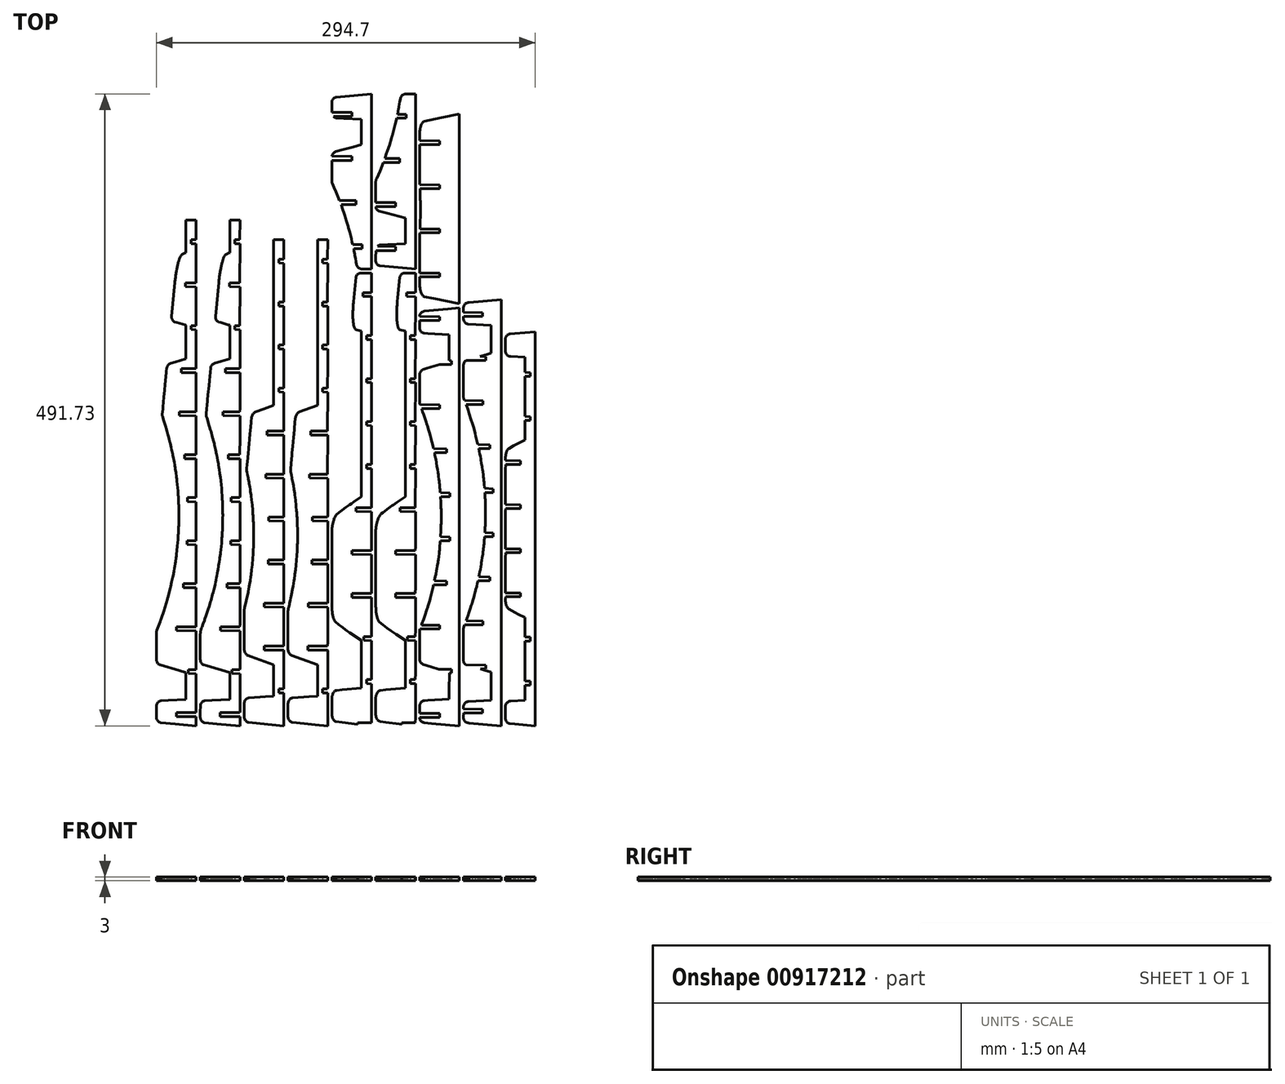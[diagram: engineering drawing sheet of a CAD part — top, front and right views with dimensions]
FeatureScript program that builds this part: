
annotation { "Feature Type Name" : "Feature", "Feature Type Description" : "" }
export const myFeature = defineFeature(function(context is Context, id is Id, definition is map)
    precondition{}
    {
        {
            var Q0;
            Q0=qCreatedBy(makeId("Top.planeOp"),FACE);
            var sketch = newSketch(context, id + "F0", { "sketchPlane" : qUnion([Q0])});
            skLineSegment(sketch, "E0", {"start": v(-124.7, 145.15) * mm, "end": v(-125.46, 145.15) * mm});
            skLineSegment(sketch, "E1", {"start": v(-125.46, 145.15) * mm, "end": v(-125.46, 144.59) * mm});
            skLineSegment(sketch, "E2", {"start": v(-125.46, 144.59) * mm, "end": v(-125.46, 143.96) * mm});
            skLineSegment(sketch, "E3", {"start": v(-125.46, 143.96) * mm, "end": v(-125.46, 143.45) * mm});
            skLineSegment(sketch, "E4", {"start": v(-125.46, 143.45) * mm, "end": v(-125.46, 142.94) * mm});
            skLineSegment(sketch, "E5", {"start": v(-125.46, 142.94) * mm, "end": v(-125.46, 134.23) * mm});
            skLineSegment(sketch, "E6", {"start": v(-125.46, 134.23) * mm, "end": v(-125.46, 132.49) * mm});
            skLineSegment(sketch, "E7", {"start": v(-125.46, 132.49) * mm, "end": v(-125.46, 131.98) * mm});
            skLineSegment(sketch, "E8", {"start": v(-125.46, 131.98) * mm, "end": v(-125.46, 131.33) * mm});
            skLineSegment(sketch, "E9", {"start": v(-125.46, 131.33) * mm, "end": v(-125.46, 130.23) * mm});
            skLineSegment(sketch, "E10", {"start": v(-125.46, 130.23) * mm, "end": v(-125.46, 129.43) * mm});
            skLineSegment(sketch, "E11", {"start": v(-125.46, 129.43) * mm, "end": v(-125.46, 128.37) * mm});
            skLineSegment(sketch, "E12", {"start": v(-125.46, 128.37) * mm, "end": v(-125.46, 126.95) * mm});
            skLineSegment(sketch, "E13", {"start": v(-125.46, 126.95) * mm, "end": v(-125.46, 124.97) * mm});
            skLineSegment(sketch, "E14", {"start": v(-125.46, 124.97) * mm, "end": v(-125.46, 122.08) * mm});
            skLineSegment(sketch, "E15", {"start": v(-125.46, 122.08) * mm, "end": v(-125.46, 119.96) * mm});
            skLineSegment(sketch, "E16", {"start": v(-125.46, 119.96) * mm, "end": v(-126.52, 119.45) * mm});
            skLineSegment(sketch, "E17", {"start": v(-126.52, 119.45) * mm, "end": v(-127.89, 118.8) * mm});
            skLineSegment(sketch, "E18", {"start": v(-127.89, 118.8) * mm, "end": v(-128.4, 118.56) * mm});
            skLineSegment(sketch, "E19", {"start": v(-128.4, 118.56) * mm, "end": v(-128.81, 118.25) * mm});
            skLineSegment(sketch, "E20", {"start": v(-128.81, 118.25) * mm, "end": v(-129.2, 117.8) * mm});
            skLineSegment(sketch, "E21", {"start": v(-129.2, 117.8) * mm, "end": v(-129.53, 117.3) * mm});
            skLineSegment(sketch, "E22", {"start": v(-129.53, 117.3) * mm, "end": v(-129.78, 116.82) * mm});
            skLineSegment(sketch, "E23", {"start": v(-129.78, 116.82) * mm, "end": v(-130.04, 116.28) * mm});
            skLineSegment(sketch, "E24", {"start": v(-130.04, 116.28) * mm, "end": v(-130.3, 115.64) * mm});
            skLineSegment(sketch, "E25", {"start": v(-130.3, 115.64) * mm, "end": v(-130.5, 115.14) * mm});
            skLineSegment(sketch, "E26", {"start": v(-130.5, 115.14) * mm, "end": v(-130.7, 114.6) * mm});
            skLineSegment(sketch, "E27", {"start": v(-130.7, 114.6) * mm, "end": v(-130.89, 114.02) * mm});
            skLineSegment(sketch, "E28", {"start": v(-130.89, 114.02) * mm, "end": v(-131.08, 113.4) * mm});
            skLineSegment(sketch, "E29", {"start": v(-131.08, 113.4) * mm, "end": v(-131.27, 112.77) * mm});
            skLineSegment(sketch, "E30", {"start": v(-131.27, 112.77) * mm, "end": v(-131.46, 112.1) * mm});
            skLineSegment(sketch, "E31", {"start": v(-131.46, 112.1) * mm, "end": v(-131.65, 111.39) * mm});
            skLineSegment(sketch, "E32", {"start": v(-131.65, 111.39) * mm, "end": v(-131.83, 110.65) * mm});
            skLineSegment(sketch, "E33", {"start": v(-131.83, 110.65) * mm, "end": v(-132, 109.9) * mm});
            skLineSegment(sketch, "E34", {"start": v(-132, 109.9) * mm, "end": v(-132.19, 109.1) * mm});
            skLineSegment(sketch, "E35", {"start": v(-132.19, 109.1) * mm, "end": v(-132.36, 108.3) * mm});
            skLineSegment(sketch, "E36", {"start": v(-132.36, 108.3) * mm, "end": v(-132.53, 107.46) * mm});
            skLineSegment(sketch, "E37", {"start": v(-132.53, 107.46) * mm, "end": v(-132.7, 106.6) * mm});
            skLineSegment(sketch, "E38", {"start": v(-132.7, 106.6) * mm, "end": v(-132.78, 106.09) * mm});
            skLineSegment(sketch, "E39", {"start": v(-132.78, 106.09) * mm, "end": v(-132.92, 105.3) * mm});
            skLineSegment(sketch, "E40", {"start": v(-132.92, 105.3) * mm, "end": v(-133.08, 104.38) * mm});
            skLineSegment(sketch, "E41", {"start": v(-133.08, 104.38) * mm, "end": v(-133.23, 103.45) * mm});
            skLineSegment(sketch, "E42", {"start": v(-133.23, 103.45) * mm, "end": v(-133.37, 102.5) * mm});
            skLineSegment(sketch, "E43", {"start": v(-133.37, 102.5) * mm, "end": v(-133.5, 101.54) * mm});
            skLineSegment(sketch, "E44", {"start": v(-133.5, 101.54) * mm, "end": v(-133.63, 100.57) * mm});
            skLineSegment(sketch, "E45", {"start": v(-133.63, 100.57) * mm, "end": v(-133.76, 99.59) * mm});
            skLineSegment(sketch, "E46", {"start": v(-133.76, 99.59) * mm, "end": v(-133.87, 98.6) * mm});
            skLineSegment(sketch, "E47", {"start": v(-133.87, 98.6) * mm, "end": v(-133.98, 97.6) * mm});
            skLineSegment(sketch, "E48", {"start": v(-133.98, 97.6) * mm, "end": v(-134.09, 96.6) * mm});
            skLineSegment(sketch, "E49", {"start": v(-134.09, 96.6) * mm, "end": v(-136.6, 70.19) * mm});
            skLineSegment(sketch, "E50", {"start": v(-136.6, 70.19) * mm, "end": v(-136.62, 69.65) * mm});
            skLineSegment(sketch, "E51", {"start": v(-136.62, 69.65) * mm, "end": v(-136.57, 69.12) * mm});
            skLineSegment(sketch, "E52", {"start": v(-136.57, 69.12) * mm, "end": v(-136.46, 68.6) * mm});
            skLineSegment(sketch, "E53", {"start": v(-136.46, 68.6) * mm, "end": v(-136.3, 68.1) * mm});
            skLineSegment(sketch, "E54", {"start": v(-136.3, 68.1) * mm, "end": v(-136.06, 67.62) * mm});
            skLineSegment(sketch, "E55", {"start": v(-136.06, 67.62) * mm, "end": v(-135.77, 67.18) * mm});
            skLineSegment(sketch, "E56", {"start": v(-135.77, 67.18) * mm, "end": v(-135.44, 66.78) * mm});
            skLineSegment(sketch, "E57", {"start": v(-135.44, 66.78) * mm, "end": v(-135.05, 66.43) * mm});
            skLineSegment(sketch, "E58", {"start": v(-135.05, 66.43) * mm, "end": v(-134.63, 66.14) * mm});
            skLineSegment(sketch, "E59", {"start": v(-134.63, 66.14) * mm, "end": v(-134.17, 65.9) * mm});
            skLineSegment(sketch, "E60", {"start": v(-134.17, 65.9) * mm, "end": v(-132.44, 65.42) * mm});
            skLineSegment(sketch, "E61", {"start": v(-132.44, 65.42) * mm, "end": v(-126, 63.58) * mm});
            skLineSegment(sketch, "E62", {"start": v(-126, 63.58) * mm, "end": v(-125.46, 63.43) * mm});
            skLineSegment(sketch, "E63", {"start": v(-125.46, 63.43) * mm, "end": v(-125.46, 51.97) * mm});
            skLineSegment(sketch, "E64", {"start": v(-125.46, 51.97) * mm, "end": v(-125.46, 40.78) * mm});
            skLineSegment(sketch, "E65", {"start": v(-125.46, 40.78) * mm, "end": v(-125.46, 40.22) * mm});
            skLineSegment(sketch, "E66", {"start": v(-125.46, 40.22) * mm, "end": v(-125.46, 39.7) * mm});
            skLineSegment(sketch, "E67", {"start": v(-125.46, 39.7) * mm, "end": v(-125.46, 37.14) * mm});
            skLineSegment(sketch, "E68", {"start": v(-125.46, 37.14) * mm, "end": v(-133.7, 34.73) * mm});
            skLineSegment(sketch, "E69", {"start": v(-133.7, 34.73) * mm, "end": v(-137.44, 33.64) * mm});
            skLineSegment(sketch, "E70", {"start": v(-137.44, 33.64) * mm, "end": v(-137.97, 33.43) * mm});
            skLineSegment(sketch, "E71", {"start": v(-137.97, 33.43) * mm, "end": v(-138.49, 33.15) * mm});
            skLineSegment(sketch, "E72", {"start": v(-138.49, 33.15) * mm, "end": v(-138.9, 32.84) * mm});
            skLineSegment(sketch, "E73", {"start": v(-138.9, 32.84) * mm, "end": v(-139.27, 32.48) * mm});
            skLineSegment(sketch, "E74", {"start": v(-139.27, 32.48) * mm, "end": v(-139.6, 32.08) * mm});
            skLineSegment(sketch, "E75", {"start": v(-139.6, 32.08) * mm, "end": v(-139.87, 31.64) * mm});
            skLineSegment(sketch, "E76", {"start": v(-139.87, 31.64) * mm, "end": v(-140.1, 31.16) * mm});
            skLineSegment(sketch, "E77", {"start": v(-140.1, 31.16) * mm, "end": v(-140.28, 30.66) * mm});
            skLineSegment(sketch, "E78", {"start": v(-140.28, 30.66) * mm, "end": v(-140.4, 30.14) * mm});
            skLineSegment(sketch, "E79", {"start": v(-140.4, 30.14) * mm, "end": v(-140.67, 27.42) * mm});
            skLineSegment(sketch, "E80", {"start": v(-140.67, 27.42) * mm, "end": v(-140.76, 26.56) * mm});
            skLineSegment(sketch, "E81", {"start": v(-140.76, 26.56) * mm, "end": v(-141.65, 17.18) * mm});
            skLineSegment(sketch, "E82", {"start": v(-141.65, 17.18) * mm, "end": v(-142.07, 12.73) * mm});
            skLineSegment(sketch, "E83", {"start": v(-142.07, 12.73) * mm, "end": v(-142.57, 7.47) * mm});
            skLineSegment(sketch, "E84", {"start": v(-142.57, 7.47) * mm, "end": v(-143.3, -0.2) * mm});
            skLineSegment(sketch, "E85", {"start": v(-143.3, -0.2) * mm, "end": v(-143.45, -1.78) * mm});
            skLineSegment(sketch, "E86", {"start": v(-143.45, -1.78) * mm, "end": v(-143.85, -5.9) * mm});
            skLineSegment(sketch, "E87", {"start": v(-143.85, -5.9) * mm, "end": v(-143.87, -6.48) * mm});
            skLineSegment(sketch, "E88", {"start": v(-143.87, -6.48) * mm, "end": v(-143.82, -7.05) * mm});
            skLineSegment(sketch, "E89", {"start": v(-143.82, -7.05) * mm, "end": v(-143.72, -7.61) * mm});
            skLineSegment(sketch, "E90", {"start": v(-143.72, -7.61) * mm, "end": v(-142.63, -10.9) * mm});
            skLineSegment(sketch, "E91", {"start": v(-142.63, -10.9) * mm, "end": v(-141.4, -14.92) * mm});
            skLineSegment(sketch, "E92", {"start": v(-141.4, -14.92) * mm, "end": v(-140.52, -17.8) * mm});
            skLineSegment(sketch, "E93", {"start": v(-140.52, -17.8) * mm, "end": v(-140.35, -18.38) * mm});
            skLineSegment(sketch, "E94", {"start": v(-140.35, -18.38) * mm, "end": v(-140.12, -19.13) * mm});
            skLineSegment(sketch, "E95", {"start": v(-140.12, -19.13) * mm, "end": v(-139.39, -21.85) * mm});
            skLineSegment(sketch, "E96", {"start": v(-139.39, -21.85) * mm, "end": v(-138.93, -23.53) * mm});
            skLineSegment(sketch, "E97", {"start": v(-138.93, -23.53) * mm, "end": v(-138.5, -25.17) * mm});
            skLineSegment(sketch, "E98", {"start": v(-138.5, -25.17) * mm, "end": v(-137.85, -27.69) * mm});
            skLineSegment(sketch, "E99", {"start": v(-137.85, -27.69) * mm, "end": v(-137.7, -28.36) * mm});
            skLineSegment(sketch, "E100", {"start": v(-137.7, -28.36) * mm, "end": v(-136.96, -31.55) * mm});
            skLineSegment(sketch, "E101", {"start": v(-136.96, -31.55) * mm, "end": v(-136.54, -33.4) * mm});
            skLineSegment(sketch, "E102", {"start": v(-136.54, -33.4) * mm, "end": v(-136.28, -34.58) * mm});
            skLineSegment(sketch, "E103", {"start": v(-136.28, -34.58) * mm, "end": v(-135.76, -36.97) * mm});
            skLineSegment(sketch, "E104", {"start": v(-135.76, -36.97) * mm, "end": v(-135.66, -37.5) * mm});
            skLineSegment(sketch, "E105", {"start": v(-135.66, -37.5) * mm, "end": v(-135.1, -40.43) * mm});
            skLineSegment(sketch, "E106", {"start": v(-135.1, -40.43) * mm, "end": v(-134.88, -41.68) * mm});
            skLineSegment(sketch, "E107", {"start": v(-134.88, -41.68) * mm, "end": v(-134.6, -43.22) * mm});
            skLineSegment(sketch, "E108", {"start": v(-134.6, -43.22) * mm, "end": v(-134.22, -45.37) * mm});
            skLineSegment(sketch, "E109", {"start": v(-134.22, -45.37) * mm, "end": v(-134.13, -45.9) * mm});
            skLineSegment(sketch, "E110", {"start": v(-134.13, -45.9) * mm, "end": v(-133.87, -47.46) * mm});
            skLineSegment(sketch, "E111", {"start": v(-133.87, -47.46) * mm, "end": v(-133.7, -48.54) * mm});
            skLineSegment(sketch, "E112", {"start": v(-133.7, -48.54) * mm, "end": v(-133.33, -51.15) * mm});
            skLineSegment(sketch, "E113", {"start": v(-133.33, -51.15) * mm, "end": v(-133.2, -52.07) * mm});
            skLineSegment(sketch, "E114", {"start": v(-133.2, -52.07) * mm, "end": v(-133, -53.68) * mm});
            skLineSegment(sketch, "E115", {"start": v(-133, -53.68) * mm, "end": v(-132.8, -55.14) * mm});
            skLineSegment(sketch, "E116", {"start": v(-132.8, -55.14) * mm, "end": v(-132.68, -56.12) * mm});
            skLineSegment(sketch, "E117", {"start": v(-132.68, -56.12) * mm, "end": v(-132.44, -58.07) * mm});
            skLineSegment(sketch, "E118", {"start": v(-132.44, -58.07) * mm, "end": v(-132.16, -60.6) * mm});
            skLineSegment(sketch, "E119", {"start": v(-132.16, -60.6) * mm, "end": v(-131.92, -63.17) * mm});
            skLineSegment(sketch, "E120", {"start": v(-131.92, -63.17) * mm, "end": v(-131.74, -65.47) * mm});
            skLineSegment(sketch, "E121", {"start": v(-131.74, -65.47) * mm, "end": v(-131.68, -66.12) * mm});
            skLineSegment(sketch, "E122", {"start": v(-131.68, -66.12) * mm, "end": v(-131.57, -67.73) * mm});
            skLineSegment(sketch, "E123", {"start": v(-131.57, -67.73) * mm, "end": v(-131.5, -68.63) * mm});
            skLineSegment(sketch, "E124", {"start": v(-131.5, -68.63) * mm, "end": v(-131.42, -69.96) * mm});
            skLineSegment(sketch, "E125", {"start": v(-131.42, -69.96) * mm, "end": v(-131.35, -71.06) * mm});
            skLineSegment(sketch, "E126", {"start": v(-131.35, -71.06) * mm, "end": v(-131.3, -72.16) * mm});
            skLineSegment(sketch, "E127", {"start": v(-131.3, -72.16) * mm, "end": v(-131.22, -73.44) * mm});
            skLineSegment(sketch, "E128", {"start": v(-131.22, -73.44) * mm, "end": v(-131.18, -74.35) * mm});
            skLineSegment(sketch, "E129", {"start": v(-131.18, -74.35) * mm, "end": v(-131.12, -75.78) * mm});
            skLineSegment(sketch, "E130", {"start": v(-131.12, -75.78) * mm, "end": v(-131.1, -76.53) * mm});
            skLineSegment(sketch, "E131", {"start": v(-131.1, -76.53) * mm, "end": v(-131.04, -78.07) * mm});
            skLineSegment(sketch, "E132", {"start": v(-131.04, -78.07) * mm, "end": v(-131.03, -78.7) * mm});
            skLineSegment(sketch, "E133", {"start": v(-131.03, -78.7) * mm, "end": v(-130.99, -80.35) * mm});
            skLineSegment(sketch, "E134", {"start": v(-130.99, -80.35) * mm, "end": v(-130.98, -80.9) * mm});
            skLineSegment(sketch, "E135", {"start": v(-130.98, -80.9) * mm, "end": v(-130.95, -82.6) * mm});
            skLineSegment(sketch, "E136", {"start": v(-130.95, -82.6) * mm, "end": v(-130.94, -84.85) * mm});
            skLineSegment(sketch, "E137", {"start": v(-130.94, -84.85) * mm, "end": v(-130.95, -87.1) * mm});
            skLineSegment(sketch, "E138", {"start": v(-130.95, -87.1) * mm, "end": v(-130.96, -87.62) * mm});
            skLineSegment(sketch, "E139", {"start": v(-130.96, -87.62) * mm, "end": v(-130.99, -89.35) * mm});
            skLineSegment(sketch, "E140", {"start": v(-130.99, -89.35) * mm, "end": v(-131, -89.94) * mm});
            skLineSegment(sketch, "E141", {"start": v(-131, -89.94) * mm, "end": v(-131.04, -91.62) * mm});
            skLineSegment(sketch, "E142", {"start": v(-131.04, -91.62) * mm, "end": v(-131.07, -92.32) * mm});
            skLineSegment(sketch, "E143", {"start": v(-131.07, -92.32) * mm, "end": v(-131.12, -93.92) * mm});
            skLineSegment(sketch, "E144", {"start": v(-131.12, -93.92) * mm, "end": v(-131.16, -94.77) * mm});
            skLineSegment(sketch, "E145", {"start": v(-131.16, -94.77) * mm, "end": v(-131.22, -96.25) * mm});
            skLineSegment(sketch, "E146", {"start": v(-131.22, -96.25) * mm, "end": v(-131.28, -97.32) * mm});
            skLineSegment(sketch, "E147", {"start": v(-131.28, -97.32) * mm, "end": v(-131.35, -98.63) * mm});
            skLineSegment(sketch, "E148", {"start": v(-131.35, -98.63) * mm, "end": v(-131.43, -99.97) * mm});
            skLineSegment(sketch, "E149", {"start": v(-131.43, -99.97) * mm, "end": v(-131.5, -101.07) * mm});
            skLineSegment(sketch, "E150", {"start": v(-131.5, -101.07) * mm, "end": v(-131.62, -102.75) * mm});
            skLineSegment(sketch, "E151", {"start": v(-131.62, -102.75) * mm, "end": v(-131.68, -103.57) * mm});
            skLineSegment(sketch, "E152", {"start": v(-131.68, -103.57) * mm, "end": v(-131.85, -105.68) * mm});
            skLineSegment(sketch, "E153", {"start": v(-131.85, -105.68) * mm, "end": v(-132.13, -108.79) * mm});
            skLineSegment(sketch, "E154", {"start": v(-132.13, -108.79) * mm, "end": v(-132.44, -111.63) * mm});
            skLineSegment(sketch, "E155", {"start": v(-132.44, -111.63) * mm, "end": v(-132.52, -112.3) * mm});
            skLineSegment(sketch, "E156", {"start": v(-132.52, -112.3) * mm, "end": v(-132.8, -114.55) * mm});
            skLineSegment(sketch, "E157", {"start": v(-132.8, -114.55) * mm, "end": v(-133.01, -116.15) * mm});
            skLineSegment(sketch, "E158", {"start": v(-133.01, -116.15) * mm, "end": v(-133.2, -117.62) * mm});
            skLineSegment(sketch, "E159", {"start": v(-133.2, -117.62) * mm, "end": v(-133.6, -120.39) * mm});
            skLineSegment(sketch, "E160", {"start": v(-133.6, -120.39) * mm, "end": v(-133.87, -122.24) * mm});
            skLineSegment(sketch, "E161", {"start": v(-133.87, -122.24) * mm, "end": v(-134.22, -124.33) * mm});
            skLineSegment(sketch, "E162", {"start": v(-134.22, -124.33) * mm, "end": v(-134.42, -125.45) * mm});
            skLineSegment(sketch, "E163", {"start": v(-134.42, -125.45) * mm, "end": v(-134.88, -128.02) * mm});
            skLineSegment(sketch, "E164", {"start": v(-134.88, -128.02) * mm, "end": v(-135.53, -131.53) * mm});
            skLineSegment(sketch, "E165", {"start": v(-135.53, -131.53) * mm, "end": v(-135.76, -132.73) * mm});
            skLineSegment(sketch, "E166", {"start": v(-135.76, -132.73) * mm, "end": v(-136.54, -136.3) * mm});
            skLineSegment(sketch, "E167", {"start": v(-136.54, -136.3) * mm, "end": v(-137.38, -139.96) * mm});
            skLineSegment(sketch, "E168", {"start": v(-137.38, -139.96) * mm, "end": v(-137.61, -141) * mm});
            skLineSegment(sketch, "E169", {"start": v(-137.61, -141) * mm, "end": v(-137.85, -142) * mm});
            skLineSegment(sketch, "E170", {"start": v(-137.85, -142) * mm, "end": v(-138.93, -146.16) * mm});
            skLineSegment(sketch, "E171", {"start": v(-138.93, -146.16) * mm, "end": v(-140.12, -150.57) * mm});
            skLineSegment(sketch, "E172", {"start": v(-140.12, -150.57) * mm, "end": v(-140.52, -151.9) * mm});
            skLineSegment(sketch, "E173", {"start": v(-140.52, -151.9) * mm, "end": v(-142.1, -157.07) * mm});
            skLineSegment(sketch, "E174", {"start": v(-142.1, -157.07) * mm, "end": v(-142.48, -158.32) * mm});
            skLineSegment(sketch, "E175", {"start": v(-142.48, -158.32) * mm, "end": v(-144.96, -165.6) * mm});
            skLineSegment(sketch, "E176", {"start": v(-144.96, -165.6) * mm, "end": v(-145.22, -166.35) * mm});
            skLineSegment(sketch, "E177", {"start": v(-145.22, -166.35) * mm, "end": v(-145.61, -167.36) * mm});
            skLineSegment(sketch, "E178", {"start": v(-145.61, -167.36) * mm, "end": v(-148.04, -173.74) * mm});
            skLineSegment(sketch, "E179", {"start": v(-148.04, -173.74) * mm, "end": v(-148.23, -174.3) * mm});
            skLineSegment(sketch, "E180", {"start": v(-148.23, -174.3) * mm, "end": v(-148.35, -174.88) * mm});
            skLineSegment(sketch, "E181", {"start": v(-148.35, -174.88) * mm, "end": v(-148.4, -175.48) * mm});
            skLineSegment(sketch, "E182", {"start": v(-148.4, -175.48) * mm, "end": v(-148.41, -178.9) * mm});
            skLineSegment(sketch, "E183", {"start": v(-148.41, -178.9) * mm, "end": v(-148.41, -182.48) * mm});
            skLineSegment(sketch, "E184", {"start": v(-148.41, -182.48) * mm, "end": v(-148.41, -189.59) * mm});
            skLineSegment(sketch, "E185", {"start": v(-148.41, -189.59) * mm, "end": v(-148.41, -196.75) * mm});
            skLineSegment(sketch, "E186", {"start": v(-148.41, -196.75) * mm, "end": v(-148.38, -197.3) * mm});
            skLineSegment(sketch, "E187", {"start": v(-148.38, -197.3) * mm, "end": v(-148.28, -197.86) * mm});
            skLineSegment(sketch, "E188", {"start": v(-148.28, -197.86) * mm, "end": v(-148.13, -198.39) * mm});
            skLineSegment(sketch, "E189", {"start": v(-148.13, -198.39) * mm, "end": v(-147.9, -198.89) * mm});
            skLineSegment(sketch, "E190", {"start": v(-147.9, -198.89) * mm, "end": v(-147.64, -199.36) * mm});
            skLineSegment(sketch, "E191", {"start": v(-147.64, -199.36) * mm, "end": v(-147.31, -199.79) * mm});
            skLineSegment(sketch, "E192", {"start": v(-147.31, -199.79) * mm, "end": v(-146.94, -200.17) * mm});
            skLineSegment(sketch, "E193", {"start": v(-146.94, -200.17) * mm, "end": v(-146.53, -200.5) * mm});
            skLineSegment(sketch, "E194", {"start": v(-146.53, -200.5) * mm, "end": v(-146.08, -200.76) * mm});
            skLineSegment(sketch, "E195", {"start": v(-146.08, -200.76) * mm, "end": v(-145.6, -200.96) * mm});
            skLineSegment(sketch, "E196", {"start": v(-145.6, -200.96) * mm, "end": v(-130.6, -205.33) * mm});
            skLineSegment(sketch, "E197", {"start": v(-130.6, -205.33) * mm, "end": v(-125.46, -206.84) * mm});
            skLineSegment(sketch, "E198", {"start": v(-125.46, -206.84) * mm, "end": v(-125.46, -208.47) * mm});
            skLineSegment(sketch, "E199", {"start": v(-125.46, -208.47) * mm, "end": v(-125.46, -210.91) * mm});
            skLineSegment(sketch, "E200", {"start": v(-125.46, -210.91) * mm, "end": v(-125.46, -220.58) * mm});
            skLineSegment(sketch, "E201", {"start": v(-125.46, -220.58) * mm, "end": v(-125.46, -227.75) * mm});
            skLineSegment(sketch, "E202", {"start": v(-125.46, -227.75) * mm, "end": v(-139.25, -228.54) * mm});
            skLineSegment(sketch, "E203", {"start": v(-139.25, -228.54) * mm, "end": v(-144.62, -228.84) * mm});
            skLineSegment(sketch, "E204", {"start": v(-144.62, -228.84) * mm, "end": v(-145.14, -228.9) * mm});
            skLineSegment(sketch, "E205", {"start": v(-145.14, -228.9) * mm, "end": v(-145.64, -229.03) * mm});
            skLineSegment(sketch, "E206", {"start": v(-145.64, -229.03) * mm, "end": v(-146.13, -229.24) * mm});
            skLineSegment(sketch, "E207", {"start": v(-146.13, -229.24) * mm, "end": v(-146.58, -229.5) * mm});
            skLineSegment(sketch, "E208", {"start": v(-146.58, -229.5) * mm, "end": v(-147, -229.83) * mm});
            skLineSegment(sketch, "E209", {"start": v(-147, -229.83) * mm, "end": v(-147.37, -230.21) * mm});
            skLineSegment(sketch, "E210", {"start": v(-147.37, -230.21) * mm, "end": v(-147.7, -230.64) * mm});
            skLineSegment(sketch, "E211", {"start": v(-147.7, -230.64) * mm, "end": v(-147.97, -231.12) * mm});
            skLineSegment(sketch, "E212", {"start": v(-147.97, -231.12) * mm, "end": v(-148.17, -231.62) * mm});
            skLineSegment(sketch, "E213", {"start": v(-148.17, -231.62) * mm, "end": v(-148.32, -232.15) * mm});
            skLineSegment(sketch, "E214", {"start": v(-148.32, -232.15) * mm, "end": v(-148.4, -232.7) * mm});
            skLineSegment(sketch, "E215", {"start": v(-148.4, -232.7) * mm, "end": v(-148.41, -237.11) * mm});
            skLineSegment(sketch, "E216", {"start": v(-148.41, -237.11) * mm, "end": v(-148.41, -241.73) * mm});
            skLineSegment(sketch, "E217", {"start": v(-148.41, -241.73) * mm, "end": v(-148.38, -242.28) * mm});
            skLineSegment(sketch, "E218", {"start": v(-148.38, -242.28) * mm, "end": v(-148.28, -242.82) * mm});
            skLineSegment(sketch, "E219", {"start": v(-148.28, -242.82) * mm, "end": v(-148.1, -243.34) * mm});
            skLineSegment(sketch, "E220", {"start": v(-148.1, -243.34) * mm, "end": v(-147.88, -243.84) * mm});
            skLineSegment(sketch, "E221", {"start": v(-147.88, -243.84) * mm, "end": v(-147.59, -244.3) * mm});
            skLineSegment(sketch, "E222", {"start": v(-147.59, -244.3) * mm, "end": v(-147.24, -244.7) * mm});
            skLineSegment(sketch, "E223", {"start": v(-147.24, -244.7) * mm, "end": v(-146.85, -245.07) * mm});
            skLineSegment(sketch, "E224", {"start": v(-146.85, -245.07) * mm, "end": v(-146.41, -245.38) * mm});
            skLineSegment(sketch, "E225", {"start": v(-146.41, -245.38) * mm, "end": v(-145.94, -245.62) * mm});
            skLineSegment(sketch, "E226", {"start": v(-145.94, -245.62) * mm, "end": v(-145.45, -245.8) * mm});
            skLineSegment(sketch, "E227", {"start": v(-145.45, -245.8) * mm, "end": v(-144.93, -245.9) * mm});
            skLineSegment(sketch, "E228", {"start": v(-144.93, -245.9) * mm, "end": v(-133.71, -246.92) * mm});
            skLineSegment(sketch, "E229", {"start": v(-133.71, -246.92) * mm, "end": v(-117.46, -248.41) * mm});
            skLineSegment(sketch, "E230", {"start": v(-117.46, -248.41) * mm, "end": v(-117.46, -241.24) * mm});
            skLineSegment(sketch, "E231", {"start": v(-117.46, -241.24) * mm, "end": v(-132.94, -241.09) * mm});
            skLineSegment(sketch, "E232", {"start": v(-132.94, -241.09) * mm, "end": v(-132.94, -238.09) * mm});
            skLineSegment(sketch, "E233", {"start": v(-132.94, -238.09) * mm, "end": v(-117.61, -238.09) * mm});
            skLineSegment(sketch, "E234", {"start": v(-117.61, -238.09) * mm, "end": v(-117.46, -219.57) * mm});
            skLineSegment(sketch, "E235", {"start": v(-117.46, -219.57) * mm, "end": v(-117.46, -218.58) * mm});
            skLineSegment(sketch, "E236", {"start": v(-117.46, -218.58) * mm, "end": v(-117.46, -207.78) * mm});
            skLineSegment(sketch, "E237", {"start": v(-117.46, -207.78) * mm, "end": v(-123.78, -207.63) * mm});
            skLineSegment(sketch, "E238", {"start": v(-123.78, -207.63) * mm, "end": v(-123.78, -204.63) * mm});
            skLineSegment(sketch, "E239", {"start": v(-123.78, -204.63) * mm, "end": v(-117.61, -204.63) * mm});
            skLineSegment(sketch, "E240", {"start": v(-117.61, -204.63) * mm, "end": v(-117.46, -203.27) * mm});
            skLineSegment(sketch, "E241", {"start": v(-117.46, -203.27) * mm, "end": v(-117.46, -192.24) * mm});
            skLineSegment(sketch, "E242", {"start": v(-117.46, -192.24) * mm, "end": v(-117.46, -190.68) * mm});
            skLineSegment(sketch, "E243", {"start": v(-117.46, -190.68) * mm, "end": v(-117.46, -181.81) * mm});
            skLineSegment(sketch, "E244", {"start": v(-117.46, -181.81) * mm, "end": v(-117.46, -180.12) * mm});
            skLineSegment(sketch, "E245", {"start": v(-117.46, -180.12) * mm, "end": v(-117.46, -174.32) * mm});
            skLineSegment(sketch, "E246", {"start": v(-117.46, -174.32) * mm, "end": v(-132.72, -174.17) * mm});
            skLineSegment(sketch, "E247", {"start": v(-132.72, -174.17) * mm, "end": v(-132.72, -171.17) * mm});
            skLineSegment(sketch, "E248", {"start": v(-132.72, -171.17) * mm, "end": v(-117.61, -171.17) * mm});
            skLineSegment(sketch, "E249", {"start": v(-117.61, -171.17) * mm, "end": v(-117.46, -165.08) * mm});
            skLineSegment(sketch, "E250", {"start": v(-117.46, -165.08) * mm, "end": v(-117.46, -163.27) * mm});
            skLineSegment(sketch, "E251", {"start": v(-117.46, -163.27) * mm, "end": v(-117.46, -158.23) * mm});
            skLineSegment(sketch, "E252", {"start": v(-117.46, -158.23) * mm, "end": v(-117.46, -156.4) * mm});
            skLineSegment(sketch, "E253", {"start": v(-117.46, -156.4) * mm, "end": v(-117.46, -152.13) * mm});
            skLineSegment(sketch, "E254", {"start": v(-117.46, -152.13) * mm, "end": v(-117.46, -150.3) * mm});
            skLineSegment(sketch, "E255", {"start": v(-117.46, -150.3) * mm, "end": v(-117.46, -146.65) * mm});
            skLineSegment(sketch, "E256", {"start": v(-117.46, -146.65) * mm, "end": v(-117.46, -144.82) * mm});
            skLineSegment(sketch, "E257", {"start": v(-117.46, -144.82) * mm, "end": v(-117.46, -141.67) * mm});
            skLineSegment(sketch, "E258", {"start": v(-117.46, -141.67) * mm, "end": v(-117.46, -140.87) * mm});
            skLineSegment(sketch, "E259", {"start": v(-117.46, -140.87) * mm, "end": v(-127.5, -140.72) * mm});
            skLineSegment(sketch, "E260", {"start": v(-127.5, -140.72) * mm, "end": v(-127.5, -137.72) * mm});
            skLineSegment(sketch, "E261", {"start": v(-127.5, -137.72) * mm, "end": v(-117.61, -137.72) * mm});
            skLineSegment(sketch, "E262", {"start": v(-117.61, -137.72) * mm, "end": v(-117.46, -137.13) * mm});
            skLineSegment(sketch, "E263", {"start": v(-117.46, -137.13) * mm, "end": v(-117.46, -135.32) * mm});
            skLineSegment(sketch, "E264", {"start": v(-117.46, -135.32) * mm, "end": v(-117.46, -132.94) * mm});
            skLineSegment(sketch, "E265", {"start": v(-117.46, -132.94) * mm, "end": v(-117.46, -131.16) * mm});
            skLineSegment(sketch, "E266", {"start": v(-117.46, -131.16) * mm, "end": v(-117.46, -129.06) * mm});
            skLineSegment(sketch, "E267", {"start": v(-117.46, -129.06) * mm, "end": v(-117.46, -127.3) * mm});
            skLineSegment(sketch, "E268", {"start": v(-117.46, -127.3) * mm, "end": v(-117.46, -125.44) * mm});
            skLineSegment(sketch, "E269", {"start": v(-117.46, -125.44) * mm, "end": v(-117.46, -123.7) * mm});
            skLineSegment(sketch, "E270", {"start": v(-117.46, -123.7) * mm, "end": v(-117.46, -122.05) * mm});
            skLineSegment(sketch, "E271", {"start": v(-117.46, -122.05) * mm, "end": v(-117.46, -120.33) * mm});
            skLineSegment(sketch, "E272", {"start": v(-117.46, -120.33) * mm, "end": v(-117.46, -118.85) * mm});
            skLineSegment(sketch, "E273", {"start": v(-117.46, -118.85) * mm, "end": v(-117.46, -117.14) * mm});
            skLineSegment(sketch, "E274", {"start": v(-117.46, -117.14) * mm, "end": v(-117.46, -115.81) * mm});
            skLineSegment(sketch, "E275", {"start": v(-117.46, -115.81) * mm, "end": v(-117.46, -114.13) * mm});
            skLineSegment(sketch, "E276", {"start": v(-117.46, -114.13) * mm, "end": v(-117.46, -112.92) * mm});
            skLineSegment(sketch, "E277", {"start": v(-117.46, -112.92) * mm, "end": v(-117.46, -111.25) * mm});
            skLineSegment(sketch, "E278", {"start": v(-117.46, -111.25) * mm, "end": v(-117.46, -110.16) * mm});
            skLineSegment(sketch, "E279", {"start": v(-117.46, -110.16) * mm, "end": v(-117.46, -108.5) * mm});
            skLineSegment(sketch, "E280", {"start": v(-117.46, -108.5) * mm, "end": v(-117.46, -107.5) * mm});
            skLineSegment(sketch, "E281", {"start": v(-117.46, -107.5) * mm, "end": v(-124.73, -107.26) * mm});
            skLineSegment(sketch, "E282", {"start": v(-124.73, -107.26) * mm, "end": v(-124.73, -104.26) * mm});
            skLineSegment(sketch, "E283", {"start": v(-124.73, -104.26) * mm, "end": v(-117.61, -104.26) * mm});
            skLineSegment(sketch, "E284", {"start": v(-117.61, -104.26) * mm, "end": v(-117.46, -103.3) * mm});
            skLineSegment(sketch, "E285", {"start": v(-117.46, -103.3) * mm, "end": v(-117.46, -102.44) * mm});
            skLineSegment(sketch, "E286", {"start": v(-117.46, -102.44) * mm, "end": v(-117.46, -100.82) * mm});
            skLineSegment(sketch, "E287", {"start": v(-117.46, -100.82) * mm, "end": v(-117.46, -100.01) * mm});
            skLineSegment(sketch, "E288", {"start": v(-117.46, -100.01) * mm, "end": v(-117.46, -98.4) * mm});
            skLineSegment(sketch, "E289", {"start": v(-117.46, -98.4) * mm, "end": v(-117.46, -97.64) * mm});
            skLineSegment(sketch, "E290", {"start": v(-117.46, -97.64) * mm, "end": v(-117.46, -96.04) * mm});
            skLineSegment(sketch, "E291", {"start": v(-117.46, -96.04) * mm, "end": v(-117.46, -95.32) * mm});
            skLineSegment(sketch, "E292", {"start": v(-117.46, -95.32) * mm, "end": v(-117.46, -93.72) * mm});
            skLineSegment(sketch, "E293", {"start": v(-117.46, -93.72) * mm, "end": v(-117.46, -93.03) * mm});
            skLineSegment(sketch, "E294", {"start": v(-117.46, -93.03) * mm, "end": v(-117.46, -91.43) * mm});
            skLineSegment(sketch, "E295", {"start": v(-117.46, -91.43) * mm, "end": v(-117.46, -90.76) * mm});
            skLineSegment(sketch, "E296", {"start": v(-117.46, -90.76) * mm, "end": v(-117.46, -89.17) * mm});
            skLineSegment(sketch, "E297", {"start": v(-117.46, -89.17) * mm, "end": v(-117.46, -88.51) * mm});
            skLineSegment(sketch, "E298", {"start": v(-117.46, -88.51) * mm, "end": v(-117.46, -86.92) * mm});
            skLineSegment(sketch, "E299", {"start": v(-117.46, -86.92) * mm, "end": v(-117.46, -86.27) * mm});
            skLineSegment(sketch, "E300", {"start": v(-117.46, -86.27) * mm, "end": v(-117.46, -84.68) * mm});
            skLineSegment(sketch, "E301", {"start": v(-117.46, -84.68) * mm, "end": v(-117.46, -84.03) * mm});
            skLineSegment(sketch, "E302", {"start": v(-117.46, -84.03) * mm, "end": v(-117.46, -82.44) * mm});
            skLineSegment(sketch, "E303", {"start": v(-117.46, -82.44) * mm, "end": v(-117.46, -81.78) * mm});
            skLineSegment(sketch, "E304", {"start": v(-117.46, -81.78) * mm, "end": v(-117.46, -80.18) * mm});
            skLineSegment(sketch, "E305", {"start": v(-117.46, -80.18) * mm, "end": v(-117.46, -79.52) * mm});
            skLineSegment(sketch, "E306", {"start": v(-117.46, -79.52) * mm, "end": v(-117.46, -77.91) * mm});
            skLineSegment(sketch, "E307", {"start": v(-117.46, -77.91) * mm, "end": v(-117.46, -77.23) * mm});
            skLineSegment(sketch, "E308", {"start": v(-117.46, -77.23) * mm, "end": v(-117.46, -75.61) * mm});
            skLineSegment(sketch, "E309", {"start": v(-117.46, -75.61) * mm, "end": v(-117.46, -74) * mm});
            skLineSegment(sketch, "E310", {"start": v(-117.46, -74) * mm, "end": v(-124.41, -73.8) * mm});
            skLineSegment(sketch, "E311", {"start": v(-124.41, -73.8) * mm, "end": v(-124.41, -70.8) * mm});
            skLineSegment(sketch, "E312", {"start": v(-124.41, -70.8) * mm, "end": v(-117.61, -70.8) * mm});
            skLineSegment(sketch, "E313", {"start": v(-117.61, -70.8) * mm, "end": v(-117.46, -69.28) * mm});
            skLineSegment(sketch, "E314", {"start": v(-117.46, -69.28) * mm, "end": v(-117.46, -67.76) * mm});
            skLineSegment(sketch, "E315", {"start": v(-117.46, -67.76) * mm, "end": v(-117.46, -66.27) * mm});
            skLineSegment(sketch, "E316", {"start": v(-117.46, -66.27) * mm, "end": v(-117.46, -64.82) * mm});
            skLineSegment(sketch, "E317", {"start": v(-117.46, -64.82) * mm, "end": v(-117.46, -63.4) * mm});
            skLineSegment(sketch, "E318", {"start": v(-117.46, -63.4) * mm, "end": v(-117.46, -62.04) * mm});
            skLineSegment(sketch, "E319", {"start": v(-117.46, -62.04) * mm, "end": v(-117.46, -40.5) * mm});
            skLineSegment(sketch, "E320", {"start": v(-117.46, -40.5) * mm, "end": v(-126.58, -40.35) * mm});
            skLineSegment(sketch, "E321", {"start": v(-126.58, -40.35) * mm, "end": v(-126.58, -37.35) * mm});
            skLineSegment(sketch, "E322", {"start": v(-126.58, -37.35) * mm, "end": v(-117.61, -37.35) * mm});
            skLineSegment(sketch, "E323", {"start": v(-117.61, -37.35) * mm, "end": v(-117.46, -26.41) * mm});
            skLineSegment(sketch, "E324", {"start": v(-117.46, -26.41) * mm, "end": v(-117.46, -23.6) * mm});
            skLineSegment(sketch, "E325", {"start": v(-117.46, -23.6) * mm, "end": v(-117.46, -20.76) * mm});
            skLineSegment(sketch, "E326", {"start": v(-117.46, -20.76) * mm, "end": v(-117.46, -17.93) * mm});
            skLineSegment(sketch, "E327", {"start": v(-117.46, -17.93) * mm, "end": v(-117.46, -15.1) * mm});
            skLineSegment(sketch, "E328", {"start": v(-117.46, -15.1) * mm, "end": v(-117.46, -12.3) * mm});
            skLineSegment(sketch, "E329", {"start": v(-117.46, -12.3) * mm, "end": v(-117.46, -9.53) * mm});
            skLineSegment(sketch, "E330", {"start": v(-117.46, -9.53) * mm, "end": v(-117.46, -7.05) * mm});
            skLineSegment(sketch, "E331", {"start": v(-117.46, -7.05) * mm, "end": v(-130.63, -6.9) * mm});
            skLineSegment(sketch, "E332", {"start": v(-130.63, -6.9) * mm, "end": v(-130.63, -3.9) * mm});
            skLineSegment(sketch, "E333", {"start": v(-130.63, -3.9) * mm, "end": v(-117.61, -3.9) * mm});
            skLineSegment(sketch, "E334", {"start": v(-117.61, -3.9) * mm, "end": v(-117.46, -1.45) * mm});
            skLineSegment(sketch, "E335", {"start": v(-117.46, -1.45) * mm, "end": v(-117.46, 1.14) * mm});
            skLineSegment(sketch, "E336", {"start": v(-117.46, 1.14) * mm, "end": v(-117.46, 3.73) * mm});
            skLineSegment(sketch, "E337", {"start": v(-117.46, 3.73) * mm, "end": v(-117.46, 4.26) * mm});
            skLineSegment(sketch, "E338", {"start": v(-117.46, 4.26) * mm, "end": v(-117.46, 4.8) * mm});
            skLineSegment(sketch, "E339", {"start": v(-117.46, 4.8) * mm, "end": v(-117.46, 5.4) * mm});
            skLineSegment(sketch, "E340", {"start": v(-117.46, 5.4) * mm, "end": v(-117.46, 6) * mm});
            skLineSegment(sketch, "E341", {"start": v(-117.46, 6) * mm, "end": v(-117.46, 6.58) * mm});
            skLineSegment(sketch, "E342", {"start": v(-117.46, 6.58) * mm, "end": v(-117.46, 9.1) * mm});
            skLineSegment(sketch, "E343", {"start": v(-117.46, 9.1) * mm, "end": v(-117.46, 11.54) * mm});
            skLineSegment(sketch, "E344", {"start": v(-117.46, 11.54) * mm, "end": v(-117.46, 13.91) * mm});
            skLineSegment(sketch, "E345", {"start": v(-117.46, 13.91) * mm, "end": v(-117.46, 16.2) * mm});
            skLineSegment(sketch, "E346", {"start": v(-117.46, 16.2) * mm, "end": v(-117.46, 18.4) * mm});
            skLineSegment(sketch, "E347", {"start": v(-117.46, 18.4) * mm, "end": v(-117.46, 20.53) * mm});
            skLineSegment(sketch, "E348", {"start": v(-117.46, 20.53) * mm, "end": v(-117.46, 22.56) * mm});
            skLineSegment(sketch, "E349", {"start": v(-117.46, 22.56) * mm, "end": v(-117.46, 24.5) * mm});
            skLineSegment(sketch, "E350", {"start": v(-117.46, 24.5) * mm, "end": v(-117.46, 26.36) * mm});
            skLineSegment(sketch, "E351", {"start": v(-117.46, 26.36) * mm, "end": v(-129.04, 26.56) * mm});
            skLineSegment(sketch, "E352", {"start": v(-129.04, 26.56) * mm, "end": v(-129.04, 29.56) * mm});
            skLineSegment(sketch, "E353", {"start": v(-129.04, 29.56) * mm, "end": v(-117.61, 29.56) * mm});
            skLineSegment(sketch, "E354", {"start": v(-117.61, 29.56) * mm, "end": v(-117.46, 59.86) * mm});
            skLineSegment(sketch, "E355", {"start": v(-117.46, 59.86) * mm, "end": v(-121.46, 60.01) * mm});
            skLineSegment(sketch, "E356", {"start": v(-121.46, 60.01) * mm, "end": v(-121.46, 63.01) * mm});
            skLineSegment(sketch, "E357", {"start": v(-121.46, 63.01) * mm, "end": v(-117.61, 63.01) * mm});
            skLineSegment(sketch, "E358", {"start": v(-117.61, 63.01) * mm, "end": v(-117.46, 93.32) * mm});
            skLineSegment(sketch, "E359", {"start": v(-117.46, 93.32) * mm, "end": v(-125.85, 93.47) * mm});
            skLineSegment(sketch, "E360", {"start": v(-125.85, 93.47) * mm, "end": v(-125.85, 96.47) * mm});
            skLineSegment(sketch, "E361", {"start": v(-125.85, 96.47) * mm, "end": v(-117.61, 96.47) * mm});
            skLineSegment(sketch, "E362", {"start": v(-117.61, 96.47) * mm, "end": v(-117.46, 126.77) * mm});
            skLineSegment(sketch, "E363", {"start": v(-117.46, 126.77) * mm, "end": v(-121.46, 126.92) * mm});
            skLineSegment(sketch, "E364", {"start": v(-121.46, 126.92) * mm, "end": v(-121.46, 129.92) * mm});
            skLineSegment(sketch, "E365", {"start": v(-121.46, 129.92) * mm, "end": v(-117.61, 129.92) * mm});
            skLineSegment(sketch, "E366", {"start": v(-117.61, 129.92) * mm, "end": v(-117.46, 145.15) * mm});
            skLineSegment(sketch, "E367", {"start": v(-117.46, 145.15) * mm, "end": v(-121.04, 145.15) * mm});
            skLineSegment(sketch, "E368", {"start": v(-121.04, 145.15) * mm, "end": v(-124.7, 145.15) * mm});
            skLineSegment(sketch, "E369", {"start": v(-83.34, 145.15) * mm, "end": v(-90.58, 145.15) * mm});
            skLineSegment(sketch, "E370", {"start": v(-90.58, 145.15) * mm, "end": v(-91.34, 145.15) * mm});
            skLineSegment(sketch, "E371", {"start": v(-91.34, 145.15) * mm, "end": v(-91.34, 144.59) * mm});
            skLineSegment(sketch, "E372", {"start": v(-91.34, 144.59) * mm, "end": v(-91.34, 143.96) * mm});
            skLineSegment(sketch, "E373", {"start": v(-91.34, 143.96) * mm, "end": v(-91.34, 143.45) * mm});
            skLineSegment(sketch, "E374", {"start": v(-91.34, 143.45) * mm, "end": v(-91.34, 142.87) * mm});
            skLineSegment(sketch, "E375", {"start": v(-91.34, 142.87) * mm, "end": v(-91.34, 142.24) * mm});
            skLineSegment(sketch, "E376", {"start": v(-91.34, 142.24) * mm, "end": v(-91.34, 119.96) * mm});
            skLineSegment(sketch, "E377", {"start": v(-91.34, 119.96) * mm, "end": v(-92.4, 119.45) * mm});
            skLineSegment(sketch, "E378", {"start": v(-92.4, 119.45) * mm, "end": v(-92.9, 119.21) * mm});
            skLineSegment(sketch, "E379", {"start": v(-92.9, 119.21) * mm, "end": v(-94.27, 118.56) * mm});
            skLineSegment(sketch, "E380", {"start": v(-94.27, 118.56) * mm, "end": v(-94.7, 118.24) * mm});
            skLineSegment(sketch, "E381", {"start": v(-94.7, 118.24) * mm, "end": v(-95.08, 117.8) * mm});
            skLineSegment(sketch, "E382", {"start": v(-95.08, 117.8) * mm, "end": v(-95.4, 117.31) * mm});
            skLineSegment(sketch, "E383", {"start": v(-95.4, 117.31) * mm, "end": v(-95.65, 116.83) * mm});
            skLineSegment(sketch, "E384", {"start": v(-95.65, 116.83) * mm, "end": v(-95.92, 116.26) * mm});
            skLineSegment(sketch, "E385", {"start": v(-95.92, 116.26) * mm, "end": v(-96.17, 115.67) * mm});
            skLineSegment(sketch, "E386", {"start": v(-96.17, 115.67) * mm, "end": v(-96.37, 115.16) * mm});
            skLineSegment(sketch, "E387", {"start": v(-96.37, 115.16) * mm, "end": v(-96.56, 114.62) * mm});
            skLineSegment(sketch, "E388", {"start": v(-96.56, 114.62) * mm, "end": v(-96.76, 114.05) * mm});
            skLineSegment(sketch, "E389", {"start": v(-96.76, 114.05) * mm, "end": v(-96.95, 113.44) * mm});
            skLineSegment(sketch, "E390", {"start": v(-96.95, 113.44) * mm, "end": v(-97.14, 112.8) * mm});
            skLineSegment(sketch, "E391", {"start": v(-97.14, 112.8) * mm, "end": v(-97.33, 112.12) * mm});
            skLineSegment(sketch, "E392", {"start": v(-97.33, 112.12) * mm, "end": v(-97.52, 111.42) * mm});
            skLineSegment(sketch, "E393", {"start": v(-97.52, 111.42) * mm, "end": v(-97.7, 110.68) * mm});
            skLineSegment(sketch, "E394", {"start": v(-97.7, 110.68) * mm, "end": v(-97.88, 109.92) * mm});
            skLineSegment(sketch, "E395", {"start": v(-97.88, 109.92) * mm, "end": v(-98.06, 109.13) * mm});
            skLineSegment(sketch, "E396", {"start": v(-98.06, 109.13) * mm, "end": v(-98.23, 108.32) * mm});
            skLineSegment(sketch, "E397", {"start": v(-98.23, 108.32) * mm, "end": v(-98.4, 107.48) * mm});
            skLineSegment(sketch, "E398", {"start": v(-98.4, 107.48) * mm, "end": v(-98.56, 106.63) * mm});
            skLineSegment(sketch, "E399", {"start": v(-98.56, 106.63) * mm, "end": v(-98.66, 106.12) * mm});
            skLineSegment(sketch, "E400", {"start": v(-98.66, 106.12) * mm, "end": v(-98.81, 105.22) * mm});
            skLineSegment(sketch, "E401", {"start": v(-98.81, 105.22) * mm, "end": v(-98.97, 104.32) * mm});
            skLineSegment(sketch, "E402", {"start": v(-98.97, 104.32) * mm, "end": v(-99.11, 103.4) * mm});
            skLineSegment(sketch, "E403", {"start": v(-99.11, 103.4) * mm, "end": v(-99.25, 102.45) * mm});
            skLineSegment(sketch, "E404", {"start": v(-99.25, 102.45) * mm, "end": v(-99.39, 101.5) * mm});
            skLineSegment(sketch, "E405", {"start": v(-99.39, 101.5) * mm, "end": v(-99.52, 100.53) * mm});
            skLineSegment(sketch, "E406", {"start": v(-99.52, 100.53) * mm, "end": v(-99.64, 99.56) * mm});
            skLineSegment(sketch, "E407", {"start": v(-99.64, 99.56) * mm, "end": v(-99.75, 98.58) * mm});
            skLineSegment(sketch, "E408", {"start": v(-99.75, 98.58) * mm, "end": v(-99.86, 97.59) * mm});
            skLineSegment(sketch, "E409", {"start": v(-99.86, 97.59) * mm, "end": v(-99.96, 96.6) * mm});
            skLineSegment(sketch, "E410", {"start": v(-99.96, 96.6) * mm, "end": v(-102.48, 70.2) * mm});
            skLineSegment(sketch, "E411", {"start": v(-102.48, 70.2) * mm, "end": v(-102.5, 69.67) * mm});
            skLineSegment(sketch, "E412", {"start": v(-102.5, 69.67) * mm, "end": v(-102.45, 69.13) * mm});
            skLineSegment(sketch, "E413", {"start": v(-102.45, 69.13) * mm, "end": v(-102.34, 68.61) * mm});
            skLineSegment(sketch, "E414", {"start": v(-102.34, 68.61) * mm, "end": v(-102.17, 68.1) * mm});
            skLineSegment(sketch, "E415", {"start": v(-102.17, 68.1) * mm, "end": v(-101.94, 67.63) * mm});
            skLineSegment(sketch, "E416", {"start": v(-101.94, 67.63) * mm, "end": v(-101.65, 67.2) * mm});
            skLineSegment(sketch, "E417", {"start": v(-101.65, 67.2) * mm, "end": v(-101.31, 66.8) * mm});
            skLineSegment(sketch, "E418", {"start": v(-101.31, 66.8) * mm, "end": v(-100.93, 66.45) * mm});
            skLineSegment(sketch, "E419", {"start": v(-100.93, 66.45) * mm, "end": v(-100.5, 66.15) * mm});
            skLineSegment(sketch, "E420", {"start": v(-100.5, 66.15) * mm, "end": v(-100.05, 65.92) * mm});
            skLineSegment(sketch, "E421", {"start": v(-100.05, 65.92) * mm, "end": v(-98.32, 65.42) * mm});
            skLineSegment(sketch, "E422", {"start": v(-98.32, 65.42) * mm, "end": v(-92.54, 63.78) * mm});
            skLineSegment(sketch, "E423", {"start": v(-92.54, 63.78) * mm, "end": v(-91.87, 63.58) * mm});
            skLineSegment(sketch, "E424", {"start": v(-91.87, 63.58) * mm, "end": v(-91.34, 63.43) * mm});
            skLineSegment(sketch, "E425", {"start": v(-91.34, 63.43) * mm, "end": v(-91.34, 51.97) * mm});
            skLineSegment(sketch, "E426", {"start": v(-91.34, 51.97) * mm, "end": v(-91.34, 40.84) * mm});
            skLineSegment(sketch, "E427", {"start": v(-91.34, 40.84) * mm, "end": v(-91.34, 40.3) * mm});
            skLineSegment(sketch, "E428", {"start": v(-91.34, 40.3) * mm, "end": v(-91.34, 39.77) * mm});
            skLineSegment(sketch, "E429", {"start": v(-91.34, 39.77) * mm, "end": v(-91.34, 37.14) * mm});
            skLineSegment(sketch, "E430", {"start": v(-91.34, 37.14) * mm, "end": v(-97.85, 35.25) * mm});
            skLineSegment(sketch, "E431", {"start": v(-97.85, 35.25) * mm, "end": v(-103.31, 33.66) * mm});
            skLineSegment(sketch, "E432", {"start": v(-103.31, 33.66) * mm, "end": v(-103.8, 33.48) * mm});
            skLineSegment(sketch, "E433", {"start": v(-103.8, 33.48) * mm, "end": v(-104.36, 33.17) * mm});
            skLineSegment(sketch, "E434", {"start": v(-104.36, 33.17) * mm, "end": v(-104.78, 32.86) * mm});
            skLineSegment(sketch, "E435", {"start": v(-104.78, 32.86) * mm, "end": v(-105.25, 32.38) * mm});
            skLineSegment(sketch, "E436", {"start": v(-105.25, 32.38) * mm, "end": v(-105.57, 31.97) * mm});
            skLineSegment(sketch, "E437", {"start": v(-105.57, 31.97) * mm, "end": v(-105.83, 31.51) * mm});
            skLineSegment(sketch, "E438", {"start": v(-105.83, 31.51) * mm, "end": v(-106.04, 31.03) * mm});
            skLineSegment(sketch, "E439", {"start": v(-106.04, 31.03) * mm, "end": v(-106.2, 30.52) * mm});
            skLineSegment(sketch, "E440", {"start": v(-106.2, 30.52) * mm, "end": v(-106.3, 30) * mm});
            skLineSegment(sketch, "E441", {"start": v(-106.3, 30) * mm, "end": v(-107.23, 20.31) * mm});
            skLineSegment(sketch, "E442", {"start": v(-107.23, 20.31) * mm, "end": v(-107.6, 16.3) * mm});
            skLineSegment(sketch, "E443", {"start": v(-107.6, 16.3) * mm, "end": v(-108.28, 9.24) * mm});
            skLineSegment(sketch, "E444", {"start": v(-108.28, 9.24) * mm, "end": v(-109.08, 0.84) * mm});
            skLineSegment(sketch, "E445", {"start": v(-109.08, 0.84) * mm, "end": v(-109.28, -1.25) * mm});
            skLineSegment(sketch, "E446", {"start": v(-109.28, -1.25) * mm, "end": v(-109.72, -5.9) * mm});
            skLineSegment(sketch, "E447", {"start": v(-109.72, -5.9) * mm, "end": v(-109.74, -6.48) * mm});
            skLineSegment(sketch, "E448", {"start": v(-109.74, -6.48) * mm, "end": v(-109.7, -7.05) * mm});
            skLineSegment(sketch, "E449", {"start": v(-109.7, -7.05) * mm, "end": v(-109.6, -7.61) * mm});
            skLineSegment(sketch, "E450", {"start": v(-109.6, -7.61) * mm, "end": v(-109.2, -8.8) * mm});
            skLineSegment(sketch, "E451", {"start": v(-109.2, -8.8) * mm, "end": v(-108.46, -11.05) * mm});
            skLineSegment(sketch, "E452", {"start": v(-108.46, -11.05) * mm, "end": v(-107.97, -12.62) * mm});
            skLineSegment(sketch, "E453", {"start": v(-107.97, -12.62) * mm, "end": v(-106.4, -17.8) * mm});
            skLineSegment(sketch, "E454", {"start": v(-106.4, -17.8) * mm, "end": v(-106, -19.13) * mm});
            skLineSegment(sketch, "E455", {"start": v(-106, -19.13) * mm, "end": v(-104.81, -23.53) * mm});
            skLineSegment(sketch, "E456", {"start": v(-104.81, -23.53) * mm, "end": v(-103.73, -27.69) * mm});
            skLineSegment(sketch, "E457", {"start": v(-103.73, -27.69) * mm, "end": v(-103.49, -28.7) * mm});
            skLineSegment(sketch, "E458", {"start": v(-103.49, -28.7) * mm, "end": v(-103.25, -29.73) * mm});
            skLineSegment(sketch, "E459", {"start": v(-103.25, -29.73) * mm, "end": v(-102.42, -33.4) * mm});
            skLineSegment(sketch, "E460", {"start": v(-102.42, -33.4) * mm, "end": v(-101.64, -36.97) * mm});
            skLineSegment(sketch, "E461", {"start": v(-101.64, -36.97) * mm, "end": v(-101.5, -37.7) * mm});
            skLineSegment(sketch, "E462", {"start": v(-101.5, -37.7) * mm, "end": v(-100.75, -41.68) * mm});
            skLineSegment(sketch, "E463", {"start": v(-100.75, -41.68) * mm, "end": v(-100.3, -44.25) * mm});
            skLineSegment(sketch, "E464", {"start": v(-100.3, -44.25) * mm, "end": v(-100.1, -45.37) * mm});
            skLineSegment(sketch, "E465", {"start": v(-100.1, -45.37) * mm, "end": v(-99.74, -47.46) * mm});
            skLineSegment(sketch, "E466", {"start": v(-99.74, -47.46) * mm, "end": v(-99.54, -48.82) * mm});
            skLineSegment(sketch, "E467", {"start": v(-99.54, -48.82) * mm, "end": v(-99.08, -52.07) * mm});
            skLineSegment(sketch, "E468", {"start": v(-99.08, -52.07) * mm, "end": v(-98.89, -53.55) * mm});
            skLineSegment(sketch, "E469", {"start": v(-98.89, -53.55) * mm, "end": v(-98.68, -55.14) * mm});
            skLineSegment(sketch, "E470", {"start": v(-98.68, -55.14) * mm, "end": v(-98.4, -57.4) * mm});
            skLineSegment(sketch, "E471", {"start": v(-98.4, -57.4) * mm, "end": v(-98.32, -58.07) * mm});
            skLineSegment(sketch, "E472", {"start": v(-98.32, -58.07) * mm, "end": v(-98.04, -60.6) * mm});
            skLineSegment(sketch, "E473", {"start": v(-98.04, -60.6) * mm, "end": v(-97.77, -63.54) * mm});
            skLineSegment(sketch, "E474", {"start": v(-97.77, -63.54) * mm, "end": v(-97.56, -66.12) * mm});
            skLineSegment(sketch, "E475", {"start": v(-97.56, -66.12) * mm, "end": v(-97.5, -66.95) * mm});
            skLineSegment(sketch, "E476", {"start": v(-97.5, -66.95) * mm, "end": v(-97.38, -68.63) * mm});
            skLineSegment(sketch, "E477", {"start": v(-97.38, -68.63) * mm, "end": v(-97.31, -69.72) * mm});
            skLineSegment(sketch, "E478", {"start": v(-97.31, -69.72) * mm, "end": v(-97.23, -71.06) * mm});
            skLineSegment(sketch, "E479", {"start": v(-97.23, -71.06) * mm, "end": v(-97.16, -72.38) * mm});
            skLineSegment(sketch, "E480", {"start": v(-97.16, -72.38) * mm, "end": v(-97.1, -73.44) * mm});
            skLineSegment(sketch, "E481", {"start": v(-97.1, -73.44) * mm, "end": v(-97.04, -74.92) * mm});
            skLineSegment(sketch, "E482", {"start": v(-97.04, -74.92) * mm, "end": v(-97, -75.78) * mm});
            skLineSegment(sketch, "E483", {"start": v(-97, -75.78) * mm, "end": v(-96.94, -77.38) * mm});
            skLineSegment(sketch, "E484", {"start": v(-96.94, -77.38) * mm, "end": v(-96.92, -78.07) * mm});
            skLineSegment(sketch, "E485", {"start": v(-96.92, -78.07) * mm, "end": v(-96.88, -79.76) * mm});
            skLineSegment(sketch, "E486", {"start": v(-96.88, -79.76) * mm, "end": v(-96.86, -80.35) * mm});
            skLineSegment(sketch, "E487", {"start": v(-96.86, -80.35) * mm, "end": v(-96.84, -82.08) * mm});
            skLineSegment(sketch, "E488", {"start": v(-96.84, -82.08) * mm, "end": v(-96.83, -82.6) * mm});
            skLineSegment(sketch, "E489", {"start": v(-96.83, -82.6) * mm, "end": v(-96.82, -84.35) * mm});
            skLineSegment(sketch, "E490", {"start": v(-96.82, -84.35) * mm, "end": v(-96.83, -86.59) * mm});
            skLineSegment(sketch, "E491", {"start": v(-96.83, -86.59) * mm, "end": v(-96.86, -88.8) * mm});
            skLineSegment(sketch, "E492", {"start": v(-96.86, -88.8) * mm, "end": v(-96.86, -89.35) * mm});
            skLineSegment(sketch, "E493", {"start": v(-96.86, -89.35) * mm, "end": v(-96.9, -90.99) * mm});
            skLineSegment(sketch, "E494", {"start": v(-96.9, -90.99) * mm, "end": v(-96.92, -91.62) * mm});
            skLineSegment(sketch, "E495", {"start": v(-96.92, -91.62) * mm, "end": v(-96.97, -93.17) * mm});
            skLineSegment(sketch, "E496", {"start": v(-96.97, -93.17) * mm, "end": v(-97, -93.92) * mm});
            skLineSegment(sketch, "E497", {"start": v(-97, -93.92) * mm, "end": v(-97.06, -95.35) * mm});
            skLineSegment(sketch, "E498", {"start": v(-97.06, -95.35) * mm, "end": v(-97.1, -96.25) * mm});
            skLineSegment(sketch, "E499", {"start": v(-97.1, -96.25) * mm, "end": v(-97.17, -97.54) * mm});
            skLineSegment(sketch, "E500", {"start": v(-97.17, -97.54) * mm, "end": v(-97.23, -98.63) * mm});
            skLineSegment(sketch, "E501", {"start": v(-97.23, -98.63) * mm, "end": v(-97.3, -99.74) * mm});
            skLineSegment(sketch, "E502", {"start": v(-97.3, -99.74) * mm, "end": v(-97.38, -101.07) * mm});
            skLineSegment(sketch, "E503", {"start": v(-97.38, -101.07) * mm, "end": v(-97.44, -101.97) * mm});
            skLineSegment(sketch, "E504", {"start": v(-97.44, -101.97) * mm, "end": v(-97.56, -103.57) * mm});
            skLineSegment(sketch, "E505", {"start": v(-97.56, -103.57) * mm, "end": v(-97.61, -104.22) * mm});
            skLineSegment(sketch, "E506", {"start": v(-97.61, -104.22) * mm, "end": v(-97.77, -106.16) * mm});
            skLineSegment(sketch, "E507", {"start": v(-97.77, -106.16) * mm, "end": v(-98.01, -108.84) * mm});
            skLineSegment(sketch, "E508", {"start": v(-98.01, -108.84) * mm, "end": v(-98.27, -111.2) * mm});
            skLineSegment(sketch, "E509", {"start": v(-98.27, -111.2) * mm, "end": v(-98.56, -113.57) * mm});
            skLineSegment(sketch, "E510", {"start": v(-98.56, -113.57) * mm, "end": v(-98.68, -114.55) * mm});
            skLineSegment(sketch, "E511", {"start": v(-98.68, -114.55) * mm, "end": v(-98.87, -116.02) * mm});
            skLineSegment(sketch, "E512", {"start": v(-98.87, -116.02) * mm, "end": v(-99.08, -117.62) * mm});
            skLineSegment(sketch, "E513", {"start": v(-99.08, -117.62) * mm, "end": v(-99.21, -118.54) * mm});
            skLineSegment(sketch, "E514", {"start": v(-99.21, -118.54) * mm, "end": v(-99.54, -120.87) * mm});
            skLineSegment(sketch, "E515", {"start": v(-99.54, -120.87) * mm, "end": v(-99.74, -122.24) * mm});
            skLineSegment(sketch, "E516", {"start": v(-99.74, -122.24) * mm, "end": v(-100, -123.8) * mm});
            skLineSegment(sketch, "E517", {"start": v(-100, -123.8) * mm, "end": v(-100.1, -124.33) * mm});
            skLineSegment(sketch, "E518", {"start": v(-100.1, -124.33) * mm, "end": v(-100.48, -126.47) * mm});
            skLineSegment(sketch, "E519", {"start": v(-100.48, -126.47) * mm, "end": v(-100.75, -128.02) * mm});
            skLineSegment(sketch, "E520", {"start": v(-100.75, -128.02) * mm, "end": v(-100.99, -129.27) * mm});
            skLineSegment(sketch, "E521", {"start": v(-100.99, -129.27) * mm, "end": v(-101.5, -132) * mm});
            skLineSegment(sketch, "E522", {"start": v(-101.5, -132) * mm, "end": v(-101.64, -132.73) * mm});
            skLineSegment(sketch, "E523", {"start": v(-101.64, -132.73) * mm, "end": v(-102.16, -135.11) * mm});
            skLineSegment(sketch, "E524", {"start": v(-102.16, -135.11) * mm, "end": v(-102.42, -136.3) * mm});
            skLineSegment(sketch, "E525", {"start": v(-102.42, -136.3) * mm, "end": v(-102.84, -138.14) * mm});
            skLineSegment(sketch, "E526", {"start": v(-102.84, -138.14) * mm, "end": v(-103.49, -141) * mm});
            skLineSegment(sketch, "E527", {"start": v(-103.49, -141) * mm, "end": v(-103.73, -142) * mm});
            skLineSegment(sketch, "E528", {"start": v(-103.73, -142) * mm, "end": v(-104.38, -144.53) * mm});
            skLineSegment(sketch, "E529", {"start": v(-104.38, -144.53) * mm, "end": v(-104.81, -146.16) * mm});
            skLineSegment(sketch, "E530", {"start": v(-104.81, -146.16) * mm, "end": v(-105.27, -147.85) * mm});
            skLineSegment(sketch, "E531", {"start": v(-105.27, -147.85) * mm, "end": v(-106, -150.57) * mm});
            skLineSegment(sketch, "E532", {"start": v(-106, -150.57) * mm, "end": v(-106.22, -151.32) * mm});
            skLineSegment(sketch, "E533", {"start": v(-106.22, -151.32) * mm, "end": v(-106.4, -151.9) * mm});
            skLineSegment(sketch, "E534", {"start": v(-106.4, -151.9) * mm, "end": v(-107.27, -154.78) * mm});
            skLineSegment(sketch, "E535", {"start": v(-107.27, -154.78) * mm, "end": v(-108.36, -158.32) * mm});
            skLineSegment(sketch, "E536", {"start": v(-108.36, -158.32) * mm, "end": v(-109.64, -162.1) * mm});
            skLineSegment(sketch, "E537", {"start": v(-109.64, -162.1) * mm, "end": v(-110.84, -165.6) * mm});
            skLineSegment(sketch, "E538", {"start": v(-110.84, -165.6) * mm, "end": v(-111.1, -166.35) * mm});
            skLineSegment(sketch, "E539", {"start": v(-111.1, -166.35) * mm, "end": v(-112.15, -169.07) * mm});
            skLineSegment(sketch, "E540", {"start": v(-112.15, -169.07) * mm, "end": v(-112.93, -171.2) * mm});
            skLineSegment(sketch, "E541", {"start": v(-112.93, -171.2) * mm, "end": v(-113.35, -172.25) * mm});
            skLineSegment(sketch, "E542", {"start": v(-113.35, -172.25) * mm, "end": v(-113.92, -173.74) * mm});
            skLineSegment(sketch, "E543", {"start": v(-113.92, -173.74) * mm, "end": v(-114.1, -174.3) * mm});
            skLineSegment(sketch, "E544", {"start": v(-114.1, -174.3) * mm, "end": v(-114.22, -174.8) * mm});
            skLineSegment(sketch, "E545", {"start": v(-114.22, -174.8) * mm, "end": v(-114.28, -175.4) * mm});
            skLineSegment(sketch, "E546", {"start": v(-114.28, -175.4) * mm, "end": v(-114.29, -177.8) * mm});
            skLineSegment(sketch, "E547", {"start": v(-114.29, -177.8) * mm, "end": v(-114.29, -178.9) * mm});
            skLineSegment(sketch, "E548", {"start": v(-114.29, -178.9) * mm, "end": v(-114.29, -184.5) * mm});
            skLineSegment(sketch, "E549", {"start": v(-114.29, -184.5) * mm, "end": v(-114.29, -189.59) * mm});
            skLineSegment(sketch, "E550", {"start": v(-114.29, -189.59) * mm, "end": v(-114.29, -191.99) * mm});
            skLineSegment(sketch, "E551", {"start": v(-114.29, -191.99) * mm, "end": v(-114.29, -196.75) * mm});
            skLineSegment(sketch, "E552", {"start": v(-114.29, -196.75) * mm, "end": v(-114.26, -197.3) * mm});
            skLineSegment(sketch, "E553", {"start": v(-114.26, -197.3) * mm, "end": v(-114.16, -197.86) * mm});
            skLineSegment(sketch, "E554", {"start": v(-114.16, -197.86) * mm, "end": v(-114, -198.39) * mm});
            skLineSegment(sketch, "E555", {"start": v(-114, -198.39) * mm, "end": v(-113.79, -198.89) * mm});
            skLineSegment(sketch, "E556", {"start": v(-113.79, -198.89) * mm, "end": v(-113.51, -199.36) * mm});
            skLineSegment(sketch, "E557", {"start": v(-113.51, -199.36) * mm, "end": v(-113.19, -199.79) * mm});
            skLineSegment(sketch, "E558", {"start": v(-113.19, -199.79) * mm, "end": v(-112.82, -200.17) * mm});
            skLineSegment(sketch, "E559", {"start": v(-112.82, -200.17) * mm, "end": v(-112.4, -200.5) * mm});
            skLineSegment(sketch, "E560", {"start": v(-112.4, -200.5) * mm, "end": v(-111.96, -200.76) * mm});
            skLineSegment(sketch, "E561", {"start": v(-111.96, -200.76) * mm, "end": v(-111.49, -200.96) * mm});
            skLineSegment(sketch, "E562", {"start": v(-111.49, -200.96) * mm, "end": v(-109.43, -201.57) * mm});
            skLineSegment(sketch, "E563", {"start": v(-109.43, -201.57) * mm, "end": v(-91.34, -206.84) * mm});
            skLineSegment(sketch, "E564", {"start": v(-91.34, -206.84) * mm, "end": v(-91.34, -207.86) * mm});
            skLineSegment(sketch, "E565", {"start": v(-91.34, -207.86) * mm, "end": v(-91.34, -208.47) * mm});
            skLineSegment(sketch, "E566", {"start": v(-91.34, -208.47) * mm, "end": v(-91.34, -215.15) * mm});
            skLineSegment(sketch, "E567", {"start": v(-91.34, -215.15) * mm, "end": v(-91.34, -220.58) * mm});
            skLineSegment(sketch, "E568", {"start": v(-91.34, -220.58) * mm, "end": v(-91.34, -223.19) * mm});
            skLineSegment(sketch, "E569", {"start": v(-91.34, -223.19) * mm, "end": v(-91.34, -227.75) * mm});
            skLineSegment(sketch, "E570", {"start": v(-91.34, -227.75) * mm, "end": v(-105.13, -228.54) * mm});
            skLineSegment(sketch, "E571", {"start": v(-105.13, -228.54) * mm, "end": v(-110.5, -228.84) * mm});
            skLineSegment(sketch, "E572", {"start": v(-110.5, -228.84) * mm, "end": v(-111.02, -228.9) * mm});
            skLineSegment(sketch, "E573", {"start": v(-111.02, -228.9) * mm, "end": v(-111.52, -229.03) * mm});
            skLineSegment(sketch, "E574", {"start": v(-111.52, -229.03) * mm, "end": v(-112, -229.24) * mm});
            skLineSegment(sketch, "E575", {"start": v(-112, -229.24) * mm, "end": v(-112.46, -229.5) * mm});
            skLineSegment(sketch, "E576", {"start": v(-112.46, -229.5) * mm, "end": v(-112.88, -229.83) * mm});
            skLineSegment(sketch, "E577", {"start": v(-112.88, -229.83) * mm, "end": v(-113.25, -230.21) * mm});
            skLineSegment(sketch, "E578", {"start": v(-113.25, -230.21) * mm, "end": v(-113.57, -230.64) * mm});
            skLineSegment(sketch, "E579", {"start": v(-113.57, -230.64) * mm, "end": v(-113.84, -231.12) * mm});
            skLineSegment(sketch, "E580", {"start": v(-113.84, -231.12) * mm, "end": v(-114.05, -231.62) * mm});
            skLineSegment(sketch, "E581", {"start": v(-114.05, -231.62) * mm, "end": v(-114.2, -232.15) * mm});
            skLineSegment(sketch, "E582", {"start": v(-114.2, -232.15) * mm, "end": v(-114.27, -232.7) * mm});
            skLineSegment(sketch, "E583", {"start": v(-114.27, -232.7) * mm, "end": v(-114.29, -237.6) * mm});
            skLineSegment(sketch, "E584", {"start": v(-114.29, -237.6) * mm, "end": v(-114.29, -241.73) * mm});
            skLineSegment(sketch, "E585", {"start": v(-114.29, -241.73) * mm, "end": v(-114.26, -242.28) * mm});
            skLineSegment(sketch, "E586", {"start": v(-114.26, -242.28) * mm, "end": v(-114.15, -242.82) * mm});
            skLineSegment(sketch, "E587", {"start": v(-114.15, -242.82) * mm, "end": v(-113.99, -243.34) * mm});
            skLineSegment(sketch, "E588", {"start": v(-113.99, -243.34) * mm, "end": v(-113.75, -243.84) * mm});
            skLineSegment(sketch, "E589", {"start": v(-113.75, -243.84) * mm, "end": v(-113.46, -244.3) * mm});
            skLineSegment(sketch, "E590", {"start": v(-113.46, -244.3) * mm, "end": v(-113.12, -244.7) * mm});
            skLineSegment(sketch, "E591", {"start": v(-113.12, -244.7) * mm, "end": v(-112.72, -245.07) * mm});
            skLineSegment(sketch, "E592", {"start": v(-112.72, -245.07) * mm, "end": v(-112.29, -245.38) * mm});
            skLineSegment(sketch, "E593", {"start": v(-112.29, -245.38) * mm, "end": v(-111.82, -245.62) * mm});
            skLineSegment(sketch, "E594", {"start": v(-111.82, -245.62) * mm, "end": v(-111.32, -245.8) * mm});
            skLineSegment(sketch, "E595", {"start": v(-111.32, -245.8) * mm, "end": v(-110.81, -245.9) * mm});
            skLineSegment(sketch, "E596", {"start": v(-110.81, -245.9) * mm, "end": v(-101.52, -246.77) * mm});
            skLineSegment(sketch, "E597", {"start": v(-101.52, -246.77) * mm, "end": v(-83.34, -248.41) * mm});
            skLineSegment(sketch, "E598", {"start": v(-83.34, -248.41) * mm, "end": v(-83.34, -241.24) * mm});
            skLineSegment(sketch, "E599", {"start": v(-83.34, -241.24) * mm, "end": v(-98.82, -241.09) * mm});
            skLineSegment(sketch, "E600", {"start": v(-98.82, -241.09) * mm, "end": v(-98.82, -238.09) * mm});
            skLineSegment(sketch, "E601", {"start": v(-98.82, -238.09) * mm, "end": v(-83.5, -238.09) * mm});
            skLineSegment(sketch, "E602", {"start": v(-83.5, -238.09) * mm, "end": v(-83.34, -237.26) * mm});
            skLineSegment(sketch, "E603", {"start": v(-83.34, -237.26) * mm, "end": v(-83.34, -218.58) * mm});
            skLineSegment(sketch, "E604", {"start": v(-83.34, -218.58) * mm, "end": v(-83.34, -217.52) * mm});
            skLineSegment(sketch, "E605", {"start": v(-83.34, -217.52) * mm, "end": v(-83.34, -207.78) * mm});
            skLineSegment(sketch, "E606", {"start": v(-83.34, -207.78) * mm, "end": v(-89.66, -207.63) * mm});
            skLineSegment(sketch, "E607", {"start": v(-89.66, -207.63) * mm, "end": v(-89.66, -204.63) * mm});
            skLineSegment(sketch, "E608", {"start": v(-89.66, -204.63) * mm, "end": v(-83.5, -204.63) * mm});
            skLineSegment(sketch, "E609", {"start": v(-83.5, -204.63) * mm, "end": v(-83.34, -203.27) * mm});
            skLineSegment(sketch, "E610", {"start": v(-83.34, -203.27) * mm, "end": v(-83.34, -201.84) * mm});
            skLineSegment(sketch, "E611", {"start": v(-83.34, -201.84) * mm, "end": v(-83.34, -190.68) * mm});
            skLineSegment(sketch, "E612", {"start": v(-83.34, -190.68) * mm, "end": v(-83.34, -189.03) * mm});
            skLineSegment(sketch, "E613", {"start": v(-83.34, -189.03) * mm, "end": v(-83.34, -180.12) * mm});
            skLineSegment(sketch, "E614", {"start": v(-83.34, -180.12) * mm, "end": v(-83.34, -178.34) * mm});
            skLineSegment(sketch, "E615", {"start": v(-83.34, -178.34) * mm, "end": v(-83.34, -174.32) * mm});
            skLineSegment(sketch, "E616", {"start": v(-83.34, -174.32) * mm, "end": v(-98.6, -174.17) * mm});
            skLineSegment(sketch, "E617", {"start": v(-98.6, -174.17) * mm, "end": v(-98.6, -171.17) * mm});
            skLineSegment(sketch, "E618", {"start": v(-98.6, -171.17) * mm, "end": v(-83.5, -171.17) * mm});
            skLineSegment(sketch, "E619", {"start": v(-83.5, -171.17) * mm, "end": v(-83.34, -169.24) * mm});
            skLineSegment(sketch, "E620", {"start": v(-83.34, -169.24) * mm, "end": v(-83.34, -163.27) * mm});
            skLineSegment(sketch, "E621", {"start": v(-83.34, -163.27) * mm, "end": v(-83.34, -161.38) * mm});
            skLineSegment(sketch, "E622", {"start": v(-83.34, -161.38) * mm, "end": v(-83.34, -156.4) * mm});
            skLineSegment(sketch, "E623", {"start": v(-83.34, -156.4) * mm, "end": v(-83.34, -154.5) * mm});
            skLineSegment(sketch, "E624", {"start": v(-83.34, -154.5) * mm, "end": v(-83.34, -150.3) * mm});
            skLineSegment(sketch, "E625", {"start": v(-83.34, -150.3) * mm, "end": v(-83.34, -148.4) * mm});
            skLineSegment(sketch, "E626", {"start": v(-83.34, -148.4) * mm, "end": v(-83.34, -144.82) * mm});
            skLineSegment(sketch, "E627", {"start": v(-83.34, -144.82) * mm, "end": v(-83.34, -142.93) * mm});
            skLineSegment(sketch, "E628", {"start": v(-83.34, -142.93) * mm, "end": v(-83.34, -140.87) * mm});
            skLineSegment(sketch, "E629", {"start": v(-83.34, -140.87) * mm, "end": v(-93.38, -140.72) * mm});
            skLineSegment(sketch, "E630", {"start": v(-93.38, -140.72) * mm, "end": v(-93.38, -137.72) * mm});
            skLineSegment(sketch, "E631", {"start": v(-93.38, -137.72) * mm, "end": v(-83.5, -137.72) * mm});
            skLineSegment(sketch, "E632", {"start": v(-83.5, -137.72) * mm, "end": v(-83.34, -135.32) * mm});
            skLineSegment(sketch, "E633", {"start": v(-83.34, -135.32) * mm, "end": v(-83.34, -133.47) * mm});
            skLineSegment(sketch, "E634", {"start": v(-83.34, -133.47) * mm, "end": v(-83.34, -131.16) * mm});
            skLineSegment(sketch, "E635", {"start": v(-83.34, -131.16) * mm, "end": v(-83.34, -129.33) * mm});
            skLineSegment(sketch, "E636", {"start": v(-83.34, -129.33) * mm, "end": v(-83.34, -127.3) * mm});
            skLineSegment(sketch, "E637", {"start": v(-83.34, -127.3) * mm, "end": v(-83.34, -125.5) * mm});
            skLineSegment(sketch, "E638", {"start": v(-83.34, -125.5) * mm, "end": v(-83.34, -123.7) * mm});
            skLineSegment(sketch, "E639", {"start": v(-83.34, -123.7) * mm, "end": v(-83.34, -121.92) * mm});
            skLineSegment(sketch, "E640", {"start": v(-83.34, -121.92) * mm, "end": v(-83.34, -120.33) * mm});
            skLineSegment(sketch, "E641", {"start": v(-83.34, -120.33) * mm, "end": v(-83.34, -118.57) * mm});
            skLineSegment(sketch, "E642", {"start": v(-83.34, -118.57) * mm, "end": v(-83.34, -117.14) * mm});
            skLineSegment(sketch, "E643", {"start": v(-83.34, -117.14) * mm, "end": v(-83.34, -115.4) * mm});
            skLineSegment(sketch, "E644", {"start": v(-83.34, -115.4) * mm, "end": v(-83.34, -114.13) * mm});
            skLineSegment(sketch, "E645", {"start": v(-83.34, -114.13) * mm, "end": v(-83.34, -112.41) * mm});
            skLineSegment(sketch, "E646", {"start": v(-83.34, -112.41) * mm, "end": v(-83.34, -111.25) * mm});
            skLineSegment(sketch, "E647", {"start": v(-83.34, -111.25) * mm, "end": v(-83.34, -109.56) * mm});
            skLineSegment(sketch, "E648", {"start": v(-83.34, -109.56) * mm, "end": v(-83.34, -108.5) * mm});
            skLineSegment(sketch, "E649", {"start": v(-83.34, -108.5) * mm, "end": v(-83.34, -107.41) * mm});
            skLineSegment(sketch, "E650", {"start": v(-83.34, -107.41) * mm, "end": v(-90.6, -107.26) * mm});
            skLineSegment(sketch, "E651", {"start": v(-90.6, -107.26) * mm, "end": v(-90.6, -104.26) * mm});
            skLineSegment(sketch, "E652", {"start": v(-90.6, -104.26) * mm, "end": v(-83.5, -104.26) * mm});
            skLineSegment(sketch, "E653", {"start": v(-83.5, -104.26) * mm, "end": v(-83.34, -103.3) * mm});
            skLineSegment(sketch, "E654", {"start": v(-83.34, -103.3) * mm, "end": v(-83.34, -101.65) * mm});
            skLineSegment(sketch, "E655", {"start": v(-83.34, -101.65) * mm, "end": v(-83.34, -100.82) * mm});
            skLineSegment(sketch, "E656", {"start": v(-83.34, -100.82) * mm, "end": v(-83.34, -99.18) * mm});
            skLineSegment(sketch, "E657", {"start": v(-83.34, -99.18) * mm, "end": v(-83.34, -98.4) * mm});
            skLineSegment(sketch, "E658", {"start": v(-83.34, -98.4) * mm, "end": v(-83.34, -96.78) * mm});
            skLineSegment(sketch, "E659", {"start": v(-83.34, -96.78) * mm, "end": v(-83.34, -96.04) * mm});
            skLineSegment(sketch, "E660", {"start": v(-83.34, -96.04) * mm, "end": v(-83.34, -94.43) * mm});
            skLineSegment(sketch, "E661", {"start": v(-83.34, -94.43) * mm, "end": v(-83.34, -93.72) * mm});
            skLineSegment(sketch, "E662", {"start": v(-83.34, -93.72) * mm, "end": v(-83.34, -92.11) * mm});
            skLineSegment(sketch, "E663", {"start": v(-83.34, -92.11) * mm, "end": v(-83.34, -91.43) * mm});
            skLineSegment(sketch, "E664", {"start": v(-83.34, -91.43) * mm, "end": v(-83.34, -89.83) * mm});
            skLineSegment(sketch, "E665", {"start": v(-83.34, -89.83) * mm, "end": v(-83.34, -89.17) * mm});
            skLineSegment(sketch, "E666", {"start": v(-83.34, -89.17) * mm, "end": v(-83.34, -87.57) * mm});
            skLineSegment(sketch, "E667", {"start": v(-83.34, -87.57) * mm, "end": v(-83.34, -86.92) * mm});
            skLineSegment(sketch, "E668", {"start": v(-83.34, -86.92) * mm, "end": v(-83.34, -85.33) * mm});
            skLineSegment(sketch, "E669", {"start": v(-83.34, -85.33) * mm, "end": v(-83.34, -84.68) * mm});
            skLineSegment(sketch, "E670", {"start": v(-83.34, -84.68) * mm, "end": v(-83.34, -83.09) * mm});
            skLineSegment(sketch, "E671", {"start": v(-83.34, -83.09) * mm, "end": v(-83.34, -82.44) * mm});
            skLineSegment(sketch, "E672", {"start": v(-83.34, -82.44) * mm, "end": v(-83.34, -80.84) * mm});
            skLineSegment(sketch, "E673", {"start": v(-83.34, -80.84) * mm, "end": v(-83.34, -80.18) * mm});
            skLineSegment(sketch, "E674", {"start": v(-83.34, -80.18) * mm, "end": v(-83.34, -78.59) * mm});
            skLineSegment(sketch, "E675", {"start": v(-83.34, -78.59) * mm, "end": v(-83.34, -77.91) * mm});
            skLineSegment(sketch, "E676", {"start": v(-83.34, -77.91) * mm, "end": v(-83.34, -76.31) * mm});
            skLineSegment(sketch, "E677", {"start": v(-83.34, -76.31) * mm, "end": v(-83.34, -75.61) * mm});
            skLineSegment(sketch, "E678", {"start": v(-83.34, -75.61) * mm, "end": v(-83.34, -74) * mm});
            skLineSegment(sketch, "E679", {"start": v(-83.34, -74) * mm, "end": v(-90.3, -73.8) * mm});
            skLineSegment(sketch, "E680", {"start": v(-90.3, -73.8) * mm, "end": v(-90.3, -70.8) * mm});
            skLineSegment(sketch, "E681", {"start": v(-90.3, -70.8) * mm, "end": v(-83.5, -70.8) * mm});
            skLineSegment(sketch, "E682", {"start": v(-83.5, -70.8) * mm, "end": v(-83.34, -69.28) * mm});
            skLineSegment(sketch, "E683", {"start": v(-83.34, -69.28) * mm, "end": v(-83.34, -67.76) * mm});
            skLineSegment(sketch, "E684", {"start": v(-83.34, -67.76) * mm, "end": v(-83.34, -66.27) * mm});
            skLineSegment(sketch, "E685", {"start": v(-83.34, -66.27) * mm, "end": v(-83.34, -64.82) * mm});
            skLineSegment(sketch, "E686", {"start": v(-83.34, -64.82) * mm, "end": v(-83.34, -63.4) * mm});
            skLineSegment(sketch, "E687", {"start": v(-83.34, -63.4) * mm, "end": v(-83.34, -62.04) * mm});
            skLineSegment(sketch, "E688", {"start": v(-83.34, -62.04) * mm, "end": v(-83.34, -60.73) * mm});
            skLineSegment(sketch, "E689", {"start": v(-83.34, -60.73) * mm, "end": v(-83.34, -40.5) * mm});
            skLineSegment(sketch, "E690", {"start": v(-83.34, -40.5) * mm, "end": v(-92.45, -40.35) * mm});
            skLineSegment(sketch, "E691", {"start": v(-92.45, -40.35) * mm, "end": v(-92.45, -37.35) * mm});
            skLineSegment(sketch, "E692", {"start": v(-92.45, -37.35) * mm, "end": v(-83.5, -37.35) * mm});
            skLineSegment(sketch, "E693", {"start": v(-83.5, -37.35) * mm, "end": v(-83.34, -23.6) * mm});
            skLineSegment(sketch, "E694", {"start": v(-83.34, -23.6) * mm, "end": v(-83.34, -20.76) * mm});
            skLineSegment(sketch, "E695", {"start": v(-83.34, -20.76) * mm, "end": v(-83.34, -17.93) * mm});
            skLineSegment(sketch, "E696", {"start": v(-83.34, -17.93) * mm, "end": v(-83.34, -15.1) * mm});
            skLineSegment(sketch, "E697", {"start": v(-83.34, -15.1) * mm, "end": v(-83.34, -12.3) * mm});
            skLineSegment(sketch, "E698", {"start": v(-83.34, -12.3) * mm, "end": v(-83.34, -9.53) * mm});
            skLineSegment(sketch, "E699", {"start": v(-83.34, -9.53) * mm, "end": v(-83.34, -7.05) * mm});
            skLineSegment(sketch, "E700", {"start": v(-83.34, -7.05) * mm, "end": v(-96.5, -6.9) * mm});
            skLineSegment(sketch, "E701", {"start": v(-96.5, -6.9) * mm, "end": v(-96.5, -3.9) * mm});
            skLineSegment(sketch, "E702", {"start": v(-96.5, -3.9) * mm, "end": v(-83.5, -3.9) * mm});
            skLineSegment(sketch, "E703", {"start": v(-83.5, -3.9) * mm, "end": v(-83.34, -1.45) * mm});
            skLineSegment(sketch, "E704", {"start": v(-83.34, -1.45) * mm, "end": v(-83.34, 1.14) * mm});
            skLineSegment(sketch, "E705", {"start": v(-83.34, 1.14) * mm, "end": v(-83.34, 3.66) * mm});
            skLineSegment(sketch, "E706", {"start": v(-83.34, 3.66) * mm, "end": v(-83.34, 4.18) * mm});
            skLineSegment(sketch, "E707", {"start": v(-83.34, 4.18) * mm, "end": v(-83.34, 4.71) * mm});
            skLineSegment(sketch, "E708", {"start": v(-83.34, 4.71) * mm, "end": v(-83.34, 5.3) * mm});
            skLineSegment(sketch, "E709", {"start": v(-83.34, 5.3) * mm, "end": v(-83.34, 5.9) * mm});
            skLineSegment(sketch, "E710", {"start": v(-83.34, 5.9) * mm, "end": v(-83.34, 6.49) * mm});
            skLineSegment(sketch, "E711", {"start": v(-83.34, 6.49) * mm, "end": v(-83.34, 9) * mm});
            skLineSegment(sketch, "E712", {"start": v(-83.34, 9) * mm, "end": v(-83.34, 11.54) * mm});
            skLineSegment(sketch, "E713", {"start": v(-83.34, 11.54) * mm, "end": v(-83.34, 13.91) * mm});
            skLineSegment(sketch, "E714", {"start": v(-83.34, 13.91) * mm, "end": v(-83.34, 16.2) * mm});
            skLineSegment(sketch, "E715", {"start": v(-83.34, 16.2) * mm, "end": v(-83.34, 18.4) * mm});
            skLineSegment(sketch, "E716", {"start": v(-83.34, 18.4) * mm, "end": v(-83.34, 20.53) * mm});
            skLineSegment(sketch, "E717", {"start": v(-83.34, 20.53) * mm, "end": v(-83.34, 22.56) * mm});
            skLineSegment(sketch, "E718", {"start": v(-83.34, 22.56) * mm, "end": v(-83.34, 24.5) * mm});
            skLineSegment(sketch, "E719", {"start": v(-83.34, 24.5) * mm, "end": v(-83.34, 26.36) * mm});
            skLineSegment(sketch, "E720", {"start": v(-83.34, 26.36) * mm, "end": v(-94.92, 26.56) * mm});
            skLineSegment(sketch, "E721", {"start": v(-94.92, 26.56) * mm, "end": v(-94.92, 29.56) * mm});
            skLineSegment(sketch, "E722", {"start": v(-94.92, 29.56) * mm, "end": v(-83.5, 29.56) * mm});
            skLineSegment(sketch, "E723", {"start": v(-83.5, 29.56) * mm, "end": v(-83.34, 31.4) * mm});
            skLineSegment(sketch, "E724", {"start": v(-83.34, 31.4) * mm, "end": v(-83.34, 32.91) * mm});
            skLineSegment(sketch, "E725", {"start": v(-83.34, 32.91) * mm, "end": v(-83.34, 59.86) * mm});
            skLineSegment(sketch, "E726", {"start": v(-83.34, 59.86) * mm, "end": v(-87.34, 60.01) * mm});
            skLineSegment(sketch, "E727", {"start": v(-87.34, 60.01) * mm, "end": v(-87.34, 63.01) * mm});
            skLineSegment(sketch, "E728", {"start": v(-87.34, 63.01) * mm, "end": v(-83.5, 63.01) * mm});
            skLineSegment(sketch, "E729", {"start": v(-83.5, 63.01) * mm, "end": v(-83.34, 93.32) * mm});
            skLineSegment(sketch, "E730", {"start": v(-83.34, 93.32) * mm, "end": v(-91.73, 93.47) * mm});
            skLineSegment(sketch, "E731", {"start": v(-91.73, 93.47) * mm, "end": v(-91.73, 96.47) * mm});
            skLineSegment(sketch, "E732", {"start": v(-91.73, 96.47) * mm, "end": v(-83.5, 96.47) * mm});
            skLineSegment(sketch, "E733", {"start": v(-83.5, 96.47) * mm, "end": v(-83.34, 126.77) * mm});
            skLineSegment(sketch, "E734", {"start": v(-83.34, 126.77) * mm, "end": v(-87.34, 126.92) * mm});
            skLineSegment(sketch, "E735", {"start": v(-87.34, 126.92) * mm, "end": v(-87.34, 129.92) * mm});
            skLineSegment(sketch, "E736", {"start": v(-87.34, 129.92) * mm, "end": v(-83.5, 129.92) * mm});
            skLineSegment(sketch, "E737", {"start": v(-83.5, 129.92) * mm, "end": v(-83.34, 145.15) * mm});
            skLineSegment(sketch, "E738", {"start": v(-53.22, 130.07) * mm, "end": v(-57.22, 130.07) * mm});
            skLineSegment(sketch, "E739", {"start": v(-57.22, 130.07) * mm, "end": v(-57.22, 129.51) * mm});
            skLineSegment(sketch, "E740", {"start": v(-57.22, 129.51) * mm, "end": v(-57.22, 128.99) * mm});
            skLineSegment(sketch, "E741", {"start": v(-57.22, 128.99) * mm, "end": v(-57.22, 128.46) * mm});
            skLineSegment(sketch, "E742", {"start": v(-57.22, 128.46) * mm, "end": v(-57.22, 127.91) * mm});
            skLineSegment(sketch, "E743", {"start": v(-57.22, 127.91) * mm, "end": v(-57.22, 127.35) * mm});
            skLineSegment(sketch, "E744", {"start": v(-57.22, 127.35) * mm, "end": v(-57.22, 126.74) * mm});
            skLineSegment(sketch, "E745", {"start": v(-57.22, 126.74) * mm, "end": v(-57.22, 52.16) * mm});
            skLineSegment(sketch, "E746", {"start": v(-57.22, 52.16) * mm, "end": v(-57.22, 36.67) * mm});
            skLineSegment(sketch, "E747", {"start": v(-57.22, 36.67) * mm, "end": v(-57.22, 35.35) * mm});
            skLineSegment(sketch, "E748", {"start": v(-57.22, 35.35) * mm, "end": v(-57.22, 34.02) * mm});
            skLineSegment(sketch, "E749", {"start": v(-57.22, 34.02) * mm, "end": v(-57.22, 32.15) * mm});
            skLineSegment(sketch, "E750", {"start": v(-57.22, 32.15) * mm, "end": v(-57.22, 29.63) * mm});
            skLineSegment(sketch, "E751", {"start": v(-57.22, 29.63) * mm, "end": v(-57.22, 26.31) * mm});
            skLineSegment(sketch, "E752", {"start": v(-57.22, 26.31) * mm, "end": v(-57.22, 22) * mm});
            skLineSegment(sketch, "E753", {"start": v(-57.22, 22) * mm, "end": v(-57.22, 16.4) * mm});
            skLineSegment(sketch, "E754", {"start": v(-57.22, 16.4) * mm, "end": v(-57.22, 9.07) * mm});
            skLineSegment(sketch, "E755", {"start": v(-57.22, 9.07) * mm, "end": v(-57.22, 0.95) * mm});
            skLineSegment(sketch, "E756", {"start": v(-57.22, 0.95) * mm, "end": v(-64.83, -1.77) * mm});
            skLineSegment(sketch, "E757", {"start": v(-64.83, -1.77) * mm, "end": v(-71.28, -4.03) * mm});
            skLineSegment(sketch, "E758", {"start": v(-71.28, -4.03) * mm, "end": v(-71.76, -4.24) * mm});
            skLineSegment(sketch, "E759", {"start": v(-71.76, -4.24) * mm, "end": v(-72.22, -4.54) * mm});
            skLineSegment(sketch, "E760", {"start": v(-72.22, -4.54) * mm, "end": v(-72.65, -4.92) * mm});
            skLineSegment(sketch, "E761", {"start": v(-72.65, -4.92) * mm, "end": v(-73.05, -5.36) * mm});
            skLineSegment(sketch, "E762", {"start": v(-73.05, -5.36) * mm, "end": v(-73.41, -5.86) * mm});
            skLineSegment(sketch, "E763", {"start": v(-73.41, -5.86) * mm, "end": v(-73.73, -6.42) * mm});
            skLineSegment(sketch, "E764", {"start": v(-73.73, -6.42) * mm, "end": v(-73.94, -6.9) * mm});
            skLineSegment(sketch, "E765", {"start": v(-73.94, -6.9) * mm, "end": v(-74.14, -7.45) * mm});
            skLineSegment(sketch, "E766", {"start": v(-74.14, -7.45) * mm, "end": v(-74.3, -8) * mm});
            skLineSegment(sketch, "E767", {"start": v(-74.3, -8) * mm, "end": v(-74.4, -8.57) * mm});
            skLineSegment(sketch, "E768", {"start": v(-74.4, -8.57) * mm, "end": v(-74.71, -11.69) * mm});
            skLineSegment(sketch, "E769", {"start": v(-74.71, -11.69) * mm, "end": v(-74.77, -12.22) * mm});
            skLineSegment(sketch, "E770", {"start": v(-74.77, -12.22) * mm, "end": v(-75.4, -18.8) * mm});
            skLineSegment(sketch, "E771", {"start": v(-75.4, -18.8) * mm, "end": v(-75.58, -20.73) * mm});
            skLineSegment(sketch, "E772", {"start": v(-75.58, -20.73) * mm, "end": v(-76.05, -25.68) * mm});
            skLineSegment(sketch, "E773", {"start": v(-76.05, -25.68) * mm, "end": v(-76.35, -28.9) * mm});
            skLineSegment(sketch, "E774", {"start": v(-76.35, -28.9) * mm, "end": v(-76.68, -32.34) * mm});
            skLineSegment(sketch, "E775", {"start": v(-76.68, -32.34) * mm, "end": v(-77.1, -36.78) * mm});
            skLineSegment(sketch, "E776", {"start": v(-77.1, -36.78) * mm, "end": v(-77.3, -38.77) * mm});
            skLineSegment(sketch, "E777", {"start": v(-77.3, -38.77) * mm, "end": v(-77.43, -40.23) * mm});
            skLineSegment(sketch, "E778", {"start": v(-77.43, -40.23) * mm, "end": v(-77.89, -45.02) * mm});
            skLineSegment(sketch, "E779", {"start": v(-77.89, -45.02) * mm, "end": v(-78.18, -48.08) * mm});
            skLineSegment(sketch, "E780", {"start": v(-78.18, -48.08) * mm, "end": v(-78.21, -48.6) * mm});
            skLineSegment(sketch, "E781", {"start": v(-78.21, -48.6) * mm, "end": v(-78.22, -49.13) * mm});
            skLineSegment(sketch, "E782", {"start": v(-78.22, -49.13) * mm, "end": v(-78.2, -49.65) * mm});
            skLineSegment(sketch, "E783", {"start": v(-78.2, -49.65) * mm, "end": v(-78.15, -50.16) * mm});
            skLineSegment(sketch, "E784", {"start": v(-78.15, -50.16) * mm, "end": v(-78.02, -50.89) * mm});
            skLineSegment(sketch, "E785", {"start": v(-78.02, -50.89) * mm, "end": v(-77.6, -52.85) * mm});
            skLineSegment(sketch, "E786", {"start": v(-77.6, -52.85) * mm, "end": v(-77.08, -55.38) * mm});
            skLineSegment(sketch, "E787", {"start": v(-77.08, -55.38) * mm, "end": v(-76.98, -55.92) * mm});
            skLineSegment(sketch, "E788", {"start": v(-76.98, -55.92) * mm, "end": v(-76.41, -59.02) * mm});
            skLineSegment(sketch, "E789", {"start": v(-76.41, -59.02) * mm, "end": v(-76.25, -59.94) * mm});
            skLineSegment(sketch, "E790", {"start": v(-76.25, -59.94) * mm, "end": v(-75.81, -62.54) * mm});
            skLineSegment(sketch, "E791", {"start": v(-75.81, -62.54) * mm, "end": v(-75.5, -64.4) * mm});
            skLineSegment(sketch, "E792", {"start": v(-75.5, -64.4) * mm, "end": v(-75.27, -66.01) * mm});
            skLineSegment(sketch, "E793", {"start": v(-75.27, -66.01) * mm, "end": v(-74.86, -68.72) * mm});
            skLineSegment(sketch, "E794", {"start": v(-74.86, -68.72) * mm, "end": v(-74.77, -69.45) * mm});
            skLineSegment(sketch, "E795", {"start": v(-74.77, -69.45) * mm, "end": v(-74.34, -72.7) * mm});
            skLineSegment(sketch, "E796", {"start": v(-74.34, -72.7) * mm, "end": v(-73.95, -76.35) * mm});
            skLineSegment(sketch, "E797", {"start": v(-73.95, -76.35) * mm, "end": v(-73.88, -76.95) * mm});
            skLineSegment(sketch, "E798", {"start": v(-73.88, -76.95) * mm, "end": v(-73.62, -79.84) * mm});
            skLineSegment(sketch, "E799", {"start": v(-73.62, -79.84) * mm, "end": v(-73.53, -80.92) * mm});
            skLineSegment(sketch, "E800", {"start": v(-73.53, -80.92) * mm, "end": v(-73.35, -83.32) * mm});
            skLineSegment(sketch, "E801", {"start": v(-73.35, -83.32) * mm, "end": v(-73.24, -84.8) * mm});
            skLineSegment(sketch, "E802", {"start": v(-73.24, -84.8) * mm, "end": v(-73.12, -86.82) * mm});
            skLineSegment(sketch, "E803", {"start": v(-73.12, -86.82) * mm, "end": v(-73.02, -88.64) * mm});
            skLineSegment(sketch, "E804", {"start": v(-73.02, -88.64) * mm, "end": v(-72.95, -90.36) * mm});
            skLineSegment(sketch, "E805", {"start": v(-72.95, -90.36) * mm, "end": v(-72.86, -92.42) * mm});
            skLineSegment(sketch, "E806", {"start": v(-72.86, -92.42) * mm, "end": v(-72.82, -93.94) * mm});
            skLineSegment(sketch, "E807", {"start": v(-72.82, -93.94) * mm, "end": v(-72.77, -96.18) * mm});
            skLineSegment(sketch, "E808", {"start": v(-72.77, -96.18) * mm, "end": v(-72.76, -97.59) * mm});
            skLineSegment(sketch, "E809", {"start": v(-72.76, -97.59) * mm, "end": v(-72.74, -99.93) * mm});
            skLineSegment(sketch, "E810", {"start": v(-72.74, -99.93) * mm, "end": v(-72.75, -101.32) * mm});
            skLineSegment(sketch, "E811", {"start": v(-72.75, -101.32) * mm, "end": v(-72.77, -103.67) * mm});
            skLineSegment(sketch, "E812", {"start": v(-72.77, -103.67) * mm, "end": v(-72.8, -105.15) * mm});
            skLineSegment(sketch, "E813", {"start": v(-72.8, -105.15) * mm, "end": v(-72.86, -107.43) * mm});
            skLineSegment(sketch, "E814", {"start": v(-72.86, -107.43) * mm, "end": v(-72.93, -109.12) * mm});
            skLineSegment(sketch, "E815", {"start": v(-72.93, -109.12) * mm, "end": v(-73.02, -111.22) * mm});
            skLineSegment(sketch, "E816", {"start": v(-73.02, -111.22) * mm, "end": v(-73.13, -113.24) * mm});
            skLineSegment(sketch, "E817", {"start": v(-73.13, -113.24) * mm, "end": v(-73.24, -115.05) * mm});
            skLineSegment(sketch, "E818", {"start": v(-73.24, -115.05) * mm, "end": v(-73.42, -117.55) * mm});
            skLineSegment(sketch, "E819", {"start": v(-73.42, -117.55) * mm, "end": v(-73.53, -118.94) * mm});
            skLineSegment(sketch, "E820", {"start": v(-73.53, -118.94) * mm, "end": v(-73.81, -122.1) * mm});
            skLineSegment(sketch, "E821", {"start": v(-73.81, -122.1) * mm, "end": v(-73.88, -122.9) * mm});
            skLineSegment(sketch, "E822", {"start": v(-73.88, -122.9) * mm, "end": v(-74.3, -126.92) * mm});
            skLineSegment(sketch, "E823", {"start": v(-74.3, -126.92) * mm, "end": v(-74.86, -131.14) * mm});
            skLineSegment(sketch, "E824", {"start": v(-74.86, -131.14) * mm, "end": v(-75.04, -132.33) * mm});
            skLineSegment(sketch, "E825", {"start": v(-75.04, -132.33) * mm, "end": v(-75.5, -135.44) * mm});
            skLineSegment(sketch, "E826", {"start": v(-75.5, -135.44) * mm, "end": v(-75.97, -138.27) * mm});
            skLineSegment(sketch, "E827", {"start": v(-75.97, -138.27) * mm, "end": v(-76.25, -139.91) * mm});
            skLineSegment(sketch, "E828", {"start": v(-76.25, -139.91) * mm, "end": v(-76.98, -143.93) * mm});
            skLineSegment(sketch, "E829", {"start": v(-76.98, -143.93) * mm, "end": v(-77.13, -144.72) * mm});
            skLineSegment(sketch, "E830", {"start": v(-77.13, -144.72) * mm, "end": v(-77.3, -145.44) * mm});
            skLineSegment(sketch, "E831", {"start": v(-77.3, -145.44) * mm, "end": v(-78.49, -150.95) * mm});
            skLineSegment(sketch, "E832", {"start": v(-78.49, -150.95) * mm, "end": v(-79.8, -156.48) * mm});
            skLineSegment(sketch, "E833", {"start": v(-79.8, -156.48) * mm, "end": v(-79.93, -157.08) * mm});
            skLineSegment(sketch, "E834", {"start": v(-79.93, -157.08) * mm, "end": v(-80.03, -157.66) * mm});
            skLineSegment(sketch, "E835", {"start": v(-80.03, -157.66) * mm, "end": v(-80.1, -158.22) * mm});
            skLineSegment(sketch, "E836", {"start": v(-80.1, -158.22) * mm, "end": v(-80.15, -158.79) * mm});
            skLineSegment(sketch, "E837", {"start": v(-80.15, -158.79) * mm, "end": v(-80.17, -159.36) * mm});
            skLineSegment(sketch, "E838", {"start": v(-80.17, -159.36) * mm, "end": v(-80.17, -163.08) * mm});
            skLineSegment(sketch, "E839", {"start": v(-80.17, -163.08) * mm, "end": v(-80.17, -164.04) * mm});
            skLineSegment(sketch, "E840", {"start": v(-80.17, -164.04) * mm, "end": v(-80.17, -169.1) * mm});
            skLineSegment(sketch, "E841", {"start": v(-80.17, -169.1) * mm, "end": v(-80.17, -171.88) * mm});
            skLineSegment(sketch, "E842", {"start": v(-80.17, -171.88) * mm, "end": v(-80.17, -175.54) * mm});
            skLineSegment(sketch, "E843", {"start": v(-80.17, -175.54) * mm, "end": v(-80.17, -180.67) * mm});
            skLineSegment(sketch, "E844", {"start": v(-80.17, -180.67) * mm, "end": v(-80.17, -182.5) * mm});
            skLineSegment(sketch, "E845", {"start": v(-80.17, -182.5) * mm, "end": v(-80.17, -188.35) * mm});
            skLineSegment(sketch, "E846", {"start": v(-80.17, -188.35) * mm, "end": v(-80.15, -188.86) * mm});
            skLineSegment(sketch, "E847", {"start": v(-80.15, -188.86) * mm, "end": v(-80.08, -189.53) * mm});
            skLineSegment(sketch, "E848", {"start": v(-80.08, -189.53) * mm, "end": v(-79.98, -190.06) * mm});
            skLineSegment(sketch, "E849", {"start": v(-79.98, -190.06) * mm, "end": v(-79.82, -190.62) * mm});
            skLineSegment(sketch, "E850", {"start": v(-79.82, -190.62) * mm, "end": v(-79.6, -191.21) * mm});
            skLineSegment(sketch, "E851", {"start": v(-79.6, -191.21) * mm, "end": v(-79.3, -191.76) * mm});
            skLineSegment(sketch, "E852", {"start": v(-79.3, -191.76) * mm, "end": v(-78.98, -192.26) * mm});
            skLineSegment(sketch, "E853", {"start": v(-78.98, -192.26) * mm, "end": v(-78.6, -192.7) * mm});
            skLineSegment(sketch, "E854", {"start": v(-78.6, -192.7) * mm, "end": v(-78.2, -193.08) * mm});
            skLineSegment(sketch, "E855", {"start": v(-78.2, -193.08) * mm, "end": v(-77.75, -193.39) * mm});
            skLineSegment(sketch, "E856", {"start": v(-77.75, -193.39) * mm, "end": v(-77.2, -193.68) * mm});
            skLineSegment(sketch, "E857", {"start": v(-77.2, -193.68) * mm, "end": v(-74.74, -194.56) * mm});
            skLineSegment(sketch, "E858", {"start": v(-74.74, -194.56) * mm, "end": v(-57.22, -200.8) * mm});
            skLineSegment(sketch, "E859", {"start": v(-57.22, -200.8) * mm, "end": v(-57.22, -201.94) * mm});
            skLineSegment(sketch, "E860", {"start": v(-57.22, -201.94) * mm, "end": v(-57.22, -202.54) * mm});
            skLineSegment(sketch, "E861", {"start": v(-57.22, -202.54) * mm, "end": v(-57.22, -210.08) * mm});
            skLineSegment(sketch, "E862", {"start": v(-57.22, -210.08) * mm, "end": v(-57.22, -215.51) * mm});
            skLineSegment(sketch, "E863", {"start": v(-57.22, -215.51) * mm, "end": v(-57.22, -218.97) * mm});
            skLineSegment(sketch, "E864", {"start": v(-57.22, -218.97) * mm, "end": v(-57.22, -225.3) * mm});
            skLineSegment(sketch, "E865", {"start": v(-57.22, -225.3) * mm, "end": v(-63.69, -225.7) * mm});
            skLineSegment(sketch, "E866", {"start": v(-63.69, -225.7) * mm, "end": v(-76.38, -226.52) * mm});
            skLineSegment(sketch, "E867", {"start": v(-76.38, -226.52) * mm, "end": v(-76.9, -226.6) * mm});
            skLineSegment(sketch, "E868", {"start": v(-76.9, -226.6) * mm, "end": v(-77.4, -226.75) * mm});
            skLineSegment(sketch, "E869", {"start": v(-77.4, -226.75) * mm, "end": v(-77.88, -226.98) * mm});
            skLineSegment(sketch, "E870", {"start": v(-77.88, -226.98) * mm, "end": v(-78.33, -227.29) * mm});
            skLineSegment(sketch, "E871", {"start": v(-78.33, -227.29) * mm, "end": v(-78.75, -227.66) * mm});
            skLineSegment(sketch, "E872", {"start": v(-78.75, -227.66) * mm, "end": v(-79.13, -228.1) * mm});
            skLineSegment(sketch, "E873", {"start": v(-79.13, -228.1) * mm, "end": v(-79.45, -228.6) * mm});
            skLineSegment(sketch, "E874", {"start": v(-79.45, -228.6) * mm, "end": v(-79.72, -229.14) * mm});
            skLineSegment(sketch, "E875", {"start": v(-79.72, -229.14) * mm, "end": v(-79.93, -229.7) * mm});
            skLineSegment(sketch, "E876", {"start": v(-79.93, -229.7) * mm, "end": v(-80.07, -230.28) * mm});
            skLineSegment(sketch, "E877", {"start": v(-80.07, -230.28) * mm, "end": v(-80.15, -230.88) * mm});
            skLineSegment(sketch, "E878", {"start": v(-80.15, -230.88) * mm, "end": v(-80.17, -237.96) * mm});
            skLineSegment(sketch, "E879", {"start": v(-80.17, -237.96) * mm, "end": v(-80.17, -241.02) * mm});
            skLineSegment(sketch, "E880", {"start": v(-80.17, -241.02) * mm, "end": v(-80.14, -241.54) * mm});
            skLineSegment(sketch, "E881", {"start": v(-80.14, -241.54) * mm, "end": v(-80.05, -242.13) * mm});
            skLineSegment(sketch, "E882", {"start": v(-80.05, -242.13) * mm, "end": v(-79.9, -242.7) * mm});
            skLineSegment(sketch, "E883", {"start": v(-79.9, -242.7) * mm, "end": v(-79.68, -243.25) * mm});
            skLineSegment(sketch, "E884", {"start": v(-79.68, -243.25) * mm, "end": v(-79.4, -243.76) * mm});
            skLineSegment(sketch, "E885", {"start": v(-79.4, -243.76) * mm, "end": v(-79.07, -244.22) * mm});
            skLineSegment(sketch, "E886", {"start": v(-79.07, -244.22) * mm, "end": v(-78.7, -244.64) * mm});
            skLineSegment(sketch, "E887", {"start": v(-78.7, -244.64) * mm, "end": v(-78.27, -244.99) * mm});
            skLineSegment(sketch, "E888", {"start": v(-78.27, -244.99) * mm, "end": v(-77.81, -245.27) * mm});
            skLineSegment(sketch, "E889", {"start": v(-77.81, -245.27) * mm, "end": v(-77.33, -245.49) * mm});
            skLineSegment(sketch, "E890", {"start": v(-77.33, -245.49) * mm, "end": v(-76.82, -245.62) * mm});
            skLineSegment(sketch, "E891", {"start": v(-76.82, -245.62) * mm, "end": v(-67.65, -246.59) * mm});
            skLineSegment(sketch, "E892", {"start": v(-67.65, -246.59) * mm, "end": v(-49.22, -248.41) * mm});
            skLineSegment(sketch, "E893", {"start": v(-49.22, -248.41) * mm, "end": v(-49.22, -242.58) * mm});
            skLineSegment(sketch, "E894", {"start": v(-49.22, -242.58) * mm, "end": v(-49.22, -229.89) * mm});
            skLineSegment(sketch, "E895", {"start": v(-49.22, -229.89) * mm, "end": v(-49.22, -222.86) * mm});
            skLineSegment(sketch, "E896", {"start": v(-49.22, -222.86) * mm, "end": v(-53.22, -222.7) * mm});
            skLineSegment(sketch, "E897", {"start": v(-53.22, -222.7) * mm, "end": v(-53.22, -219.7) * mm});
            skLineSegment(sketch, "E898", {"start": v(-53.22, -219.7) * mm, "end": v(-49.37, -219.7) * mm});
            skLineSegment(sketch, "E899", {"start": v(-49.37, -219.7) * mm, "end": v(-49.22, -218.7) * mm});
            skLineSegment(sketch, "E900", {"start": v(-49.22, -218.7) * mm, "end": v(-49.22, -218.14) * mm});
            skLineSegment(sketch, "E901", {"start": v(-49.22, -218.14) * mm, "end": v(-49.22, -208.74) * mm});
            skLineSegment(sketch, "E902", {"start": v(-49.22, -208.74) * mm, "end": v(-49.22, -208.04) * mm});
            skLineSegment(sketch, "E903", {"start": v(-49.22, -208.04) * mm, "end": v(-49.22, -199.78) * mm});
            skLineSegment(sketch, "E904", {"start": v(-49.22, -199.78) * mm, "end": v(-49.22, -198.98) * mm});
            skLineSegment(sketch, "E905", {"start": v(-49.22, -198.98) * mm, "end": v(-49.22, -191.64) * mm});
            skLineSegment(sketch, "E906", {"start": v(-49.22, -191.64) * mm, "end": v(-49.22, -190.76) * mm});
            skLineSegment(sketch, "E907", {"start": v(-49.22, -190.76) * mm, "end": v(-49.22, -189.4) * mm});
            skLineSegment(sketch, "E908", {"start": v(-49.22, -189.4) * mm, "end": v(-64.7, -189.25) * mm});
            skLineSegment(sketch, "E909", {"start": v(-64.7, -189.25) * mm, "end": v(-64.7, -186.25) * mm});
            skLineSegment(sketch, "E910", {"start": v(-64.7, -186.25) * mm, "end": v(-49.37, -186.25) * mm});
            skLineSegment(sketch, "E911", {"start": v(-49.37, -186.25) * mm, "end": v(-49.22, -184.2) * mm});
            skLineSegment(sketch, "E912", {"start": v(-49.22, -184.2) * mm, "end": v(-49.22, -183.26) * mm});
            skLineSegment(sketch, "E913", {"start": v(-49.22, -183.26) * mm, "end": v(-49.22, -177.35) * mm});
            skLineSegment(sketch, "E914", {"start": v(-49.22, -177.35) * mm, "end": v(-49.22, -176.36) * mm});
            skLineSegment(sketch, "E915", {"start": v(-49.22, -176.36) * mm, "end": v(-49.22, -171) * mm});
            skLineSegment(sketch, "E916", {"start": v(-49.22, -171) * mm, "end": v(-49.22, -169.97) * mm});
            skLineSegment(sketch, "E917", {"start": v(-49.22, -169.97) * mm, "end": v(-49.22, -165.06) * mm});
            skLineSegment(sketch, "E918", {"start": v(-49.22, -165.06) * mm, "end": v(-49.22, -164) * mm});
            skLineSegment(sketch, "E919", {"start": v(-49.22, -164) * mm, "end": v(-49.22, -159.49) * mm});
            skLineSegment(sketch, "E920", {"start": v(-49.22, -159.49) * mm, "end": v(-49.22, -158.42) * mm});
            skLineSegment(sketch, "E921", {"start": v(-49.22, -158.42) * mm, "end": v(-49.22, -155.95) * mm});
            skLineSegment(sketch, "E922", {"start": v(-49.22, -155.95) * mm, "end": v(-64.43, -155.8) * mm});
            skLineSegment(sketch, "E923", {"start": v(-64.43, -155.8) * mm, "end": v(-64.43, -152.8) * mm});
            skLineSegment(sketch, "E924", {"start": v(-64.43, -152.8) * mm, "end": v(-49.37, -152.8) * mm});
            skLineSegment(sketch, "E925", {"start": v(-49.37, -152.8) * mm, "end": v(-49.22, -149.24) * mm});
            skLineSegment(sketch, "E926", {"start": v(-49.22, -149.24) * mm, "end": v(-49.22, -148.14) * mm});
            skLineSegment(sketch, "E927", {"start": v(-49.22, -148.14) * mm, "end": v(-49.22, -144.48) * mm});
            skLineSegment(sketch, "E928", {"start": v(-49.22, -144.48) * mm, "end": v(-49.22, -143.38) * mm});
            skLineSegment(sketch, "E929", {"start": v(-49.22, -143.38) * mm, "end": v(-49.22, -139.93) * mm});
            skLineSegment(sketch, "E930", {"start": v(-49.22, -139.93) * mm, "end": v(-49.22, -138.81) * mm});
            skLineSegment(sketch, "E931", {"start": v(-49.22, -138.81) * mm, "end": v(-49.22, -135.54) * mm});
            skLineSegment(sketch, "E932", {"start": v(-49.22, -135.54) * mm, "end": v(-49.22, -134.42) * mm});
            skLineSegment(sketch, "E933", {"start": v(-49.22, -134.42) * mm, "end": v(-49.22, -131.3) * mm});
            skLineSegment(sketch, "E934", {"start": v(-49.22, -131.3) * mm, "end": v(-49.22, -130.18) * mm});
            skLineSegment(sketch, "E935", {"start": v(-49.22, -130.18) * mm, "end": v(-49.22, -127.2) * mm});
            skLineSegment(sketch, "E936", {"start": v(-49.22, -127.2) * mm, "end": v(-49.22, -126.06) * mm});
            skLineSegment(sketch, "E937", {"start": v(-49.22, -126.06) * mm, "end": v(-49.22, -123.18) * mm});
            skLineSegment(sketch, "E938", {"start": v(-49.22, -123.18) * mm, "end": v(-49.22, -122.5) * mm});
            skLineSegment(sketch, "E939", {"start": v(-49.22, -122.5) * mm, "end": v(-61.53, -122.34) * mm});
            skLineSegment(sketch, "E940", {"start": v(-61.53, -122.34) * mm, "end": v(-61.53, -119.34) * mm});
            skLineSegment(sketch, "E941", {"start": v(-61.53, -119.34) * mm, "end": v(-49.37, -119.34) * mm});
            skLineSegment(sketch, "E942", {"start": v(-49.37, -119.34) * mm, "end": v(-49.22, -118.13) * mm});
            skLineSegment(sketch, "E943", {"start": v(-49.22, -118.13) * mm, "end": v(-49.22, -115.41) * mm});
            skLineSegment(sketch, "E944", {"start": v(-49.22, -115.41) * mm, "end": v(-49.22, -114.28) * mm});
            skLineSegment(sketch, "E945", {"start": v(-49.22, -114.28) * mm, "end": v(-49.22, -111.61) * mm});
            skLineSegment(sketch, "E946", {"start": v(-49.22, -111.61) * mm, "end": v(-49.22, -110.48) * mm});
            skLineSegment(sketch, "E947", {"start": v(-49.22, -110.48) * mm, "end": v(-49.22, -107.85) * mm});
            skLineSegment(sketch, "E948", {"start": v(-49.22, -107.85) * mm, "end": v(-49.22, -106.72) * mm});
            skLineSegment(sketch, "E949", {"start": v(-49.22, -106.72) * mm, "end": v(-49.22, -104.12) * mm});
            skLineSegment(sketch, "E950", {"start": v(-49.22, -104.12) * mm, "end": v(-49.22, -102.98) * mm});
            skLineSegment(sketch, "E951", {"start": v(-49.22, -102.98) * mm, "end": v(-49.22, -100.4) * mm});
            skLineSegment(sketch, "E952", {"start": v(-49.22, -100.4) * mm, "end": v(-49.22, -99.26) * mm});
            skLineSegment(sketch, "E953", {"start": v(-49.22, -99.26) * mm, "end": v(-49.22, -96.67) * mm});
            skLineSegment(sketch, "E954", {"start": v(-49.22, -96.67) * mm, "end": v(-49.22, -95.53) * mm});
            skLineSegment(sketch, "E955", {"start": v(-49.22, -95.53) * mm, "end": v(-49.22, -92.92) * mm});
            skLineSegment(sketch, "E956", {"start": v(-49.22, -92.92) * mm, "end": v(-49.22, -91.78) * mm});
            skLineSegment(sketch, "E957", {"start": v(-49.22, -91.78) * mm, "end": v(-49.22, -89.15) * mm});
            skLineSegment(sketch, "E958", {"start": v(-49.22, -89.15) * mm, "end": v(-61.2, -88.89) * mm});
            skLineSegment(sketch, "E959", {"start": v(-61.2, -88.89) * mm, "end": v(-61.2, -85.89) * mm});
            skLineSegment(sketch, "E960", {"start": v(-61.2, -85.89) * mm, "end": v(-49.37, -85.89) * mm});
            skLineSegment(sketch, "E961", {"start": v(-49.37, -85.89) * mm, "end": v(-49.22, -85.32) * mm});
            skLineSegment(sketch, "E962", {"start": v(-49.22, -85.32) * mm, "end": v(-49.22, -84.18) * mm});
            skLineSegment(sketch, "E963", {"start": v(-49.22, -84.18) * mm, "end": v(-49.22, -83.04) * mm});
            skLineSegment(sketch, "E964", {"start": v(-49.22, -83.04) * mm, "end": v(-49.22, -81.92) * mm});
            skLineSegment(sketch, "E965", {"start": v(-49.22, -81.92) * mm, "end": v(-49.22, -80.8) * mm});
            skLineSegment(sketch, "E966", {"start": v(-49.22, -80.8) * mm, "end": v(-49.22, -79.7) * mm});
            skLineSegment(sketch, "E967", {"start": v(-49.22, -79.7) * mm, "end": v(-49.22, -78.63) * mm});
            skLineSegment(sketch, "E968", {"start": v(-49.22, -78.63) * mm, "end": v(-49.22, -77.57) * mm});
            skLineSegment(sketch, "E969", {"start": v(-49.22, -77.57) * mm, "end": v(-49.22, -76.55) * mm});
            skLineSegment(sketch, "E970", {"start": v(-49.22, -76.55) * mm, "end": v(-49.22, -75.55) * mm});
            skLineSegment(sketch, "E971", {"start": v(-49.22, -75.55) * mm, "end": v(-49.22, -74.58) * mm});
            skLineSegment(sketch, "E972", {"start": v(-49.22, -74.58) * mm, "end": v(-49.22, -55.58) * mm});
            skLineSegment(sketch, "E973", {"start": v(-49.22, -55.58) * mm, "end": v(-63.45, -55.43) * mm});
            skLineSegment(sketch, "E974", {"start": v(-63.45, -55.43) * mm, "end": v(-63.45, -52.43) * mm});
            skLineSegment(sketch, "E975", {"start": v(-63.45, -52.43) * mm, "end": v(-49.37, -52.43) * mm});
            skLineSegment(sketch, "E976", {"start": v(-49.37, -52.43) * mm, "end": v(-49.22, -22.13) * mm});
            skLineSegment(sketch, "E977", {"start": v(-49.22, -22.13) * mm, "end": v(-62.38, -21.98) * mm});
            skLineSegment(sketch, "E978", {"start": v(-62.38, -21.98) * mm, "end": v(-62.38, -18.98) * mm});
            skLineSegment(sketch, "E979", {"start": v(-62.38, -18.98) * mm, "end": v(-49.37, -18.98) * mm});
            skLineSegment(sketch, "E980", {"start": v(-49.37, -18.98) * mm, "end": v(-49.22, 11.33) * mm});
            skLineSegment(sketch, "E981", {"start": v(-49.22, 11.33) * mm, "end": v(-53.22, 11.48) * mm});
            skLineSegment(sketch, "E982", {"start": v(-53.22, 11.48) * mm, "end": v(-53.22, 14.48) * mm});
            skLineSegment(sketch, "E983", {"start": v(-53.22, 14.48) * mm, "end": v(-49.37, 14.48) * mm});
            skLineSegment(sketch, "E984", {"start": v(-49.37, 14.48) * mm, "end": v(-49.22, 30.04) * mm});
            skLineSegment(sketch, "E985", {"start": v(-49.22, 30.04) * mm, "end": v(-49.22, 31.66) * mm});
            skLineSegment(sketch, "E986", {"start": v(-49.22, 31.66) * mm, "end": v(-49.22, 33.3) * mm});
            skLineSegment(sketch, "E987", {"start": v(-49.22, 33.3) * mm, "end": v(-49.22, 34.92) * mm});
            skLineSegment(sketch, "E988", {"start": v(-49.22, 34.92) * mm, "end": v(-49.22, 36.54) * mm});
            skLineSegment(sketch, "E989", {"start": v(-49.22, 36.54) * mm, "end": v(-49.22, 38.16) * mm});
            skLineSegment(sketch, "E990", {"start": v(-49.22, 38.16) * mm, "end": v(-49.22, 39.75) * mm});
            skLineSegment(sketch, "E991", {"start": v(-49.22, 39.75) * mm, "end": v(-49.22, 41.33) * mm});
            skLineSegment(sketch, "E992", {"start": v(-49.22, 41.33) * mm, "end": v(-49.22, 42.88) * mm});
            skLineSegment(sketch, "E993", {"start": v(-49.22, 42.88) * mm, "end": v(-49.22, 44.4) * mm});
            skLineSegment(sketch, "E994", {"start": v(-49.22, 44.4) * mm, "end": v(-49.37, 44.93) * mm});
            skLineSegment(sketch, "E995", {"start": v(-49.37, 44.93) * mm, "end": v(-53.22, 44.93) * mm});
            skLineSegment(sketch, "E996", {"start": v(-53.22, 44.93) * mm, "end": v(-53.22, 47.93) * mm});
            skLineSegment(sketch, "E997", {"start": v(-53.22, 47.93) * mm, "end": v(-49.37, 47.93) * mm});
            skLineSegment(sketch, "E998", {"start": v(-49.37, 47.93) * mm, "end": v(-49.22, 48.58) * mm});
            skLineSegment(sketch, "E999", {"start": v(-49.22, 48.58) * mm, "end": v(-49.22, 49.14) * mm});
            skLineSegment(sketch, "E1000", {"start": v(-49.22, 49.14) * mm, "end": v(-49.22, 49.73) * mm});
            skLineSegment(sketch, "E1001", {"start": v(-49.22, 49.73) * mm, "end": v(-49.22, 50.34) * mm});
            skLineSegment(sketch, "E1002", {"start": v(-49.22, 50.34) * mm, "end": v(-49.22, 50.97) * mm});
            skLineSegment(sketch, "E1003", {"start": v(-49.22, 50.97) * mm, "end": v(-49.22, 51.6) * mm});
            skLineSegment(sketch, "E1004", {"start": v(-49.22, 51.6) * mm, "end": v(-49.22, 52.23) * mm});
            skLineSegment(sketch, "E1005", {"start": v(-49.22, 52.23) * mm, "end": v(-49.22, 52.84) * mm});
            skLineSegment(sketch, "E1006", {"start": v(-49.22, 52.84) * mm, "end": v(-49.22, 53.43) * mm});
            skLineSegment(sketch, "E1007", {"start": v(-49.22, 53.43) * mm, "end": v(-49.22, 54.82) * mm});
            skLineSegment(sketch, "E1008", {"start": v(-49.22, 54.82) * mm, "end": v(-49.22, 56.18) * mm});
            skLineSegment(sketch, "E1009", {"start": v(-49.22, 56.18) * mm, "end": v(-49.22, 57.49) * mm});
            skLineSegment(sketch, "E1010", {"start": v(-49.22, 57.49) * mm, "end": v(-49.22, 58.75) * mm});
            skLineSegment(sketch, "E1011", {"start": v(-49.22, 58.75) * mm, "end": v(-49.22, 59.97) * mm});
            skLineSegment(sketch, "E1012", {"start": v(-49.22, 59.97) * mm, "end": v(-49.22, 61.14) * mm});
            skLineSegment(sketch, "E1013", {"start": v(-49.22, 61.14) * mm, "end": v(-49.22, 62.27) * mm});
            skLineSegment(sketch, "E1014", {"start": v(-49.22, 62.27) * mm, "end": v(-49.22, 63.35) * mm});
            skLineSegment(sketch, "E1015", {"start": v(-49.22, 63.35) * mm, "end": v(-49.22, 64.37) * mm});
            skLineSegment(sketch, "E1016", {"start": v(-49.22, 64.37) * mm, "end": v(-49.22, 65.35) * mm});
            skLineSegment(sketch, "E1017", {"start": v(-49.22, 65.35) * mm, "end": v(-49.22, 66.28) * mm});
            skLineSegment(sketch, "E1018", {"start": v(-49.22, 66.28) * mm, "end": v(-49.22, 78.24) * mm});
            skLineSegment(sketch, "E1019", {"start": v(-49.22, 78.24) * mm, "end": v(-53.22, 78.4) * mm});
            skLineSegment(sketch, "E1020", {"start": v(-53.22, 78.4) * mm, "end": v(-53.22, 81.4) * mm});
            skLineSegment(sketch, "E1021", {"start": v(-53.22, 81.4) * mm, "end": v(-49.37, 81.4) * mm});
            skLineSegment(sketch, "E1022", {"start": v(-49.37, 81.4) * mm, "end": v(-49.22, 111.7) * mm});
            skLineSegment(sketch, "E1023", {"start": v(-49.22, 111.7) * mm, "end": v(-53.22, 111.85) * mm});
            skLineSegment(sketch, "E1024", {"start": v(-53.22, 111.85) * mm, "end": v(-53.22, 114.85) * mm});
            skLineSegment(sketch, "E1025", {"start": v(-53.22, 114.85) * mm, "end": v(-49.37, 114.85) * mm});
            skLineSegment(sketch, "E1026", {"start": v(-49.37, 114.85) * mm, "end": v(-49.22, 130.07) * mm});
            skLineSegment(sketch, "E1027", {"start": v(-49.22, 130.07) * mm, "end": v(-51.2, 130.07) * mm});
            skLineSegment(sketch, "E1028", {"start": v(-51.2, 130.07) * mm, "end": v(-53.22, 130.07) * mm});
            skLineSegment(sketch, "E1029", {"start": v(-15.1, 130.07) * mm, "end": v(-19.1, 130.07) * mm});
            skLineSegment(sketch, "E1030", {"start": v(-19.1, 130.07) * mm, "end": v(-23.1, 130.07) * mm});
            skLineSegment(sketch, "E1031", {"start": v(-23.1, 130.07) * mm, "end": v(-23.1, 129.51) * mm});
            skLineSegment(sketch, "E1032", {"start": v(-23.1, 129.51) * mm, "end": v(-23.1, 129) * mm});
            skLineSegment(sketch, "E1033", {"start": v(-23.1, 129) * mm, "end": v(-23.1, 128.45) * mm});
            skLineSegment(sketch, "E1034", {"start": v(-23.1, 128.45) * mm, "end": v(-23.1, 127.9) * mm});
            skLineSegment(sketch, "E1035", {"start": v(-23.1, 127.9) * mm, "end": v(-23.1, 87.44) * mm});
            skLineSegment(sketch, "E1036", {"start": v(-23.1, 87.44) * mm, "end": v(-23.1, 86.9) * mm});
            skLineSegment(sketch, "E1037", {"start": v(-23.1, 86.9) * mm, "end": v(-23.1, 86.4) * mm});
            skLineSegment(sketch, "E1038", {"start": v(-23.1, 86.4) * mm, "end": v(-23.1, 76.52) * mm});
            skLineSegment(sketch, "E1039", {"start": v(-23.1, 76.52) * mm, "end": v(-23.1, 70.04) * mm});
            skLineSegment(sketch, "E1040", {"start": v(-23.1, 70.04) * mm, "end": v(-23.1, 62.15) * mm});
            skLineSegment(sketch, "E1041", {"start": v(-23.1, 62.15) * mm, "end": v(-23.1, 52.44) * mm});
            skLineSegment(sketch, "E1042", {"start": v(-23.1, 52.44) * mm, "end": v(-23.1, 40.28) * mm});
            skLineSegment(sketch, "E1043", {"start": v(-23.1, 40.28) * mm, "end": v(-23.1, 24.75) * mm});
            skLineSegment(sketch, "E1044", {"start": v(-23.1, 24.75) * mm, "end": v(-23.1, 4.42) * mm});
            skLineSegment(sketch, "E1045", {"start": v(-23.1, 4.42) * mm, "end": v(-23.1, 0.95) * mm});
            skLineSegment(sketch, "E1046", {"start": v(-23.1, 0.95) * mm, "end": v(-32.96, -2.54) * mm});
            skLineSegment(sketch, "E1047", {"start": v(-32.96, -2.54) * mm, "end": v(-37.16, -4.05) * mm});
            skLineSegment(sketch, "E1048", {"start": v(-37.16, -4.05) * mm, "end": v(-37.64, -4.28) * mm});
            skLineSegment(sketch, "E1049", {"start": v(-37.64, -4.28) * mm, "end": v(-38.1, -4.58) * mm});
            skLineSegment(sketch, "E1050", {"start": v(-38.1, -4.58) * mm, "end": v(-38.53, -4.94) * mm});
            skLineSegment(sketch, "E1051", {"start": v(-38.53, -4.94) * mm, "end": v(-38.93, -5.38) * mm});
            skLineSegment(sketch, "E1052", {"start": v(-38.93, -5.38) * mm, "end": v(-39.3, -5.88) * mm});
            skLineSegment(sketch, "E1053", {"start": v(-39.3, -5.88) * mm, "end": v(-39.6, -6.42) * mm});
            skLineSegment(sketch, "E1054", {"start": v(-39.6, -6.42) * mm, "end": v(-39.87, -7.02) * mm});
            skLineSegment(sketch, "E1055", {"start": v(-39.87, -7.02) * mm, "end": v(-40.08, -7.65) * mm});
            skLineSegment(sketch, "E1056", {"start": v(-40.08, -7.65) * mm, "end": v(-40.24, -8.3) * mm});
            skLineSegment(sketch, "E1057", {"start": v(-40.24, -8.3) * mm, "end": v(-40.33, -8.98) * mm});
            skLineSegment(sketch, "E1058", {"start": v(-40.33, -8.98) * mm, "end": v(-41.04, -16.4) * mm});
            skLineSegment(sketch, "E1059", {"start": v(-41.04, -16.4) * mm, "end": v(-41.2, -18.02) * mm});
            skLineSegment(sketch, "E1060", {"start": v(-41.2, -18.02) * mm, "end": v(-41.75, -23.87) * mm});
            skLineSegment(sketch, "E1061", {"start": v(-41.75, -23.87) * mm, "end": v(-42.05, -27.05) * mm});
            skLineSegment(sketch, "E1062", {"start": v(-42.05, -27.05) * mm, "end": v(-42.44, -31.07) * mm});
            skLineSegment(sketch, "E1063", {"start": v(-42.44, -31.07) * mm, "end": v(-42.88, -35.72) * mm});
            skLineSegment(sketch, "E1064", {"start": v(-42.88, -35.72) * mm, "end": v(-43.1, -38.04) * mm});
            skLineSegment(sketch, "E1065", {"start": v(-43.1, -38.04) * mm, "end": v(-43.67, -44.04) * mm});
            skLineSegment(sketch, "E1066", {"start": v(-43.67, -44.04) * mm, "end": v(-43.74, -44.78) * mm});
            skLineSegment(sketch, "E1067", {"start": v(-43.74, -44.78) * mm, "end": v(-44.06, -48.08) * mm});
            skLineSegment(sketch, "E1068", {"start": v(-44.06, -48.08) * mm, "end": v(-44.1, -48.6) * mm});
            skLineSegment(sketch, "E1069", {"start": v(-44.1, -48.6) * mm, "end": v(-44.1, -49.13) * mm});
            skLineSegment(sketch, "E1070", {"start": v(-44.1, -49.13) * mm, "end": v(-44.07, -49.65) * mm});
            skLineSegment(sketch, "E1071", {"start": v(-44.07, -49.65) * mm, "end": v(-44.02, -50.16) * mm});
            skLineSegment(sketch, "E1072", {"start": v(-44.02, -50.16) * mm, "end": v(-43.94, -50.68) * mm});
            skLineSegment(sketch, "E1073", {"start": v(-43.94, -50.68) * mm, "end": v(-43.45, -53.05) * mm});
            skLineSegment(sketch, "E1074", {"start": v(-43.45, -53.05) * mm, "end": v(-42.96, -55.38) * mm});
            skLineSegment(sketch, "E1075", {"start": v(-42.96, -55.38) * mm, "end": v(-42.85, -55.92) * mm});
            skLineSegment(sketch, "E1076", {"start": v(-42.85, -55.92) * mm, "end": v(-42.12, -59.94) * mm});
            skLineSegment(sketch, "E1077", {"start": v(-42.12, -59.94) * mm, "end": v(-41.85, -61.59) * mm});
            skLineSegment(sketch, "E1078", {"start": v(-41.85, -61.59) * mm, "end": v(-41.38, -64.4) * mm});
            skLineSegment(sketch, "E1079", {"start": v(-41.38, -64.4) * mm, "end": v(-40.92, -67.52) * mm});
            skLineSegment(sketch, "E1080", {"start": v(-40.92, -67.52) * mm, "end": v(-40.74, -68.72) * mm});
            skLineSegment(sketch, "E1081", {"start": v(-40.74, -68.72) * mm, "end": v(-40.21, -72.7) * mm});
            skLineSegment(sketch, "E1082", {"start": v(-40.21, -72.7) * mm, "end": v(-39.76, -76.95) * mm});
            skLineSegment(sketch, "E1083", {"start": v(-39.76, -76.95) * mm, "end": v(-39.69, -77.76) * mm});
            skLineSegment(sketch, "E1084", {"start": v(-39.69, -77.76) * mm, "end": v(-39.4, -80.92) * mm});
            skLineSegment(sketch, "E1085", {"start": v(-39.4, -80.92) * mm, "end": v(-39.3, -82.3) * mm});
            skLineSegment(sketch, "E1086", {"start": v(-39.3, -82.3) * mm, "end": v(-39.12, -84.8) * mm});
            skLineSegment(sketch, "E1087", {"start": v(-39.12, -84.8) * mm, "end": v(-39.01, -86.61) * mm});
            skLineSegment(sketch, "E1088", {"start": v(-39.01, -86.61) * mm, "end": v(-38.9, -88.64) * mm});
            skLineSegment(sketch, "E1089", {"start": v(-38.9, -88.64) * mm, "end": v(-38.8, -90.74) * mm});
            skLineSegment(sketch, "E1090", {"start": v(-38.8, -90.74) * mm, "end": v(-38.74, -92.42) * mm});
            skLineSegment(sketch, "E1091", {"start": v(-38.74, -92.42) * mm, "end": v(-38.68, -94.7) * mm});
            skLineSegment(sketch, "E1092", {"start": v(-38.68, -94.7) * mm, "end": v(-38.65, -96.18) * mm});
            skLineSegment(sketch, "E1093", {"start": v(-38.65, -96.18) * mm, "end": v(-38.63, -98.53) * mm});
            skLineSegment(sketch, "E1094", {"start": v(-38.63, -98.53) * mm, "end": v(-38.61, -99.93) * mm});
            skLineSegment(sketch, "E1095", {"start": v(-38.61, -99.93) * mm, "end": v(-38.63, -102.26) * mm});
            skLineSegment(sketch, "E1096", {"start": v(-38.63, -102.26) * mm, "end": v(-38.65, -103.67) * mm});
            skLineSegment(sketch, "E1097", {"start": v(-38.65, -103.67) * mm, "end": v(-38.7, -105.91) * mm});
            skLineSegment(sketch, "E1098", {"start": v(-38.7, -105.91) * mm, "end": v(-38.74, -107.43) * mm});
            skLineSegment(sketch, "E1099", {"start": v(-38.74, -107.43) * mm, "end": v(-38.82, -109.5) * mm});
            skLineSegment(sketch, "E1100", {"start": v(-38.82, -109.5) * mm, "end": v(-38.9, -111.22) * mm});
            skLineSegment(sketch, "E1101", {"start": v(-38.9, -111.22) * mm, "end": v(-39, -113.03) * mm});
            skLineSegment(sketch, "E1102", {"start": v(-39, -113.03) * mm, "end": v(-39.12, -115.05) * mm});
            skLineSegment(sketch, "E1103", {"start": v(-39.12, -115.05) * mm, "end": v(-39.22, -116.53) * mm});
            skLineSegment(sketch, "E1104", {"start": v(-39.22, -116.53) * mm, "end": v(-39.4, -118.94) * mm});
            skLineSegment(sketch, "E1105", {"start": v(-39.4, -118.94) * mm, "end": v(-39.5, -120.02) * mm});
            skLineSegment(sketch, "E1106", {"start": v(-39.5, -120.02) * mm, "end": v(-39.76, -122.9) * mm});
            skLineSegment(sketch, "E1107", {"start": v(-39.76, -122.9) * mm, "end": v(-39.82, -123.5) * mm});
            skLineSegment(sketch, "E1108", {"start": v(-39.82, -123.5) * mm, "end": v(-40.19, -126.96) * mm});
            skLineSegment(sketch, "E1109", {"start": v(-40.19, -126.96) * mm, "end": v(-40.64, -130.4) * mm});
            skLineSegment(sketch, "E1110", {"start": v(-40.64, -130.4) * mm, "end": v(-40.74, -131.14) * mm});
            skLineSegment(sketch, "E1111", {"start": v(-40.74, -131.14) * mm, "end": v(-41.14, -133.84) * mm});
            skLineSegment(sketch, "E1112", {"start": v(-41.14, -133.84) * mm, "end": v(-41.38, -135.44) * mm});
            skLineSegment(sketch, "E1113", {"start": v(-41.38, -135.44) * mm, "end": v(-41.7, -137.31) * mm});
            skLineSegment(sketch, "E1114", {"start": v(-41.7, -137.31) * mm, "end": v(-42.12, -139.91) * mm});
            skLineSegment(sketch, "E1115", {"start": v(-42.12, -139.91) * mm, "end": v(-42.29, -140.83) * mm});
            skLineSegment(sketch, "E1116", {"start": v(-42.29, -140.83) * mm, "end": v(-42.85, -143.93) * mm});
            skLineSegment(sketch, "E1117", {"start": v(-42.85, -143.93) * mm, "end": v(-42.96, -144.48) * mm});
            skLineSegment(sketch, "E1118", {"start": v(-42.96, -144.48) * mm, "end": v(-43.6, -147.44) * mm});
            skLineSegment(sketch, "E1119", {"start": v(-43.6, -147.44) * mm, "end": v(-43.84, -148.62) * mm});
            skLineSegment(sketch, "E1120", {"start": v(-43.84, -148.62) * mm, "end": v(-44.3, -150.6) * mm});
            skLineSegment(sketch, "E1121", {"start": v(-44.3, -150.6) * mm, "end": v(-44.8, -152.89) * mm});
            skLineSegment(sketch, "E1122", {"start": v(-44.8, -152.89) * mm, "end": v(-45.04, -153.81) * mm});
            skLineSegment(sketch, "E1123", {"start": v(-45.04, -153.81) * mm, "end": v(-45.67, -156.48) * mm});
            skLineSegment(sketch, "E1124", {"start": v(-45.67, -156.48) * mm, "end": v(-45.8, -157.05) * mm});
            skLineSegment(sketch, "E1125", {"start": v(-45.8, -157.05) * mm, "end": v(-45.9, -157.67) * mm});
            skLineSegment(sketch, "E1126", {"start": v(-45.9, -157.67) * mm, "end": v(-45.98, -158.26) * mm});
            skLineSegment(sketch, "E1127", {"start": v(-45.98, -158.26) * mm, "end": v(-46.03, -158.86) * mm});
            skLineSegment(sketch, "E1128", {"start": v(-46.03, -158.86) * mm, "end": v(-46.04, -159.46) * mm});
            skLineSegment(sketch, "E1129", {"start": v(-46.04, -159.46) * mm, "end": v(-46.04, -162.47) * mm});
            skLineSegment(sketch, "E1130", {"start": v(-46.04, -162.47) * mm, "end": v(-46.04, -163.08) * mm});
            skLineSegment(sketch, "E1131", {"start": v(-46.04, -163.08) * mm, "end": v(-46.04, -167.36) * mm});
            skLineSegment(sketch, "E1132", {"start": v(-46.04, -167.36) * mm, "end": v(-46.04, -169.1) * mm});
            skLineSegment(sketch, "E1133", {"start": v(-46.04, -169.1) * mm, "end": v(-46.04, -172.5) * mm});
            skLineSegment(sketch, "E1134", {"start": v(-46.04, -172.5) * mm, "end": v(-46.04, -175.54) * mm});
            skLineSegment(sketch, "E1135", {"start": v(-46.04, -175.54) * mm, "end": v(-46.04, -177.9) * mm});
            skLineSegment(sketch, "E1136", {"start": v(-46.04, -177.9) * mm, "end": v(-46.04, -182.5) * mm});
            skLineSegment(sketch, "E1137", {"start": v(-46.04, -182.5) * mm, "end": v(-46.04, -183.63) * mm});
            skLineSegment(sketch, "E1138", {"start": v(-46.04, -183.63) * mm, "end": v(-46.04, -188.35) * mm});
            skLineSegment(sketch, "E1139", {"start": v(-46.04, -188.35) * mm, "end": v(-46.01, -189.03) * mm});
            skLineSegment(sketch, "E1140", {"start": v(-46.01, -189.03) * mm, "end": v(-45.92, -189.75) * mm});
            skLineSegment(sketch, "E1141", {"start": v(-45.92, -189.75) * mm, "end": v(-45.76, -190.42) * mm});
            skLineSegment(sketch, "E1142", {"start": v(-45.76, -190.42) * mm, "end": v(-45.54, -191.04) * mm});
            skLineSegment(sketch, "E1143", {"start": v(-45.54, -191.04) * mm, "end": v(-45.27, -191.62) * mm});
            skLineSegment(sketch, "E1144", {"start": v(-45.27, -191.62) * mm, "end": v(-44.94, -192.14) * mm});
            skLineSegment(sketch, "E1145", {"start": v(-44.94, -192.14) * mm, "end": v(-44.57, -192.61) * mm});
            skLineSegment(sketch, "E1146", {"start": v(-44.57, -192.61) * mm, "end": v(-44.16, -193) * mm});
            skLineSegment(sketch, "E1147", {"start": v(-44.16, -193) * mm, "end": v(-43.71, -193.33) * mm});
            skLineSegment(sketch, "E1148", {"start": v(-43.71, -193.33) * mm, "end": v(-43.24, -193.58) * mm});
            skLineSegment(sketch, "E1149", {"start": v(-43.24, -193.58) * mm, "end": v(-35.52, -196.4) * mm});
            skLineSegment(sketch, "E1150", {"start": v(-35.52, -196.4) * mm, "end": v(-23.1, -200.8) * mm});
            skLineSegment(sketch, "E1151", {"start": v(-23.1, -200.8) * mm, "end": v(-23.1, -201.65) * mm});
            skLineSegment(sketch, "E1152", {"start": v(-23.1, -201.65) * mm, "end": v(-23.1, -207.58) * mm});
            skLineSegment(sketch, "E1153", {"start": v(-23.1, -207.58) * mm, "end": v(-23.1, -210.08) * mm});
            skLineSegment(sketch, "E1154", {"start": v(-23.1, -210.08) * mm, "end": v(-23.1, -213.9) * mm});
            skLineSegment(sketch, "E1155", {"start": v(-23.1, -213.9) * mm, "end": v(-23.1, -218.97) * mm});
            skLineSegment(sketch, "E1156", {"start": v(-23.1, -218.97) * mm, "end": v(-23.1, -220.62) * mm});
            skLineSegment(sketch, "E1157", {"start": v(-23.1, -220.62) * mm, "end": v(-23.1, -225.3) * mm});
            skLineSegment(sketch, "E1158", {"start": v(-23.1, -225.3) * mm, "end": v(-29.56, -225.7) * mm});
            skLineSegment(sketch, "E1159", {"start": v(-29.56, -225.7) * mm, "end": v(-42.25, -226.52) * mm});
            skLineSegment(sketch, "E1160", {"start": v(-42.25, -226.52) * mm, "end": v(-42.77, -226.6) * mm});
            skLineSegment(sketch, "E1161", {"start": v(-42.77, -226.6) * mm, "end": v(-43.27, -226.75) * mm});
            skLineSegment(sketch, "E1162", {"start": v(-43.27, -226.75) * mm, "end": v(-43.76, -226.98) * mm});
            skLineSegment(sketch, "E1163", {"start": v(-43.76, -226.98) * mm, "end": v(-44.18, -227.27) * mm});
            skLineSegment(sketch, "E1164", {"start": v(-44.18, -227.27) * mm, "end": v(-44.6, -227.64) * mm});
            skLineSegment(sketch, "E1165", {"start": v(-44.6, -227.64) * mm, "end": v(-44.99, -228.09) * mm});
            skLineSegment(sketch, "E1166", {"start": v(-44.99, -228.09) * mm, "end": v(-45.32, -228.59) * mm});
            skLineSegment(sketch, "E1167", {"start": v(-45.32, -228.59) * mm, "end": v(-45.6, -229.14) * mm});
            skLineSegment(sketch, "E1168", {"start": v(-45.6, -229.14) * mm, "end": v(-45.8, -229.7) * mm});
            skLineSegment(sketch, "E1169", {"start": v(-45.8, -229.7) * mm, "end": v(-45.95, -230.3) * mm});
            skLineSegment(sketch, "E1170", {"start": v(-45.95, -230.3) * mm, "end": v(-46.03, -230.91) * mm});
            skLineSegment(sketch, "E1171", {"start": v(-46.03, -230.91) * mm, "end": v(-46.04, -234.92) * mm});
            skLineSegment(sketch, "E1172", {"start": v(-46.04, -234.92) * mm, "end": v(-46.04, -237.96) * mm});
            skLineSegment(sketch, "E1173", {"start": v(-46.04, -237.96) * mm, "end": v(-46.04, -239.35) * mm});
            skLineSegment(sketch, "E1174", {"start": v(-46.04, -239.35) * mm, "end": v(-46.04, -241.02) * mm});
            skLineSegment(sketch, "E1175", {"start": v(-46.04, -241.02) * mm, "end": v(-46, -241.63) * mm});
            skLineSegment(sketch, "E1176", {"start": v(-46, -241.63) * mm, "end": v(-45.9, -242.23) * mm});
            skLineSegment(sketch, "E1177", {"start": v(-45.9, -242.23) * mm, "end": v(-45.74, -242.8) * mm});
            skLineSegment(sketch, "E1178", {"start": v(-45.74, -242.8) * mm, "end": v(-45.54, -243.28) * mm});
            skLineSegment(sketch, "E1179", {"start": v(-45.54, -243.28) * mm, "end": v(-45.26, -243.8) * mm});
            skLineSegment(sketch, "E1180", {"start": v(-45.26, -243.8) * mm, "end": v(-44.91, -244.27) * mm});
            skLineSegment(sketch, "E1181", {"start": v(-44.91, -244.27) * mm, "end": v(-44.52, -244.68) * mm});
            skLineSegment(sketch, "E1182", {"start": v(-44.52, -244.68) * mm, "end": v(-44.09, -245.03) * mm});
            skLineSegment(sketch, "E1183", {"start": v(-44.09, -245.03) * mm, "end": v(-43.62, -245.3) * mm});
            skLineSegment(sketch, "E1184", {"start": v(-43.62, -245.3) * mm, "end": v(-43.12, -245.51) * mm});
            skLineSegment(sketch, "E1185", {"start": v(-43.12, -245.51) * mm, "end": v(-42.6, -245.64) * mm});
            skLineSegment(sketch, "E1186", {"start": v(-42.6, -245.64) * mm, "end": v(-33.52, -246.59) * mm});
            skLineSegment(sketch, "E1187", {"start": v(-33.52, -246.59) * mm, "end": v(-24.77, -247.44) * mm});
            skLineSegment(sketch, "E1188", {"start": v(-24.77, -247.44) * mm, "end": v(-15.1, -248.41) * mm});
            skLineSegment(sketch, "E1189", {"start": v(-15.1, -248.41) * mm, "end": v(-15.1, -242.46) * mm});
            skLineSegment(sketch, "E1190", {"start": v(-15.1, -242.46) * mm, "end": v(-15.1, -229.51) * mm});
            skLineSegment(sketch, "E1191", {"start": v(-15.1, -229.51) * mm, "end": v(-15.1, -222.86) * mm});
            skLineSegment(sketch, "E1192", {"start": v(-15.1, -222.86) * mm, "end": v(-19.1, -222.7) * mm});
            skLineSegment(sketch, "E1193", {"start": v(-19.1, -222.7) * mm, "end": v(-19.1, -219.7) * mm});
            skLineSegment(sketch, "E1194", {"start": v(-19.1, -219.7) * mm, "end": v(-15.25, -219.7) * mm});
            skLineSegment(sketch, "E1195", {"start": v(-15.25, -219.7) * mm, "end": v(-15.1, -218.14) * mm});
            skLineSegment(sketch, "E1196", {"start": v(-15.1, -218.14) * mm, "end": v(-15.1, -217.56) * mm});
            skLineSegment(sketch, "E1197", {"start": v(-15.1, -217.56) * mm, "end": v(-15.1, -208.04) * mm});
            skLineSegment(sketch, "E1198", {"start": v(-15.1, -208.04) * mm, "end": v(-15.1, -207.32) * mm});
            skLineSegment(sketch, "E1199", {"start": v(-15.1, -207.32) * mm, "end": v(-15.1, -198.98) * mm});
            skLineSegment(sketch, "E1200", {"start": v(-15.1, -198.98) * mm, "end": v(-15.1, -198.15) * mm});
            skLineSegment(sketch, "E1201", {"start": v(-15.1, -198.15) * mm, "end": v(-15.1, -190.76) * mm});
            skLineSegment(sketch, "E1202", {"start": v(-15.1, -190.76) * mm, "end": v(-15.1, -189.86) * mm});
            skLineSegment(sketch, "E1203", {"start": v(-15.1, -189.86) * mm, "end": v(-15.25, -189.25) * mm});
            skLineSegment(sketch, "E1204", {"start": v(-15.25, -189.25) * mm, "end": v(-30.57, -189.25) * mm});
            skLineSegment(sketch, "E1205", {"start": v(-30.57, -189.25) * mm, "end": v(-30.57, -186.25) * mm});
            skLineSegment(sketch, "E1206", {"start": v(-30.57, -186.25) * mm, "end": v(-15.25, -186.25) * mm});
            skLineSegment(sketch, "E1207", {"start": v(-15.25, -186.25) * mm, "end": v(-15.1, -183.26) * mm});
            skLineSegment(sketch, "E1208", {"start": v(-15.1, -183.26) * mm, "end": v(-15.1, -182.3) * mm});
            skLineSegment(sketch, "E1209", {"start": v(-15.1, -182.3) * mm, "end": v(-15.1, -176.36) * mm});
            skLineSegment(sketch, "E1210", {"start": v(-15.1, -176.36) * mm, "end": v(-15.1, -175.35) * mm});
            skLineSegment(sketch, "E1211", {"start": v(-15.1, -175.35) * mm, "end": v(-15.1, -169.97) * mm});
            skLineSegment(sketch, "E1212", {"start": v(-15.1, -169.97) * mm, "end": v(-15.1, -168.92) * mm});
            skLineSegment(sketch, "E1213", {"start": v(-15.1, -168.92) * mm, "end": v(-15.1, -164) * mm});
            skLineSegment(sketch, "E1214", {"start": v(-15.1, -164) * mm, "end": v(-15.1, -162.94) * mm});
            skLineSegment(sketch, "E1215", {"start": v(-15.1, -162.94) * mm, "end": v(-15.1, -158.42) * mm});
            skLineSegment(sketch, "E1216", {"start": v(-15.1, -158.42) * mm, "end": v(-15.1, -157.33) * mm});
            skLineSegment(sketch, "E1217", {"start": v(-15.1, -157.33) * mm, "end": v(-15.1, -155.95) * mm});
            skLineSegment(sketch, "E1218", {"start": v(-15.1, -155.95) * mm, "end": v(-30.3, -155.8) * mm});
            skLineSegment(sketch, "E1219", {"start": v(-30.3, -155.8) * mm, "end": v(-30.3, -152.8) * mm});
            skLineSegment(sketch, "E1220", {"start": v(-30.3, -152.8) * mm, "end": v(-15.25, -152.8) * mm});
            skLineSegment(sketch, "E1221", {"start": v(-15.25, -152.8) * mm, "end": v(-15.1, -152.04) * mm});
            skLineSegment(sketch, "E1222", {"start": v(-15.1, -152.04) * mm, "end": v(-15.1, -148.14) * mm});
            skLineSegment(sketch, "E1223", {"start": v(-15.1, -148.14) * mm, "end": v(-15.1, -147.03) * mm});
            skLineSegment(sketch, "E1224", {"start": v(-15.1, -147.03) * mm, "end": v(-15.1, -143.38) * mm});
            skLineSegment(sketch, "E1225", {"start": v(-15.1, -143.38) * mm, "end": v(-15.1, -142.25) * mm});
            skLineSegment(sketch, "E1226", {"start": v(-15.1, -142.25) * mm, "end": v(-15.1, -138.81) * mm});
            skLineSegment(sketch, "E1227", {"start": v(-15.1, -138.81) * mm, "end": v(-15.1, -137.68) * mm});
            skLineSegment(sketch, "E1228", {"start": v(-15.1, -137.68) * mm, "end": v(-15.1, -134.42) * mm});
            skLineSegment(sketch, "E1229", {"start": v(-15.1, -134.42) * mm, "end": v(-15.1, -133.29) * mm});
            skLineSegment(sketch, "E1230", {"start": v(-15.1, -133.29) * mm, "end": v(-15.1, -130.18) * mm});
            skLineSegment(sketch, "E1231", {"start": v(-15.1, -130.18) * mm, "end": v(-15.1, -129.04) * mm});
            skLineSegment(sketch, "E1232", {"start": v(-15.1, -129.04) * mm, "end": v(-15.1, -126.06) * mm});
            skLineSegment(sketch, "E1233", {"start": v(-15.1, -126.06) * mm, "end": v(-15.1, -124.93) * mm});
            skLineSegment(sketch, "E1234", {"start": v(-15.1, -124.93) * mm, "end": v(-15.1, -122.5) * mm});
            skLineSegment(sketch, "E1235", {"start": v(-15.1, -122.5) * mm, "end": v(-27.4, -122.34) * mm});
            skLineSegment(sketch, "E1236", {"start": v(-27.4, -122.34) * mm, "end": v(-27.4, -119.34) * mm});
            skLineSegment(sketch, "E1237", {"start": v(-27.4, -119.34) * mm, "end": v(-15.25, -119.34) * mm});
            skLineSegment(sketch, "E1238", {"start": v(-15.25, -119.34) * mm, "end": v(-15.1, -118.13) * mm});
            skLineSegment(sketch, "E1239", {"start": v(-15.1, -118.13) * mm, "end": v(-15.1, -117) * mm});
            skLineSegment(sketch, "E1240", {"start": v(-15.1, -117) * mm, "end": v(-15.1, -114.28) * mm});
            skLineSegment(sketch, "E1241", {"start": v(-15.1, -114.28) * mm, "end": v(-15.1, -113.14) * mm});
            skLineSegment(sketch, "E1242", {"start": v(-15.1, -113.14) * mm, "end": v(-15.1, -110.48) * mm});
            skLineSegment(sketch, "E1243", {"start": v(-15.1, -110.48) * mm, "end": v(-15.1, -109.34) * mm});
            skLineSegment(sketch, "E1244", {"start": v(-15.1, -109.34) * mm, "end": v(-15.1, -106.72) * mm});
            skLineSegment(sketch, "E1245", {"start": v(-15.1, -106.72) * mm, "end": v(-15.1, -105.58) * mm});
            skLineSegment(sketch, "E1246", {"start": v(-15.1, -105.58) * mm, "end": v(-15.1, -102.98) * mm});
            skLineSegment(sketch, "E1247", {"start": v(-15.1, -102.98) * mm, "end": v(-15.1, -101.85) * mm});
            skLineSegment(sketch, "E1248", {"start": v(-15.1, -101.85) * mm, "end": v(-15.1, -99.26) * mm});
            skLineSegment(sketch, "E1249", {"start": v(-15.1, -99.26) * mm, "end": v(-15.1, -98.12) * mm});
            skLineSegment(sketch, "E1250", {"start": v(-15.1, -98.12) * mm, "end": v(-15.1, -95.53) * mm});
            skLineSegment(sketch, "E1251", {"start": v(-15.1, -95.53) * mm, "end": v(-15.1, -94.4) * mm});
            skLineSegment(sketch, "E1252", {"start": v(-15.1, -94.4) * mm, "end": v(-15.1, -91.78) * mm});
            skLineSegment(sketch, "E1253", {"start": v(-15.1, -91.78) * mm, "end": v(-15.1, -90.65) * mm});
            skLineSegment(sketch, "E1254", {"start": v(-15.1, -90.65) * mm, "end": v(-15.1, -89.04) * mm});
            skLineSegment(sketch, "E1255", {"start": v(-15.1, -89.04) * mm, "end": v(-27.07, -88.89) * mm});
            skLineSegment(sketch, "E1256", {"start": v(-27.07, -88.89) * mm, "end": v(-27.07, -85.89) * mm});
            skLineSegment(sketch, "E1257", {"start": v(-27.07, -85.89) * mm, "end": v(-15.25, -85.89) * mm});
            skLineSegment(sketch, "E1258", {"start": v(-15.25, -85.89) * mm, "end": v(-15.1, -84.18) * mm});
            skLineSegment(sketch, "E1259", {"start": v(-15.1, -84.18) * mm, "end": v(-15.1, -83.04) * mm});
            skLineSegment(sketch, "E1260", {"start": v(-15.1, -83.04) * mm, "end": v(-15.1, -81.92) * mm});
            skLineSegment(sketch, "E1261", {"start": v(-15.1, -81.92) * mm, "end": v(-15.1, -80.8) * mm});
            skLineSegment(sketch, "E1262", {"start": v(-15.1, -80.8) * mm, "end": v(-15.1, -79.7) * mm});
            skLineSegment(sketch, "E1263", {"start": v(-15.1, -79.7) * mm, "end": v(-15.1, -78.63) * mm});
            skLineSegment(sketch, "E1264", {"start": v(-15.1, -78.63) * mm, "end": v(-15.1, -77.57) * mm});
            skLineSegment(sketch, "E1265", {"start": v(-15.1, -77.57) * mm, "end": v(-15.1, -76.55) * mm});
            skLineSegment(sketch, "E1266", {"start": v(-15.1, -76.55) * mm, "end": v(-15.1, -75.55) * mm});
            skLineSegment(sketch, "E1267", {"start": v(-15.1, -75.55) * mm, "end": v(-15.1, -74.58) * mm});
            skLineSegment(sketch, "E1268", {"start": v(-15.1, -74.58) * mm, "end": v(-15.1, -73.66) * mm});
            skLineSegment(sketch, "E1269", {"start": v(-15.1, -73.66) * mm, "end": v(-15.1, -55.58) * mm});
            skLineSegment(sketch, "E1270", {"start": v(-15.1, -55.58) * mm, "end": v(-29.34, -55.43) * mm});
            skLineSegment(sketch, "E1271", {"start": v(-29.34, -55.43) * mm, "end": v(-29.34, -52.43) * mm});
            skLineSegment(sketch, "E1272", {"start": v(-29.34, -52.43) * mm, "end": v(-15.25, -52.43) * mm});
            skLineSegment(sketch, "E1273", {"start": v(-15.25, -52.43) * mm, "end": v(-15.1, -22.13) * mm});
            skLineSegment(sketch, "E1274", {"start": v(-15.1, -22.13) * mm, "end": v(-28.26, -21.98) * mm});
            skLineSegment(sketch, "E1275", {"start": v(-28.26, -21.98) * mm, "end": v(-28.26, -18.98) * mm});
            skLineSegment(sketch, "E1276", {"start": v(-28.26, -18.98) * mm, "end": v(-15.25, -18.98) * mm});
            skLineSegment(sketch, "E1277", {"start": v(-15.25, -18.98) * mm, "end": v(-15.1, 11.33) * mm});
            skLineSegment(sketch, "E1278", {"start": v(-15.1, 11.33) * mm, "end": v(-19.1, 11.48) * mm});
            skLineSegment(sketch, "E1279", {"start": v(-19.1, 11.48) * mm, "end": v(-19.1, 14.48) * mm});
            skLineSegment(sketch, "E1280", {"start": v(-19.1, 14.48) * mm, "end": v(-15.25, 14.48) * mm});
            skLineSegment(sketch, "E1281", {"start": v(-15.25, 14.48) * mm, "end": v(-15.1, 31.66) * mm});
            skLineSegment(sketch, "E1282", {"start": v(-15.1, 31.66) * mm, "end": v(-15.1, 33.3) * mm});
            skLineSegment(sketch, "E1283", {"start": v(-15.1, 33.3) * mm, "end": v(-15.1, 34.92) * mm});
            skLineSegment(sketch, "E1284", {"start": v(-15.1, 34.92) * mm, "end": v(-15.1, 36.54) * mm});
            skLineSegment(sketch, "E1285", {"start": v(-15.1, 36.54) * mm, "end": v(-15.1, 38.16) * mm});
            skLineSegment(sketch, "E1286", {"start": v(-15.1, 38.16) * mm, "end": v(-15.1, 39.75) * mm});
            skLineSegment(sketch, "E1287", {"start": v(-15.1, 39.75) * mm, "end": v(-15.1, 41.33) * mm});
            skLineSegment(sketch, "E1288", {"start": v(-15.1, 41.33) * mm, "end": v(-15.1, 42.88) * mm});
            skLineSegment(sketch, "E1289", {"start": v(-15.1, 42.88) * mm, "end": v(-15.1, 44.4) * mm});
            skLineSegment(sketch, "E1290", {"start": v(-15.1, 44.4) * mm, "end": v(-15.25, 44.93) * mm});
            skLineSegment(sketch, "E1291", {"start": v(-15.25, 44.93) * mm, "end": v(-19.1, 44.93) * mm});
            skLineSegment(sketch, "E1292", {"start": v(-19.1, 44.93) * mm, "end": v(-19.1, 47.93) * mm});
            skLineSegment(sketch, "E1293", {"start": v(-19.1, 47.93) * mm, "end": v(-15.25, 47.93) * mm});
            skLineSegment(sketch, "E1294", {"start": v(-15.25, 47.93) * mm, "end": v(-15.1, 48.58) * mm});
            skLineSegment(sketch, "E1295", {"start": v(-15.1, 48.58) * mm, "end": v(-15.1, 49.14) * mm});
            skLineSegment(sketch, "E1296", {"start": v(-15.1, 49.14) * mm, "end": v(-15.1, 49.73) * mm});
            skLineSegment(sketch, "E1297", {"start": v(-15.1, 49.73) * mm, "end": v(-15.1, 50.34) * mm});
            skLineSegment(sketch, "E1298", {"start": v(-15.1, 50.34) * mm, "end": v(-15.1, 50.97) * mm});
            skLineSegment(sketch, "E1299", {"start": v(-15.1, 50.97) * mm, "end": v(-15.1, 51.6) * mm});
            skLineSegment(sketch, "E1300", {"start": v(-15.1, 51.6) * mm, "end": v(-15.1, 52.23) * mm});
            skLineSegment(sketch, "E1301", {"start": v(-15.1, 52.23) * mm, "end": v(-15.1, 52.84) * mm});
            skLineSegment(sketch, "E1302", {"start": v(-15.1, 52.84) * mm, "end": v(-15.1, 54.63) * mm});
            skLineSegment(sketch, "E1303", {"start": v(-15.1, 54.63) * mm, "end": v(-15.1, 56.18) * mm});
            skLineSegment(sketch, "E1304", {"start": v(-15.1, 56.18) * mm, "end": v(-15.1, 57.49) * mm});
            skLineSegment(sketch, "E1305", {"start": v(-15.1, 57.49) * mm, "end": v(-15.1, 58.75) * mm});
            skLineSegment(sketch, "E1306", {"start": v(-15.1, 58.75) * mm, "end": v(-15.1, 59.97) * mm});
            skLineSegment(sketch, "E1307", {"start": v(-15.1, 59.97) * mm, "end": v(-15.1, 61.14) * mm});
            skLineSegment(sketch, "E1308", {"start": v(-15.1, 61.14) * mm, "end": v(-15.1, 62.27) * mm});
            skLineSegment(sketch, "E1309", {"start": v(-15.1, 62.27) * mm, "end": v(-15.1, 63.35) * mm});
            skLineSegment(sketch, "E1310", {"start": v(-15.1, 63.35) * mm, "end": v(-15.1, 64.37) * mm});
            skLineSegment(sketch, "E1311", {"start": v(-15.1, 64.37) * mm, "end": v(-15.1, 65.35) * mm});
            skLineSegment(sketch, "E1312", {"start": v(-15.1, 65.35) * mm, "end": v(-15.1, 66.28) * mm});
            skLineSegment(sketch, "E1313", {"start": v(-15.1, 66.28) * mm, "end": v(-15.1, 67.16) * mm});
            skLineSegment(sketch, "E1314", {"start": v(-15.1, 67.16) * mm, "end": v(-15.1, 68) * mm});
            skLineSegment(sketch, "E1315", {"start": v(-15.1, 68) * mm, "end": v(-15.1, 78.24) * mm});
            skLineSegment(sketch, "E1316", {"start": v(-15.1, 78.24) * mm, "end": v(-19.1, 78.4) * mm});
            skLineSegment(sketch, "E1317", {"start": v(-19.1, 78.4) * mm, "end": v(-19.1, 81.4) * mm});
            skLineSegment(sketch, "E1318", {"start": v(-19.1, 81.4) * mm, "end": v(-15.25, 81.4) * mm});
            skLineSegment(sketch, "E1319", {"start": v(-15.25, 81.4) * mm, "end": v(-15.1, 111.7) * mm});
            skLineSegment(sketch, "E1320", {"start": v(-15.1, 111.7) * mm, "end": v(-19.1, 111.85) * mm});
            skLineSegment(sketch, "E1321", {"start": v(-19.1, 111.85) * mm, "end": v(-19.1, 114.85) * mm});
            skLineSegment(sketch, "E1322", {"start": v(-19.1, 114.85) * mm, "end": v(-15.25, 114.85) * mm});
            skLineSegment(sketch, "E1323", {"start": v(-15.25, 114.85) * mm, "end": v(-15.1, 130.07) * mm});
            skLineSegment(sketch, "E1324", {"start": v(13.49, 104.02) * mm, "end": v(10.9, 104.02) * mm});
            skLineSegment(sketch, "E1325", {"start": v(10.9, 104.02) * mm, "end": v(10.4, 104.01) * mm});
            skLineSegment(sketch, "E1326", {"start": v(10.4, 104.01) * mm, "end": v(9.82, 103.93) * mm});
            skLineSegment(sketch, "E1327", {"start": v(9.82, 103.93) * mm, "end": v(9.3, 103.78) * mm});
            skLineSegment(sketch, "E1328", {"start": v(9.3, 103.78) * mm, "end": v(8.83, 103.57) * mm});
            skLineSegment(sketch, "E1329", {"start": v(8.83, 103.57) * mm, "end": v(8.38, 103.3) * mm});
            skLineSegment(sketch, "E1330", {"start": v(8.38, 103.3) * mm, "end": v(7.97, 102.98) * mm});
            skLineSegment(sketch, "E1331", {"start": v(7.97, 102.98) * mm, "end": v(7.61, 102.6) * mm});
            skLineSegment(sketch, "E1332", {"start": v(7.61, 102.6) * mm, "end": v(7.3, 102.19) * mm});
            skLineSegment(sketch, "E1333", {"start": v(7.3, 102.19) * mm, "end": v(7.05, 101.73) * mm});
            skLineSegment(sketch, "E1334", {"start": v(7.05, 101.73) * mm, "end": v(6.86, 101.25) * mm});
            skLineSegment(sketch, "E1335", {"start": v(6.86, 101.25) * mm, "end": v(6.73, 100.74) * mm});
            skLineSegment(sketch, "E1336", {"start": v(6.73, 100.74) * mm, "end": v(4.9, 81.62) * mm});
            skLineSegment(sketch, "E1337", {"start": v(4.9, 81.62) * mm, "end": v(4.81, 80.71) * mm});
            skLineSegment(sketch, "E1338", {"start": v(4.81, 80.71) * mm, "end": v(4.74, 79.85) * mm});
            skLineSegment(sketch, "E1339", {"start": v(4.74, 79.85) * mm, "end": v(4.67, 78.95) * mm});
            skLineSegment(sketch, "E1340", {"start": v(4.67, 78.95) * mm, "end": v(4.61, 78.06) * mm});
            skLineSegment(sketch, "E1341", {"start": v(4.61, 78.06) * mm, "end": v(4.56, 77.12) * mm});
            skLineSegment(sketch, "E1342", {"start": v(4.56, 77.12) * mm, "end": v(4.51, 76.23) * mm});
            skLineSegment(sketch, "E1343", {"start": v(4.51, 76.23) * mm, "end": v(4.48, 75.36) * mm});
            skLineSegment(sketch, "E1344", {"start": v(4.48, 75.36) * mm, "end": v(4.45, 74.5) * mm});
            skLineSegment(sketch, "E1345", {"start": v(4.45, 74.5) * mm, "end": v(4.43, 73.64) * mm});
            skLineSegment(sketch, "E1346", {"start": v(4.43, 73.64) * mm, "end": v(4.42, 72.8) * mm});
            skLineSegment(sketch, "E1347", {"start": v(4.42, 72.8) * mm, "end": v(4.41, 71.97) * mm});
            skLineSegment(sketch, "E1348", {"start": v(4.41, 71.97) * mm, "end": v(4.42, 71.17) * mm});
            skLineSegment(sketch, "E1349", {"start": v(4.42, 71.17) * mm, "end": v(4.43, 70.38) * mm});
            skLineSegment(sketch, "E1350", {"start": v(4.43, 70.38) * mm, "end": v(4.45, 69.61) * mm});
            skLineSegment(sketch, "E1351", {"start": v(4.45, 69.61) * mm, "end": v(4.48, 68.86) * mm});
            skLineSegment(sketch, "E1352", {"start": v(4.48, 68.86) * mm, "end": v(4.51, 68.14) * mm});
            skLineSegment(sketch, "E1353", {"start": v(4.51, 68.14) * mm, "end": v(4.56, 67.44) * mm});
            skLineSegment(sketch, "E1354", {"start": v(4.56, 67.44) * mm, "end": v(4.6, 66.76) * mm});
            skLineSegment(sketch, "E1355", {"start": v(4.6, 66.76) * mm, "end": v(4.67, 66.11) * mm});
            skLineSegment(sketch, "E1356", {"start": v(4.67, 66.11) * mm, "end": v(4.74, 65.49) * mm});
            skLineSegment(sketch, "E1357", {"start": v(4.74, 65.49) * mm, "end": v(4.81, 64.9) * mm});
            skLineSegment(sketch, "E1358", {"start": v(4.81, 64.9) * mm, "end": v(4.9, 64.33) * mm});
            skLineSegment(sketch, "E1359", {"start": v(4.9, 64.33) * mm, "end": v(4.98, 63.8) * mm});
            skLineSegment(sketch, "E1360", {"start": v(4.98, 63.8) * mm, "end": v(5.08, 63.3) * mm});
            skLineSegment(sketch, "E1361", {"start": v(5.08, 63.3) * mm, "end": v(5.2, 62.76) * mm});
            skLineSegment(sketch, "E1362", {"start": v(5.2, 62.76) * mm, "end": v(5.33, 62.27) * mm});
            skLineSegment(sketch, "E1363", {"start": v(5.33, 62.27) * mm, "end": v(5.53, 61.63) * mm});
            skLineSegment(sketch, "E1364", {"start": v(5.53, 61.63) * mm, "end": v(5.8, 61) * mm});
            skLineSegment(sketch, "E1365", {"start": v(5.8, 61) * mm, "end": v(6.09, 60.53) * mm});
            skLineSegment(sketch, "E1366", {"start": v(6.09, 60.53) * mm, "end": v(6.45, 60.16) * mm});
            skLineSegment(sketch, "E1367", {"start": v(6.45, 60.16) * mm, "end": v(7.16, 59.9) * mm});
            skLineSegment(sketch, "E1368", {"start": v(7.16, 59.9) * mm, "end": v(11.03, 58.8) * mm});
            skLineSegment(sketch, "E1369", {"start": v(11.03, 58.8) * mm, "end": v(11.03, -40.89) * mm});
            skLineSegment(sketch, "E1370", {"start": v(11.03, -40.89) * mm, "end": v(11.03, -70.06) * mm});
            skLineSegment(sketch, "E1371", {"start": v(11.03, -70.06) * mm, "end": v(4.9, -74.2) * mm});
            skLineSegment(sketch, "E1372", {"start": v(4.9, -74.2) * mm, "end": v(3.2, -75.3) * mm});
            skLineSegment(sketch, "E1373", {"start": v(3.2, -75.3) * mm, "end": v(1.8, -76.25) * mm});
            skLineSegment(sketch, "E1374", {"start": v(1.8, -76.25) * mm, "end": v(-1.09, -78.4) * mm});
            skLineSegment(sketch, "E1375", {"start": v(-1.09, -78.4) * mm, "end": v(-4.01, -80.49) * mm});
            skLineSegment(sketch, "E1376", {"start": v(-4.01, -80.49) * mm, "end": v(-6.36, -82.29) * mm});
            skLineSegment(sketch, "E1377", {"start": v(-6.36, -82.29) * mm, "end": v(-6.78, -82.64) * mm});
            skLineSegment(sketch, "E1378", {"start": v(-6.78, -82.64) * mm, "end": v(-7.97, -83.6) * mm});
            skLineSegment(sketch, "E1379", {"start": v(-7.97, -83.6) * mm, "end": v(-8.33, -83.98) * mm});
            skLineSegment(sketch, "E1380", {"start": v(-8.33, -83.98) * mm, "end": v(-8.68, -84.4) * mm});
            skLineSegment(sketch, "E1381", {"start": v(-8.68, -84.4) * mm, "end": v(-9, -84.85) * mm});
            skLineSegment(sketch, "E1382", {"start": v(-9, -84.85) * mm, "end": v(-9.36, -85.45) * mm});
            skLineSegment(sketch, "E1383", {"start": v(-9.36, -85.45) * mm, "end": v(-9.7, -86.17) * mm});
            skLineSegment(sketch, "E1384", {"start": v(-9.7, -86.17) * mm, "end": v(-9.9, -86.64) * mm});
            skLineSegment(sketch, "E1385", {"start": v(-9.9, -86.64) * mm, "end": v(-10.19, -87.45) * mm});
            skLineSegment(sketch, "E1386", {"start": v(-10.19, -87.45) * mm, "end": v(-10.4, -88.12) * mm});
            skLineSegment(sketch, "E1387", {"start": v(-10.4, -88.12) * mm, "end": v(-10.57, -88.66) * mm});
            skLineSegment(sketch, "E1388", {"start": v(-10.57, -88.66) * mm, "end": v(-10.73, -89.22) * mm});
            skLineSegment(sketch, "E1389", {"start": v(-10.73, -89.22) * mm, "end": v(-10.88, -89.8) * mm});
            skLineSegment(sketch, "E1390", {"start": v(-10.88, -89.8) * mm, "end": v(-11.03, -90.4) * mm});
            skLineSegment(sketch, "E1391", {"start": v(-11.03, -90.4) * mm, "end": v(-11.17, -91.01) * mm});
            skLineSegment(sketch, "E1392", {"start": v(-11.17, -91.01) * mm, "end": v(-11.3, -91.62) * mm});
            skLineSegment(sketch, "E1393", {"start": v(-11.3, -91.62) * mm, "end": v(-11.4, -92.19) * mm});
            skLineSegment(sketch, "E1394", {"start": v(-11.4, -92.19) * mm, "end": v(-11.53, -92.88) * mm});
            skLineSegment(sketch, "E1395", {"start": v(-11.53, -92.88) * mm, "end": v(-11.63, -93.49) * mm});
            skLineSegment(sketch, "E1396", {"start": v(-11.63, -93.49) * mm, "end": v(-11.72, -94.08) * mm});
            skLineSegment(sketch, "E1397", {"start": v(-11.72, -94.08) * mm, "end": v(-11.8, -94.62) * mm});
            skLineSegment(sketch, "E1398", {"start": v(-11.8, -94.62) * mm, "end": v(-11.86, -95.32) * mm});
            skLineSegment(sketch, "E1399", {"start": v(-11.86, -95.32) * mm, "end": v(-11.88, -95.95) * mm});
            skLineSegment(sketch, "E1400", {"start": v(-11.88, -95.95) * mm, "end": v(-11.9, -96.8) * mm});
            skLineSegment(sketch, "E1401", {"start": v(-11.9, -96.8) * mm, "end": v(-11.92, -97.54) * mm});
            skLineSegment(sketch, "E1402", {"start": v(-11.92, -97.54) * mm, "end": v(-11.92, -98.4) * mm});
            skLineSegment(sketch, "E1403", {"start": v(-11.92, -98.4) * mm, "end": v(-11.92, -102.75) * mm});
            skLineSegment(sketch, "E1404", {"start": v(-11.92, -102.75) * mm, "end": v(-11.92, -107.9) * mm});
            skLineSegment(sketch, "E1405", {"start": v(-11.92, -107.9) * mm, "end": v(-11.92, -113.02) * mm});
            skLineSegment(sketch, "E1406", {"start": v(-11.92, -113.02) * mm, "end": v(-11.92, -113.61) * mm});
            skLineSegment(sketch, "E1407", {"start": v(-11.92, -113.61) * mm, "end": v(-11.92, -118.16) * mm});
            skLineSegment(sketch, "E1408", {"start": v(-11.92, -118.16) * mm, "end": v(-11.92, -118.86) * mm});
            skLineSegment(sketch, "E1409", {"start": v(-11.92, -118.86) * mm, "end": v(-11.92, -123.33) * mm});
            skLineSegment(sketch, "E1410", {"start": v(-11.92, -123.33) * mm, "end": v(-11.92, -124.08) * mm});
            skLineSegment(sketch, "E1411", {"start": v(-11.92, -124.08) * mm, "end": v(-11.92, -128.55) * mm});
            skLineSegment(sketch, "E1412", {"start": v(-11.92, -128.55) * mm, "end": v(-11.92, -129.3) * mm});
            skLineSegment(sketch, "E1413", {"start": v(-11.92, -129.3) * mm, "end": v(-11.92, -133.84) * mm});
            skLineSegment(sketch, "E1414", {"start": v(-11.92, -133.84) * mm, "end": v(-11.92, -134.54) * mm});
            skLineSegment(sketch, "E1415", {"start": v(-11.92, -134.54) * mm, "end": v(-11.92, -139.22) * mm});
            skLineSegment(sketch, "E1416", {"start": v(-11.92, -139.22) * mm, "end": v(-11.92, -139.8) * mm});
            skLineSegment(sketch, "E1417", {"start": v(-11.92, -139.8) * mm, "end": v(-11.92, -144.73) * mm});
            skLineSegment(sketch, "E1418", {"start": v(-11.92, -144.73) * mm, "end": v(-11.92, -150.38) * mm});
            skLineSegment(sketch, "E1419", {"start": v(-11.92, -150.38) * mm, "end": v(-11.92, -153.5) * mm});
            skLineSegment(sketch, "E1420", {"start": v(-11.92, -153.5) * mm, "end": v(-11.92, -154.27) * mm});
            skLineSegment(sketch, "E1421", {"start": v(-11.92, -154.27) * mm, "end": v(-11.9, -155.03) * mm});
            skLineSegment(sketch, "E1422", {"start": v(-11.9, -155.03) * mm, "end": v(-11.89, -155.78) * mm});
            skLineSegment(sketch, "E1423", {"start": v(-11.89, -155.78) * mm, "end": v(-11.86, -156.42) * mm});
            skLineSegment(sketch, "E1424", {"start": v(-11.86, -156.42) * mm, "end": v(-11.84, -156.98) * mm});
            skLineSegment(sketch, "E1425", {"start": v(-11.84, -156.98) * mm, "end": v(-11.8, -157.54) * mm});
            skLineSegment(sketch, "E1426", {"start": v(-11.8, -157.54) * mm, "end": v(-11.76, -158.1) * mm});
            skLineSegment(sketch, "E1427", {"start": v(-11.76, -158.1) * mm, "end": v(-11.72, -158.65) * mm});
            skLineSegment(sketch, "E1428", {"start": v(-11.72, -158.65) * mm, "end": v(-11.67, -159.2) * mm});
            skLineSegment(sketch, "E1429", {"start": v(-11.67, -159.2) * mm, "end": v(-11.61, -159.73) * mm});
            skLineSegment(sketch, "E1430", {"start": v(-11.61, -159.73) * mm, "end": v(-11.55, -160.26) * mm});
            skLineSegment(sketch, "E1431", {"start": v(-11.55, -160.26) * mm, "end": v(-11.48, -160.79) * mm});
            skLineSegment(sketch, "E1432", {"start": v(-11.48, -160.79) * mm, "end": v(-11.41, -161.3) * mm});
            skLineSegment(sketch, "E1433", {"start": v(-11.41, -161.3) * mm, "end": v(-11.25, -162.21) * mm});
            skLineSegment(sketch, "E1434", {"start": v(-11.25, -162.21) * mm, "end": v(-11.14, -162.71) * mm});
            skLineSegment(sketch, "E1435", {"start": v(-11.14, -162.71) * mm, "end": v(-10.97, -163.44) * mm});
            skLineSegment(sketch, "E1436", {"start": v(-10.97, -163.44) * mm, "end": v(-10.82, -163.98) * mm});
            skLineSegment(sketch, "E1437", {"start": v(-10.82, -163.98) * mm, "end": v(-10.64, -164.56) * mm});
            skLineSegment(sketch, "E1438", {"start": v(-10.64, -164.56) * mm, "end": v(-10.45, -165.1) * mm});
            skLineSegment(sketch, "E1439", {"start": v(-10.45, -165.1) * mm, "end": v(-10.18, -165.77) * mm});
            skLineSegment(sketch, "E1440", {"start": v(-10.18, -165.77) * mm, "end": v(-9.9, -166.35) * mm});
            skLineSegment(sketch, "E1441", {"start": v(-9.9, -166.35) * mm, "end": v(-9.6, -166.86) * mm});
            skLineSegment(sketch, "E1442", {"start": v(-9.6, -166.86) * mm, "end": v(-9.28, -167.28) * mm});
            skLineSegment(sketch, "E1443", {"start": v(-9.28, -167.28) * mm, "end": v(-6.36, -169.67) * mm});
            skLineSegment(sketch, "E1444", {"start": v(-6.36, -169.67) * mm, "end": v(-4.5, -171.04) * mm});
            skLineSegment(sketch, "E1445", {"start": v(-4.5, -171.04) * mm, "end": v(0, -174.42) * mm});
            skLineSegment(sketch, "E1446", {"start": v(0, -174.42) * mm, "end": v(1.8, -175.7) * mm});
            skLineSegment(sketch, "E1447", {"start": v(1.8, -175.7) * mm, "end": v(11.03, -181.84) * mm});
            skLineSegment(sketch, "E1448", {"start": v(11.03, -181.84) * mm, "end": v(11.03, -188.12) * mm});
            skLineSegment(sketch, "E1449", {"start": v(11.03, -188.12) * mm, "end": v(11.03, -189.32) * mm});
            skLineSegment(sketch, "E1450", {"start": v(11.03, -189.32) * mm, "end": v(11.03, -194.52) * mm});
            skLineSegment(sketch, "E1451", {"start": v(11.03, -194.52) * mm, "end": v(11.03, -197.13) * mm});
            skLineSegment(sketch, "E1452", {"start": v(11.03, -197.13) * mm, "end": v(11.03, -201.18) * mm});
            skLineSegment(sketch, "E1453", {"start": v(11.03, -201.18) * mm, "end": v(11.03, -205.5) * mm});
            skLineSegment(sketch, "E1454", {"start": v(11.03, -205.5) * mm, "end": v(11.03, -208.14) * mm});
            skLineSegment(sketch, "E1455", {"start": v(11.03, -208.14) * mm, "end": v(11.03, -214.5) * mm});
            skLineSegment(sketch, "E1456", {"start": v(11.03, -214.5) * mm, "end": v(11.03, -215.45) * mm});
            skLineSegment(sketch, "E1457", {"start": v(11.03, -215.45) * mm, "end": v(11.03, -219.02) * mm});
            skLineSegment(sketch, "E1458", {"start": v(11.03, -219.02) * mm, "end": v(-3.97, -220.33) * mm});
            skLineSegment(sketch, "E1459", {"start": v(-3.97, -220.33) * mm, "end": v(-8.13, -220.69) * mm});
            skLineSegment(sketch, "E1460", {"start": v(-8.13, -220.69) * mm, "end": v(-8.65, -220.79) * mm});
            skLineSegment(sketch, "E1461", {"start": v(-8.65, -220.79) * mm, "end": v(-9.15, -221) * mm});
            skLineSegment(sketch, "E1462", {"start": v(-9.15, -221) * mm, "end": v(-9.63, -221.31) * mm});
            skLineSegment(sketch, "E1463", {"start": v(-9.63, -221.31) * mm, "end": v(-10.09, -221.73) * mm});
            skLineSegment(sketch, "E1464", {"start": v(-10.09, -221.73) * mm, "end": v(-10.5, -222.2) * mm});
            skLineSegment(sketch, "E1465", {"start": v(-10.5, -222.2) * mm, "end": v(-10.87, -222.76) * mm});
            skLineSegment(sketch, "E1466", {"start": v(-10.87, -222.76) * mm, "end": v(-11.18, -223.37) * mm});
            skLineSegment(sketch, "E1467", {"start": v(-11.18, -223.37) * mm, "end": v(-11.4, -223.88) * mm});
            skLineSegment(sketch, "E1468", {"start": v(-11.4, -223.88) * mm, "end": v(-11.6, -224.52) * mm});
            skLineSegment(sketch, "E1469", {"start": v(-11.6, -224.52) * mm, "end": v(-11.74, -225.12) * mm});
            skLineSegment(sketch, "E1470", {"start": v(-11.74, -225.12) * mm, "end": v(-11.83, -225.64) * mm});
            skLineSegment(sketch, "E1471", {"start": v(-11.83, -225.64) * mm, "end": v(-11.89, -226.18) * mm});
            skLineSegment(sketch, "E1472", {"start": v(-11.89, -226.18) * mm, "end": v(-11.92, -226.72) * mm});
            skLineSegment(sketch, "E1473", {"start": v(-11.92, -226.72) * mm, "end": v(-11.92, -229.67) * mm});
            skLineSegment(sketch, "E1474", {"start": v(-11.92, -229.67) * mm, "end": v(-11.92, -234.5) * mm});
            skLineSegment(sketch, "E1475", {"start": v(-11.92, -234.5) * mm, "end": v(-11.92, -237.7) * mm});
            skLineSegment(sketch, "E1476", {"start": v(-11.92, -237.7) * mm, "end": v(-11.92, -239.34) * mm});
            skLineSegment(sketch, "E1477", {"start": v(-11.92, -239.34) * mm, "end": v(-11.9, -240.02) * mm});
            skLineSegment(sketch, "E1478", {"start": v(-11.9, -240.02) * mm, "end": v(-11.83, -240.6) * mm});
            skLineSegment(sketch, "E1479", {"start": v(-11.83, -240.6) * mm, "end": v(-11.7, -241.21) * mm});
            skLineSegment(sketch, "E1480", {"start": v(-11.7, -241.21) * mm, "end": v(-11.55, -241.78) * mm});
            skLineSegment(sketch, "E1481", {"start": v(-11.55, -241.78) * mm, "end": v(-11.34, -242.32) * mm});
            skLineSegment(sketch, "E1482", {"start": v(-11.34, -242.32) * mm, "end": v(-11.1, -242.85) * mm});
            skLineSegment(sketch, "E1483", {"start": v(-11.1, -242.85) * mm, "end": v(-10.83, -243.3) * mm});
            skLineSegment(sketch, "E1484", {"start": v(-10.83, -243.3) * mm, "end": v(-10.5, -243.75) * mm});
            skLineSegment(sketch, "E1485", {"start": v(-10.5, -243.75) * mm, "end": v(-10.07, -244.2) * mm});
            skLineSegment(sketch, "E1486", {"start": v(-10.07, -244.2) * mm, "end": v(-9.61, -244.56) * mm});
            skLineSegment(sketch, "E1487", {"start": v(-9.61, -244.56) * mm, "end": v(-9.12, -244.84) * mm});
            skLineSegment(sketch, "E1488", {"start": v(-9.12, -244.84) * mm, "end": v(-8.61, -245.01) * mm});
            skLineSegment(sketch, "E1489", {"start": v(-8.61, -245.01) * mm, "end": v(-4, -245.62) * mm});
            skLineSegment(sketch, "E1490", {"start": v(-4, -245.62) * mm, "end": v(8.19, -247.1) * mm});
            skLineSegment(sketch, "E1491", {"start": v(8.19, -247.1) * mm, "end": v(8.19, -245.76) * mm});
            skLineSegment(sketch, "E1492", {"start": v(8.19, -245.76) * mm, "end": v(18.88, -245.76) * mm});
            skLineSegment(sketch, "E1493", {"start": v(18.88, -245.76) * mm, "end": v(19.03, -242.26) * mm});
            skLineSegment(sketch, "E1494", {"start": v(19.03, -242.26) * mm, "end": v(19.03, -232.73) * mm});
            skLineSegment(sketch, "E1495", {"start": v(19.03, -232.73) * mm, "end": v(19.03, -223.9) * mm});
            skLineSegment(sketch, "E1496", {"start": v(19.03, -223.9) * mm, "end": v(19.03, -215.65) * mm});
            skLineSegment(sketch, "E1497", {"start": v(19.03, -215.65) * mm, "end": v(15.03, -215.3) * mm});
            skLineSegment(sketch, "E1498", {"start": v(15.03, -215.3) * mm, "end": v(15.03, -212.3) * mm});
            skLineSegment(sketch, "E1499", {"start": v(15.03, -212.3) * mm, "end": v(18.88, -212.3) * mm});
            skLineSegment(sketch, "E1500", {"start": v(18.88, -212.3) * mm, "end": v(19.03, -207.9) * mm});
            skLineSegment(sketch, "E1501", {"start": v(19.03, -207.9) * mm, "end": v(19.03, -200.58) * mm});
            skLineSegment(sketch, "E1502", {"start": v(19.03, -200.58) * mm, "end": v(19.03, -193.64) * mm});
            skLineSegment(sketch, "E1503", {"start": v(19.03, -193.64) * mm, "end": v(19.03, -193.13) * mm});
            skLineSegment(sketch, "E1504", {"start": v(19.03, -193.13) * mm, "end": v(19.03, -187.02) * mm});
            skLineSegment(sketch, "E1505", {"start": v(19.03, -187.02) * mm, "end": v(19.03, -186.47) * mm});
            skLineSegment(sketch, "E1506", {"start": v(19.03, -186.47) * mm, "end": v(19.03, -182) * mm});
            skLineSegment(sketch, "E1507", {"start": v(19.03, -182) * mm, "end": v(12.78, -181.85) * mm});
            skLineSegment(sketch, "E1508", {"start": v(12.78, -181.85) * mm, "end": v(12.78, -178.85) * mm});
            skLineSegment(sketch, "E1509", {"start": v(12.78, -178.85) * mm, "end": v(18.88, -178.85) * mm});
            skLineSegment(sketch, "E1510", {"start": v(18.88, -178.85) * mm, "end": v(19.03, -174.56) * mm});
            skLineSegment(sketch, "E1511", {"start": v(19.03, -174.56) * mm, "end": v(19.03, -173.96) * mm});
            skLineSegment(sketch, "E1512", {"start": v(19.03, -173.96) * mm, "end": v(19.03, -168.66) * mm});
            skLineSegment(sketch, "E1513", {"start": v(19.03, -168.66) * mm, "end": v(19.03, -168.04) * mm});
            skLineSegment(sketch, "E1514", {"start": v(19.03, -168.04) * mm, "end": v(19.03, -162.92) * mm});
            skLineSegment(sketch, "E1515", {"start": v(19.03, -162.92) * mm, "end": v(19.03, -162.29) * mm});
            skLineSegment(sketch, "E1516", {"start": v(19.03, -162.29) * mm, "end": v(19.03, -157.33) * mm});
            skLineSegment(sketch, "E1517", {"start": v(19.03, -157.33) * mm, "end": v(19.03, -156.68) * mm});
            skLineSegment(sketch, "E1518", {"start": v(19.03, -156.68) * mm, "end": v(19.03, -151.86) * mm});
            skLineSegment(sketch, "E1519", {"start": v(19.03, -151.86) * mm, "end": v(19.03, -151.2) * mm});
            skLineSegment(sketch, "E1520", {"start": v(19.03, -151.2) * mm, "end": v(19.03, -148.55) * mm});
            skLineSegment(sketch, "E1521", {"start": v(19.03, -148.55) * mm, "end": v(3.55, -148.4) * mm});
            skLineSegment(sketch, "E1522", {"start": v(3.55, -148.4) * mm, "end": v(3.55, -145.4) * mm});
            skLineSegment(sketch, "E1523", {"start": v(3.55, -145.4) * mm, "end": v(18.88, -145.4) * mm});
            skLineSegment(sketch, "E1524", {"start": v(18.88, -145.4) * mm, "end": v(19.03, -141.17) * mm});
            skLineSegment(sketch, "E1525", {"start": v(19.03, -141.17) * mm, "end": v(19.03, -140.5) * mm});
            skLineSegment(sketch, "E1526", {"start": v(19.03, -140.5) * mm, "end": v(19.03, -135.92) * mm});
            skLineSegment(sketch, "E1527", {"start": v(19.03, -135.92) * mm, "end": v(19.03, -135.24) * mm});
            skLineSegment(sketch, "E1528", {"start": v(19.03, -135.24) * mm, "end": v(19.03, -130.7) * mm});
            skLineSegment(sketch, "E1529", {"start": v(19.03, -130.7) * mm, "end": v(19.03, -130.02) * mm});
            skLineSegment(sketch, "E1530", {"start": v(19.03, -130.02) * mm, "end": v(19.03, -125.5) * mm});
            skLineSegment(sketch, "E1531", {"start": v(19.03, -125.5) * mm, "end": v(19.03, -124.81) * mm});
            skLineSegment(sketch, "E1532", {"start": v(19.03, -124.81) * mm, "end": v(19.03, -120.28) * mm});
            skLineSegment(sketch, "E1533", {"start": v(19.03, -120.28) * mm, "end": v(19.03, -119.6) * mm});
            skLineSegment(sketch, "E1534", {"start": v(19.03, -119.6) * mm, "end": v(19.03, -115.1) * mm});
            skLineSegment(sketch, "E1535", {"start": v(19.03, -115.1) * mm, "end": v(3.55, -114.94) * mm});
            skLineSegment(sketch, "E1536", {"start": v(3.55, -114.94) * mm, "end": v(3.55, -111.94) * mm});
            skLineSegment(sketch, "E1537", {"start": v(3.55, -111.94) * mm, "end": v(18.88, -111.94) * mm});
            skLineSegment(sketch, "E1538", {"start": v(18.88, -111.94) * mm, "end": v(19.03, -109.75) * mm});
            skLineSegment(sketch, "E1539", {"start": v(19.03, -109.75) * mm, "end": v(19.03, -109.07) * mm});
            skLineSegment(sketch, "E1540", {"start": v(19.03, -109.07) * mm, "end": v(19.03, -104.4) * mm});
            skLineSegment(sketch, "E1541", {"start": v(19.03, -104.4) * mm, "end": v(19.03, -103.72) * mm});
            skLineSegment(sketch, "E1542", {"start": v(19.03, -103.72) * mm, "end": v(19.03, -103.06) * mm});
            skLineSegment(sketch, "E1543", {"start": v(19.03, -103.06) * mm, "end": v(19.03, -102.4) * mm});
            skLineSegment(sketch, "E1544", {"start": v(19.03, -102.4) * mm, "end": v(19.03, -101.74) * mm});
            skLineSegment(sketch, "E1545", {"start": v(19.03, -101.74) * mm, "end": v(19.03, -101.1) * mm});
            skLineSegment(sketch, "E1546", {"start": v(19.03, -101.1) * mm, "end": v(19.03, -100.47) * mm});
            skLineSegment(sketch, "E1547", {"start": v(19.03, -100.47) * mm, "end": v(19.03, -99.85) * mm});
            skLineSegment(sketch, "E1548", {"start": v(19.03, -99.85) * mm, "end": v(19.03, -99.25) * mm});
            skLineSegment(sketch, "E1549", {"start": v(19.03, -99.25) * mm, "end": v(19.03, -98.66) * mm});
            skLineSegment(sketch, "E1550", {"start": v(19.03, -98.66) * mm, "end": v(19.03, -98.1) * mm});
            skLineSegment(sketch, "E1551", {"start": v(19.03, -98.1) * mm, "end": v(19.03, -81.63) * mm});
            skLineSegment(sketch, "E1552", {"start": v(19.03, -81.63) * mm, "end": v(6.86, -81.48) * mm});
            skLineSegment(sketch, "E1553", {"start": v(6.86, -81.48) * mm, "end": v(6.86, -78.48) * mm});
            skLineSegment(sketch, "E1554", {"start": v(6.86, -78.48) * mm, "end": v(18.88, -78.48) * mm});
            skLineSegment(sketch, "E1555", {"start": v(18.88, -78.48) * mm, "end": v(19.03, -48.18) * mm});
            skLineSegment(sketch, "E1556", {"start": v(19.03, -48.18) * mm, "end": v(15.03, -48.03) * mm});
            skLineSegment(sketch, "E1557", {"start": v(15.03, -48.03) * mm, "end": v(15.03, -45.03) * mm});
            skLineSegment(sketch, "E1558", {"start": v(15.03, -45.03) * mm, "end": v(18.88, -45.03) * mm});
            skLineSegment(sketch, "E1559", {"start": v(18.88, -45.03) * mm, "end": v(19.03, -14.72) * mm});
            skLineSegment(sketch, "E1560", {"start": v(19.03, -14.72) * mm, "end": v(15.03, -14.57) * mm});
            skLineSegment(sketch, "E1561", {"start": v(15.03, -14.57) * mm, "end": v(15.03, -11.57) * mm});
            skLineSegment(sketch, "E1562", {"start": v(15.03, -11.57) * mm, "end": v(18.88, -11.57) * mm});
            skLineSegment(sketch, "E1563", {"start": v(18.88, -11.57) * mm, "end": v(19.03, 18.73) * mm});
            skLineSegment(sketch, "E1564", {"start": v(19.03, 18.73) * mm, "end": v(15.03, 18.88) * mm});
            skLineSegment(sketch, "E1565", {"start": v(15.03, 18.88) * mm, "end": v(15.03, 21.88) * mm});
            skLineSegment(sketch, "E1566", {"start": v(15.03, 21.88) * mm, "end": v(18.88, 21.88) * mm});
            skLineSegment(sketch, "E1567", {"start": v(18.88, 21.88) * mm, "end": v(19.03, 52.19) * mm});
            skLineSegment(sketch, "E1568", {"start": v(19.03, 52.19) * mm, "end": v(15.03, 52.34) * mm});
            skLineSegment(sketch, "E1569", {"start": v(15.03, 52.34) * mm, "end": v(15.03, 55.34) * mm});
            skLineSegment(sketch, "E1570", {"start": v(15.03, 55.34) * mm, "end": v(18.88, 55.34) * mm});
            skLineSegment(sketch, "E1571", {"start": v(18.88, 55.34) * mm, "end": v(19.03, 75.53) * mm});
            skLineSegment(sketch, "E1572", {"start": v(19.03, 75.53) * mm, "end": v(19.03, 76.37) * mm});
            skLineSegment(sketch, "E1573", {"start": v(19.03, 76.37) * mm, "end": v(19.03, 77.22) * mm});
            skLineSegment(sketch, "E1574", {"start": v(19.03, 77.22) * mm, "end": v(19.03, 78.06) * mm});
            skLineSegment(sketch, "E1575", {"start": v(19.03, 78.06) * mm, "end": v(19.03, 78.87) * mm});
            skLineSegment(sketch, "E1576", {"start": v(19.03, 78.87) * mm, "end": v(19.03, 79.65) * mm});
            skLineSegment(sketch, "E1577", {"start": v(19.03, 79.65) * mm, "end": v(19.03, 80.24) * mm});
            skLineSegment(sketch, "E1578", {"start": v(19.03, 80.24) * mm, "end": v(19.03, 80.91) * mm});
            skLineSegment(sketch, "E1579", {"start": v(19.03, 80.91) * mm, "end": v(19.03, 81.67) * mm});
            skLineSegment(sketch, "E1580", {"start": v(19.03, 81.67) * mm, "end": v(19.03, 82.2) * mm});
            skLineSegment(sketch, "E1581", {"start": v(19.03, 82.2) * mm, "end": v(19.03, 82.78) * mm});
            skLineSegment(sketch, "E1582", {"start": v(19.03, 82.78) * mm, "end": v(19.03, 83.37) * mm});
            skLineSegment(sketch, "E1583", {"start": v(19.03, 83.37) * mm, "end": v(19.03, 83.98) * mm});
            skLineSegment(sketch, "E1584", {"start": v(19.03, 83.98) * mm, "end": v(19.03, 84.6) * mm});
            skLineSegment(sketch, "E1585", {"start": v(19.03, 84.6) * mm, "end": v(19.03, 85.24) * mm});
            skLineSegment(sketch, "E1586", {"start": v(19.03, 85.24) * mm, "end": v(18.88, 85.8) * mm});
            skLineSegment(sketch, "E1587", {"start": v(18.88, 85.8) * mm, "end": v(12.23, 85.8) * mm});
            skLineSegment(sketch, "E1588", {"start": v(12.23, 85.8) * mm, "end": v(12.23, 88.8) * mm});
            skLineSegment(sketch, "E1589", {"start": v(12.23, 88.8) * mm, "end": v(18.88, 88.8) * mm});
            skLineSegment(sketch, "E1590", {"start": v(18.88, 88.8) * mm, "end": v(19.03, 89.3) * mm});
            skLineSegment(sketch, "E1591", {"start": v(19.03, 89.3) * mm, "end": v(19.03, 89.84) * mm});
            skLineSegment(sketch, "E1592", {"start": v(19.03, 89.84) * mm, "end": v(19.03, 90.56) * mm});
            skLineSegment(sketch, "E1593", {"start": v(19.03, 90.56) * mm, "end": v(19.03, 91.21) * mm});
            skLineSegment(sketch, "E1594", {"start": v(19.03, 91.21) * mm, "end": v(19.03, 91.78) * mm});
            skLineSegment(sketch, "E1595", {"start": v(19.03, 91.78) * mm, "end": v(19.03, 104.02) * mm});
            skLineSegment(sketch, "E1596", {"start": v(19.03, 104.02) * mm, "end": v(18.26, 104.02) * mm});
            skLineSegment(sketch, "E1597", {"start": v(18.26, 104.02) * mm, "end": v(13.49, 104.02) * mm});
            skLineSegment(sketch, "E1598", {"start": v(11.03, 223.55) * mm, "end": v(11.03, 213.74) * mm});
            skLineSegment(sketch, "E1599", {"start": v(11.03, 213.74) * mm, "end": v(11.03, 203.83) * mm});
            skLineSegment(sketch, "E1600", {"start": v(11.03, 203.83) * mm, "end": v(4.55, 202.07) * mm});
            skLineSegment(sketch, "E1601", {"start": v(4.55, 202.07) * mm, "end": v(-3.08, 200.02) * mm});
            skLineSegment(sketch, "E1602", {"start": v(-3.08, 200.02) * mm, "end": v(-8.96, 198.43) * mm});
            skLineSegment(sketch, "E1603", {"start": v(-8.96, 198.43) * mm, "end": v(-9.44, 198.25) * mm});
            skLineSegment(sketch, "E1604", {"start": v(-9.44, 198.25) * mm, "end": v(-9.92, 198.01) * mm});
            skLineSegment(sketch, "E1605", {"start": v(-9.92, 198.01) * mm, "end": v(-10.34, 197.73) * mm});
            skLineSegment(sketch, "E1606", {"start": v(-10.34, 197.73) * mm, "end": v(-10.72, 197.39) * mm});
            skLineSegment(sketch, "E1607", {"start": v(-10.72, 197.39) * mm, "end": v(-11.06, 197) * mm});
            skLineSegment(sketch, "E1608", {"start": v(-11.06, 197) * mm, "end": v(-11.35, 196.58) * mm});
            skLineSegment(sketch, "E1609", {"start": v(-11.35, 196.58) * mm, "end": v(-11.58, 196.12) * mm});
            skLineSegment(sketch, "E1610", {"start": v(-11.58, 196.12) * mm, "end": v(-11.76, 195.63) * mm});
            skLineSegment(sketch, "E1611", {"start": v(-11.76, 195.63) * mm, "end": v(-11.87, 195.13) * mm});
            skLineSegment(sketch, "E1612", {"start": v(-11.87, 195.13) * mm, "end": v(3.55, 194.66) * mm});
            skLineSegment(sketch, "E1613", {"start": v(3.55, 194.66) * mm, "end": v(3.55, 191.66) * mm});
            skLineSegment(sketch, "E1614", {"start": v(3.55, 191.66) * mm, "end": v(-11.77, 191.66) * mm});
            skLineSegment(sketch, "E1615", {"start": v(-11.77, 191.66) * mm, "end": v(-11.92, 186) * mm});
            skLineSegment(sketch, "E1616", {"start": v(-11.92, 186) * mm, "end": v(-11.92, 176.64) * mm});
            skLineSegment(sketch, "E1617", {"start": v(-11.92, 176.64) * mm, "end": v(-11.92, 175.94) * mm});
            skLineSegment(sketch, "E1618", {"start": v(-11.92, 175.94) * mm, "end": v(-11.92, 175.4) * mm});
            skLineSegment(sketch, "E1619", {"start": v(-11.92, 175.4) * mm, "end": v(-11.89, 174.87) * mm});
            skLineSegment(sketch, "E1620", {"start": v(-11.89, 174.87) * mm, "end": v(-11.79, 174.35) * mm});
            skLineSegment(sketch, "E1621", {"start": v(-11.79, 174.35) * mm, "end": v(-11.62, 173.84) * mm});
            skLineSegment(sketch, "E1622", {"start": v(-11.62, 173.84) * mm, "end": v(-10.21, 170.56) * mm});
            skLineSegment(sketch, "E1623", {"start": v(-10.21, 170.56) * mm, "end": v(-8.77, 167.3) * mm});
            skLineSegment(sketch, "E1624", {"start": v(-8.77, 167.3) * mm, "end": v(-6.79, 162.34) * mm});
            skLineSegment(sketch, "E1625", {"start": v(-6.79, 162.34) * mm, "end": v(-6.09, 160.6) * mm});
            skLineSegment(sketch, "E1626", {"start": v(-6.09, 160.6) * mm, "end": v(6.72, 160.36) * mm});
            skLineSegment(sketch, "E1627", {"start": v(6.72, 160.36) * mm, "end": v(6.72, 157.36) * mm});
            skLineSegment(sketch, "E1628", {"start": v(6.72, 157.36) * mm, "end": v(-4.7, 157.36) * mm});
            skLineSegment(sketch, "E1629", {"start": v(-4.7, 157.36) * mm, "end": v(-3.63, 153.9) * mm});
            skLineSegment(sketch, "E1630", {"start": v(-3.63, 153.9) * mm, "end": v(-3.32, 152.97) * mm});
            skLineSegment(sketch, "E1631", {"start": v(-3.32, 152.97) * mm, "end": v(-2.7, 151.17) * mm});
            skLineSegment(sketch, "E1632", {"start": v(-2.7, 151.17) * mm, "end": v(-1.8, 148.44) * mm});
            skLineSegment(sketch, "E1633", {"start": v(-1.8, 148.44) * mm, "end": v(-1.36, 147.1) * mm});
            skLineSegment(sketch, "E1634", {"start": v(-1.36, 147.1) * mm, "end": v(-0.42, 144.02) * mm});
            skLineSegment(sketch, "E1635", {"start": v(-0.42, 144.02) * mm, "end": v(0.73, 140.21) * mm});
            skLineSegment(sketch, "E1636", {"start": v(0.73, 140.21) * mm, "end": v(0.94, 139.45) * mm});
            skLineSegment(sketch, "E1637", {"start": v(0.94, 139.45) * mm, "end": v(1.94, 135.74) * mm});
            skLineSegment(sketch, "E1638", {"start": v(1.94, 135.74) * mm, "end": v(2.63, 133.17) * mm});
            skLineSegment(sketch, "E1639", {"start": v(2.63, 133.17) * mm, "end": v(2.93, 131.89) * mm});
            skLineSegment(sketch, "E1640", {"start": v(2.93, 131.89) * mm, "end": v(3.25, 130.58) * mm});
            skLineSegment(sketch, "E1641", {"start": v(3.25, 130.58) * mm, "end": v(3.82, 128.15) * mm});
            skLineSegment(sketch, "E1642", {"start": v(3.82, 128.15) * mm, "end": v(4.28, 126.2) * mm});
            skLineSegment(sketch, "E1643", {"start": v(4.28, 126.2) * mm, "end": v(11.76, 126.06) * mm});
            skLineSegment(sketch, "E1644", {"start": v(11.76, 126.06) * mm, "end": v(11.76, 123.06) * mm});
            skLineSegment(sketch, "E1645", {"start": v(11.76, 123.06) * mm, "end": v(5.12, 123.06) * mm});
            skLineSegment(sketch, "E1646", {"start": v(5.12, 123.06) * mm, "end": v(5.3, 121.29) * mm});
            skLineSegment(sketch, "E1647", {"start": v(5.3, 121.29) * mm, "end": v(5.85, 118.64) * mm});
            skLineSegment(sketch, "E1648", {"start": v(5.85, 118.64) * mm, "end": v(5.97, 117.96) * mm});
            skLineSegment(sketch, "E1649", {"start": v(5.97, 117.96) * mm, "end": v(6.46, 115.17) * mm});
            skLineSegment(sketch, "E1650", {"start": v(6.46, 115.17) * mm, "end": v(6.78, 113.29) * mm});
            skLineSegment(sketch, "E1651", {"start": v(6.78, 113.29) * mm, "end": v(6.93, 112.42) * mm});
            skLineSegment(sketch, "E1652", {"start": v(6.93, 112.42) * mm, "end": v(7.17, 111) * mm});
            skLineSegment(sketch, "E1653", {"start": v(7.17, 111) * mm, "end": v(7.28, 110.48) * mm});
            skLineSegment(sketch, "E1654", {"start": v(7.28, 110.48) * mm, "end": v(7.48, 109.9) * mm});
            skLineSegment(sketch, "E1655", {"start": v(7.48, 109.9) * mm, "end": v(7.74, 109.35) * mm});
            skLineSegment(sketch, "E1656", {"start": v(7.74, 109.35) * mm, "end": v(8.05, 108.86) * mm});
            skLineSegment(sketch, "E1657", {"start": v(8.05, 108.86) * mm, "end": v(8.41, 108.42) * mm});
            skLineSegment(sketch, "E1658", {"start": v(8.41, 108.42) * mm, "end": v(8.82, 108.04) * mm});
            skLineSegment(sketch, "E1659", {"start": v(8.82, 108.04) * mm, "end": v(9.27, 107.72) * mm});
            skLineSegment(sketch, "E1660", {"start": v(9.27, 107.72) * mm, "end": v(9.74, 107.48) * mm});
            skLineSegment(sketch, "E1661", {"start": v(9.74, 107.48) * mm, "end": v(10.25, 107.3) * mm});
            skLineSegment(sketch, "E1662", {"start": v(10.25, 107.3) * mm, "end": v(10.76, 107.21) * mm});
            skLineSegment(sketch, "E1663", {"start": v(10.76, 107.21) * mm, "end": v(14.17, 107.2) * mm});
            skLineSegment(sketch, "E1664", {"start": v(14.17, 107.2) * mm, "end": v(19.03, 107.2) * mm});
            skLineSegment(sketch, "E1665", {"start": v(19.03, 107.2) * mm, "end": v(19.03, 109.41) * mm});
            skLineSegment(sketch, "E1666", {"start": v(19.03, 109.41) * mm, "end": v(19.03, 113.51) * mm});
            skLineSegment(sketch, "E1667", {"start": v(19.03, 113.51) * mm, "end": v(19.03, 114.3) * mm});
            skLineSegment(sketch, "E1668", {"start": v(19.03, 114.3) * mm, "end": v(19.03, 118.4) * mm});
            skLineSegment(sketch, "E1669", {"start": v(19.03, 118.4) * mm, "end": v(19.03, 119.97) * mm});
            skLineSegment(sketch, "E1670", {"start": v(19.03, 119.97) * mm, "end": v(19.03, 124.33) * mm});
            skLineSegment(sketch, "E1671", {"start": v(19.03, 124.33) * mm, "end": v(19.03, 127.1) * mm});
            skLineSegment(sketch, "E1672", {"start": v(19.03, 127.1) * mm, "end": v(19.03, 131.72) * mm});
            skLineSegment(sketch, "E1673", {"start": v(19.03, 131.72) * mm, "end": v(19.03, 136.35) * mm});
            skLineSegment(sketch, "E1674", {"start": v(19.03, 136.35) * mm, "end": v(19.03, 141.24) * mm});
            skLineSegment(sketch, "E1675", {"start": v(19.03, 141.24) * mm, "end": v(19.03, 148.93) * mm});
            skLineSegment(sketch, "E1676", {"start": v(19.03, 148.93) * mm, "end": v(19.03, 154) * mm});
            skLineSegment(sketch, "E1677", {"start": v(19.03, 154) * mm, "end": v(19.03, 167.14) * mm});
            skLineSegment(sketch, "E1678", {"start": v(19.03, 167.14) * mm, "end": v(19.03, 172.12) * mm});
            skLineSegment(sketch, "E1679", {"start": v(19.03, 172.12) * mm, "end": v(19.03, 196.01) * mm});
            skLineSegment(sketch, "E1680", {"start": v(19.03, 196.01) * mm, "end": v(19.03, 199.95) * mm});
            skLineSegment(sketch, "E1681", {"start": v(19.03, 199.95) * mm, "end": v(19.03, 243.32) * mm});
            skLineSegment(sketch, "E1682", {"start": v(19.03, 243.32) * mm, "end": v(-5.18, 241.19) * mm});
            skLineSegment(sketch, "E1683", {"start": v(-5.18, 241.19) * mm, "end": v(-8.27, 240.92) * mm});
            skLineSegment(sketch, "E1684", {"start": v(-8.27, 240.92) * mm, "end": v(-8.79, 240.83) * mm});
            skLineSegment(sketch, "E1685", {"start": v(-8.79, 240.83) * mm, "end": v(-9.29, 240.68) * mm});
            skLineSegment(sketch, "E1686", {"start": v(-9.29, 240.68) * mm, "end": v(-9.77, 240.47) * mm});
            skLineSegment(sketch, "E1687", {"start": v(-9.77, 240.47) * mm, "end": v(-10.21, 240.2) * mm});
            skLineSegment(sketch, "E1688", {"start": v(-10.21, 240.2) * mm, "end": v(-10.62, 239.86) * mm});
            skLineSegment(sketch, "E1689", {"start": v(-10.62, 239.86) * mm, "end": v(-10.98, 239.48) * mm});
            skLineSegment(sketch, "E1690", {"start": v(-10.98, 239.48) * mm, "end": v(-11.3, 239.05) * mm});
            skLineSegment(sketch, "E1691", {"start": v(-11.3, 239.05) * mm, "end": v(-11.55, 238.6) * mm});
            skLineSegment(sketch, "E1692", {"start": v(-11.55, 238.6) * mm, "end": v(-11.74, 238.1) * mm});
            skLineSegment(sketch, "E1693", {"start": v(-11.74, 238.1) * mm, "end": v(-11.86, 237.59) * mm});
            skLineSegment(sketch, "E1694", {"start": v(-11.86, 237.59) * mm, "end": v(-11.92, 237.06) * mm});
            skLineSegment(sketch, "E1695", {"start": v(-11.92, 237.06) * mm, "end": v(-11.92, 230.22) * mm});
            skLineSegment(sketch, "E1696", {"start": v(-11.92, 230.22) * mm, "end": v(-11.92, 229.1) * mm});
            skLineSegment(sketch, "E1697", {"start": v(-11.92, 229.1) * mm, "end": v(3.6, 228.96) * mm});
            skLineSegment(sketch, "E1698", {"start": v(3.6, 228.96) * mm, "end": v(3.6, 225.96) * mm});
            skLineSegment(sketch, "E1699", {"start": v(3.6, 225.96) * mm, "end": v(-10.65, 225.96) * mm});
            skLineSegment(sketch, "E1700", {"start": v(-10.65, 225.96) * mm, "end": v(-10.37, 225.42) * mm});
            skLineSegment(sketch, "E1701", {"start": v(-10.37, 225.42) * mm, "end": v(-9.94, 225.12) * mm});
            skLineSegment(sketch, "E1702", {"start": v(-9.94, 225.12) * mm, "end": v(-9.48, 224.89) * mm});
            skLineSegment(sketch, "E1703", {"start": v(-9.48, 224.89) * mm, "end": v(-8.98, 224.71) * mm});
            skLineSegment(sketch, "E1704", {"start": v(-8.98, 224.71) * mm, "end": v(-8.48, 224.6) * mm});
            skLineSegment(sketch, "E1705", {"start": v(-8.48, 224.6) * mm, "end": v(-2.59, 224.28) * mm});
            skLineSegment(sketch, "E1706", {"start": v(-2.59, 224.28) * mm, "end": v(11.03, 223.55) * mm});
            skLineSegment(sketch, "E1707", {"start": v(53.15, 104.02) * mm, "end": v(52.38, 104.02) * mm});
            skLineSegment(sketch, "E1708", {"start": v(52.38, 104.02) * mm, "end": v(47.61, 104.02) * mm});
            skLineSegment(sketch, "E1709", {"start": v(47.61, 104.02) * mm, "end": v(44.79, 104.02) * mm});
            skLineSegment(sketch, "E1710", {"start": v(44.79, 104.02) * mm, "end": v(44.27, 103.99) * mm});
            skLineSegment(sketch, "E1711", {"start": v(44.27, 103.99) * mm, "end": v(43.76, 103.89) * mm});
            skLineSegment(sketch, "E1712", {"start": v(43.76, 103.89) * mm, "end": v(43.27, 103.72) * mm});
            skLineSegment(sketch, "E1713", {"start": v(43.27, 103.72) * mm, "end": v(42.8, 103.5) * mm});
            skLineSegment(sketch, "E1714", {"start": v(42.8, 103.5) * mm, "end": v(42.36, 103.2) * mm});
            skLineSegment(sketch, "E1715", {"start": v(42.36, 103.2) * mm, "end": v(41.97, 102.86) * mm});
            skLineSegment(sketch, "E1716", {"start": v(41.97, 102.86) * mm, "end": v(41.63, 102.47) * mm});
            skLineSegment(sketch, "E1717", {"start": v(41.63, 102.47) * mm, "end": v(41.33, 102.04) * mm});
            skLineSegment(sketch, "E1718", {"start": v(41.33, 102.04) * mm, "end": v(41.1, 101.57) * mm});
            skLineSegment(sketch, "E1719", {"start": v(41.1, 101.57) * mm, "end": v(40.93, 101.08) * mm});
            skLineSegment(sketch, "E1720", {"start": v(40.93, 101.08) * mm, "end": v(40.83, 100.57) * mm});
            skLineSegment(sketch, "E1721", {"start": v(40.83, 100.57) * mm, "end": v(39.34, 85.02) * mm});
            skLineSegment(sketch, "E1722", {"start": v(39.34, 85.02) * mm, "end": v(39.02, 81.62) * mm});
            skLineSegment(sketch, "E1723", {"start": v(39.02, 81.62) * mm, "end": v(38.94, 80.8) * mm});
            skLineSegment(sketch, "E1724", {"start": v(38.94, 80.8) * mm, "end": v(38.86, 79.85) * mm});
            skLineSegment(sketch, "E1725", {"start": v(38.86, 79.85) * mm, "end": v(38.8, 78.95) * mm});
            skLineSegment(sketch, "E1726", {"start": v(38.8, 78.95) * mm, "end": v(38.74, 78.06) * mm});
            skLineSegment(sketch, "E1727", {"start": v(38.74, 78.06) * mm, "end": v(38.68, 77.17) * mm});
            skLineSegment(sketch, "E1728", {"start": v(38.68, 77.17) * mm, "end": v(38.64, 76.29) * mm});
            skLineSegment(sketch, "E1729", {"start": v(38.64, 76.29) * mm, "end": v(38.6, 75.4) * mm});
            skLineSegment(sketch, "E1730", {"start": v(38.6, 75.4) * mm, "end": v(38.57, 74.54) * mm});
            skLineSegment(sketch, "E1731", {"start": v(38.57, 74.54) * mm, "end": v(38.55, 73.69) * mm});
            skLineSegment(sketch, "E1732", {"start": v(38.55, 73.69) * mm, "end": v(38.54, 72.85) * mm});
            skLineSegment(sketch, "E1733", {"start": v(38.54, 72.85) * mm, "end": v(38.53, 72.02) * mm});
            skLineSegment(sketch, "E1734", {"start": v(38.53, 72.02) * mm, "end": v(38.54, 71.22) * mm});
            skLineSegment(sketch, "E1735", {"start": v(38.54, 71.22) * mm, "end": v(38.55, 70.43) * mm});
            skLineSegment(sketch, "E1736", {"start": v(38.55, 70.43) * mm, "end": v(38.57, 69.65) * mm});
            skLineSegment(sketch, "E1737", {"start": v(38.57, 69.65) * mm, "end": v(38.6, 68.9) * mm});
            skLineSegment(sketch, "E1738", {"start": v(38.6, 68.9) * mm, "end": v(38.63, 68.18) * mm});
            skLineSegment(sketch, "E1739", {"start": v(38.63, 68.18) * mm, "end": v(38.68, 67.47) * mm});
            skLineSegment(sketch, "E1740", {"start": v(38.68, 67.47) * mm, "end": v(38.73, 66.8) * mm});
            skLineSegment(sketch, "E1741", {"start": v(38.73, 66.8) * mm, "end": v(38.79, 66.14) * mm});
            skLineSegment(sketch, "E1742", {"start": v(38.79, 66.14) * mm, "end": v(38.86, 65.52) * mm});
            skLineSegment(sketch, "E1743", {"start": v(38.86, 65.52) * mm, "end": v(38.93, 64.92) * mm});
            skLineSegment(sketch, "E1744", {"start": v(38.93, 64.92) * mm, "end": v(39.01, 64.36) * mm});
            skLineSegment(sketch, "E1745", {"start": v(39.01, 64.36) * mm, "end": v(39.1, 63.82) * mm});
            skLineSegment(sketch, "E1746", {"start": v(39.1, 63.82) * mm, "end": v(39.2, 63.32) * mm});
            skLineSegment(sketch, "E1747", {"start": v(39.2, 63.32) * mm, "end": v(39.32, 62.78) * mm});
            skLineSegment(sketch, "E1748", {"start": v(39.32, 62.78) * mm, "end": v(39.45, 62.28) * mm});
            skLineSegment(sketch, "E1749", {"start": v(39.45, 62.28) * mm, "end": v(39.65, 61.64) * mm});
            skLineSegment(sketch, "E1750", {"start": v(39.65, 61.64) * mm, "end": v(39.92, 61.01) * mm});
            skLineSegment(sketch, "E1751", {"start": v(39.92, 61.01) * mm, "end": v(40.2, 60.53) * mm});
            skLineSegment(sketch, "E1752", {"start": v(40.2, 60.53) * mm, "end": v(40.57, 60.16) * mm});
            skLineSegment(sketch, "E1753", {"start": v(40.57, 60.16) * mm, "end": v(41.29, 59.9) * mm});
            skLineSegment(sketch, "E1754", {"start": v(41.29, 59.9) * mm, "end": v(45.15, 58.8) * mm});
            skLineSegment(sketch, "E1755", {"start": v(45.15, 58.8) * mm, "end": v(45.15, -34.8) * mm});
            skLineSegment(sketch, "E1756", {"start": v(45.15, -34.8) * mm, "end": v(45.15, -70.12) * mm});
            skLineSegment(sketch, "E1757", {"start": v(45.15, -70.12) * mm, "end": v(38.5, -74.52) * mm});
            skLineSegment(sketch, "E1758", {"start": v(38.5, -74.52) * mm, "end": v(35.93, -76.25) * mm});
            skLineSegment(sketch, "E1759", {"start": v(35.93, -76.25) * mm, "end": v(34.93, -76.96) * mm});
            skLineSegment(sketch, "E1760", {"start": v(34.93, -76.96) * mm, "end": v(32.14, -79.01) * mm});
            skLineSegment(sketch, "E1761", {"start": v(32.14, -79.01) * mm, "end": v(27.76, -82.29) * mm});
            skLineSegment(sketch, "E1762", {"start": v(27.76, -82.29) * mm, "end": v(26.22, -83.51) * mm});
            skLineSegment(sketch, "E1763", {"start": v(26.22, -83.51) * mm, "end": v(25.8, -83.91) * mm});
            skLineSegment(sketch, "E1764", {"start": v(25.8, -83.91) * mm, "end": v(25.47, -84.34) * mm});
            skLineSegment(sketch, "E1765", {"start": v(25.47, -84.34) * mm, "end": v(25.13, -84.84) * mm});
            skLineSegment(sketch, "E1766", {"start": v(25.13, -84.84) * mm, "end": v(24.8, -85.43) * mm});
            skLineSegment(sketch, "E1767", {"start": v(24.8, -85.43) * mm, "end": v(24.58, -85.88) * mm});
            skLineSegment(sketch, "E1768", {"start": v(24.58, -85.88) * mm, "end": v(24.34, -86.43) * mm});
            skLineSegment(sketch, "E1769", {"start": v(24.34, -86.43) * mm, "end": v(24.1, -87.03) * mm});
            skLineSegment(sketch, "E1770", {"start": v(24.1, -87.03) * mm, "end": v(23.9, -87.57) * mm});
            skLineSegment(sketch, "E1771", {"start": v(23.9, -87.57) * mm, "end": v(23.63, -88.34) * mm});
            skLineSegment(sketch, "E1772", {"start": v(23.63, -88.34) * mm, "end": v(23.49, -88.83) * mm});
            skLineSegment(sketch, "E1773", {"start": v(23.49, -88.83) * mm, "end": v(23.35, -89.33) * mm});
            skLineSegment(sketch, "E1774", {"start": v(23.35, -89.33) * mm, "end": v(23.23, -89.84) * mm});
            skLineSegment(sketch, "E1775", {"start": v(23.23, -89.84) * mm, "end": v(23.1, -90.37) * mm});
            skLineSegment(sketch, "E1776", {"start": v(23.1, -90.37) * mm, "end": v(22.98, -90.92) * mm});
            skLineSegment(sketch, "E1777", {"start": v(22.98, -90.92) * mm, "end": v(22.86, -91.48) * mm});
            skLineSegment(sketch, "E1778", {"start": v(22.86, -91.48) * mm, "end": v(22.75, -92.05) * mm});
            skLineSegment(sketch, "E1779", {"start": v(22.75, -92.05) * mm, "end": v(22.64, -92.63) * mm});
            skLineSegment(sketch, "E1780", {"start": v(22.64, -92.63) * mm, "end": v(22.54, -93.21) * mm});
            skLineSegment(sketch, "E1781", {"start": v(22.54, -93.21) * mm, "end": v(22.44, -93.8) * mm});
            skLineSegment(sketch, "E1782", {"start": v(22.44, -93.8) * mm, "end": v(22.35, -94.37) * mm});
            skLineSegment(sketch, "E1783", {"start": v(22.35, -94.37) * mm, "end": v(22.28, -95.05) * mm});
            skLineSegment(sketch, "E1784", {"start": v(22.28, -95.05) * mm, "end": v(22.25, -95.69) * mm});
            skLineSegment(sketch, "E1785", {"start": v(22.25, -95.69) * mm, "end": v(22.23, -96.35) * mm});
            skLineSegment(sketch, "E1786", {"start": v(22.23, -96.35) * mm, "end": v(22.22, -96.88) * mm});
            skLineSegment(sketch, "E1787", {"start": v(22.22, -96.88) * mm, "end": v(22.2, -97.54) * mm});
            skLineSegment(sketch, "E1788", {"start": v(22.2, -97.54) * mm, "end": v(22.2, -98.28) * mm});
            skLineSegment(sketch, "E1789", {"start": v(22.2, -98.28) * mm, "end": v(22.2, -102.98) * mm});
            skLineSegment(sketch, "E1790", {"start": v(22.2, -102.98) * mm, "end": v(22.2, -108.33) * mm});
            skLineSegment(sketch, "E1791", {"start": v(22.2, -108.33) * mm, "end": v(22.2, -113.61) * mm});
            skLineSegment(sketch, "E1792", {"start": v(22.2, -113.61) * mm, "end": v(22.2, -114.24) * mm});
            skLineSegment(sketch, "E1793", {"start": v(22.2, -114.24) * mm, "end": v(22.2, -118.86) * mm});
            skLineSegment(sketch, "E1794", {"start": v(22.2, -118.86) * mm, "end": v(22.2, -119.58) * mm});
            skLineSegment(sketch, "E1795", {"start": v(22.2, -119.58) * mm, "end": v(22.2, -124.08) * mm});
            skLineSegment(sketch, "E1796", {"start": v(22.2, -124.08) * mm, "end": v(22.2, -124.84) * mm});
            skLineSegment(sketch, "E1797", {"start": v(22.2, -124.84) * mm, "end": v(22.2, -129.3) * mm});
            skLineSegment(sketch, "E1798", {"start": v(22.2, -129.3) * mm, "end": v(22.2, -130.04) * mm});
            skLineSegment(sketch, "E1799", {"start": v(22.2, -130.04) * mm, "end": v(22.2, -134.54) * mm});
            skLineSegment(sketch, "E1800", {"start": v(22.2, -134.54) * mm, "end": v(22.2, -135.21) * mm});
            skLineSegment(sketch, "E1801", {"start": v(22.2, -135.21) * mm, "end": v(22.2, -139.8) * mm});
            skLineSegment(sketch, "E1802", {"start": v(22.2, -139.8) * mm, "end": v(22.2, -140.37) * mm});
            skLineSegment(sketch, "E1803", {"start": v(22.2, -140.37) * mm, "end": v(22.2, -145.14) * mm});
            skLineSegment(sketch, "E1804", {"start": v(22.2, -145.14) * mm, "end": v(22.2, -150.55) * mm});
            skLineSegment(sketch, "E1805", {"start": v(22.2, -150.55) * mm, "end": v(22.2, -153.5) * mm});
            skLineSegment(sketch, "E1806", {"start": v(22.2, -153.5) * mm, "end": v(22.2, -154.27) * mm});
            skLineSegment(sketch, "E1807", {"start": v(22.2, -154.27) * mm, "end": v(22.21, -154.87) * mm});
            skLineSegment(sketch, "E1808", {"start": v(22.21, -154.87) * mm, "end": v(22.23, -155.74) * mm});
            skLineSegment(sketch, "E1809", {"start": v(22.23, -155.74) * mm, "end": v(22.26, -156.46) * mm});
            skLineSegment(sketch, "E1810", {"start": v(22.26, -156.46) * mm, "end": v(22.3, -157.09) * mm});
            skLineSegment(sketch, "E1811", {"start": v(22.3, -157.09) * mm, "end": v(22.33, -157.7) * mm});
            skLineSegment(sketch, "E1812", {"start": v(22.33, -157.7) * mm, "end": v(22.38, -158.33) * mm});
            skLineSegment(sketch, "E1813", {"start": v(22.38, -158.33) * mm, "end": v(22.43, -158.93) * mm});
            skLineSegment(sketch, "E1814", {"start": v(22.43, -158.93) * mm, "end": v(22.49, -159.53) * mm});
            skLineSegment(sketch, "E1815", {"start": v(22.49, -159.53) * mm, "end": v(22.55, -160.12) * mm});
            skLineSegment(sketch, "E1816", {"start": v(22.55, -160.12) * mm, "end": v(22.63, -160.7) * mm});
            skLineSegment(sketch, "E1817", {"start": v(22.63, -160.7) * mm, "end": v(22.7, -161.22) * mm});
            skLineSegment(sketch, "E1818", {"start": v(22.7, -161.22) * mm, "end": v(22.8, -161.8) * mm});
            skLineSegment(sketch, "E1819", {"start": v(22.8, -161.8) * mm, "end": v(22.9, -162.31) * mm});
            skLineSegment(sketch, "E1820", {"start": v(22.9, -162.31) * mm, "end": v(23.08, -163.15) * mm});
            skLineSegment(sketch, "E1821", {"start": v(23.08, -163.15) * mm, "end": v(23.23, -163.72) * mm});
            skLineSegment(sketch, "E1822", {"start": v(23.23, -163.72) * mm, "end": v(23.42, -164.37) * mm});
            skLineSegment(sketch, "E1823", {"start": v(23.42, -164.37) * mm, "end": v(23.62, -164.96) * mm});
            skLineSegment(sketch, "E1824", {"start": v(23.62, -164.96) * mm, "end": v(23.8, -165.45) * mm});
            skLineSegment(sketch, "E1825", {"start": v(23.8, -165.45) * mm, "end": v(24.05, -166) * mm});
            skLineSegment(sketch, "E1826", {"start": v(24.05, -166) * mm, "end": v(24.36, -166.58) * mm});
            skLineSegment(sketch, "E1827", {"start": v(24.36, -166.58) * mm, "end": v(24.68, -167.06) * mm});
            skLineSegment(sketch, "E1828", {"start": v(24.68, -167.06) * mm, "end": v(25, -167.45) * mm});
            skLineSegment(sketch, "E1829", {"start": v(25, -167.45) * mm, "end": v(27.76, -169.67) * mm});
            skLineSegment(sketch, "E1830", {"start": v(27.76, -169.67) * mm, "end": v(31.12, -172.2) * mm});
            skLineSegment(sketch, "E1831", {"start": v(31.12, -172.2) * mm, "end": v(34.13, -174.42) * mm});
            skLineSegment(sketch, "E1832", {"start": v(34.13, -174.42) * mm, "end": v(35.93, -175.7) * mm});
            skLineSegment(sketch, "E1833", {"start": v(35.93, -175.7) * mm, "end": v(37.88, -177.03) * mm});
            skLineSegment(sketch, "E1834", {"start": v(37.88, -177.03) * mm, "end": v(45.15, -181.84) * mm});
            skLineSegment(sketch, "E1835", {"start": v(45.15, -181.84) * mm, "end": v(45.15, -187.26) * mm});
            skLineSegment(sketch, "E1836", {"start": v(45.15, -187.26) * mm, "end": v(45.15, -188.12) * mm});
            skLineSegment(sketch, "E1837", {"start": v(45.15, -188.12) * mm, "end": v(45.15, -192.7) * mm});
            skLineSegment(sketch, "E1838", {"start": v(45.15, -192.7) * mm, "end": v(45.15, -194.52) * mm});
            skLineSegment(sketch, "E1839", {"start": v(45.15, -194.52) * mm, "end": v(45.15, -198.27) * mm});
            skLineSegment(sketch, "E1840", {"start": v(45.15, -198.27) * mm, "end": v(45.15, -201.18) * mm});
            skLineSegment(sketch, "E1841", {"start": v(45.15, -201.18) * mm, "end": v(45.15, -204) * mm});
            skLineSegment(sketch, "E1842", {"start": v(45.15, -204) * mm, "end": v(45.15, -208.14) * mm});
            skLineSegment(sketch, "E1843", {"start": v(45.15, -208.14) * mm, "end": v(45.15, -209.93) * mm});
            skLineSegment(sketch, "E1844", {"start": v(45.15, -209.93) * mm, "end": v(45.15, -215.45) * mm});
            skLineSegment(sketch, "E1845", {"start": v(45.15, -215.45) * mm, "end": v(45.15, -216.07) * mm});
            skLineSegment(sketch, "E1846", {"start": v(45.15, -216.07) * mm, "end": v(45.15, -219.02) * mm});
            skLineSegment(sketch, "E1847", {"start": v(45.15, -219.02) * mm, "end": v(30.15, -220.33) * mm});
            skLineSegment(sketch, "E1848", {"start": v(30.15, -220.33) * mm, "end": v(26, -220.69) * mm});
            skLineSegment(sketch, "E1849", {"start": v(26, -220.69) * mm, "end": v(25.48, -220.79) * mm});
            skLineSegment(sketch, "E1850", {"start": v(25.48, -220.79) * mm, "end": v(24.99, -220.99) * mm});
            skLineSegment(sketch, "E1851", {"start": v(24.99, -220.99) * mm, "end": v(24.5, -221.3) * mm});
            skLineSegment(sketch, "E1852", {"start": v(24.5, -221.3) * mm, "end": v(24.04, -221.73) * mm});
            skLineSegment(sketch, "E1853", {"start": v(24.04, -221.73) * mm, "end": v(23.62, -222.21) * mm});
            skLineSegment(sketch, "E1854", {"start": v(23.62, -222.21) * mm, "end": v(23.24, -222.78) * mm});
            skLineSegment(sketch, "E1855", {"start": v(23.24, -222.78) * mm, "end": v(23, -223.24) * mm});
            skLineSegment(sketch, "E1856", {"start": v(23, -223.24) * mm, "end": v(22.73, -223.88) * mm});
            skLineSegment(sketch, "E1857", {"start": v(22.73, -223.88) * mm, "end": v(22.55, -224.44) * mm});
            skLineSegment(sketch, "E1858", {"start": v(22.55, -224.44) * mm, "end": v(22.42, -224.97) * mm});
            skLineSegment(sketch, "E1859", {"start": v(22.42, -224.97) * mm, "end": v(22.32, -225.5) * mm});
            skLineSegment(sketch, "E1860", {"start": v(22.32, -225.5) * mm, "end": v(22.25, -226.06) * mm});
            skLineSegment(sketch, "E1861", {"start": v(22.25, -226.06) * mm, "end": v(22.21, -226.61) * mm});
            skLineSegment(sketch, "E1862", {"start": v(22.21, -226.61) * mm, "end": v(22.2, -228.64) * mm});
            skLineSegment(sketch, "E1863", {"start": v(22.2, -228.64) * mm, "end": v(22.2, -229.67) * mm});
            skLineSegment(sketch, "E1864", {"start": v(22.2, -229.67) * mm, "end": v(22.2, -233.5) * mm});
            skLineSegment(sketch, "E1865", {"start": v(22.2, -233.5) * mm, "end": v(22.2, -237.7) * mm});
            skLineSegment(sketch, "E1866", {"start": v(22.2, -237.7) * mm, "end": v(22.2, -238.36) * mm});
            skLineSegment(sketch, "E1867", {"start": v(22.2, -238.36) * mm, "end": v(22.2, -239.34) * mm});
            skLineSegment(sketch, "E1868", {"start": v(22.2, -239.34) * mm, "end": v(22.22, -239.91) * mm});
            skLineSegment(sketch, "E1869", {"start": v(22.22, -239.91) * mm, "end": v(22.27, -240.43) * mm});
            skLineSegment(sketch, "E1870", {"start": v(22.27, -240.43) * mm, "end": v(22.36, -240.93) * mm});
            skLineSegment(sketch, "E1871", {"start": v(22.36, -240.93) * mm, "end": v(22.5, -241.55) * mm});
            skLineSegment(sketch, "E1872", {"start": v(22.5, -241.55) * mm, "end": v(22.7, -242.12) * mm});
            skLineSegment(sketch, "E1873", {"start": v(22.7, -242.12) * mm, "end": v(22.93, -242.65) * mm});
            skLineSegment(sketch, "E1874", {"start": v(22.93, -242.65) * mm, "end": v(23.21, -243.17) * mm});
            skLineSegment(sketch, "E1875", {"start": v(23.21, -243.17) * mm, "end": v(23.5, -243.59) * mm});
            skLineSegment(sketch, "E1876", {"start": v(23.5, -243.59) * mm, "end": v(23.87, -244.02) * mm});
            skLineSegment(sketch, "E1877", {"start": v(23.87, -244.02) * mm, "end": v(24.32, -244.43) * mm});
            skLineSegment(sketch, "E1878", {"start": v(24.32, -244.43) * mm, "end": v(24.8, -244.74) * mm});
            skLineSegment(sketch, "E1879", {"start": v(24.8, -244.74) * mm, "end": v(25.31, -244.96) * mm});
            skLineSegment(sketch, "E1880", {"start": v(25.31, -244.96) * mm, "end": v(25.85, -245.1) * mm});
            skLineSegment(sketch, "E1881", {"start": v(25.85, -245.1) * mm, "end": v(30.12, -245.62) * mm});
            skLineSegment(sketch, "E1882", {"start": v(30.12, -245.62) * mm, "end": v(40.53, -246.86) * mm});
            skLineSegment(sketch, "E1883", {"start": v(40.53, -246.86) * mm, "end": v(42.4, -247.09) * mm});
            skLineSegment(sketch, "E1884", {"start": v(42.4, -247.09) * mm, "end": v(42.4, -245.76) * mm});
            skLineSegment(sketch, "E1885", {"start": v(42.4, -245.76) * mm, "end": v(53, -245.76) * mm});
            skLineSegment(sketch, "E1886", {"start": v(53, -245.76) * mm, "end": v(53.15, -242.18) * mm});
            skLineSegment(sketch, "E1887", {"start": v(53.15, -242.18) * mm, "end": v(53.15, -232.54) * mm});
            skLineSegment(sketch, "E1888", {"start": v(53.15, -232.54) * mm, "end": v(53.15, -223.61) * mm});
            skLineSegment(sketch, "E1889", {"start": v(53.15, -223.61) * mm, "end": v(53.15, -215.46) * mm});
            skLineSegment(sketch, "E1890", {"start": v(53.15, -215.46) * mm, "end": v(49.15, -215.3) * mm});
            skLineSegment(sketch, "E1891", {"start": v(49.15, -215.3) * mm, "end": v(49.15, -212.3) * mm});
            skLineSegment(sketch, "E1892", {"start": v(49.15, -212.3) * mm, "end": v(53, -212.3) * mm});
            skLineSegment(sketch, "E1893", {"start": v(53, -212.3) * mm, "end": v(53.15, -207.48) * mm});
            skLineSegment(sketch, "E1894", {"start": v(53.15, -207.48) * mm, "end": v(53.15, -200.12) * mm});
            skLineSegment(sketch, "E1895", {"start": v(53.15, -200.12) * mm, "end": v(53.15, -193.13) * mm});
            skLineSegment(sketch, "E1896", {"start": v(53.15, -193.13) * mm, "end": v(53.15, -192.61) * mm});
            skLineSegment(sketch, "E1897", {"start": v(53.15, -192.61) * mm, "end": v(53.15, -186.47) * mm});
            skLineSegment(sketch, "E1898", {"start": v(53.15, -186.47) * mm, "end": v(53.15, -185.92) * mm});
            skLineSegment(sketch, "E1899", {"start": v(53.15, -185.92) * mm, "end": v(53.15, -182) * mm});
            skLineSegment(sketch, "E1900", {"start": v(53.15, -182) * mm, "end": v(46.9, -181.85) * mm});
            skLineSegment(sketch, "E1901", {"start": v(46.9, -181.85) * mm, "end": v(46.9, -178.85) * mm});
            skLineSegment(sketch, "E1902", {"start": v(46.9, -178.85) * mm, "end": v(53, -178.85) * mm});
            skLineSegment(sketch, "E1903", {"start": v(53, -178.85) * mm, "end": v(53.15, -173.96) * mm});
            skLineSegment(sketch, "E1904", {"start": v(53.15, -173.96) * mm, "end": v(53.15, -173.36) * mm});
            skLineSegment(sketch, "E1905", {"start": v(53.15, -173.36) * mm, "end": v(53.15, -168.04) * mm});
            skLineSegment(sketch, "E1906", {"start": v(53.15, -168.04) * mm, "end": v(53.15, -167.41) * mm});
            skLineSegment(sketch, "E1907", {"start": v(53.15, -167.41) * mm, "end": v(53.15, -162.29) * mm});
            skLineSegment(sketch, "E1908", {"start": v(53.15, -162.29) * mm, "end": v(53.15, -161.64) * mm});
            skLineSegment(sketch, "E1909", {"start": v(53.15, -161.64) * mm, "end": v(53.15, -156.68) * mm});
            skLineSegment(sketch, "E1910", {"start": v(53.15, -156.68) * mm, "end": v(53.15, -156.03) * mm});
            skLineSegment(sketch, "E1911", {"start": v(53.15, -156.03) * mm, "end": v(53.15, -151.2) * mm});
            skLineSegment(sketch, "E1912", {"start": v(53.15, -151.2) * mm, "end": v(53.15, -150.53) * mm});
            skLineSegment(sketch, "E1913", {"start": v(53.15, -150.53) * mm, "end": v(53.15, -148.55) * mm});
            skLineSegment(sketch, "E1914", {"start": v(53.15, -148.55) * mm, "end": v(37.68, -148.4) * mm});
            skLineSegment(sketch, "E1915", {"start": v(37.68, -148.4) * mm, "end": v(37.68, -145.4) * mm});
            skLineSegment(sketch, "E1916", {"start": v(37.68, -145.4) * mm, "end": v(53, -145.4) * mm});
            skLineSegment(sketch, "E1917", {"start": v(53, -145.4) * mm, "end": v(53.15, -140.5) * mm});
            skLineSegment(sketch, "E1918", {"start": v(53.15, -140.5) * mm, "end": v(53.15, -139.82) * mm});
            skLineSegment(sketch, "E1919", {"start": v(53.15, -139.82) * mm, "end": v(53.15, -135.24) * mm});
            skLineSegment(sketch, "E1920", {"start": v(53.15, -135.24) * mm, "end": v(53.15, -134.56) * mm});
            skLineSegment(sketch, "E1921", {"start": v(53.15, -134.56) * mm, "end": v(53.15, -130.02) * mm});
            skLineSegment(sketch, "E1922", {"start": v(53.15, -130.02) * mm, "end": v(53.15, -129.34) * mm});
            skLineSegment(sketch, "E1923", {"start": v(53.15, -129.34) * mm, "end": v(53.15, -124.81) * mm});
            skLineSegment(sketch, "E1924", {"start": v(53.15, -124.81) * mm, "end": v(53.15, -124.13) * mm});
            skLineSegment(sketch, "E1925", {"start": v(53.15, -124.13) * mm, "end": v(53.15, -119.6) * mm});
            skLineSegment(sketch, "E1926", {"start": v(53.15, -119.6) * mm, "end": v(53.15, -118.92) * mm});
            skLineSegment(sketch, "E1927", {"start": v(53.15, -118.92) * mm, "end": v(53.15, -115.1) * mm});
            skLineSegment(sketch, "E1928", {"start": v(53.15, -115.1) * mm, "end": v(37.68, -114.94) * mm});
            skLineSegment(sketch, "E1929", {"start": v(37.68, -114.94) * mm, "end": v(37.68, -111.94) * mm});
            skLineSegment(sketch, "E1930", {"start": v(37.68, -111.94) * mm, "end": v(53, -111.94) * mm});
            skLineSegment(sketch, "E1931", {"start": v(53, -111.94) * mm, "end": v(53.15, -109.07) * mm});
            skLineSegment(sketch, "E1932", {"start": v(53.15, -109.07) * mm, "end": v(53.15, -108.4) * mm});
            skLineSegment(sketch, "E1933", {"start": v(53.15, -108.4) * mm, "end": v(53.15, -103.72) * mm});
            skLineSegment(sketch, "E1934", {"start": v(53.15, -103.72) * mm, "end": v(53.15, -103.06) * mm});
            skLineSegment(sketch, "E1935", {"start": v(53.15, -103.06) * mm, "end": v(53.15, -102.4) * mm});
            skLineSegment(sketch, "E1936", {"start": v(53.15, -102.4) * mm, "end": v(53.15, -101.74) * mm});
            skLineSegment(sketch, "E1937", {"start": v(53.15, -101.74) * mm, "end": v(53.15, -101.1) * mm});
            skLineSegment(sketch, "E1938", {"start": v(53.15, -101.1) * mm, "end": v(53.15, -100.47) * mm});
            skLineSegment(sketch, "E1939", {"start": v(53.15, -100.47) * mm, "end": v(53.15, -99.85) * mm});
            skLineSegment(sketch, "E1940", {"start": v(53.15, -99.85) * mm, "end": v(53.15, -99.25) * mm});
            skLineSegment(sketch, "E1941", {"start": v(53.15, -99.25) * mm, "end": v(53.15, -98.66) * mm});
            skLineSegment(sketch, "E1942", {"start": v(53.15, -98.66) * mm, "end": v(53.15, -98.1) * mm});
            skLineSegment(sketch, "E1943", {"start": v(53.15, -98.1) * mm, "end": v(53.15, -97.55) * mm});
            skLineSegment(sketch, "E1944", {"start": v(53.15, -97.55) * mm, "end": v(53.15, -81.63) * mm});
            skLineSegment(sketch, "E1945", {"start": v(53.15, -81.63) * mm, "end": v(41, -81.48) * mm});
            skLineSegment(sketch, "E1946", {"start": v(41, -81.48) * mm, "end": v(41, -78.48) * mm});
            skLineSegment(sketch, "E1947", {"start": v(41, -78.48) * mm, "end": v(53, -78.48) * mm});
            skLineSegment(sketch, "E1948", {"start": v(53, -78.48) * mm, "end": v(53.15, -48.18) * mm});
            skLineSegment(sketch, "E1949", {"start": v(53.15, -48.18) * mm, "end": v(49.15, -48.03) * mm});
            skLineSegment(sketch, "E1950", {"start": v(49.15, -48.03) * mm, "end": v(49.15, -45.03) * mm});
            skLineSegment(sketch, "E1951", {"start": v(49.15, -45.03) * mm, "end": v(53, -45.03) * mm});
            skLineSegment(sketch, "E1952", {"start": v(53, -45.03) * mm, "end": v(53.15, -14.72) * mm});
            skLineSegment(sketch, "E1953", {"start": v(53.15, -14.72) * mm, "end": v(49.15, -14.57) * mm});
            skLineSegment(sketch, "E1954", {"start": v(49.15, -14.57) * mm, "end": v(49.15, -11.57) * mm});
            skLineSegment(sketch, "E1955", {"start": v(49.15, -11.57) * mm, "end": v(53, -11.57) * mm});
            skLineSegment(sketch, "E1956", {"start": v(53, -11.57) * mm, "end": v(53.15, 18.73) * mm});
            skLineSegment(sketch, "E1957", {"start": v(53.15, 18.73) * mm, "end": v(49.15, 18.88) * mm});
            skLineSegment(sketch, "E1958", {"start": v(49.15, 18.88) * mm, "end": v(49.15, 21.88) * mm});
            skLineSegment(sketch, "E1959", {"start": v(49.15, 21.88) * mm, "end": v(53, 21.88) * mm});
            skLineSegment(sketch, "E1960", {"start": v(53, 21.88) * mm, "end": v(53.15, 52.19) * mm});
            skLineSegment(sketch, "E1961", {"start": v(53.15, 52.19) * mm, "end": v(49.15, 52.34) * mm});
            skLineSegment(sketch, "E1962", {"start": v(49.15, 52.34) * mm, "end": v(49.15, 55.34) * mm});
            skLineSegment(sketch, "E1963", {"start": v(49.15, 55.34) * mm, "end": v(53, 55.34) * mm});
            skLineSegment(sketch, "E1964", {"start": v(53, 55.34) * mm, "end": v(53.15, 75.95) * mm});
            skLineSegment(sketch, "E1965", {"start": v(53.15, 75.95) * mm, "end": v(53.15, 76.8) * mm});
            skLineSegment(sketch, "E1966", {"start": v(53.15, 76.8) * mm, "end": v(53.15, 77.64) * mm});
            skLineSegment(sketch, "E1967", {"start": v(53.15, 77.64) * mm, "end": v(53.15, 78.47) * mm});
            skLineSegment(sketch, "E1968", {"start": v(53.15, 78.47) * mm, "end": v(53.15, 79.27) * mm});
            skLineSegment(sketch, "E1969", {"start": v(53.15, 79.27) * mm, "end": v(53.15, 80.03) * mm});
            skLineSegment(sketch, "E1970", {"start": v(53.15, 80.03) * mm, "end": v(53.15, 80.68) * mm});
            skLineSegment(sketch, "E1971", {"start": v(53.15, 80.68) * mm, "end": v(53.15, 81.4) * mm});
            skLineSegment(sketch, "E1972", {"start": v(53.15, 81.4) * mm, "end": v(53.15, 81.94) * mm});
            skLineSegment(sketch, "E1973", {"start": v(53.15, 81.94) * mm, "end": v(53.15, 82.5) * mm});
            skLineSegment(sketch, "E1974", {"start": v(53.15, 82.5) * mm, "end": v(53.15, 83.07) * mm});
            skLineSegment(sketch, "E1975", {"start": v(53.15, 83.07) * mm, "end": v(53.15, 83.67) * mm});
            skLineSegment(sketch, "E1976", {"start": v(53.15, 83.67) * mm, "end": v(53.15, 84.29) * mm});
            skLineSegment(sketch, "E1977", {"start": v(53.15, 84.29) * mm, "end": v(53.15, 84.92) * mm});
            skLineSegment(sketch, "E1978", {"start": v(53.15, 84.92) * mm, "end": v(53.15, 85.56) * mm});
            skLineSegment(sketch, "E1979", {"start": v(53.15, 85.56) * mm, "end": v(46.35, 85.8) * mm});
            skLineSegment(sketch, "E1980", {"start": v(46.35, 85.8) * mm, "end": v(46.35, 88.8) * mm});
            skLineSegment(sketch, "E1981", {"start": v(46.35, 88.8) * mm, "end": v(53, 88.8) * mm});
            skLineSegment(sketch, "E1982", {"start": v(53, 88.8) * mm, "end": v(53.15, 89.29) * mm});
            skLineSegment(sketch, "E1983", {"start": v(53.15, 89.29) * mm, "end": v(53.15, 89.84) * mm});
            skLineSegment(sketch, "E1984", {"start": v(53.15, 89.84) * mm, "end": v(53.15, 90.56) * mm});
            skLineSegment(sketch, "E1985", {"start": v(53.15, 90.56) * mm, "end": v(53.15, 91.21) * mm});
            skLineSegment(sketch, "E1986", {"start": v(53.15, 91.21) * mm, "end": v(53.15, 91.78) * mm});
            skLineSegment(sketch, "E1987", {"start": v(53.15, 91.78) * mm, "end": v(53.15, 104.02) * mm});
            skLineSegment(sketch, "E1988", {"start": v(41.87, 241.18) * mm, "end": v(41.62, 240.67) * mm});
            skLineSegment(sketch, "E1989", {"start": v(41.62, 240.67) * mm, "end": v(41.44, 240.15) * mm});
            skLineSegment(sketch, "E1990", {"start": v(41.44, 240.15) * mm, "end": v(41.31, 239.6) * mm});
            skLineSegment(sketch, "E1991", {"start": v(41.31, 239.6) * mm, "end": v(40.9, 237.23) * mm});
            skLineSegment(sketch, "E1992", {"start": v(40.9, 237.23) * mm, "end": v(40.26, 233.54) * mm});
            skLineSegment(sketch, "E1993", {"start": v(40.26, 233.54) * mm, "end": v(40.1, 232.55) * mm});
            skLineSegment(sketch, "E1994", {"start": v(40.1, 232.55) * mm, "end": v(39.97, 231.88) * mm});
            skLineSegment(sketch, "E1995", {"start": v(39.97, 231.88) * mm, "end": v(39.1, 227.61) * mm});
            skLineSegment(sketch, "E1996", {"start": v(39.1, 227.61) * mm, "end": v(45.89, 227.46) * mm});
            skLineSegment(sketch, "E1997", {"start": v(45.89, 227.46) * mm, "end": v(45.89, 224.46) * mm});
            skLineSegment(sketch, "E1998", {"start": v(45.89, 224.46) * mm, "end": v(38.56, 224.46) * mm});
            skLineSegment(sketch, "E1999", {"start": v(38.56, 224.46) * mm, "end": v(37.37, 219.94) * mm});
            skLineSegment(sketch, "E2000", {"start": v(37.37, 219.94) * mm, "end": v(36.75, 217.35) * mm});
            skLineSegment(sketch, "E2001", {"start": v(36.75, 217.35) * mm, "end": v(35.06, 211.07) * mm});
            skLineSegment(sketch, "E2002", {"start": v(35.06, 211.07) * mm, "end": v(34.85, 210.3) * mm});
            skLineSegment(sketch, "E2003", {"start": v(34.85, 210.3) * mm, "end": v(34.48, 209.06) * mm});
            skLineSegment(sketch, "E2004", {"start": v(34.48, 209.06) * mm, "end": v(32.76, 203.4) * mm});
            skLineSegment(sketch, "E2005", {"start": v(32.76, 203.4) * mm, "end": v(31.41, 199.35) * mm});
            skLineSegment(sketch, "E2006", {"start": v(31.41, 199.35) * mm, "end": v(30.5, 196.6) * mm});
            skLineSegment(sketch, "E2007", {"start": v(30.5, 196.6) * mm, "end": v(29.7, 194.45) * mm});
            skLineSegment(sketch, "E2008", {"start": v(29.7, 194.45) * mm, "end": v(29.28, 193.31) * mm});
            skLineSegment(sketch, "E2009", {"start": v(29.28, 193.31) * mm, "end": v(40.84, 193.16) * mm});
            skLineSegment(sketch, "E2010", {"start": v(40.84, 193.16) * mm, "end": v(40.84, 190.16) * mm});
            skLineSegment(sketch, "E2011", {"start": v(40.84, 190.16) * mm, "end": v(28.22, 190.16) * mm});
            skLineSegment(sketch, "E2012", {"start": v(28.22, 190.16) * mm, "end": v(25.45, 183.46) * mm});
            skLineSegment(sketch, "E2013", {"start": v(25.45, 183.46) * mm, "end": v(22.93, 177.68) * mm});
            skLineSegment(sketch, "E2014", {"start": v(22.93, 177.68) * mm, "end": v(22.57, 176.84) * mm});
            skLineSegment(sketch, "E2015", {"start": v(22.57, 176.84) * mm, "end": v(22.39, 176.34) * mm});
            skLineSegment(sketch, "E2016", {"start": v(22.39, 176.34) * mm, "end": v(22.26, 175.83) * mm});
            skLineSegment(sketch, "E2017", {"start": v(22.26, 175.83) * mm, "end": v(22.2, 175.3) * mm});
            skLineSegment(sketch, "E2018", {"start": v(22.2, 175.3) * mm, "end": v(22.2, 173.88) * mm});
            skLineSegment(sketch, "E2019", {"start": v(22.2, 173.88) * mm, "end": v(22.2, 159.01) * mm});
            skLineSegment(sketch, "E2020", {"start": v(22.2, 159.01) * mm, "end": v(37.68, 158.86) * mm});
            skLineSegment(sketch, "E2021", {"start": v(37.68, 158.86) * mm, "end": v(37.68, 155.86) * mm});
            skLineSegment(sketch, "E2022", {"start": v(37.68, 155.86) * mm, "end": v(22.37, 155.86) * mm});
            skLineSegment(sketch, "E2023", {"start": v(22.37, 155.86) * mm, "end": v(22.26, 155.35) * mm});
            skLineSegment(sketch, "E2024", {"start": v(22.26, 155.35) * mm, "end": v(22.38, 154.85) * mm});
            skLineSegment(sketch, "E2025", {"start": v(22.38, 154.85) * mm, "end": v(22.55, 154.36) * mm});
            skLineSegment(sketch, "E2026", {"start": v(22.55, 154.36) * mm, "end": v(22.8, 153.9) * mm});
            skLineSegment(sketch, "E2027", {"start": v(22.8, 153.9) * mm, "end": v(23.08, 153.49) * mm});
            skLineSegment(sketch, "E2028", {"start": v(23.08, 153.49) * mm, "end": v(23.42, 153.1) * mm});
            skLineSegment(sketch, "E2029", {"start": v(23.42, 153.1) * mm, "end": v(23.8, 152.77) * mm});
            skLineSegment(sketch, "E2030", {"start": v(23.8, 152.77) * mm, "end": v(24.23, 152.5) * mm});
            skLineSegment(sketch, "E2031", {"start": v(24.23, 152.5) * mm, "end": v(24.71, 152.26) * mm});
            skLineSegment(sketch, "E2032", {"start": v(24.71, 152.26) * mm, "end": v(31.04, 150.5) * mm});
            skLineSegment(sketch, "E2033", {"start": v(31.04, 150.5) * mm, "end": v(45.15, 146.7) * mm});
            skLineSegment(sketch, "E2034", {"start": v(45.15, 146.7) * mm, "end": v(45.15, 138.49) * mm});
            skLineSegment(sketch, "E2035", {"start": v(45.15, 138.49) * mm, "end": v(45.15, 126.97) * mm});
            skLineSegment(sketch, "E2036", {"start": v(45.15, 126.97) * mm, "end": v(31.53, 126.24) * mm});
            skLineSegment(sketch, "E2037", {"start": v(31.53, 126.24) * mm, "end": v(26, 125.94) * mm});
            skLineSegment(sketch, "E2038", {"start": v(26, 125.94) * mm, "end": v(25.48, 125.89) * mm});
            skLineSegment(sketch, "E2039", {"start": v(25.48, 125.89) * mm, "end": v(24.97, 125.76) * mm});
            skLineSegment(sketch, "E2040", {"start": v(24.97, 125.76) * mm, "end": v(24.49, 125.56) * mm});
            skLineSegment(sketch, "E2041", {"start": v(24.49, 125.56) * mm, "end": v(24.03, 125.3) * mm});
            skLineSegment(sketch, "E2042", {"start": v(24.03, 125.3) * mm, "end": v(23.62, 125) * mm});
            skLineSegment(sketch, "E2043", {"start": v(23.62, 125) * mm, "end": v(37.73, 124.56) * mm});
            skLineSegment(sketch, "E2044", {"start": v(37.73, 124.56) * mm, "end": v(37.73, 121.56) * mm});
            skLineSegment(sketch, "E2045", {"start": v(37.73, 121.56) * mm, "end": v(22.35, 121.56) * mm});
            skLineSegment(sketch, "E2046", {"start": v(22.35, 121.56) * mm, "end": v(22.2, 116.07) * mm});
            skLineSegment(sketch, "E2047", {"start": v(22.2, 116.07) * mm, "end": v(22.2, 113.63) * mm});
            skLineSegment(sketch, "E2048", {"start": v(22.2, 113.63) * mm, "end": v(22.24, 113.1) * mm});
            skLineSegment(sketch, "E2049", {"start": v(22.24, 113.1) * mm, "end": v(22.34, 112.59) * mm});
            skLineSegment(sketch, "E2050", {"start": v(22.34, 112.59) * mm, "end": v(22.5, 112.09) * mm});
            skLineSegment(sketch, "E2051", {"start": v(22.5, 112.09) * mm, "end": v(22.74, 111.62) * mm});
            skLineSegment(sketch, "E2052", {"start": v(22.74, 111.62) * mm, "end": v(23.03, 111.18) * mm});
            skLineSegment(sketch, "E2053", {"start": v(23.03, 111.18) * mm, "end": v(23.37, 110.78) * mm});
            skLineSegment(sketch, "E2054", {"start": v(23.37, 110.78) * mm, "end": v(23.77, 110.43) * mm});
            skLineSegment(sketch, "E2055", {"start": v(23.77, 110.43) * mm, "end": v(24.2, 110.14) * mm});
            skLineSegment(sketch, "E2056", {"start": v(24.2, 110.14) * mm, "end": v(24.67, 109.9) * mm});
            skLineSegment(sketch, "E2057", {"start": v(24.67, 109.9) * mm, "end": v(25.17, 109.74) * mm});
            skLineSegment(sketch, "E2058", {"start": v(25.17, 109.74) * mm, "end": v(25.68, 109.63) * mm});
            skLineSegment(sketch, "E2059", {"start": v(25.68, 109.63) * mm, "end": v(50.1, 107.46) * mm});
            skLineSegment(sketch, "E2060", {"start": v(50.1, 107.46) * mm, "end": v(53.15, 107.2) * mm});
            skLineSegment(sketch, "E2061", {"start": v(53.15, 107.2) * mm, "end": v(53.15, 147.24) * mm});
            skLineSegment(sketch, "E2062", {"start": v(53.15, 147.24) * mm, "end": v(53.15, 150.57) * mm});
            skLineSegment(sketch, "E2063", {"start": v(53.15, 150.57) * mm, "end": v(53.15, 174.03) * mm});
            skLineSegment(sketch, "E2064", {"start": v(53.15, 174.03) * mm, "end": v(53.15, 178.4) * mm});
            skLineSegment(sketch, "E2065", {"start": v(53.15, 178.4) * mm, "end": v(53.15, 191.94) * mm});
            skLineSegment(sketch, "E2066", {"start": v(53.15, 191.94) * mm, "end": v(53.15, 196.51) * mm});
            skLineSegment(sketch, "E2067", {"start": v(53.15, 196.51) * mm, "end": v(53.15, 204.8) * mm});
            skLineSegment(sketch, "E2068", {"start": v(53.15, 204.8) * mm, "end": v(53.15, 209.28) * mm});
            skLineSegment(sketch, "E2069", {"start": v(53.15, 209.28) * mm, "end": v(53.15, 214.5) * mm});
            skLineSegment(sketch, "E2070", {"start": v(53.15, 214.5) * mm, "end": v(53.15, 218.8) * mm});
            skLineSegment(sketch, "E2071", {"start": v(53.15, 218.8) * mm, "end": v(53.15, 222.12) * mm});
            skLineSegment(sketch, "E2072", {"start": v(53.15, 222.12) * mm, "end": v(53.15, 226.2) * mm});
            skLineSegment(sketch, "E2073", {"start": v(53.15, 226.2) * mm, "end": v(53.15, 228.26) * mm});
            skLineSegment(sketch, "E2074", {"start": v(53.15, 228.26) * mm, "end": v(53.15, 232.12) * mm});
            skLineSegment(sketch, "E2075", {"start": v(53.15, 232.12) * mm, "end": v(53.15, 233.35) * mm});
            skLineSegment(sketch, "E2076", {"start": v(53.15, 233.35) * mm, "end": v(53.15, 237) * mm});
            skLineSegment(sketch, "E2077", {"start": v(53.15, 237) * mm, "end": v(53.15, 237.63) * mm});
            skLineSegment(sketch, "E2078", {"start": v(53.15, 237.63) * mm, "end": v(53.15, 241.1) * mm});
            skLineSegment(sketch, "E2079", {"start": v(53.15, 241.1) * mm, "end": v(53.15, 243.32) * mm});
            skLineSegment(sketch, "E2080", {"start": v(53.15, 243.32) * mm, "end": v(50.1, 243.32) * mm});
            skLineSegment(sketch, "E2081", {"start": v(50.1, 243.32) * mm, "end": v(45.23, 243.32) * mm});
            skLineSegment(sketch, "E2082", {"start": v(45.23, 243.32) * mm, "end": v(44.71, 243.28) * mm});
            skLineSegment(sketch, "E2083", {"start": v(44.71, 243.28) * mm, "end": v(44.2, 243.17) * mm});
            skLineSegment(sketch, "E2084", {"start": v(44.2, 243.17) * mm, "end": v(43.7, 242.97) * mm});
            skLineSegment(sketch, "E2085", {"start": v(43.7, 242.97) * mm, "end": v(43.24, 242.7) * mm});
            skLineSegment(sketch, "E2086", {"start": v(43.24, 242.7) * mm, "end": v(42.8, 242.36) * mm});
            skLineSegment(sketch, "E2087", {"start": v(42.8, 242.36) * mm, "end": v(42.4, 241.96) * mm});
            skLineSegment(sketch, "E2088", {"start": v(42.4, 241.96) * mm, "end": v(42.06, 241.5) * mm});
            skLineSegment(sketch, "E2089", {"start": v(42.06, 241.5) * mm, "end": v(41.87, 241.18) * mm});
            skLineSegment(sketch, "E2090", {"start": v(87.27, 69.77) * mm, "end": v(87.27, 76.83) * mm});
            skLineSegment(sketch, "E2091", {"start": v(87.27, 76.83) * mm, "end": v(78.22, 76.01) * mm});
            skLineSegment(sketch, "E2092", {"start": v(78.22, 76.01) * mm, "end": v(59.98, 74.33) * mm});
            skLineSegment(sketch, "E2093", {"start": v(59.98, 74.33) * mm, "end": v(59.46, 74.24) * mm});
            skLineSegment(sketch, "E2094", {"start": v(59.46, 74.24) * mm, "end": v(58.96, 74.09) * mm});
            skLineSegment(sketch, "E2095", {"start": v(58.96, 74.09) * mm, "end": v(58.48, 73.86) * mm});
            skLineSegment(sketch, "E2096", {"start": v(58.48, 73.86) * mm, "end": v(58.03, 73.58) * mm});
            skLineSegment(sketch, "E2097", {"start": v(58.03, 73.58) * mm, "end": v(57.62, 73.23) * mm});
            skLineSegment(sketch, "E2098", {"start": v(57.62, 73.23) * mm, "end": v(57.26, 72.84) * mm});
            skLineSegment(sketch, "E2099", {"start": v(57.26, 72.84) * mm, "end": v(56.95, 72.4) * mm});
            skLineSegment(sketch, "E2100", {"start": v(56.95, 72.4) * mm, "end": v(56.71, 71.94) * mm});
            skLineSegment(sketch, "E2101", {"start": v(56.71, 71.94) * mm, "end": v(56.52, 71.42) * mm});
            skLineSegment(sketch, "E2102", {"start": v(56.52, 71.42) * mm, "end": v(56.4, 70.88) * mm});
            skLineSegment(sketch, "E2103", {"start": v(56.4, 70.88) * mm, "end": v(56.33, 70.33) * mm});
            skLineSegment(sketch, "E2104", {"start": v(56.33, 70.33) * mm, "end": v(71.8, 70.06) * mm});
            skLineSegment(sketch, "E2105", {"start": v(71.8, 70.06) * mm, "end": v(71.8, 67.06) * mm});
            skLineSegment(sketch, "E2106", {"start": v(71.8, 67.06) * mm, "end": v(56.48, 67.06) * mm});
            skLineSegment(sketch, "E2107", {"start": v(56.48, 67.06) * mm, "end": v(56.33, 65.08) * mm});
            skLineSegment(sketch, "E2108", {"start": v(56.33, 65.08) * mm, "end": v(56.33, 61.39) * mm});
            skLineSegment(sketch, "E2109", {"start": v(56.33, 61.39) * mm, "end": v(56.36, 60.87) * mm});
            skLineSegment(sketch, "E2110", {"start": v(56.36, 60.87) * mm, "end": v(56.46, 60.32) * mm});
            skLineSegment(sketch, "E2111", {"start": v(56.46, 60.32) * mm, "end": v(56.62, 59.79) * mm});
            skLineSegment(sketch, "E2112", {"start": v(56.62, 59.79) * mm, "end": v(56.85, 59.29) * mm});
            skLineSegment(sketch, "E2113", {"start": v(56.85, 59.29) * mm, "end": v(57.14, 58.82) * mm});
            skLineSegment(sketch, "E2114", {"start": v(57.14, 58.82) * mm, "end": v(57.48, 58.4) * mm});
            skLineSegment(sketch, "E2115", {"start": v(57.48, 58.4) * mm, "end": v(57.87, 58.03) * mm});
            skLineSegment(sketch, "E2116", {"start": v(57.87, 58.03) * mm, "end": v(58.3, 57.72) * mm});
            skLineSegment(sketch, "E2117", {"start": v(58.3, 57.72) * mm, "end": v(58.77, 57.47) * mm});
            skLineSegment(sketch, "E2118", {"start": v(58.77, 57.47) * mm, "end": v(59.26, 57.28) * mm});
            skLineSegment(sketch, "E2119", {"start": v(59.26, 57.28) * mm, "end": v(59.77, 57.17) * mm});
            skLineSegment(sketch, "E2120", {"start": v(59.77, 57.17) * mm, "end": v(62.66, 57) * mm});
            skLineSegment(sketch, "E2121", {"start": v(62.66, 57) * mm, "end": v(79.27, 56.03) * mm});
            skLineSegment(sketch, "E2122", {"start": v(79.27, 56.03) * mm, "end": v(79.27, 52.56) * mm});
            skLineSegment(sketch, "E2123", {"start": v(79.27, 52.56) * mm, "end": v(79.27, 49.15) * mm});
            skLineSegment(sketch, "E2124", {"start": v(79.27, 49.15) * mm, "end": v(79.27, 41.73) * mm});
            skLineSegment(sketch, "E2125", {"start": v(79.27, 41.73) * mm, "end": v(79.27, 35.9) * mm});
            skLineSegment(sketch, "E2126", {"start": v(79.27, 35.9) * mm, "end": v(81.03, 35.76) * mm});
            skLineSegment(sketch, "E2127", {"start": v(81.03, 35.76) * mm, "end": v(81.03, 32.76) * mm});
            skLineSegment(sketch, "E2128", {"start": v(81.03, 32.76) * mm, "end": v(71.87, 32.76) * mm});
            skLineSegment(sketch, "E2129", {"start": v(71.87, 32.76) * mm, "end": v(65.26, 30.81) * mm});
            skLineSegment(sketch, "E2130", {"start": v(65.26, 30.81) * mm, "end": v(61.1, 29.57) * mm});
            skLineSegment(sketch, "E2131", {"start": v(61.1, 29.57) * mm, "end": v(59.3, 29.04) * mm});
            skLineSegment(sketch, "E2132", {"start": v(59.3, 29.04) * mm, "end": v(58.81, 28.83) * mm});
            skLineSegment(sketch, "E2133", {"start": v(58.81, 28.83) * mm, "end": v(58.36, 28.59) * mm});
            skLineSegment(sketch, "E2134", {"start": v(58.36, 28.59) * mm, "end": v(57.93, 28.28) * mm});
            skLineSegment(sketch, "E2135", {"start": v(57.93, 28.28) * mm, "end": v(57.55, 27.92) * mm});
            skLineSegment(sketch, "E2136", {"start": v(57.55, 27.92) * mm, "end": v(57.2, 27.5) * mm});
            skLineSegment(sketch, "E2137", {"start": v(57.2, 27.5) * mm, "end": v(56.91, 27.05) * mm});
            skLineSegment(sketch, "E2138", {"start": v(56.91, 27.05) * mm, "end": v(56.68, 26.55) * mm});
            skLineSegment(sketch, "E2139", {"start": v(56.68, 26.55) * mm, "end": v(56.51, 26.07) * mm});
            skLineSegment(sketch, "E2140", {"start": v(56.51, 26.07) * mm, "end": v(56.39, 25.52) * mm});
            skLineSegment(sketch, "E2141", {"start": v(56.39, 25.52) * mm, "end": v(56.33, 24.95) * mm});
            skLineSegment(sketch, "E2142", {"start": v(56.33, 24.95) * mm, "end": v(56.33, 23.74) * mm});
            skLineSegment(sketch, "E2143", {"start": v(56.33, 23.74) * mm, "end": v(56.33, 16.25) * mm});
            skLineSegment(sketch, "E2144", {"start": v(56.33, 16.25) * mm, "end": v(56.33, 12.57) * mm});
            skLineSegment(sketch, "E2145", {"start": v(56.33, 12.57) * mm, "end": v(56.33, 9.5) * mm});
            skLineSegment(sketch, "E2146", {"start": v(56.33, 9.5) * mm, "end": v(56.33, 3.4) * mm});
            skLineSegment(sketch, "E2147", {"start": v(56.33, 3.4) * mm, "end": v(56.36, 2.73) * mm});
            skLineSegment(sketch, "E2148", {"start": v(56.36, 2.73) * mm, "end": v(56.46, 2.13) * mm});
            skLineSegment(sketch, "E2149", {"start": v(56.46, 2.13) * mm, "end": v(56.6, 1.6) * mm});
            skLineSegment(sketch, "E2150", {"start": v(56.6, 1.6) * mm, "end": v(72.07, 1.46) * mm});
            skLineSegment(sketch, "E2151", {"start": v(72.07, 1.46) * mm, "end": v(72.07, -1.54) * mm});
            skLineSegment(sketch, "E2152", {"start": v(72.07, -1.54) * mm, "end": v(57.98, -1.54) * mm});
            skLineSegment(sketch, "E2153", {"start": v(57.98, -1.54) * mm, "end": v(58.18, -2.6) * mm});
            skLineSegment(sketch, "E2154", {"start": v(58.18, -2.6) * mm, "end": v(58.72, -4.09) * mm});
            skLineSegment(sketch, "E2155", {"start": v(58.72, -4.09) * mm, "end": v(59.52, -6.22) * mm});
            skLineSegment(sketch, "E2156", {"start": v(59.52, -6.22) * mm, "end": v(59.86, -7.24) * mm});
            skLineSegment(sketch, "E2157", {"start": v(59.86, -7.24) * mm, "end": v(60.17, -8.14) * mm});
            skLineSegment(sketch, "E2158", {"start": v(60.17, -8.14) * mm, "end": v(61.12, -11) * mm});
            skLineSegment(sketch, "E2159", {"start": v(61.12, -11) * mm, "end": v(62.16, -14.12) * mm});
            skLineSegment(sketch, "E2160", {"start": v(62.16, -14.12) * mm, "end": v(62.4, -14.93) * mm});
            skLineSegment(sketch, "E2161", {"start": v(62.4, -14.93) * mm, "end": v(63.37, -18.2) * mm});
            skLineSegment(sketch, "E2162", {"start": v(63.37, -18.2) * mm, "end": v(64.2, -21) * mm});
            skLineSegment(sketch, "E2163", {"start": v(64.2, -21) * mm, "end": v(64.37, -21.6) * mm});
            skLineSegment(sketch, "E2164", {"start": v(64.37, -21.6) * mm, "end": v(64.62, -22.47) * mm});
            skLineSegment(sketch, "E2165", {"start": v(64.62, -22.47) * mm, "end": v(65.28, -25) * mm});
            skLineSegment(sketch, "E2166", {"start": v(65.28, -25) * mm, "end": v(65.65, -26.45) * mm});
            skLineSegment(sketch, "E2167", {"start": v(65.65, -26.45) * mm, "end": v(66.11, -28.3) * mm});
            skLineSegment(sketch, "E2168", {"start": v(66.11, -28.3) * mm, "end": v(66.89, -31.39) * mm});
            skLineSegment(sketch, "E2169", {"start": v(66.89, -31.39) * mm, "end": v(67.17, -32.7) * mm});
            skLineSegment(sketch, "E2170", {"start": v(67.17, -32.7) * mm, "end": v(77.24, -32.84) * mm});
            skLineSegment(sketch, "E2171", {"start": v(77.24, -32.84) * mm, "end": v(77.24, -35.84) * mm});
            skLineSegment(sketch, "E2172", {"start": v(77.24, -35.84) * mm, "end": v(68.04, -35.84) * mm});
            skLineSegment(sketch, "E2173", {"start": v(68.04, -35.84) * mm, "end": v(68.23, -37.6) * mm});
            skLineSegment(sketch, "E2174", {"start": v(68.23, -37.6) * mm, "end": v(68.76, -40.17) * mm});
            skLineSegment(sketch, "E2175", {"start": v(68.76, -40.17) * mm, "end": v(68.97, -41.26) * mm});
            skLineSegment(sketch, "E2176", {"start": v(68.97, -41.26) * mm, "end": v(69.35, -43.37) * mm});
            skLineSegment(sketch, "E2177", {"start": v(69.35, -43.37) * mm, "end": v(69.47, -44.07) * mm});
            skLineSegment(sketch, "E2178", {"start": v(69.47, -44.07) * mm, "end": v(69.83, -46.19) * mm});
            skLineSegment(sketch, "E2179", {"start": v(69.83, -46.19) * mm, "end": v(70.09, -47.72) * mm});
            skLineSegment(sketch, "E2180", {"start": v(70.09, -47.72) * mm, "end": v(70.27, -48.9) * mm});
            skLineSegment(sketch, "E2181", {"start": v(70.27, -48.9) * mm, "end": v(70.63, -51.15) * mm});
            skLineSegment(sketch, "E2182", {"start": v(70.63, -51.15) * mm, "end": v(70.87, -52.8) * mm});
            skLineSegment(sketch, "E2183", {"start": v(70.87, -52.8) * mm, "end": v(71.04, -54.1) * mm});
            skLineSegment(sketch, "E2184", {"start": v(71.04, -54.1) * mm, "end": v(71.36, -56.68) * mm});
            skLineSegment(sketch, "E2185", {"start": v(71.36, -56.68) * mm, "end": v(71.46, -57.48) * mm});
            skLineSegment(sketch, "E2186", {"start": v(71.46, -57.48) * mm, "end": v(71.65, -59.19) * mm});
            skLineSegment(sketch, "E2187", {"start": v(71.65, -59.19) * mm, "end": v(71.8, -60.44) * mm});
            skLineSegment(sketch, "E2188", {"start": v(71.8, -60.44) * mm, "end": v(71.91, -61.63) * mm});
            skLineSegment(sketch, "E2189", {"start": v(71.91, -61.63) * mm, "end": v(72.08, -63.27) * mm});
            skLineSegment(sketch, "E2190", {"start": v(72.08, -63.27) * mm, "end": v(72.15, -64.02) * mm});
            skLineSegment(sketch, "E2191", {"start": v(72.15, -64.02) * mm, "end": v(72.33, -66) * mm});
            skLineSegment(sketch, "E2192", {"start": v(72.33, -66) * mm, "end": v(72.41, -66.99) * mm});
            skLineSegment(sketch, "E2193", {"start": v(72.41, -66.99) * mm, "end": v(79.85, -67.14) * mm});
            skLineSegment(sketch, "E2194", {"start": v(79.85, -67.14) * mm, "end": v(79.85, -70.14) * mm});
            skLineSegment(sketch, "E2195", {"start": v(79.85, -70.14) * mm, "end": v(72.8, -70.14) * mm});
            skLineSegment(sketch, "E2196", {"start": v(72.8, -70.14) * mm, "end": v(72.7, -71.04) * mm});
            skLineSegment(sketch, "E2197", {"start": v(72.7, -71.04) * mm, "end": v(72.83, -73.37) * mm});
            skLineSegment(sketch, "E2198", {"start": v(72.83, -73.37) * mm, "end": v(72.93, -75.69) * mm});
            skLineSegment(sketch, "E2199", {"start": v(72.93, -75.69) * mm, "end": v(72.95, -76.2) * mm});
            skLineSegment(sketch, "E2200", {"start": v(72.95, -76.2) * mm, "end": v(73.01, -78) * mm});
            skLineSegment(sketch, "E2201", {"start": v(73.01, -78) * mm, "end": v(73.04, -78.63) * mm});
            skLineSegment(sketch, "E2202", {"start": v(73.04, -78.63) * mm, "end": v(73.08, -80.31) * mm});
            skLineSegment(sketch, "E2203", {"start": v(73.08, -80.31) * mm, "end": v(73.1, -81.03) * mm});
            skLineSegment(sketch, "E2204", {"start": v(73.1, -81.03) * mm, "end": v(73.12, -82.64) * mm});
            skLineSegment(sketch, "E2205", {"start": v(73.12, -82.64) * mm, "end": v(73.13, -83.42) * mm});
            skLineSegment(sketch, "E2206", {"start": v(73.13, -83.42) * mm, "end": v(73.14, -84.98) * mm});
            skLineSegment(sketch, "E2207", {"start": v(73.14, -84.98) * mm, "end": v(73.14, -85.79) * mm});
            skLineSegment(sketch, "E2208", {"start": v(73.14, -85.79) * mm, "end": v(73.13, -87.36) * mm});
            skLineSegment(sketch, "E2209", {"start": v(73.13, -87.36) * mm, "end": v(73.13, -88.16) * mm});
            skLineSegment(sketch, "E2210", {"start": v(73.13, -88.16) * mm, "end": v(73.1, -89.78) * mm});
            skLineSegment(sketch, "E2211", {"start": v(73.1, -89.78) * mm, "end": v(73.1, -90.55) * mm});
            skLineSegment(sketch, "E2212", {"start": v(73.1, -90.55) * mm, "end": v(73.05, -92.26) * mm});
            skLineSegment(sketch, "E2213", {"start": v(73.05, -92.26) * mm, "end": v(73.04, -92.95) * mm});
            skLineSegment(sketch, "E2214", {"start": v(73.04, -92.95) * mm, "end": v(72.97, -94.8) * mm});
            skLineSegment(sketch, "E2215", {"start": v(72.97, -94.8) * mm, "end": v(72.95, -95.38) * mm});
            skLineSegment(sketch, "E2216", {"start": v(72.95, -95.38) * mm, "end": v(72.86, -97.42) * mm});
            skLineSegment(sketch, "E2217", {"start": v(72.86, -97.42) * mm, "end": v(72.72, -100.14) * mm});
            skLineSegment(sketch, "E2218", {"start": v(72.72, -100.14) * mm, "end": v(72.65, -101.29) * mm});
            skLineSegment(sketch, "E2219", {"start": v(72.65, -101.29) * mm, "end": v(79.85, -101.44) * mm});
            skLineSegment(sketch, "E2220", {"start": v(79.85, -101.44) * mm, "end": v(79.85, -104.44) * mm});
            skLineSegment(sketch, "E2221", {"start": v(79.85, -104.44) * mm, "end": v(72.56, -104.44) * mm});
            skLineSegment(sketch, "E2222", {"start": v(72.56, -104.44) * mm, "end": v(72.33, -105.58) * mm});
            skLineSegment(sketch, "E2223", {"start": v(72.33, -105.58) * mm, "end": v(72.28, -106.09) * mm});
            skLineSegment(sketch, "E2224", {"start": v(72.28, -106.09) * mm, "end": v(72.08, -108.31) * mm});
            skLineSegment(sketch, "E2225", {"start": v(72.08, -108.31) * mm, "end": v(71.97, -109.38) * mm});
            skLineSegment(sketch, "E2226", {"start": v(71.97, -109.38) * mm, "end": v(71.8, -111.14) * mm});
            skLineSegment(sketch, "E2227", {"start": v(71.8, -111.14) * mm, "end": v(71.6, -112.91) * mm});
            skLineSegment(sketch, "E2228", {"start": v(71.6, -112.91) * mm, "end": v(71.46, -114.1) * mm});
            skLineSegment(sketch, "E2229", {"start": v(71.46, -114.1) * mm, "end": v(71.14, -116.74) * mm});
            skLineSegment(sketch, "E2230", {"start": v(71.14, -116.74) * mm, "end": v(70.87, -118.78) * mm});
            skLineSegment(sketch, "E2231", {"start": v(70.87, -118.78) * mm, "end": v(70.63, -120.43) * mm});
            skLineSegment(sketch, "E2232", {"start": v(70.63, -120.43) * mm, "end": v(70.52, -121.1) * mm});
            skLineSegment(sketch, "E2233", {"start": v(70.52, -121.1) * mm, "end": v(70.09, -123.86) * mm});
            skLineSegment(sketch, "E2234", {"start": v(70.09, -123.86) * mm, "end": v(69.7, -126.18) * mm});
            skLineSegment(sketch, "E2235", {"start": v(69.7, -126.18) * mm, "end": v(69.47, -127.5) * mm});
            skLineSegment(sketch, "E2236", {"start": v(69.47, -127.5) * mm, "end": v(68.97, -130.32) * mm});
            skLineSegment(sketch, "E2237", {"start": v(68.97, -130.32) * mm, "end": v(68.76, -131.41) * mm});
            skLineSegment(sketch, "E2238", {"start": v(68.76, -131.41) * mm, "end": v(68.6, -132.21) * mm});
            skLineSegment(sketch, "E2239", {"start": v(68.6, -132.21) * mm, "end": v(67.9, -135.59) * mm});
            skLineSegment(sketch, "E2240", {"start": v(67.9, -135.59) * mm, "end": v(77.24, -135.74) * mm});
            skLineSegment(sketch, "E2241", {"start": v(77.24, -135.74) * mm, "end": v(77.24, -138.74) * mm});
            skLineSegment(sketch, "E2242", {"start": v(77.24, -138.74) * mm, "end": v(67.32, -138.74) * mm});
            skLineSegment(sketch, "E2243", {"start": v(67.32, -138.74) * mm, "end": v(66.9, -140.13) * mm});
            skLineSegment(sketch, "E2244", {"start": v(66.9, -140.13) * mm, "end": v(65.65, -145.13) * mm});
            skLineSegment(sketch, "E2245", {"start": v(65.65, -145.13) * mm, "end": v(64.62, -149.1) * mm});
            skLineSegment(sketch, "E2246", {"start": v(64.62, -149.1) * mm, "end": v(64.2, -150.59) * mm});
            skLineSegment(sketch, "E2247", {"start": v(64.2, -150.59) * mm, "end": v(63.04, -154.5) * mm});
            skLineSegment(sketch, "E2248", {"start": v(63.04, -154.5) * mm, "end": v(62.4, -156.65) * mm});
            skLineSegment(sketch, "E2249", {"start": v(62.4, -156.65) * mm, "end": v(62.16, -157.46) * mm});
            skLineSegment(sketch, "E2250", {"start": v(62.16, -157.46) * mm, "end": v(60.17, -163.44) * mm});
            skLineSegment(sketch, "E2251", {"start": v(60.17, -163.44) * mm, "end": v(59.52, -165.36) * mm});
            skLineSegment(sketch, "E2252", {"start": v(59.52, -165.36) * mm, "end": v(58.09, -169.18) * mm});
            skLineSegment(sketch, "E2253", {"start": v(58.09, -169.18) * mm, "end": v(57.83, -169.89) * mm});
            skLineSegment(sketch, "E2254", {"start": v(57.83, -169.89) * mm, "end": v(72.07, -170.04) * mm});
            skLineSegment(sketch, "E2255", {"start": v(72.07, -170.04) * mm, "end": v(72.07, -173.04) * mm});
            skLineSegment(sketch, "E2256", {"start": v(72.07, -173.04) * mm, "end": v(56.75, -173.04) * mm});
            skLineSegment(sketch, "E2257", {"start": v(56.75, -173.04) * mm, "end": v(56.5, -173.5) * mm});
            skLineSegment(sketch, "E2258", {"start": v(56.5, -173.5) * mm, "end": v(56.39, -174.1) * mm});
            skLineSegment(sketch, "E2259", {"start": v(56.39, -174.1) * mm, "end": v(56.33, -174.72) * mm});
            skLineSegment(sketch, "E2260", {"start": v(56.33, -174.72) * mm, "end": v(56.33, -184.15) * mm});
            skLineSegment(sketch, "E2261", {"start": v(56.33, -184.15) * mm, "end": v(56.33, -193.5) * mm});
            skLineSegment(sketch, "E2262", {"start": v(56.33, -193.5) * mm, "end": v(56.33, -194.84) * mm});
            skLineSegment(sketch, "E2263", {"start": v(56.33, -194.84) * mm, "end": v(56.33, -196.32) * mm});
            skLineSegment(sketch, "E2264", {"start": v(56.33, -196.32) * mm, "end": v(56.36, -196.84) * mm});
            skLineSegment(sketch, "E2265", {"start": v(56.36, -196.84) * mm, "end": v(56.45, -197.39) * mm});
            skLineSegment(sketch, "E2266", {"start": v(56.45, -197.39) * mm, "end": v(56.6, -197.91) * mm});
            skLineSegment(sketch, "E2267", {"start": v(56.6, -197.91) * mm, "end": v(56.8, -198.41) * mm});
            skLineSegment(sketch, "E2268", {"start": v(56.8, -198.41) * mm, "end": v(57.07, -198.88) * mm});
            skLineSegment(sketch, "E2269", {"start": v(57.07, -198.88) * mm, "end": v(57.38, -199.31) * mm});
            skLineSegment(sketch, "E2270", {"start": v(57.38, -199.31) * mm, "end": v(57.75, -199.7) * mm});
            skLineSegment(sketch, "E2271", {"start": v(57.75, -199.7) * mm, "end": v(58.15, -200.03) * mm});
            skLineSegment(sketch, "E2272", {"start": v(58.15, -200.03) * mm, "end": v(58.59, -200.3) * mm});
            skLineSegment(sketch, "E2273", {"start": v(58.59, -200.3) * mm, "end": v(59.05, -200.5) * mm});
            skLineSegment(sketch, "E2274", {"start": v(59.05, -200.5) * mm, "end": v(65.26, -202.39) * mm});
            skLineSegment(sketch, "E2275", {"start": v(65.26, -202.39) * mm, "end": v(71.36, -204.19) * mm});
            skLineSegment(sketch, "E2276", {"start": v(71.36, -204.19) * mm, "end": v(71.87, -204.34) * mm});
            skLineSegment(sketch, "E2277", {"start": v(71.87, -204.34) * mm, "end": v(81.01, -204.34) * mm});
            skLineSegment(sketch, "E2278", {"start": v(81.01, -204.34) * mm, "end": v(81.01, -207.34) * mm});
            skLineSegment(sketch, "E2279", {"start": v(81.01, -207.34) * mm, "end": v(79.42, -207.34) * mm});
            skLineSegment(sketch, "E2280", {"start": v(79.42, -207.34) * mm, "end": v(79.27, -220.73) * mm});
            skLineSegment(sketch, "E2281", {"start": v(79.27, -220.73) * mm, "end": v(79.27, -227.61) * mm});
            skLineSegment(sketch, "E2282", {"start": v(79.27, -227.61) * mm, "end": v(62.66, -228.57) * mm});
            skLineSegment(sketch, "E2283", {"start": v(62.66, -228.57) * mm, "end": v(60.12, -228.72) * mm});
            skLineSegment(sketch, "E2284", {"start": v(60.12, -228.72) * mm, "end": v(59.6, -228.78) * mm});
            skLineSegment(sketch, "E2285", {"start": v(59.6, -228.78) * mm, "end": v(59.1, -228.91) * mm});
            skLineSegment(sketch, "E2286", {"start": v(59.1, -228.91) * mm, "end": v(58.61, -229.12) * mm});
            skLineSegment(sketch, "E2287", {"start": v(58.61, -229.12) * mm, "end": v(58.16, -229.4) * mm});
            skLineSegment(sketch, "E2288", {"start": v(58.16, -229.4) * mm, "end": v(57.74, -229.72) * mm});
            skLineSegment(sketch, "E2289", {"start": v(57.74, -229.72) * mm, "end": v(57.37, -230.1) * mm});
            skLineSegment(sketch, "E2290", {"start": v(57.37, -230.1) * mm, "end": v(57.05, -230.53) * mm});
            skLineSegment(sketch, "E2291", {"start": v(57.05, -230.53) * mm, "end": v(56.78, -231) * mm});
            skLineSegment(sketch, "E2292", {"start": v(56.78, -231) * mm, "end": v(56.57, -231.5) * mm});
            skLineSegment(sketch, "E2293", {"start": v(56.57, -231.5) * mm, "end": v(56.43, -232.02) * mm});
            skLineSegment(sketch, "E2294", {"start": v(56.43, -232.02) * mm, "end": v(56.34, -232.56) * mm});
            skLineSegment(sketch, "E2295", {"start": v(56.34, -232.56) * mm, "end": v(56.33, -238.48) * mm});
            skLineSegment(sketch, "E2296", {"start": v(56.33, -238.48) * mm, "end": v(71.8, -238.63) * mm});
            skLineSegment(sketch, "E2297", {"start": v(71.8, -238.63) * mm, "end": v(71.8, -241.63) * mm});
            skLineSegment(sketch, "E2298", {"start": v(71.8, -241.63) * mm, "end": v(56.48, -241.63) * mm});
            skLineSegment(sketch, "E2299", {"start": v(56.48, -241.63) * mm, "end": v(56.36, -242.24) * mm});
            skLineSegment(sketch, "E2300", {"start": v(56.36, -242.24) * mm, "end": v(56.46, -242.77) * mm});
            skLineSegment(sketch, "E2301", {"start": v(56.46, -242.77) * mm, "end": v(56.62, -243.3) * mm});
            skLineSegment(sketch, "E2302", {"start": v(56.62, -243.3) * mm, "end": v(56.85, -243.78) * mm});
            skLineSegment(sketch, "E2303", {"start": v(56.85, -243.78) * mm, "end": v(57.13, -244.24) * mm});
            skLineSegment(sketch, "E2304", {"start": v(57.13, -244.24) * mm, "end": v(57.47, -244.65) * mm});
            skLineSegment(sketch, "E2305", {"start": v(57.47, -244.65) * mm, "end": v(57.86, -245.02) * mm});
            skLineSegment(sketch, "E2306", {"start": v(57.86, -245.02) * mm, "end": v(58.29, -245.33) * mm});
            skLineSegment(sketch, "E2307", {"start": v(58.29, -245.33) * mm, "end": v(58.75, -245.58) * mm});
            skLineSegment(sketch, "E2308", {"start": v(58.75, -245.58) * mm, "end": v(59.24, -245.76) * mm});
            skLineSegment(sketch, "E2309", {"start": v(59.24, -245.76) * mm, "end": v(59.75, -245.87) * mm});
            skLineSegment(sketch, "E2310", {"start": v(59.75, -245.87) * mm, "end": v(65.7, -246.43) * mm});
            skLineSegment(sketch, "E2311", {"start": v(65.7, -246.43) * mm, "end": v(87.27, -248.41) * mm});
            skLineSegment(sketch, "E2312", {"start": v(87.27, -248.41) * mm, "end": v(87.27, -241.87) * mm});
            skLineSegment(sketch, "E2313", {"start": v(87.27, -241.87) * mm, "end": v(87.27, -222.94) * mm});
            skLineSegment(sketch, "E2314", {"start": v(87.27, -222.94) * mm, "end": v(87.27, -222.08) * mm});
            skLineSegment(sketch, "E2315", {"start": v(87.27, -222.08) * mm, "end": v(87.27, -207.65) * mm});
            skLineSegment(sketch, "E2316", {"start": v(87.27, -207.65) * mm, "end": v(87.27, -206.4) * mm});
            skLineSegment(sketch, "E2317", {"start": v(87.27, -206.4) * mm, "end": v(87.27, -195) * mm});
            skLineSegment(sketch, "E2318", {"start": v(87.27, -195) * mm, "end": v(87.27, -193.51) * mm});
            skLineSegment(sketch, "E2319", {"start": v(87.27, -193.51) * mm, "end": v(87.27, -184.3) * mm});
            skLineSegment(sketch, "E2320", {"start": v(87.27, -184.3) * mm, "end": v(87.27, -182.69) * mm});
            skLineSegment(sketch, "E2321", {"start": v(87.27, -182.69) * mm, "end": v(87.27, -175.13) * mm});
            skLineSegment(sketch, "E2322", {"start": v(87.27, -175.13) * mm, "end": v(87.27, -173.43) * mm});
            skLineSegment(sketch, "E2323", {"start": v(87.27, -173.43) * mm, "end": v(87.27, -167.15) * mm});
            skLineSegment(sketch, "E2324", {"start": v(87.27, -167.15) * mm, "end": v(87.27, -165.4) * mm});
            skLineSegment(sketch, "E2325", {"start": v(87.27, -165.4) * mm, "end": v(87.27, -160.11) * mm});
            skLineSegment(sketch, "E2326", {"start": v(87.27, -160.11) * mm, "end": v(87.27, -158.34) * mm});
            skLineSegment(sketch, "E2327", {"start": v(87.27, -158.34) * mm, "end": v(87.27, -153.84) * mm});
            skLineSegment(sketch, "E2328", {"start": v(87.27, -153.84) * mm, "end": v(87.27, -152.06) * mm});
            skLineSegment(sketch, "E2329", {"start": v(87.27, -152.06) * mm, "end": v(87.27, -148.2) * mm});
            skLineSegment(sketch, "E2330", {"start": v(87.27, -148.2) * mm, "end": v(87.27, -146.42) * mm});
            skLineSegment(sketch, "E2331", {"start": v(87.27, -146.42) * mm, "end": v(87.27, -143.08) * mm});
            skLineSegment(sketch, "E2332", {"start": v(87.27, -143.08) * mm, "end": v(87.27, -141.3) * mm});
            skLineSegment(sketch, "E2333", {"start": v(87.27, -141.3) * mm, "end": v(87.27, -138.4) * mm});
            skLineSegment(sketch, "E2334", {"start": v(87.27, -138.4) * mm, "end": v(87.27, -136.63) * mm});
            skLineSegment(sketch, "E2335", {"start": v(87.27, -136.63) * mm, "end": v(87.27, -134.07) * mm});
            skLineSegment(sketch, "E2336", {"start": v(87.27, -134.07) * mm, "end": v(87.27, -132.33) * mm});
            skLineSegment(sketch, "E2337", {"start": v(87.27, -132.33) * mm, "end": v(87.27, -130.06) * mm});
            skLineSegment(sketch, "E2338", {"start": v(87.27, -130.06) * mm, "end": v(87.27, -128.34) * mm});
            skLineSegment(sketch, "E2339", {"start": v(87.27, -128.34) * mm, "end": v(87.27, -126.32) * mm});
            skLineSegment(sketch, "E2340", {"start": v(87.27, -126.32) * mm, "end": v(87.27, -124.61) * mm});
            skLineSegment(sketch, "E2341", {"start": v(87.27, -124.61) * mm, "end": v(87.27, -122.8) * mm});
            skLineSegment(sketch, "E2342", {"start": v(87.27, -122.8) * mm, "end": v(87.27, -121.11) * mm});
            skLineSegment(sketch, "E2343", {"start": v(87.27, -121.11) * mm, "end": v(87.27, -119.48) * mm});
            skLineSegment(sketch, "E2344", {"start": v(87.27, -119.48) * mm, "end": v(87.27, -117.81) * mm});
            skLineSegment(sketch, "E2345", {"start": v(87.27, -117.81) * mm, "end": v(87.27, -116.33) * mm});
            skLineSegment(sketch, "E2346", {"start": v(87.27, -116.33) * mm, "end": v(87.27, -114.68) * mm});
            skLineSegment(sketch, "E2347", {"start": v(87.27, -114.68) * mm, "end": v(87.27, -113.33) * mm});
            skLineSegment(sketch, "E2348", {"start": v(87.27, -113.33) * mm, "end": v(87.27, -111.69) * mm});
            skLineSegment(sketch, "E2349", {"start": v(87.27, -111.69) * mm, "end": v(87.27, -110.45) * mm});
            skLineSegment(sketch, "E2350", {"start": v(87.27, -110.45) * mm, "end": v(87.27, -108.82) * mm});
            skLineSegment(sketch, "E2351", {"start": v(87.27, -108.82) * mm, "end": v(87.27, -107.67) * mm});
            skLineSegment(sketch, "E2352", {"start": v(87.27, -107.67) * mm, "end": v(87.27, -106.06) * mm});
            skLineSegment(sketch, "E2353", {"start": v(87.27, -106.06) * mm, "end": v(87.27, -105) * mm});
            skLineSegment(sketch, "E2354", {"start": v(87.27, -105) * mm, "end": v(87.27, -103.4) * mm});
            skLineSegment(sketch, "E2355", {"start": v(87.27, -103.4) * mm, "end": v(87.27, -102.39) * mm});
            skLineSegment(sketch, "E2356", {"start": v(87.27, -102.39) * mm, "end": v(87.27, -100.8) * mm});
            skLineSegment(sketch, "E2357", {"start": v(87.27, -100.8) * mm, "end": v(87.27, -99.85) * mm});
            skLineSegment(sketch, "E2358", {"start": v(87.27, -99.85) * mm, "end": v(87.27, -98.27) * mm});
            skLineSegment(sketch, "E2359", {"start": v(87.27, -98.27) * mm, "end": v(87.27, -97.36) * mm});
            skLineSegment(sketch, "E2360", {"start": v(87.27, -97.36) * mm, "end": v(87.27, -95.8) * mm});
            skLineSegment(sketch, "E2361", {"start": v(87.27, -95.8) * mm, "end": v(87.27, -94.92) * mm});
            skLineSegment(sketch, "E2362", {"start": v(87.27, -94.92) * mm, "end": v(87.27, -93.35) * mm});
            skLineSegment(sketch, "E2363", {"start": v(87.27, -93.35) * mm, "end": v(87.27, -92.5) * mm});
            skLineSegment(sketch, "E2364", {"start": v(87.27, -92.5) * mm, "end": v(87.27, -90.95) * mm});
            skLineSegment(sketch, "E2365", {"start": v(87.27, -90.95) * mm, "end": v(87.27, -90.12) * mm});
            skLineSegment(sketch, "E2366", {"start": v(87.27, -90.12) * mm, "end": v(87.27, -88.57) * mm});
            skLineSegment(sketch, "E2367", {"start": v(87.27, -88.57) * mm, "end": v(87.27, -87.75) * mm});
            skLineSegment(sketch, "E2368", {"start": v(87.27, -87.75) * mm, "end": v(87.27, -86.2) * mm});
            skLineSegment(sketch, "E2369", {"start": v(87.27, -86.2) * mm, "end": v(87.27, -85.38) * mm});
            skLineSegment(sketch, "E2370", {"start": v(87.27, -85.38) * mm, "end": v(87.27, -84.57) * mm});
            skLineSegment(sketch, "E2371", {"start": v(87.27, -84.57) * mm, "end": v(87.27, -83.01) * mm});
            skLineSegment(sketch, "E2372", {"start": v(87.27, -83.01) * mm, "end": v(87.27, -82.19) * mm});
            skLineSegment(sketch, "E2373", {"start": v(87.27, -82.19) * mm, "end": v(87.27, -80.63) * mm});
            skLineSegment(sketch, "E2374", {"start": v(87.27, -80.63) * mm, "end": v(87.27, -79.8) * mm});
            skLineSegment(sketch, "E2375", {"start": v(87.27, -79.8) * mm, "end": v(87.27, -78.22) * mm});
            skLineSegment(sketch, "E2376", {"start": v(87.27, -78.22) * mm, "end": v(87.27, -77.36) * mm});
            skLineSegment(sketch, "E2377", {"start": v(87.27, -77.36) * mm, "end": v(87.27, -75.79) * mm});
            skLineSegment(sketch, "E2378", {"start": v(87.27, -75.79) * mm, "end": v(87.27, -74.9) * mm});
            skLineSegment(sketch, "E2379", {"start": v(87.27, -74.9) * mm, "end": v(87.27, -73.3) * mm});
            skLineSegment(sketch, "E2380", {"start": v(87.27, -73.3) * mm, "end": v(87.27, -72.38) * mm});
            skLineSegment(sketch, "E2381", {"start": v(87.27, -72.38) * mm, "end": v(87.27, -70.78) * mm});
            skLineSegment(sketch, "E2382", {"start": v(87.27, -70.78) * mm, "end": v(87.27, -69.8) * mm});
            skLineSegment(sketch, "E2383", {"start": v(87.27, -69.8) * mm, "end": v(87.27, -68.19) * mm});
            skLineSegment(sketch, "E2384", {"start": v(87.27, -68.19) * mm, "end": v(87.27, -67.14) * mm});
            skLineSegment(sketch, "E2385", {"start": v(87.27, -67.14) * mm, "end": v(87.27, -65.52) * mm});
            skLineSegment(sketch, "E2386", {"start": v(87.27, -65.52) * mm, "end": v(87.27, -64.4) * mm});
            skLineSegment(sketch, "E2387", {"start": v(87.27, -64.4) * mm, "end": v(87.27, -62.76) * mm});
            skLineSegment(sketch, "E2388", {"start": v(87.27, -62.76) * mm, "end": v(87.27, -61.55) * mm});
            skLineSegment(sketch, "E2389", {"start": v(87.27, -61.55) * mm, "end": v(87.27, -59.89) * mm});
            skLineSegment(sketch, "E2390", {"start": v(87.27, -59.89) * mm, "end": v(87.27, -58.57) * mm});
            skLineSegment(sketch, "E2391", {"start": v(87.27, -58.57) * mm, "end": v(87.27, -56.9) * mm});
            skLineSegment(sketch, "E2392", {"start": v(87.27, -56.9) * mm, "end": v(87.27, -55.46) * mm});
            skLineSegment(sketch, "E2393", {"start": v(87.27, -55.46) * mm, "end": v(87.27, -53.77) * mm});
            skLineSegment(sketch, "E2394", {"start": v(87.27, -53.77) * mm, "end": v(87.27, -52.18) * mm});
            skLineSegment(sketch, "E2395", {"start": v(87.27, -52.18) * mm, "end": v(87.27, -50.46) * mm});
            skLineSegment(sketch, "E2396", {"start": v(87.27, -50.46) * mm, "end": v(87.27, -48.7) * mm});
            skLineSegment(sketch, "E2397", {"start": v(87.27, -48.7) * mm, "end": v(87.27, -46.97) * mm});
            skLineSegment(sketch, "E2398", {"start": v(87.27, -46.97) * mm, "end": v(87.27, -45) * mm});
            skLineSegment(sketch, "E2399", {"start": v(87.27, -45) * mm, "end": v(87.27, -43.24) * mm});
            skLineSegment(sketch, "E2400", {"start": v(87.27, -43.24) * mm, "end": v(87.27, -41.03) * mm});
            skLineSegment(sketch, "E2401", {"start": v(87.27, -41.03) * mm, "end": v(87.27, -39.25) * mm});
            skLineSegment(sketch, "E2402", {"start": v(87.27, -39.25) * mm, "end": v(87.27, -36.75) * mm});
            skLineSegment(sketch, "E2403", {"start": v(87.27, -36.75) * mm, "end": v(87.27, -34.95) * mm});
            skLineSegment(sketch, "E2404", {"start": v(87.27, -34.95) * mm, "end": v(87.27, -32.1) * mm});
            skLineSegment(sketch, "E2405", {"start": v(87.27, -32.1) * mm, "end": v(87.27, -30.27) * mm});
            skLineSegment(sketch, "E2406", {"start": v(87.27, -30.27) * mm, "end": v(87.27, -27) * mm});
            skLineSegment(sketch, "E2407", {"start": v(87.27, -27) * mm, "end": v(87.27, -25.16) * mm});
            skLineSegment(sketch, "E2408", {"start": v(87.27, -25.16) * mm, "end": v(87.27, -21.37) * mm});
            skLineSegment(sketch, "E2409", {"start": v(87.27, -21.37) * mm, "end": v(87.27, -19.52) * mm});
            skLineSegment(sketch, "E2410", {"start": v(87.27, -19.52) * mm, "end": v(87.27, -15.08) * mm});
            skLineSegment(sketch, "E2411", {"start": v(87.27, -15.08) * mm, "end": v(87.27, -13.24) * mm});
            skLineSegment(sketch, "E2412", {"start": v(87.27, -13.24) * mm, "end": v(87.27, -8) * mm});
            skLineSegment(sketch, "E2413", {"start": v(87.27, -8) * mm, "end": v(87.27, -6.18) * mm});
            skLineSegment(sketch, "E2414", {"start": v(87.27, -6.18) * mm, "end": v(87.27, 0.07) * mm});
            skLineSegment(sketch, "E2415", {"start": v(87.27, 0.07) * mm, "end": v(87.27, 1.85) * mm});
            skLineSegment(sketch, "E2416", {"start": v(87.27, 1.85) * mm, "end": v(87.27, 9.41) * mm});
            skLineSegment(sketch, "E2417", {"start": v(87.27, 9.41) * mm, "end": v(87.27, 11.1) * mm});
            skLineSegment(sketch, "E2418", {"start": v(87.27, 11.1) * mm, "end": v(87.27, 20.38) * mm});
            skLineSegment(sketch, "E2419", {"start": v(87.27, 20.38) * mm, "end": v(87.27, 21.94) * mm});
            skLineSegment(sketch, "E2420", {"start": v(87.27, 21.94) * mm, "end": v(87.27, 33.5) * mm});
            skLineSegment(sketch, "E2421", {"start": v(87.27, 33.5) * mm, "end": v(87.27, 34.83) * mm});
            skLineSegment(sketch, "E2422", {"start": v(87.27, 34.83) * mm, "end": v(87.27, 49.57) * mm});
            skLineSegment(sketch, "E2423", {"start": v(87.27, 49.57) * mm, "end": v(87.27, 50.5) * mm});
            skLineSegment(sketch, "E2424", {"start": v(87.27, 50.5) * mm, "end": v(87.27, 69.77) * mm});
            skLineSegment(sketch, "E2425", {"start": v(87.27, 221.47) * mm, "end": v(87.27, 227.8) * mm});
            skLineSegment(sketch, "E2426", {"start": v(87.27, 227.8) * mm, "end": v(73.3, 224.92) * mm});
            skLineSegment(sketch, "E2427", {"start": v(73.3, 224.92) * mm, "end": v(59.98, 222.13) * mm});
            skLineSegment(sketch, "E2428", {"start": v(59.98, 222.13) * mm, "end": v(59.48, 221.94) * mm});
            skLineSegment(sketch, "E2429", {"start": v(59.48, 221.94) * mm, "end": v(58.96, 221.58) * mm});
            skLineSegment(sketch, "E2430", {"start": v(58.96, 221.58) * mm, "end": v(58.48, 221.05) * mm});
            skLineSegment(sketch, "E2431", {"start": v(58.48, 221.05) * mm, "end": v(58.18, 220.6) * mm});
            skLineSegment(sketch, "E2432", {"start": v(58.18, 220.6) * mm, "end": v(57.9, 220.07) * mm});
            skLineSegment(sketch, "E2433", {"start": v(57.9, 220.07) * mm, "end": v(57.62, 219.48) * mm});
            skLineSegment(sketch, "E2434", {"start": v(57.62, 219.48) * mm, "end": v(57.38, 218.84) * mm});
            skLineSegment(sketch, "E2435", {"start": v(57.38, 218.84) * mm, "end": v(57.21, 218.34) * mm});
            skLineSegment(sketch, "E2436", {"start": v(57.21, 218.34) * mm, "end": v(57.05, 217.77) * mm});
            skLineSegment(sketch, "E2437", {"start": v(57.05, 217.77) * mm, "end": v(56.9, 217.15) * mm});
            skLineSegment(sketch, "E2438", {"start": v(56.9, 217.15) * mm, "end": v(56.78, 216.6) * mm});
            skLineSegment(sketch, "E2439", {"start": v(56.78, 216.6) * mm, "end": v(56.64, 215.85) * mm});
            skLineSegment(sketch, "E2440", {"start": v(56.64, 215.85) * mm, "end": v(56.57, 215.35) * mm});
            skLineSegment(sketch, "E2441", {"start": v(56.57, 215.35) * mm, "end": v(56.47, 214.55) * mm});
            skLineSegment(sketch, "E2442", {"start": v(56.47, 214.55) * mm, "end": v(56.42, 213.98) * mm});
            skLineSegment(sketch, "E2443", {"start": v(56.42, 213.98) * mm, "end": v(56.38, 213.4) * mm});
            skLineSegment(sketch, "E2444", {"start": v(56.38, 213.4) * mm, "end": v(56.36, 212.87) * mm});
            skLineSegment(sketch, "E2445", {"start": v(56.36, 212.87) * mm, "end": v(56.34, 212.32) * mm});
            skLineSegment(sketch, "E2446", {"start": v(56.34, 212.32) * mm, "end": v(56.33, 211.78) * mm});
            skLineSegment(sketch, "E2447", {"start": v(56.33, 211.78) * mm, "end": v(56.33, 208.93) * mm});
            skLineSegment(sketch, "E2448", {"start": v(56.33, 208.93) * mm, "end": v(56.33, 208.3) * mm});
            skLineSegment(sketch, "E2449", {"start": v(56.33, 208.3) * mm, "end": v(56.33, 207) * mm});
            skLineSegment(sketch, "E2450", {"start": v(56.33, 207) * mm, "end": v(71.8, 206.86) * mm});
            skLineSegment(sketch, "E2451", {"start": v(71.8, 206.86) * mm, "end": v(71.8, 203.86) * mm});
            skLineSegment(sketch, "E2452", {"start": v(71.8, 203.86) * mm, "end": v(56.48, 203.86) * mm});
            skLineSegment(sketch, "E2453", {"start": v(56.48, 203.86) * mm, "end": v(56.33, 202.36) * mm});
            skLineSegment(sketch, "E2454", {"start": v(56.33, 202.36) * mm, "end": v(56.33, 199.17) * mm});
            skLineSegment(sketch, "E2455", {"start": v(56.33, 199.17) * mm, "end": v(56.33, 196.38) * mm});
            skLineSegment(sketch, "E2456", {"start": v(56.33, 196.38) * mm, "end": v(56.33, 194.16) * mm});
            skLineSegment(sketch, "E2457", {"start": v(56.33, 194.16) * mm, "end": v(56.33, 190.38) * mm});
            skLineSegment(sketch, "E2458", {"start": v(56.33, 190.38) * mm, "end": v(56.33, 189.05) * mm});
            skLineSegment(sketch, "E2459", {"start": v(56.33, 189.05) * mm, "end": v(56.33, 184.34) * mm});
            skLineSegment(sketch, "E2460", {"start": v(56.33, 184.34) * mm, "end": v(56.33, 183.82) * mm});
            skLineSegment(sketch, "E2461", {"start": v(56.33, 183.82) * mm, "end": v(56.33, 179.82) * mm});
            skLineSegment(sketch, "E2462", {"start": v(56.33, 179.82) * mm, "end": v(56.33, 178.94) * mm});
            skLineSegment(sketch, "E2463", {"start": v(56.33, 178.94) * mm, "end": v(56.34, 178.25) * mm});
            skLineSegment(sketch, "E2464", {"start": v(56.34, 178.25) * mm, "end": v(56.34, 177.72) * mm});
            skLineSegment(sketch, "E2465", {"start": v(56.34, 177.72) * mm, "end": v(56.36, 176.46) * mm});
            skLineSegment(sketch, "E2466", {"start": v(56.36, 176.46) * mm, "end": v(56.39, 175.2) * mm});
            skLineSegment(sketch, "E2467", {"start": v(56.39, 175.2) * mm, "end": v(56.4, 174.42) * mm});
            skLineSegment(sketch, "E2468", {"start": v(56.4, 174.42) * mm, "end": v(56.46, 172.86) * mm});
            skLineSegment(sketch, "E2469", {"start": v(56.46, 172.86) * mm, "end": v(71.87, 172.56) * mm});
            skLineSegment(sketch, "E2470", {"start": v(71.87, 172.56) * mm, "end": v(71.87, 169.56) * mm});
            skLineSegment(sketch, "E2471", {"start": v(71.87, 169.56) * mm, "end": v(56.72, 169.56) * mm});
            skLineSegment(sketch, "E2472", {"start": v(56.72, 169.56) * mm, "end": v(56.6, 168.6) * mm});
            skLineSegment(sketch, "E2473", {"start": v(56.6, 168.6) * mm, "end": v(56.63, 167.89) * mm});
            skLineSegment(sketch, "E2474", {"start": v(56.63, 167.89) * mm, "end": v(56.7, 166.35) * mm});
            skLineSegment(sketch, "E2475", {"start": v(56.7, 166.35) * mm, "end": v(56.77, 163.76) * mm});
            skLineSegment(sketch, "E2476", {"start": v(56.77, 163.76) * mm, "end": v(56.83, 162.07) * mm});
            skLineSegment(sketch, "E2477", {"start": v(56.83, 162.07) * mm, "end": v(56.86, 161.15) * mm});
            skLineSegment(sketch, "E2478", {"start": v(56.86, 161.15) * mm, "end": v(56.9, 159.95) * mm});
            skLineSegment(sketch, "E2479", {"start": v(56.9, 159.95) * mm, "end": v(56.95, 155.95) * mm});
            skLineSegment(sketch, "E2480", {"start": v(56.95, 155.95) * mm, "end": v(56.97, 153.9) * mm});
            skLineSegment(sketch, "E2481", {"start": v(56.97, 153.9) * mm, "end": v(56.96, 153) * mm});
            skLineSegment(sketch, "E2482", {"start": v(56.96, 153) * mm, "end": v(56.95, 151.87) * mm});
            skLineSegment(sketch, "E2483", {"start": v(56.95, 151.87) * mm, "end": v(56.92, 149.64) * mm});
            skLineSegment(sketch, "E2484", {"start": v(56.92, 149.64) * mm, "end": v(56.9, 147.87) * mm});
            skLineSegment(sketch, "E2485", {"start": v(56.9, 147.87) * mm, "end": v(56.87, 147.02) * mm});
            skLineSegment(sketch, "E2486", {"start": v(56.87, 147.02) * mm, "end": v(56.8, 145.2) * mm});
            skLineSegment(sketch, "E2487", {"start": v(56.8, 145.2) * mm, "end": v(56.77, 144.06) * mm});
            skLineSegment(sketch, "E2488", {"start": v(56.77, 144.06) * mm, "end": v(56.75, 143.37) * mm});
            skLineSegment(sketch, "E2489", {"start": v(56.75, 143.37) * mm, "end": v(56.7, 141.81) * mm});
            skLineSegment(sketch, "E2490", {"start": v(56.7, 141.81) * mm, "end": v(56.64, 140.33) * mm});
            skLineSegment(sketch, "E2491", {"start": v(56.64, 140.33) * mm, "end": v(56.6, 139.03) * mm});
            skLineSegment(sketch, "E2492", {"start": v(56.6, 139.03) * mm, "end": v(56.57, 138.4) * mm});
            skLineSegment(sketch, "E2493", {"start": v(56.57, 138.4) * mm, "end": v(71.87, 138.26) * mm});
            skLineSegment(sketch, "E2494", {"start": v(71.87, 138.26) * mm, "end": v(71.87, 135.26) * mm});
            skLineSegment(sketch, "E2495", {"start": v(71.87, 135.26) * mm, "end": v(56.61, 135.26) * mm});
            skLineSegment(sketch, "E2496", {"start": v(56.61, 135.26) * mm, "end": v(56.43, 134.18) * mm});
            skLineSegment(sketch, "E2497", {"start": v(56.43, 134.18) * mm, "end": v(56.4, 133.14) * mm});
            skLineSegment(sketch, "E2498", {"start": v(56.4, 133.14) * mm, "end": v(56.39, 132.62) * mm});
            skLineSegment(sketch, "E2499", {"start": v(56.39, 132.62) * mm, "end": v(56.38, 132.1) * mm});
            skLineSegment(sketch, "E2500", {"start": v(56.38, 132.1) * mm, "end": v(56.36, 131.36) * mm});
            skLineSegment(sketch, "E2501", {"start": v(56.36, 131.36) * mm, "end": v(56.34, 130.1) * mm});
            skLineSegment(sketch, "E2502", {"start": v(56.34, 130.1) * mm, "end": v(56.34, 129.57) * mm});
            skLineSegment(sketch, "E2503", {"start": v(56.34, 129.57) * mm, "end": v(56.33, 128.98) * mm});
            skLineSegment(sketch, "E2504", {"start": v(56.33, 128.98) * mm, "end": v(56.33, 128.2) * mm});
            skLineSegment(sketch, "E2505", {"start": v(56.33, 128.2) * mm, "end": v(56.33, 123.47) * mm});
            skLineSegment(sketch, "E2506", {"start": v(56.33, 123.47) * mm, "end": v(56.33, 122.79) * mm});
            skLineSegment(sketch, "E2507", {"start": v(56.33, 122.79) * mm, "end": v(56.33, 117.44) * mm});
            skLineSegment(sketch, "E2508", {"start": v(56.33, 117.44) * mm, "end": v(56.33, 115.6) * mm});
            skLineSegment(sketch, "E2509", {"start": v(56.33, 115.6) * mm, "end": v(56.33, 111.43) * mm});
            skLineSegment(sketch, "E2510", {"start": v(56.33, 111.43) * mm, "end": v(56.33, 108.18) * mm});
            skLineSegment(sketch, "E2511", {"start": v(56.33, 108.18) * mm, "end": v(56.33, 105.46) * mm});
            skLineSegment(sketch, "E2512", {"start": v(56.33, 105.46) * mm, "end": v(56.33, 104.1) * mm});
            skLineSegment(sketch, "E2513", {"start": v(56.33, 104.1) * mm, "end": v(71.8, 103.96) * mm});
            skLineSegment(sketch, "E2514", {"start": v(71.8, 103.96) * mm, "end": v(71.8, 100.96) * mm});
            skLineSegment(sketch, "E2515", {"start": v(71.8, 100.96) * mm, "end": v(56.48, 100.96) * mm});
            skLineSegment(sketch, "E2516", {"start": v(56.48, 100.96) * mm, "end": v(56.33, 99.5) * mm});
            skLineSegment(sketch, "E2517", {"start": v(56.33, 99.5) * mm, "end": v(56.33, 96.33) * mm});
            skLineSegment(sketch, "E2518", {"start": v(56.33, 96.33) * mm, "end": v(56.33, 95.64) * mm});
            skLineSegment(sketch, "E2519", {"start": v(56.33, 95.64) * mm, "end": v(56.36, 94.82) * mm});
            skLineSegment(sketch, "E2520", {"start": v(56.36, 94.82) * mm, "end": v(56.4, 94.25) * mm});
            skLineSegment(sketch, "E2521", {"start": v(56.4, 94.25) * mm, "end": v(56.46, 93.35) * mm});
            skLineSegment(sketch, "E2522", {"start": v(56.46, 93.35) * mm, "end": v(56.56, 92.52) * mm});
            skLineSegment(sketch, "E2523", {"start": v(56.56, 92.52) * mm, "end": v(56.68, 91.72) * mm});
            skLineSegment(sketch, "E2524", {"start": v(56.68, 91.72) * mm, "end": v(56.78, 91.22) * mm});
            skLineSegment(sketch, "E2525", {"start": v(56.78, 91.22) * mm, "end": v(56.92, 90.58) * mm});
            skLineSegment(sketch, "E2526", {"start": v(56.92, 90.58) * mm, "end": v(57.05, 90.05) * mm});
            skLineSegment(sketch, "E2527", {"start": v(57.05, 90.05) * mm, "end": v(57.2, 89.52) * mm});
            skLineSegment(sketch, "E2528", {"start": v(57.2, 89.52) * mm, "end": v(57.38, 88.98) * mm});
            skLineSegment(sketch, "E2529", {"start": v(57.38, 88.98) * mm, "end": v(57.62, 88.33) * mm});
            skLineSegment(sketch, "E2530", {"start": v(57.62, 88.33) * mm, "end": v(57.9, 87.75) * mm});
            skLineSegment(sketch, "E2531", {"start": v(57.9, 87.75) * mm, "end": v(58.18, 87.22) * mm});
            skLineSegment(sketch, "E2532", {"start": v(58.18, 87.22) * mm, "end": v(58.48, 86.77) * mm});
            skLineSegment(sketch, "E2533", {"start": v(58.48, 86.77) * mm, "end": v(58.95, 86.24) * mm});
            skLineSegment(sketch, "E2534", {"start": v(58.95, 86.24) * mm, "end": v(59.45, 85.9) * mm});
            skLineSegment(sketch, "E2535", {"start": v(59.45, 85.9) * mm, "end": v(59.98, 85.69) * mm});
            skLineSegment(sketch, "E2536", {"start": v(59.98, 85.69) * mm, "end": v(67.15, 84.2) * mm});
            skLineSegment(sketch, "E2537", {"start": v(67.15, 84.2) * mm, "end": v(87.27, 80) * mm});
            skLineSegment(sketch, "E2538", {"start": v(87.27, 80) * mm, "end": v(87.27, 86.31) * mm});
            skLineSegment(sketch, "E2539", {"start": v(87.27, 86.31) * mm, "end": v(87.27, 94.13) * mm});
            skLineSegment(sketch, "E2540", {"start": v(87.27, 94.13) * mm, "end": v(87.27, 101.7) * mm});
            skLineSegment(sketch, "E2541", {"start": v(87.27, 101.7) * mm, "end": v(87.27, 109.05) * mm});
            skLineSegment(sketch, "E2542", {"start": v(87.27, 109.05) * mm, "end": v(87.27, 116.22) * mm});
            skLineSegment(sketch, "E2543", {"start": v(87.27, 116.22) * mm, "end": v(87.27, 123.24) * mm});
            skLineSegment(sketch, "E2544", {"start": v(87.27, 123.24) * mm, "end": v(87.27, 130.15) * mm});
            skLineSegment(sketch, "E2545", {"start": v(87.27, 130.15) * mm, "end": v(87.27, 136.97) * mm});
            skLineSegment(sketch, "E2546", {"start": v(87.27, 136.97) * mm, "end": v(87.27, 143.72) * mm});
            skLineSegment(sketch, "E2547", {"start": v(87.27, 143.72) * mm, "end": v(87.27, 150.44) * mm});
            skLineSegment(sketch, "E2548", {"start": v(87.27, 150.44) * mm, "end": v(87.27, 157.15) * mm});
            skLineSegment(sketch, "E2549", {"start": v(87.27, 157.15) * mm, "end": v(87.27, 163.66) * mm});
            skLineSegment(sketch, "E2550", {"start": v(87.27, 163.66) * mm, "end": v(87.27, 170.43) * mm});
            skLineSegment(sketch, "E2551", {"start": v(87.27, 170.43) * mm, "end": v(87.27, 177.27) * mm});
            skLineSegment(sketch, "E2552", {"start": v(87.27, 177.27) * mm, "end": v(87.27, 184.2) * mm});
            skLineSegment(sketch, "E2553", {"start": v(87.27, 184.2) * mm, "end": v(87.27, 191.26) * mm});
            skLineSegment(sketch, "E2554", {"start": v(87.27, 191.26) * mm, "end": v(87.27, 198.48) * mm});
            skLineSegment(sketch, "E2555", {"start": v(87.27, 198.48) * mm, "end": v(87.27, 205.9) * mm});
            skLineSegment(sketch, "E2556", {"start": v(87.27, 205.9) * mm, "end": v(87.27, 213.53) * mm});
            skLineSegment(sketch, "E2557", {"start": v(87.27, 213.53) * mm, "end": v(87.27, 221.43) * mm});
            skLineSegment(sketch, "E2558", {"start": v(87.27, 221.43) * mm, "end": v(87.27, 221.47) * mm});
            skLineSegment(sketch, "E2559", {"start": v(119.97, -55.98) * mm, "end": v(119.97, -54.02) * mm});
            skLineSegment(sketch, "E2560", {"start": v(119.97, -54.02) * mm, "end": v(119.97, -52.14) * mm});
            skLineSegment(sketch, "E2561", {"start": v(119.97, -52.14) * mm, "end": v(119.97, -50.3) * mm});
            skLineSegment(sketch, "E2562", {"start": v(119.97, -50.3) * mm, "end": v(119.97, -48.49) * mm});
            skLineSegment(sketch, "E2563", {"start": v(119.97, -48.49) * mm, "end": v(119.97, -46.71) * mm});
            skLineSegment(sketch, "E2564", {"start": v(119.97, -46.71) * mm, "end": v(119.97, -44.98) * mm});
            skLineSegment(sketch, "E2565", {"start": v(119.97, -44.98) * mm, "end": v(119.97, -43.29) * mm});
            skLineSegment(sketch, "E2566", {"start": v(119.97, -43.29) * mm, "end": v(119.97, -41.65) * mm});
            skLineSegment(sketch, "E2567", {"start": v(119.97, -41.65) * mm, "end": v(119.97, -40.06) * mm});
            skLineSegment(sketch, "E2568", {"start": v(119.97, -40.06) * mm, "end": v(119.97, -38.52) * mm});
            skLineSegment(sketch, "E2569", {"start": v(119.97, -38.52) * mm, "end": v(119.97, -37.05) * mm});
            skLineSegment(sketch, "E2570", {"start": v(119.97, -37.05) * mm, "end": v(119.97, 83.35) * mm});
            skLineSegment(sketch, "E2571", {"start": v(119.97, 83.35) * mm, "end": v(94.7, 81.1) * mm});
            skLineSegment(sketch, "E2572", {"start": v(94.7, 81.1) * mm, "end": v(94.05, 81.05) * mm});
            skLineSegment(sketch, "E2573", {"start": v(94.05, 81.05) * mm, "end": v(93.54, 80.97) * mm});
            skLineSegment(sketch, "E2574", {"start": v(93.54, 80.97) * mm, "end": v(93.05, 80.82) * mm});
            skLineSegment(sketch, "E2575", {"start": v(93.05, 80.82) * mm, "end": v(92.57, 80.61) * mm});
            skLineSegment(sketch, "E2576", {"start": v(92.57, 80.61) * mm, "end": v(92.13, 80.34) * mm});
            skLineSegment(sketch, "E2577", {"start": v(92.13, 80.34) * mm, "end": v(91.73, 80.02) * mm});
            skLineSegment(sketch, "E2578", {"start": v(91.73, 80.02) * mm, "end": v(91.37, 79.64) * mm});
            skLineSegment(sketch, "E2579", {"start": v(91.37, 79.64) * mm, "end": v(91.07, 79.22) * mm});
            skLineSegment(sketch, "E2580", {"start": v(91.07, 79.22) * mm, "end": v(90.82, 78.77) * mm});
            skLineSegment(sketch, "E2581", {"start": v(90.82, 78.77) * mm, "end": v(90.63, 78.28) * mm});
            skLineSegment(sketch, "E2582", {"start": v(90.63, 78.28) * mm, "end": v(90.51, 77.77) * mm});
            skLineSegment(sketch, "E2583", {"start": v(90.51, 77.77) * mm, "end": v(90.45, 77.25) * mm});
            skLineSegment(sketch, "E2584", {"start": v(90.45, 77.25) * mm, "end": v(90.45, 73.47) * mm});
            skLineSegment(sketch, "E2585", {"start": v(90.45, 73.47) * mm, "end": v(105.2, 73.32) * mm});
            skLineSegment(sketch, "E2586", {"start": v(105.2, 73.32) * mm, "end": v(105.2, 70.32) * mm});
            skLineSegment(sketch, "E2587", {"start": v(105.2, 70.32) * mm, "end": v(90.6, 70.32) * mm});
            skLineSegment(sketch, "E2588", {"start": v(90.6, 70.32) * mm, "end": v(90.45, 69.35) * mm});
            skLineSegment(sketch, "E2589", {"start": v(90.45, 69.35) * mm, "end": v(90.45, 68.5) * mm});
            skLineSegment(sketch, "E2590", {"start": v(90.45, 68.5) * mm, "end": v(90.48, 67.98) * mm});
            skLineSegment(sketch, "E2591", {"start": v(90.48, 67.98) * mm, "end": v(90.58, 67.48) * mm});
            skLineSegment(sketch, "E2592", {"start": v(90.58, 67.48) * mm, "end": v(90.74, 66.99) * mm});
            skLineSegment(sketch, "E2593", {"start": v(90.74, 66.99) * mm, "end": v(90.96, 66.51) * mm});
            skLineSegment(sketch, "E2594", {"start": v(90.96, 66.51) * mm, "end": v(91.24, 66.07) * mm});
            skLineSegment(sketch, "E2595", {"start": v(91.24, 66.07) * mm, "end": v(91.57, 65.67) * mm});
            skLineSegment(sketch, "E2596", {"start": v(91.57, 65.67) * mm, "end": v(91.95, 65.3) * mm});
            skLineSegment(sketch, "E2597", {"start": v(91.95, 65.3) * mm, "end": v(92.37, 65) * mm});
            skLineSegment(sketch, "E2598", {"start": v(92.37, 65) * mm, "end": v(92.82, 64.75) * mm});
            skLineSegment(sketch, "E2599", {"start": v(92.82, 64.75) * mm, "end": v(93.3, 64.56) * mm});
            skLineSegment(sketch, "E2600", {"start": v(93.3, 64.56) * mm, "end": v(93.8, 64.43) * mm});
            skLineSegment(sketch, "E2601", {"start": v(93.8, 64.43) * mm, "end": v(94.31, 64.37) * mm});
            skLineSegment(sketch, "E2602", {"start": v(94.31, 64.37) * mm, "end": v(111.97, 63.42) * mm});
            skLineSegment(sketch, "E2603", {"start": v(111.97, 63.42) * mm, "end": v(111.97, 57.53) * mm});
            skLineSegment(sketch, "E2604", {"start": v(111.97, 57.53) * mm, "end": v(111.97, 47.88) * mm});
            skLineSegment(sketch, "E2605", {"start": v(111.97, 47.88) * mm, "end": v(111.97, 45.34) * mm});
            skLineSegment(sketch, "E2606", {"start": v(111.97, 45.34) * mm, "end": v(111.97, 41.62) * mm});
            skLineSegment(sketch, "E2607", {"start": v(111.97, 41.62) * mm, "end": v(108.24, 40.55) * mm});
            skLineSegment(sketch, "E2608", {"start": v(108.24, 40.55) * mm, "end": v(103.4, 39.17) * mm});
            skLineSegment(sketch, "E2609", {"start": v(103.4, 39.17) * mm, "end": v(107.8, 39.02) * mm});
            skLineSegment(sketch, "E2610", {"start": v(107.8, 39.02) * mm, "end": v(107.8, 36.02) * mm});
            skLineSegment(sketch, "E2611", {"start": v(107.8, 36.02) * mm, "end": v(92.64, 36.02) * mm});
            skLineSegment(sketch, "E2612", {"start": v(92.64, 36.02) * mm, "end": v(92.1, 35.68) * mm});
            skLineSegment(sketch, "E2613", {"start": v(92.1, 35.68) * mm, "end": v(91.7, 35.35) * mm});
            skLineSegment(sketch, "E2614", {"start": v(91.7, 35.35) * mm, "end": v(91.36, 34.96) * mm});
            skLineSegment(sketch, "E2615", {"start": v(91.36, 34.96) * mm, "end": v(91.06, 34.53) * mm});
            skLineSegment(sketch, "E2616", {"start": v(91.06, 34.53) * mm, "end": v(90.82, 34.07) * mm});
            skLineSegment(sketch, "E2617", {"start": v(90.82, 34.07) * mm, "end": v(90.64, 33.57) * mm});
            skLineSegment(sketch, "E2618", {"start": v(90.64, 33.57) * mm, "end": v(90.51, 33.05) * mm});
            skLineSegment(sketch, "E2619", {"start": v(90.51, 33.05) * mm, "end": v(90.46, 32.52) * mm});
            skLineSegment(sketch, "E2620", {"start": v(90.46, 32.52) * mm, "end": v(90.45, 25.42) * mm});
            skLineSegment(sketch, "E2621", {"start": v(90.45, 25.42) * mm, "end": v(90.45, 21.08) * mm});
            skLineSegment(sketch, "E2622", {"start": v(90.45, 21.08) * mm, "end": v(90.45, 16.22) * mm});
            skLineSegment(sketch, "E2623", {"start": v(90.45, 16.22) * mm, "end": v(90.45, 7.9) * mm});
            skLineSegment(sketch, "E2624", {"start": v(90.45, 7.9) * mm, "end": v(90.48, 7.28) * mm});
            skLineSegment(sketch, "E2625", {"start": v(90.48, 7.28) * mm, "end": v(90.58, 6.65) * mm});
            skLineSegment(sketch, "E2626", {"start": v(90.58, 6.65) * mm, "end": v(90.73, 6.04) * mm});
            skLineSegment(sketch, "E2627", {"start": v(90.73, 6.04) * mm, "end": v(91.17, 4.87) * mm});
            skLineSegment(sketch, "E2628", {"start": v(91.17, 4.87) * mm, "end": v(105.73, 4.72) * mm});
            skLineSegment(sketch, "E2629", {"start": v(105.73, 4.72) * mm, "end": v(105.73, 1.72) * mm});
            skLineSegment(sketch, "E2630", {"start": v(105.73, 1.72) * mm, "end": v(92.57, 1.72) * mm});
            skLineSegment(sketch, "E2631", {"start": v(92.57, 1.72) * mm, "end": v(94.02, -2.86) * mm});
            skLineSegment(sketch, "E2632", {"start": v(94.02, -2.86) * mm, "end": v(94.85, -5.23) * mm});
            skLineSegment(sketch, "E2633", {"start": v(94.85, -5.23) * mm, "end": v(96.5, -10.33) * mm});
            skLineSegment(sketch, "E2634", {"start": v(96.5, -10.33) * mm, "end": v(97.3, -12.9) * mm});
            skLineSegment(sketch, "E2635", {"start": v(97.3, -12.9) * mm, "end": v(98.45, -16.84) * mm});
            skLineSegment(sketch, "E2636", {"start": v(98.45, -16.84) * mm, "end": v(99.58, -20.9) * mm});
            skLineSegment(sketch, "E2637", {"start": v(99.58, -20.9) * mm, "end": v(100, -22.59) * mm});
            skLineSegment(sketch, "E2638", {"start": v(100, -22.59) * mm, "end": v(100.63, -25.13) * mm});
            skLineSegment(sketch, "E2639", {"start": v(100.63, -25.13) * mm, "end": v(101.27, -27.72) * mm});
            skLineSegment(sketch, "E2640", {"start": v(101.27, -27.72) * mm, "end": v(101.67, -29.4) * mm});
            skLineSegment(sketch, "E2641", {"start": v(101.67, -29.4) * mm, "end": v(110.86, -29.58) * mm});
            skLineSegment(sketch, "E2642", {"start": v(110.86, -29.58) * mm, "end": v(110.86, -32.58) * mm});
            skLineSegment(sketch, "E2643", {"start": v(110.86, -32.58) * mm, "end": v(102.53, -32.58) * mm});
            skLineSegment(sketch, "E2644", {"start": v(102.53, -32.58) * mm, "end": v(102.8, -34.78) * mm});
            skLineSegment(sketch, "E2645", {"start": v(102.8, -34.78) * mm, "end": v(103.16, -36.54) * mm});
            skLineSegment(sketch, "E2646", {"start": v(103.16, -36.54) * mm, "end": v(103.56, -38.6) * mm});
            skLineSegment(sketch, "E2647", {"start": v(103.56, -38.6) * mm, "end": v(103.88, -40.38) * mm});
            skLineSegment(sketch, "E2648", {"start": v(103.88, -40.38) * mm, "end": v(104.03, -41.3) * mm});
            skLineSegment(sketch, "E2649", {"start": v(104.03, -41.3) * mm, "end": v(104.47, -43.94) * mm});
            skLineSegment(sketch, "E2650", {"start": v(104.47, -43.94) * mm, "end": v(104.86, -46.4) * mm});
            skLineSegment(sketch, "E2651", {"start": v(104.86, -46.4) * mm, "end": v(105, -47.24) * mm});
            skLineSegment(sketch, "E2652", {"start": v(105, -47.24) * mm, "end": v(105.27, -49.08) * mm});
            skLineSegment(sketch, "E2653", {"start": v(105.27, -49.08) * mm, "end": v(105.44, -50.32) * mm});
            skLineSegment(sketch, "E2654", {"start": v(105.44, -50.32) * mm, "end": v(105.8, -53.23) * mm});
            skLineSegment(sketch, "E2655", {"start": v(105.8, -53.23) * mm, "end": v(105.93, -54.35) * mm});
            skLineSegment(sketch, "E2656", {"start": v(105.93, -54.35) * mm, "end": v(106.12, -55.98) * mm});
            skLineSegment(sketch, "E2657", {"start": v(106.12, -55.98) * mm, "end": v(106.3, -57.69) * mm});
            skLineSegment(sketch, "E2658", {"start": v(106.3, -57.69) * mm, "end": v(106.4, -58.59) * mm});
            skLineSegment(sketch, "E2659", {"start": v(106.4, -58.59) * mm, "end": v(106.61, -60.77) * mm});
            skLineSegment(sketch, "E2660", {"start": v(106.61, -60.77) * mm, "end": v(106.79, -62.67) * mm});
            skLineSegment(sketch, "E2661", {"start": v(106.79, -62.67) * mm, "end": v(106.85, -63.48) * mm});
            skLineSegment(sketch, "E2662", {"start": v(106.85, -63.48) * mm, "end": v(113.42, -63.88) * mm});
            skLineSegment(sketch, "E2663", {"start": v(113.42, -63.88) * mm, "end": v(113.42, -66.88) * mm});
            skLineSegment(sketch, "E2664", {"start": v(113.42, -66.88) * mm, "end": v(107.24, -66.88) * mm});
            skLineSegment(sketch, "E2665", {"start": v(107.24, -66.88) * mm, "end": v(107.15, -68.03) * mm});
            skLineSegment(sketch, "E2666", {"start": v(107.15, -68.03) * mm, "end": v(107.19, -68.62) * mm});
            skLineSegment(sketch, "E2667", {"start": v(107.19, -68.62) * mm, "end": v(107.27, -70.2) * mm});
            skLineSegment(sketch, "E2668", {"start": v(107.27, -70.2) * mm, "end": v(107.3, -70.97) * mm});
            skLineSegment(sketch, "E2669", {"start": v(107.3, -70.97) * mm, "end": v(107.37, -72.33) * mm});
            skLineSegment(sketch, "E2670", {"start": v(107.37, -72.33) * mm, "end": v(107.4, -73.23) * mm});
            skLineSegment(sketch, "E2671", {"start": v(107.4, -73.23) * mm, "end": v(107.45, -74.42) * mm});
            skLineSegment(sketch, "E2672", {"start": v(107.45, -74.42) * mm, "end": v(107.48, -75.42) * mm});
            skLineSegment(sketch, "E2673", {"start": v(107.48, -75.42) * mm, "end": v(107.5, -76.48) * mm});
            skLineSegment(sketch, "E2674", {"start": v(107.5, -76.48) * mm, "end": v(107.53, -77.55) * mm});
            skLineSegment(sketch, "E2675", {"start": v(107.53, -77.55) * mm, "end": v(107.55, -78.5) * mm});
            skLineSegment(sketch, "E2676", {"start": v(107.55, -78.5) * mm, "end": v(107.57, -79.62) * mm});
            skLineSegment(sketch, "E2677", {"start": v(107.57, -79.62) * mm, "end": v(107.58, -80.52) * mm});
            skLineSegment(sketch, "E2678", {"start": v(107.58, -80.52) * mm, "end": v(107.58, -81.66) * mm});
            skLineSegment(sketch, "E2679", {"start": v(107.58, -81.66) * mm, "end": v(107.59, -82.53) * mm});
            skLineSegment(sketch, "E2680", {"start": v(107.59, -82.53) * mm, "end": v(107.58, -83.66) * mm});
            skLineSegment(sketch, "E2681", {"start": v(107.58, -83.66) * mm, "end": v(107.58, -84.54) * mm});
            skLineSegment(sketch, "E2682", {"start": v(107.58, -84.54) * mm, "end": v(107.56, -85.65) * mm});
            skLineSegment(sketch, "E2683", {"start": v(107.56, -85.65) * mm, "end": v(107.55, -86.55) * mm});
            skLineSegment(sketch, "E2684", {"start": v(107.55, -86.55) * mm, "end": v(107.53, -87.62) * mm});
            skLineSegment(sketch, "E2685", {"start": v(107.53, -87.62) * mm, "end": v(107.5, -88.59) * mm});
            skLineSegment(sketch, "E2686", {"start": v(107.5, -88.59) * mm, "end": v(107.48, -89.58) * mm});
            skLineSegment(sketch, "E2687", {"start": v(107.48, -89.58) * mm, "end": v(107.45, -90.64) * mm});
            skLineSegment(sketch, "E2688", {"start": v(107.45, -90.64) * mm, "end": v(107.41, -91.55) * mm});
            skLineSegment(sketch, "E2689", {"start": v(107.41, -91.55) * mm, "end": v(107.37, -92.73) * mm});
            skLineSegment(sketch, "E2690", {"start": v(107.37, -92.73) * mm, "end": v(107.33, -93.52) * mm});
            skLineSegment(sketch, "E2691", {"start": v(107.33, -93.52) * mm, "end": v(107.27, -94.85) * mm});
            skLineSegment(sketch, "E2692", {"start": v(107.27, -94.85) * mm, "end": v(107.24, -95.52) * mm});
            skLineSegment(sketch, "E2693", {"start": v(107.24, -95.52) * mm, "end": v(107.15, -97.03) * mm});
            skLineSegment(sketch, "E2694", {"start": v(107.15, -97.03) * mm, "end": v(107.1, -98.03) * mm});
            skLineSegment(sketch, "E2695", {"start": v(107.1, -98.03) * mm, "end": v(113.42, -98.18) * mm});
            skLineSegment(sketch, "E2696", {"start": v(113.42, -98.18) * mm, "end": v(113.42, -101.18) * mm});
            skLineSegment(sketch, "E2697", {"start": v(113.42, -101.18) * mm, "end": v(107.02, -101.18) * mm});
            skLineSegment(sketch, "E2698", {"start": v(107.02, -101.18) * mm, "end": v(106.84, -101.67) * mm});
            skLineSegment(sketch, "E2699", {"start": v(106.84, -101.67) * mm, "end": v(106.79, -102.39) * mm});
            skLineSegment(sketch, "E2700", {"start": v(106.79, -102.39) * mm, "end": v(106.66, -103.76) * mm});
            skLineSegment(sketch, "E2701", {"start": v(106.66, -103.76) * mm, "end": v(106.46, -105.86) * mm});
            skLineSegment(sketch, "E2702", {"start": v(106.46, -105.86) * mm, "end": v(106.4, -106.47) * mm});
            skLineSegment(sketch, "E2703", {"start": v(106.4, -106.47) * mm, "end": v(106.23, -108.03) * mm});
            skLineSegment(sketch, "E2704", {"start": v(106.23, -108.03) * mm, "end": v(106.12, -109.09) * mm});
            skLineSegment(sketch, "E2705", {"start": v(106.12, -109.09) * mm, "end": v(105.98, -110.26) * mm});
            skLineSegment(sketch, "E2706", {"start": v(105.98, -110.26) * mm, "end": v(105.8, -111.83) * mm});
            skLineSegment(sketch, "E2707", {"start": v(105.8, -111.83) * mm, "end": v(105.7, -112.57) * mm});
            skLineSegment(sketch, "E2708", {"start": v(105.7, -112.57) * mm, "end": v(105.44, -114.74) * mm});
            skLineSegment(sketch, "E2709", {"start": v(105.44, -114.74) * mm, "end": v(105.27, -115.98) * mm});
            skLineSegment(sketch, "E2710", {"start": v(105.27, -115.98) * mm, "end": v(105.06, -117.39) * mm});
            skLineSegment(sketch, "E2711", {"start": v(105.06, -117.39) * mm, "end": v(104.67, -119.85) * mm});
            skLineSegment(sketch, "E2712", {"start": v(104.67, -119.85) * mm, "end": v(104.47, -121.12) * mm});
            skLineSegment(sketch, "E2713", {"start": v(104.47, -121.12) * mm, "end": v(104.25, -122.43) * mm});
            skLineSegment(sketch, "E2714", {"start": v(104.25, -122.43) * mm, "end": v(103.88, -124.68) * mm});
            skLineSegment(sketch, "E2715", {"start": v(103.88, -124.68) * mm, "end": v(103.56, -126.45) * mm});
            skLineSegment(sketch, "E2716", {"start": v(103.56, -126.45) * mm, "end": v(103.28, -127.88) * mm});
            skLineSegment(sketch, "E2717", {"start": v(103.28, -127.88) * mm, "end": v(103.16, -128.53) * mm});
            skLineSegment(sketch, "E2718", {"start": v(103.16, -128.53) * mm, "end": v(102.71, -130.69) * mm});
            skLineSegment(sketch, "E2719", {"start": v(102.71, -130.69) * mm, "end": v(102.38, -132.33) * mm});
            skLineSegment(sketch, "E2720", {"start": v(102.38, -132.33) * mm, "end": v(110.86, -132.48) * mm});
            skLineSegment(sketch, "E2721", {"start": v(110.86, -132.48) * mm, "end": v(110.86, -135.48) * mm});
            skLineSegment(sketch, "E2722", {"start": v(110.86, -135.48) * mm, "end": v(101.82, -135.48) * mm});
            skLineSegment(sketch, "E2723", {"start": v(101.82, -135.48) * mm, "end": v(101.42, -136.72) * mm});
            skLineSegment(sketch, "E2724", {"start": v(101.42, -136.72) * mm, "end": v(101.27, -137.35) * mm});
            skLineSegment(sketch, "E2725", {"start": v(101.27, -137.35) * mm, "end": v(100.66, -139.82) * mm});
            skLineSegment(sketch, "E2726", {"start": v(100.66, -139.82) * mm, "end": v(100, -142.47) * mm});
            skLineSegment(sketch, "E2727", {"start": v(100, -142.47) * mm, "end": v(99.85, -143.11) * mm});
            skLineSegment(sketch, "E2728", {"start": v(99.85, -143.11) * mm, "end": v(99.58, -144.16) * mm});
            skLineSegment(sketch, "E2729", {"start": v(99.58, -144.16) * mm, "end": v(98.94, -146.44) * mm});
            skLineSegment(sketch, "E2730", {"start": v(98.94, -146.44) * mm, "end": v(98.45, -148.22) * mm});
            skLineSegment(sketch, "E2731", {"start": v(98.45, -148.22) * mm, "end": v(97.96, -149.9) * mm});
            skLineSegment(sketch, "E2732", {"start": v(97.96, -149.9) * mm, "end": v(97.3, -152.17) * mm});
            skLineSegment(sketch, "E2733", {"start": v(97.3, -152.17) * mm, "end": v(96.9, -153.5) * mm});
            skLineSegment(sketch, "E2734", {"start": v(96.9, -153.5) * mm, "end": v(96.5, -154.73) * mm});
            skLineSegment(sketch, "E2735", {"start": v(96.5, -154.73) * mm, "end": v(95.72, -157.14) * mm});
            skLineSegment(sketch, "E2736", {"start": v(95.72, -157.14) * mm, "end": v(94.85, -159.83) * mm});
            skLineSegment(sketch, "E2737", {"start": v(94.85, -159.83) * mm, "end": v(94.46, -160.95) * mm});
            skLineSegment(sketch, "E2738", {"start": v(94.46, -160.95) * mm, "end": v(94.02, -162.2) * mm});
            skLineSegment(sketch, "E2739", {"start": v(94.02, -162.2) * mm, "end": v(93.08, -164.8) * mm});
            skLineSegment(sketch, "E2740", {"start": v(93.08, -164.8) * mm, "end": v(92.42, -166.63) * mm});
            skLineSegment(sketch, "E2741", {"start": v(92.42, -166.63) * mm, "end": v(105.73, -166.78) * mm});
            skLineSegment(sketch, "E2742", {"start": v(105.73, -166.78) * mm, "end": v(105.73, -169.78) * mm});
            skLineSegment(sketch, "E2743", {"start": v(105.73, -169.78) * mm, "end": v(91.31, -169.78) * mm});
            skLineSegment(sketch, "E2744", {"start": v(91.31, -169.78) * mm, "end": v(90.88, -170.66) * mm});
            skLineSegment(sketch, "E2745", {"start": v(90.88, -170.66) * mm, "end": v(90.7, -171.24) * mm});
            skLineSegment(sketch, "E2746", {"start": v(90.7, -171.24) * mm, "end": v(90.54, -171.88) * mm});
            skLineSegment(sketch, "E2747", {"start": v(90.54, -171.88) * mm, "end": v(90.46, -172.55) * mm});
            skLineSegment(sketch, "E2748", {"start": v(90.46, -172.55) * mm, "end": v(90.45, -178.61) * mm});
            skLineSegment(sketch, "E2749", {"start": v(90.45, -178.61) * mm, "end": v(90.45, -180.24) * mm});
            skLineSegment(sketch, "E2750", {"start": v(90.45, -180.24) * mm, "end": v(90.45, -184.58) * mm});
            skLineSegment(sketch, "E2751", {"start": v(90.45, -184.58) * mm, "end": v(90.45, -188.15) * mm});
            skLineSegment(sketch, "E2752", {"start": v(90.45, -188.15) * mm, "end": v(90.45, -195.77) * mm});
            skLineSegment(sketch, "E2753", {"start": v(90.45, -195.77) * mm, "end": v(90.45, -196.35) * mm});
            skLineSegment(sketch, "E2754", {"start": v(90.45, -196.35) * mm, "end": v(90.45, -197.36) * mm});
            skLineSegment(sketch, "E2755", {"start": v(90.45, -197.36) * mm, "end": v(90.48, -197.9) * mm});
            skLineSegment(sketch, "E2756", {"start": v(90.48, -197.9) * mm, "end": v(90.58, -198.42) * mm});
            skLineSegment(sketch, "E2757", {"start": v(90.58, -198.42) * mm, "end": v(90.74, -198.93) * mm});
            skLineSegment(sketch, "E2758", {"start": v(90.74, -198.93) * mm, "end": v(90.96, -199.41) * mm});
            skLineSegment(sketch, "E2759", {"start": v(90.96, -199.41) * mm, "end": v(91.24, -199.85) * mm});
            skLineSegment(sketch, "E2760", {"start": v(91.24, -199.85) * mm, "end": v(91.57, -200.26) * mm});
            skLineSegment(sketch, "E2761", {"start": v(91.57, -200.26) * mm, "end": v(91.95, -200.6) * mm});
            skLineSegment(sketch, "E2762", {"start": v(91.95, -200.6) * mm, "end": v(92.37, -200.9) * mm});
            skLineSegment(sketch, "E2763", {"start": v(92.37, -200.9) * mm, "end": v(107.81, -201.08) * mm});
            skLineSegment(sketch, "E2764", {"start": v(107.81, -201.08) * mm, "end": v(107.81, -204.08) * mm});
            skLineSegment(sketch, "E2765", {"start": v(107.81, -204.08) * mm, "end": v(103.56, -204.08) * mm});
            skLineSegment(sketch, "E2766", {"start": v(103.56, -204.08) * mm, "end": v(106.48, -205.1) * mm});
            skLineSegment(sketch, "E2767", {"start": v(106.48, -205.1) * mm, "end": v(111.97, -206.68) * mm});
            skLineSegment(sketch, "E2768", {"start": v(111.97, -206.68) * mm, "end": v(111.97, -210.4) * mm});
            skLineSegment(sketch, "E2769", {"start": v(111.97, -210.4) * mm, "end": v(111.97, -228.49) * mm});
            skLineSegment(sketch, "E2770", {"start": v(111.97, -228.49) * mm, "end": v(94.37, -229.42) * mm});
            skLineSegment(sketch, "E2771", {"start": v(94.37, -229.42) * mm, "end": v(93.82, -229.49) * mm});
            skLineSegment(sketch, "E2772", {"start": v(93.82, -229.49) * mm, "end": v(93.32, -229.61) * mm});
            skLineSegment(sketch, "E2773", {"start": v(93.32, -229.61) * mm, "end": v(92.84, -229.8) * mm});
            skLineSegment(sketch, "E2774", {"start": v(92.84, -229.8) * mm, "end": v(92.38, -230.05) * mm});
            skLineSegment(sketch, "E2775", {"start": v(92.38, -230.05) * mm, "end": v(91.96, -230.36) * mm});
            skLineSegment(sketch, "E2776", {"start": v(91.96, -230.36) * mm, "end": v(91.58, -230.72) * mm});
            skLineSegment(sketch, "E2777", {"start": v(91.58, -230.72) * mm, "end": v(91.24, -231.12) * mm});
            skLineSegment(sketch, "E2778", {"start": v(91.24, -231.12) * mm, "end": v(90.96, -231.56) * mm});
            skLineSegment(sketch, "E2779", {"start": v(90.96, -231.56) * mm, "end": v(90.74, -232.03) * mm});
            skLineSegment(sketch, "E2780", {"start": v(90.74, -232.03) * mm, "end": v(90.58, -232.53) * mm});
            skLineSegment(sketch, "E2781", {"start": v(90.58, -232.53) * mm, "end": v(90.48, -233.05) * mm});
            skLineSegment(sketch, "E2782", {"start": v(90.48, -233.05) * mm, "end": v(90.45, -233.55) * mm});
            skLineSegment(sketch, "E2783", {"start": v(90.45, -233.55) * mm, "end": v(90.45, -235.23) * mm});
            skLineSegment(sketch, "E2784", {"start": v(90.45, -235.23) * mm, "end": v(105.2, -235.38) * mm});
            skLineSegment(sketch, "E2785", {"start": v(105.2, -235.38) * mm, "end": v(105.2, -238.38) * mm});
            skLineSegment(sketch, "E2786", {"start": v(105.2, -238.38) * mm, "end": v(90.6, -238.38) * mm});
            skLineSegment(sketch, "E2787", {"start": v(90.6, -238.38) * mm, "end": v(90.45, -241.22) * mm});
            skLineSegment(sketch, "E2788", {"start": v(90.45, -241.22) * mm, "end": v(90.45, -242.06) * mm});
            skLineSegment(sketch, "E2789", {"start": v(90.45, -242.06) * mm, "end": v(90.47, -242.58) * mm});
            skLineSegment(sketch, "E2790", {"start": v(90.47, -242.58) * mm, "end": v(90.56, -243.08) * mm});
            skLineSegment(sketch, "E2791", {"start": v(90.56, -243.08) * mm, "end": v(90.71, -243.57) * mm});
            skLineSegment(sketch, "E2792", {"start": v(90.71, -243.57) * mm, "end": v(90.93, -244.04) * mm});
            skLineSegment(sketch, "E2793", {"start": v(90.93, -244.04) * mm, "end": v(91.2, -244.47) * mm});
            skLineSegment(sketch, "E2794", {"start": v(91.2, -244.47) * mm, "end": v(91.52, -244.87) * mm});
            skLineSegment(sketch, "E2795", {"start": v(91.52, -244.87) * mm, "end": v(91.89, -245.22) * mm});
            skLineSegment(sketch, "E2796", {"start": v(91.89, -245.22) * mm, "end": v(92.3, -245.52) * mm});
            skLineSegment(sketch, "E2797", {"start": v(92.3, -245.52) * mm, "end": v(92.75, -245.76) * mm});
            skLineSegment(sketch, "E2798", {"start": v(92.75, -245.76) * mm, "end": v(93.22, -245.94) * mm});
            skLineSegment(sketch, "E2799", {"start": v(93.22, -245.94) * mm, "end": v(93.72, -246.06) * mm});
            skLineSegment(sketch, "E2800", {"start": v(93.72, -246.06) * mm, "end": v(94.7, -246.16) * mm});
            skLineSegment(sketch, "E2801", {"start": v(94.7, -246.16) * mm, "end": v(119.97, -248.41) * mm});
            skLineSegment(sketch, "E2802", {"start": v(119.97, -248.41) * mm, "end": v(119.97, -126.54) * mm});
            skLineSegment(sketch, "E2803", {"start": v(119.97, -126.54) * mm, "end": v(119.97, -125) * mm});
            skLineSegment(sketch, "E2804", {"start": v(119.97, -125) * mm, "end": v(119.97, -123.41) * mm});
            skLineSegment(sketch, "E2805", {"start": v(119.97, -123.41) * mm, "end": v(119.97, -121.77) * mm});
            skLineSegment(sketch, "E2806", {"start": v(119.97, -121.77) * mm, "end": v(119.97, -120.08) * mm});
            skLineSegment(sketch, "E2807", {"start": v(119.97, -120.08) * mm, "end": v(119.97, -118.35) * mm});
            skLineSegment(sketch, "E2808", {"start": v(119.97, -118.35) * mm, "end": v(119.97, -116.58) * mm});
            skLineSegment(sketch, "E2809", {"start": v(119.97, -116.58) * mm, "end": v(119.97, -114.76) * mm});
            skLineSegment(sketch, "E2810", {"start": v(119.97, -114.76) * mm, "end": v(119.97, -112.92) * mm});
            skLineSegment(sketch, "E2811", {"start": v(119.97, -112.92) * mm, "end": v(119.97, -111.05) * mm});
            skLineSegment(sketch, "E2812", {"start": v(119.97, -111.05) * mm, "end": v(119.97, -109.16) * mm});
            skLineSegment(sketch, "E2813", {"start": v(119.97, -109.16) * mm, "end": v(119.97, -106.94) * mm});
            skLineSegment(sketch, "E2814", {"start": v(119.97, -106.94) * mm, "end": v(119.97, -105.03) * mm});
            skLineSegment(sketch, "E2815", {"start": v(119.97, -105.03) * mm, "end": v(119.97, -103.12) * mm});
            skLineSegment(sketch, "E2816", {"start": v(119.97, -103.12) * mm, "end": v(119.97, -101.21) * mm});
            skLineSegment(sketch, "E2817", {"start": v(119.97, -101.21) * mm, "end": v(119.97, -99.3) * mm});
            skLineSegment(sketch, "E2818", {"start": v(119.97, -99.3) * mm, "end": v(119.97, -97.41) * mm});
            skLineSegment(sketch, "E2819", {"start": v(119.97, -97.41) * mm, "end": v(119.97, -95.53) * mm});
            skLineSegment(sketch, "E2820", {"start": v(119.97, -95.53) * mm, "end": v(119.97, -93.68) * mm});
            skLineSegment(sketch, "E2821", {"start": v(119.97, -93.68) * mm, "end": v(119.97, -91.85) * mm});
            skLineSegment(sketch, "E2822", {"start": v(119.97, -91.85) * mm, "end": v(119.97, -90.05) * mm});
            skLineSegment(sketch, "E2823", {"start": v(119.97, -90.05) * mm, "end": v(119.97, -88.29) * mm});
            skLineSegment(sketch, "E2824", {"start": v(119.97, -88.29) * mm, "end": v(119.97, -86.58) * mm});
            skLineSegment(sketch, "E2825", {"start": v(119.97, -86.58) * mm, "end": v(119.97, -84.91) * mm});
            skLineSegment(sketch, "E2826", {"start": v(119.97, -84.91) * mm, "end": v(119.97, -76.77) * mm});
            skLineSegment(sketch, "E2827", {"start": v(119.97, -76.77) * mm, "end": v(119.97, -75.01) * mm});
            skLineSegment(sketch, "E2828", {"start": v(119.97, -75.01) * mm, "end": v(119.97, -73.22) * mm});
            skLineSegment(sketch, "E2829", {"start": v(119.97, -73.22) * mm, "end": v(119.97, -71.38) * mm});
            skLineSegment(sketch, "E2830", {"start": v(119.97, -71.38) * mm, "end": v(119.97, -69.53) * mm});
            skLineSegment(sketch, "E2831", {"start": v(119.97, -69.53) * mm, "end": v(119.97, -67.65) * mm});
            skLineSegment(sketch, "E2832", {"start": v(119.97, -67.65) * mm, "end": v(119.97, -65.75) * mm});
            skLineSegment(sketch, "E2833", {"start": v(119.97, -65.75) * mm, "end": v(119.97, -63.85) * mm});
            skLineSegment(sketch, "E2834", {"start": v(119.97, -63.85) * mm, "end": v(119.97, -61.94) * mm});
            skLineSegment(sketch, "E2835", {"start": v(119.97, -61.94) * mm, "end": v(119.97, -60.03) * mm});
            skLineSegment(sketch, "E2836", {"start": v(119.97, -60.03) * mm, "end": v(119.97, -58.13) * mm});
            skLineSegment(sketch, "E2837", {"start": v(119.97, -58.13) * mm, "end": v(119.97, -56.24) * mm});
            skLineSegment(sketch, "E2838", {"start": v(119.97, -56.24) * mm, "end": v(119.97, -55.98) * mm});
            skLineSegment(sketch, "E2839", {"start": v(138.3, -10.92) * mm, "end": v(138.3, -13.37) * mm});
            skLineSegment(sketch, "E2840", {"start": v(138.3, -13.37) * mm, "end": v(138.3, -16.56) * mm});
            skLineSegment(sketch, "E2841", {"start": v(138.3, -16.56) * mm, "end": v(138.3, -20.15) * mm});
            skLineSegment(sketch, "E2842", {"start": v(138.3, -20.15) * mm, "end": v(138.3, -24.13) * mm});
            skLineSegment(sketch, "E2843", {"start": v(138.3, -24.13) * mm, "end": v(138.3, -25.9) * mm});
            skLineSegment(sketch, "E2844", {"start": v(138.3, -25.9) * mm, "end": v(130.69, -29.84) * mm});
            skLineSegment(sketch, "E2845", {"start": v(130.69, -29.84) * mm, "end": v(129.55, -30.45) * mm});
            skLineSegment(sketch, "E2846", {"start": v(129.55, -30.45) * mm, "end": v(125.8, -32.54) * mm});
            skLineSegment(sketch, "E2847", {"start": v(125.8, -32.54) * mm, "end": v(125.35, -32.86) * mm});
            skLineSegment(sketch, "E2848", {"start": v(125.35, -32.86) * mm, "end": v(124.98, -33.24) * mm});
            skLineSegment(sketch, "E2849", {"start": v(124.98, -33.24) * mm, "end": v(124.66, -33.65) * mm});
            skLineSegment(sketch, "E2850", {"start": v(124.66, -33.65) * mm, "end": v(124.36, -34.14) * mm});
            skLineSegment(sketch, "E2851", {"start": v(124.36, -34.14) * mm, "end": v(124.07, -34.72) * mm});
            skLineSegment(sketch, "E2852", {"start": v(124.07, -34.72) * mm, "end": v(123.87, -35.21) * mm});
            skLineSegment(sketch, "E2853", {"start": v(123.87, -35.21) * mm, "end": v(123.7, -35.75) * mm});
            skLineSegment(sketch, "E2854", {"start": v(123.7, -35.75) * mm, "end": v(123.54, -36.3) * mm});
            skLineSegment(sketch, "E2855", {"start": v(123.54, -36.3) * mm, "end": v(123.41, -36.9) * mm});
            skLineSegment(sketch, "E2856", {"start": v(123.41, -36.9) * mm, "end": v(123.3, -37.53) * mm});
            skLineSegment(sketch, "E2857", {"start": v(123.3, -37.53) * mm, "end": v(123.23, -38.18) * mm});
            skLineSegment(sketch, "E2858", {"start": v(123.23, -38.18) * mm, "end": v(123.18, -38.84) * mm});
            skLineSegment(sketch, "E2859", {"start": v(123.18, -38.84) * mm, "end": v(123.15, -39.52) * mm});
            skLineSegment(sketch, "E2860", {"start": v(123.15, -39.52) * mm, "end": v(123.14, -41.92) * mm});
            skLineSegment(sketch, "E2861", {"start": v(123.14, -41.92) * mm, "end": v(134.72, -42.07) * mm});
            skLineSegment(sketch, "E2862", {"start": v(134.72, -42.07) * mm, "end": v(134.72, -45.07) * mm});
            skLineSegment(sketch, "E2863", {"start": v(134.72, -45.07) * mm, "end": v(123.3, -45.07) * mm});
            skLineSegment(sketch, "E2864", {"start": v(123.3, -45.07) * mm, "end": v(123.14, -48.65) * mm});
            skLineSegment(sketch, "E2865", {"start": v(123.14, -48.65) * mm, "end": v(123.14, -49.25) * mm});
            skLineSegment(sketch, "E2866", {"start": v(123.14, -49.25) * mm, "end": v(123.14, -54.26) * mm});
            skLineSegment(sketch, "E2867", {"start": v(123.14, -54.26) * mm, "end": v(123.14, -58.7) * mm});
            skLineSegment(sketch, "E2868", {"start": v(123.14, -58.7) * mm, "end": v(123.14, -59.81) * mm});
            skLineSegment(sketch, "E2869", {"start": v(123.14, -59.81) * mm, "end": v(123.14, -63.98) * mm});
            skLineSegment(sketch, "E2870", {"start": v(123.14, -63.98) * mm, "end": v(123.14, -65.31) * mm});
            skLineSegment(sketch, "E2871", {"start": v(123.14, -65.31) * mm, "end": v(123.14, -69.25) * mm});
            skLineSegment(sketch, "E2872", {"start": v(123.14, -69.25) * mm, "end": v(123.14, -70.75) * mm});
            skLineSegment(sketch, "E2873", {"start": v(123.14, -70.75) * mm, "end": v(123.14, -74.5) * mm});
            skLineSegment(sketch, "E2874", {"start": v(123.14, -74.5) * mm, "end": v(123.14, -76.13) * mm});
            skLineSegment(sketch, "E2875", {"start": v(123.14, -76.13) * mm, "end": v(134.72, -76.37) * mm});
            skLineSegment(sketch, "E2876", {"start": v(134.72, -76.37) * mm, "end": v(134.72, -79.37) * mm});
            skLineSegment(sketch, "E2877", {"start": v(134.72, -79.37) * mm, "end": v(123.3, -79.37) * mm});
            skLineSegment(sketch, "E2878", {"start": v(123.3, -79.37) * mm, "end": v(123.14, -81.45) * mm});
            skLineSegment(sketch, "E2879", {"start": v(123.14, -81.45) * mm, "end": v(123.14, -84.92) * mm});
            skLineSegment(sketch, "E2880", {"start": v(123.14, -84.92) * mm, "end": v(123.14, -88.28) * mm});
            skLineSegment(sketch, "E2881", {"start": v(123.14, -88.28) * mm, "end": v(123.14, -90.1) * mm});
            skLineSegment(sketch, "E2882", {"start": v(123.14, -90.1) * mm, "end": v(123.14, -93.42) * mm});
            skLineSegment(sketch, "E2883", {"start": v(123.14, -93.42) * mm, "end": v(123.14, -95.26) * mm});
            skLineSegment(sketch, "E2884", {"start": v(123.14, -95.26) * mm, "end": v(123.14, -98.57) * mm});
            skLineSegment(sketch, "E2885", {"start": v(123.14, -98.57) * mm, "end": v(123.14, -100.4) * mm});
            skLineSegment(sketch, "E2886", {"start": v(123.14, -100.4) * mm, "end": v(123.14, -103.73) * mm});
            skLineSegment(sketch, "E2887", {"start": v(123.14, -103.73) * mm, "end": v(123.14, -105.51) * mm});
            skLineSegment(sketch, "E2888", {"start": v(123.14, -105.51) * mm, "end": v(123.14, -108.9) * mm});
            skLineSegment(sketch, "E2889", {"start": v(123.14, -108.9) * mm, "end": v(123.14, -110.52) * mm});
            skLineSegment(sketch, "E2890", {"start": v(123.14, -110.52) * mm, "end": v(134.72, -110.67) * mm});
            skLineSegment(sketch, "E2891", {"start": v(134.72, -110.67) * mm, "end": v(134.72, -113.67) * mm});
            skLineSegment(sketch, "E2892", {"start": v(134.72, -113.67) * mm, "end": v(123.3, -113.67) * mm});
            skLineSegment(sketch, "E2893", {"start": v(123.3, -113.67) * mm, "end": v(123.14, -117.72) * mm});
            skLineSegment(sketch, "E2894", {"start": v(123.14, -117.72) * mm, "end": v(123.14, -119.26) * mm});
            skLineSegment(sketch, "E2895", {"start": v(123.14, -119.26) * mm, "end": v(123.14, -123.07) * mm});
            skLineSegment(sketch, "E2896", {"start": v(123.14, -123.07) * mm, "end": v(123.14, -124.44) * mm});
            skLineSegment(sketch, "E2897", {"start": v(123.14, -124.44) * mm, "end": v(123.14, -128.47) * mm});
            skLineSegment(sketch, "E2898", {"start": v(123.14, -128.47) * mm, "end": v(123.14, -129.63) * mm});
            skLineSegment(sketch, "E2899", {"start": v(123.14, -129.63) * mm, "end": v(123.14, -133.9) * mm});
            skLineSegment(sketch, "E2900", {"start": v(123.14, -133.9) * mm, "end": v(123.14, -134.82) * mm});
            skLineSegment(sketch, "E2901", {"start": v(123.14, -134.82) * mm, "end": v(123.14, -139.37) * mm});
            skLineSegment(sketch, "E2902", {"start": v(123.14, -139.37) * mm, "end": v(123.14, -140.02) * mm});
            skLineSegment(sketch, "E2903", {"start": v(123.14, -140.02) * mm, "end": v(123.14, -144.82) * mm});
            skLineSegment(sketch, "E2904", {"start": v(123.14, -144.82) * mm, "end": v(134.72, -144.97) * mm});
            skLineSegment(sketch, "E2905", {"start": v(134.72, -144.97) * mm, "end": v(134.72, -147.97) * mm});
            skLineSegment(sketch, "E2906", {"start": v(134.72, -147.97) * mm, "end": v(123.3, -147.97) * mm});
            skLineSegment(sketch, "E2907", {"start": v(123.3, -147.97) * mm, "end": v(123.14, -150.07) * mm});
            skLineSegment(sketch, "E2908", {"start": v(123.14, -150.07) * mm, "end": v(123.16, -150.79) * mm});
            skLineSegment(sketch, "E2909", {"start": v(123.16, -150.79) * mm, "end": v(123.2, -151.46) * mm});
            skLineSegment(sketch, "E2910", {"start": v(123.2, -151.46) * mm, "end": v(123.26, -152.13) * mm});
            skLineSegment(sketch, "E2911", {"start": v(123.26, -152.13) * mm, "end": v(123.35, -152.77) * mm});
            skLineSegment(sketch, "E2912", {"start": v(123.35, -152.77) * mm, "end": v(123.47, -153.4) * mm});
            skLineSegment(sketch, "E2913", {"start": v(123.47, -153.4) * mm, "end": v(123.62, -154) * mm});
            skLineSegment(sketch, "E2914", {"start": v(123.62, -154) * mm, "end": v(123.78, -154.56) * mm});
            skLineSegment(sketch, "E2915", {"start": v(123.78, -154.56) * mm, "end": v(123.97, -155.1) * mm});
            skLineSegment(sketch, "E2916", {"start": v(123.97, -155.1) * mm, "end": v(124.18, -155.59) * mm});
            skLineSegment(sketch, "E2917", {"start": v(124.18, -155.59) * mm, "end": v(124.52, -156.24) * mm});
            skLineSegment(sketch, "E2918", {"start": v(124.52, -156.24) * mm, "end": v(124.82, -156.67) * mm});
            skLineSegment(sketch, "E2919", {"start": v(124.82, -156.67) * mm, "end": v(125.2, -157.09) * mm});
            skLineSegment(sketch, "E2920", {"start": v(125.2, -157.09) * mm, "end": v(125.65, -157.43) * mm});
            skLineSegment(sketch, "E2921", {"start": v(125.65, -157.43) * mm, "end": v(130.69, -160.2) * mm});
            skLineSegment(sketch, "E2922", {"start": v(130.69, -160.2) * mm, "end": v(132.96, -161.4) * mm});
            skLineSegment(sketch, "E2923", {"start": v(132.96, -161.4) * mm, "end": v(138.3, -164.13) * mm});
            skLineSegment(sketch, "E2924", {"start": v(138.3, -164.13) * mm, "end": v(138.3, -166.6) * mm});
            skLineSegment(sketch, "E2925", {"start": v(138.3, -166.6) * mm, "end": v(138.3, -172.34) * mm});
            skLineSegment(sketch, "E2926", {"start": v(138.3, -172.34) * mm, "end": v(138.3, -177.69) * mm});
            skLineSegment(sketch, "E2927", {"start": v(138.3, -177.69) * mm, "end": v(138.3, -179.12) * mm});
            skLineSegment(sketch, "E2928", {"start": v(138.3, -179.12) * mm, "end": v(142.3, -179.27) * mm});
            skLineSegment(sketch, "E2929", {"start": v(142.3, -179.27) * mm, "end": v(142.3, -182.27) * mm});
            skLineSegment(sketch, "E2930", {"start": v(142.3, -182.27) * mm, "end": v(138.44, -182.27) * mm});
            skLineSegment(sketch, "E2931", {"start": v(138.44, -182.27) * mm, "end": v(138.3, -187.2) * mm});
            skLineSegment(sketch, "E2932", {"start": v(138.3, -187.2) * mm, "end": v(138.3, -191.38) * mm});
            skLineSegment(sketch, "E2933", {"start": v(138.3, -191.38) * mm, "end": v(138.3, -195.19) * mm});
            skLineSegment(sketch, "E2934", {"start": v(138.3, -195.19) * mm, "end": v(138.3, -198.62) * mm});
            skLineSegment(sketch, "E2935", {"start": v(138.3, -198.62) * mm, "end": v(138.3, -201.7) * mm});
            skLineSegment(sketch, "E2936", {"start": v(138.3, -201.7) * mm, "end": v(138.3, -204.46) * mm});
            skLineSegment(sketch, "E2937", {"start": v(138.3, -204.46) * mm, "end": v(138.3, -206.9) * mm});
            skLineSegment(sketch, "E2938", {"start": v(138.3, -206.9) * mm, "end": v(138.3, -209.03) * mm});
            skLineSegment(sketch, "E2939", {"start": v(138.3, -209.03) * mm, "end": v(138.3, -210.9) * mm});
            skLineSegment(sketch, "E2940", {"start": v(138.3, -210.9) * mm, "end": v(138.3, -212.48) * mm});
            skLineSegment(sketch, "E2941", {"start": v(138.3, -212.48) * mm, "end": v(138.3, -213.42) * mm});
            skLineSegment(sketch, "E2942", {"start": v(138.3, -213.42) * mm, "end": v(142.3, -213.57) * mm});
            skLineSegment(sketch, "E2943", {"start": v(142.3, -213.57) * mm, "end": v(142.3, -216.57) * mm});
            skLineSegment(sketch, "E2944", {"start": v(142.3, -216.57) * mm, "end": v(138.44, -216.57) * mm});
            skLineSegment(sketch, "E2945", {"start": v(138.44, -216.57) * mm, "end": v(138.3, -228.49) * mm});
            skLineSegment(sketch, "E2946", {"start": v(138.3, -228.49) * mm, "end": v(127.26, -229.07) * mm});
            skLineSegment(sketch, "E2947", {"start": v(127.26, -229.07) * mm, "end": v(126.7, -229.12) * mm});
            skLineSegment(sketch, "E2948", {"start": v(126.7, -229.12) * mm, "end": v(126.19, -229.22) * mm});
            skLineSegment(sketch, "E2949", {"start": v(126.19, -229.22) * mm, "end": v(125.7, -229.39) * mm});
            skLineSegment(sketch, "E2950", {"start": v(125.7, -229.39) * mm, "end": v(125.23, -229.62) * mm});
            skLineSegment(sketch, "E2951", {"start": v(125.23, -229.62) * mm, "end": v(124.8, -229.9) * mm});
            skLineSegment(sketch, "E2952", {"start": v(124.8, -229.9) * mm, "end": v(124.4, -230.25) * mm});
            skLineSegment(sketch, "E2953", {"start": v(124.4, -230.25) * mm, "end": v(124.05, -230.64) * mm});
            skLineSegment(sketch, "E2954", {"start": v(124.05, -230.64) * mm, "end": v(123.75, -231.07) * mm});
            skLineSegment(sketch, "E2955", {"start": v(123.75, -231.07) * mm, "end": v(123.5, -231.53) * mm});
            skLineSegment(sketch, "E2956", {"start": v(123.5, -231.53) * mm, "end": v(123.32, -232.02) * mm});
            skLineSegment(sketch, "E2957", {"start": v(123.32, -232.02) * mm, "end": v(123.2, -232.53) * mm});
            skLineSegment(sketch, "E2958", {"start": v(123.2, -232.53) * mm, "end": v(123.15, -233.05) * mm});
            skLineSegment(sketch, "E2959", {"start": v(123.15, -233.05) * mm, "end": v(123.14, -238.04) * mm});
            skLineSegment(sketch, "E2960", {"start": v(123.14, -238.04) * mm, "end": v(123.14, -242.65) * mm});
            skLineSegment(sketch, "E2961", {"start": v(123.14, -242.65) * mm, "end": v(123.17, -243.17) * mm});
            skLineSegment(sketch, "E2962", {"start": v(123.17, -243.17) * mm, "end": v(123.26, -243.67) * mm});
            skLineSegment(sketch, "E2963", {"start": v(123.26, -243.67) * mm, "end": v(123.42, -244.16) * mm});
            skLineSegment(sketch, "E2964", {"start": v(123.42, -244.16) * mm, "end": v(123.63, -244.63) * mm});
            skLineSegment(sketch, "E2965", {"start": v(123.63, -244.63) * mm, "end": v(123.9, -245.06) * mm});
            skLineSegment(sketch, "E2966", {"start": v(123.9, -245.06) * mm, "end": v(124.23, -245.45) * mm});
            skLineSegment(sketch, "E2967", {"start": v(124.23, -245.45) * mm, "end": v(124.6, -245.8) * mm});
            skLineSegment(sketch, "E2968", {"start": v(124.6, -245.8) * mm, "end": v(125.02, -246.1) * mm});
            skLineSegment(sketch, "E2969", {"start": v(125.02, -246.1) * mm, "end": v(125.46, -246.34) * mm});
            skLineSegment(sketch, "E2970", {"start": v(125.46, -246.34) * mm, "end": v(125.94, -246.52) * mm});
            skLineSegment(sketch, "E2971", {"start": v(125.94, -246.52) * mm, "end": v(126.44, -246.63) * mm});
            skLineSegment(sketch, "E2972", {"start": v(126.44, -246.63) * mm, "end": v(130.37, -247) * mm});
            skLineSegment(sketch, "E2973", {"start": v(130.37, -247) * mm, "end": v(146.3, -248.41) * mm});
            skLineSegment(sketch, "E2974", {"start": v(146.3, -248.41) * mm, "end": v(146.3, -171.66) * mm});
            skLineSegment(sketch, "E2975", {"start": v(146.3, -171.66) * mm, "end": v(146.3, -170.7) * mm});
            skLineSegment(sketch, "E2976", {"start": v(146.3, -170.7) * mm, "end": v(146.3, -169.69) * mm});
            skLineSegment(sketch, "E2977", {"start": v(146.3, -169.69) * mm, "end": v(146.3, -168.66) * mm});
            skLineSegment(sketch, "E2978", {"start": v(146.3, -168.66) * mm, "end": v(146.3, -167.6) * mm});
            skLineSegment(sketch, "E2979", {"start": v(146.3, -167.6) * mm, "end": v(146.3, -166.5) * mm});
            skLineSegment(sketch, "E2980", {"start": v(146.3, -166.5) * mm, "end": v(146.3, -165.38) * mm});
            skLineSegment(sketch, "E2981", {"start": v(146.3, -165.38) * mm, "end": v(146.3, -164.24) * mm});
            skLineSegment(sketch, "E2982", {"start": v(146.3, -164.24) * mm, "end": v(146.3, -163.08) * mm});
            skLineSegment(sketch, "E2983", {"start": v(146.3, -163.08) * mm, "end": v(146.3, -161.9) * mm});
            skLineSegment(sketch, "E2984", {"start": v(146.3, -161.9) * mm, "end": v(146.3, -160.71) * mm});
            skLineSegment(sketch, "E2985", {"start": v(146.3, -160.71) * mm, "end": v(146.3, -160.14) * mm});
            skLineSegment(sketch, "E2986", {"start": v(146.3, -160.14) * mm, "end": v(146.3, -159.6) * mm});
            skLineSegment(sketch, "E2987", {"start": v(146.3, -159.6) * mm, "end": v(146.3, -159.05) * mm});
            skLineSegment(sketch, "E2988", {"start": v(146.3, -159.05) * mm, "end": v(146.3, -158.5) * mm});
            skLineSegment(sketch, "E2989", {"start": v(146.3, -158.5) * mm, "end": v(146.3, -157.24) * mm});
            skLineSegment(sketch, "E2990", {"start": v(146.3, -157.24) * mm, "end": v(146.3, -155.96) * mm});
            skLineSegment(sketch, "E2991", {"start": v(146.3, -155.96) * mm, "end": v(146.3, -154.74) * mm});
            skLineSegment(sketch, "E2992", {"start": v(146.3, -154.74) * mm, "end": v(146.3, -153.53) * mm});
            skLineSegment(sketch, "E2993", {"start": v(146.3, -153.53) * mm, "end": v(146.3, -152.31) * mm});
            skLineSegment(sketch, "E2994", {"start": v(146.3, -152.31) * mm, "end": v(146.3, -151.1) * mm});
            skLineSegment(sketch, "E2995", {"start": v(146.3, -151.1) * mm, "end": v(146.3, -149.91) * mm});
            skLineSegment(sketch, "E2996", {"start": v(146.3, -149.91) * mm, "end": v(146.3, -148.73) * mm});
            skLineSegment(sketch, "E2997", {"start": v(146.3, -148.73) * mm, "end": v(146.3, -147.57) * mm});
            skLineSegment(sketch, "E2998", {"start": v(146.3, -147.57) * mm, "end": v(146.3, -146.42) * mm});
            skLineSegment(sketch, "E2999", {"start": v(146.3, -146.42) * mm, "end": v(146.3, -145.3) * mm});
            skLineSegment(sketch, "E3000", {"start": v(146.3, -145.3) * mm, "end": v(146.3, -144.21) * mm});
            skLineSegment(sketch, "E3001", {"start": v(146.3, -144.21) * mm, "end": v(146.3, -143.15) * mm});
            skLineSegment(sketch, "E3002", {"start": v(146.3, -143.15) * mm, "end": v(146.3, -44.74) * mm});
            skLineSegment(sketch, "E3003", {"start": v(146.3, -44.74) * mm, "end": v(146.3, -43.62) * mm});
            skLineSegment(sketch, "E3004", {"start": v(146.3, -43.62) * mm, "end": v(146.3, -42.48) * mm});
            skLineSegment(sketch, "E3005", {"start": v(146.3, -42.48) * mm, "end": v(146.3, -41.31) * mm});
            skLineSegment(sketch, "E3006", {"start": v(146.3, -41.31) * mm, "end": v(146.3, -40.13) * mm});
            skLineSegment(sketch, "E3007", {"start": v(146.3, -40.13) * mm, "end": v(146.3, -38.93) * mm});
            skLineSegment(sketch, "E3008", {"start": v(146.3, -38.93) * mm, "end": v(146.3, -37.73) * mm});
            skLineSegment(sketch, "E3009", {"start": v(146.3, -37.73) * mm, "end": v(146.3, -36.52) * mm});
            skLineSegment(sketch, "E3010", {"start": v(146.3, -36.52) * mm, "end": v(146.3, -35.3) * mm});
            skLineSegment(sketch, "E3011", {"start": v(146.3, -35.3) * mm, "end": v(146.3, -34.09) * mm});
            skLineSegment(sketch, "E3012", {"start": v(146.3, -34.09) * mm, "end": v(146.3, -32.88) * mm});
            skLineSegment(sketch, "E3013", {"start": v(146.3, -32.88) * mm, "end": v(146.3, -31.68) * mm});
            skLineSegment(sketch, "E3014", {"start": v(146.3, -31.68) * mm, "end": v(146.3, -31.16) * mm});
            skLineSegment(sketch, "E3015", {"start": v(146.3, -31.16) * mm, "end": v(146.3, -30.6) * mm});
            skLineSegment(sketch, "E3016", {"start": v(146.3, -30.6) * mm, "end": v(146.3, -30.05) * mm});
            skLineSegment(sketch, "E3017", {"start": v(146.3, -30.05) * mm, "end": v(146.3, -29.5) * mm});
            skLineSegment(sketch, "E3018", {"start": v(146.3, -29.5) * mm, "end": v(146.3, -28.2) * mm});
            skLineSegment(sketch, "E3019", {"start": v(146.3, -28.2) * mm, "end": v(146.3, -26.96) * mm});
            skLineSegment(sketch, "E3020", {"start": v(146.3, -26.96) * mm, "end": v(146.3, -25.8) * mm});
            skLineSegment(sketch, "E3021", {"start": v(146.3, -25.8) * mm, "end": v(146.3, -24.66) * mm});
            skLineSegment(sketch, "E3022", {"start": v(146.3, -24.66) * mm, "end": v(146.3, -23.54) * mm});
            skLineSegment(sketch, "E3023", {"start": v(146.3, -23.54) * mm, "end": v(146.3, -22.45) * mm});
            skLineSegment(sketch, "E3024", {"start": v(146.3, -22.45) * mm, "end": v(146.3, -21.39) * mm});
            skLineSegment(sketch, "E3025", {"start": v(146.3, -21.39) * mm, "end": v(146.3, -20.35) * mm});
            skLineSegment(sketch, "E3026", {"start": v(146.3, -20.35) * mm, "end": v(146.3, -19.35) * mm});
            skLineSegment(sketch, "E3027", {"start": v(146.3, -19.35) * mm, "end": v(146.3, -18.39) * mm});
            skLineSegment(sketch, "E3028", {"start": v(146.3, -18.39) * mm, "end": v(146.3, -17.46) * mm});
            skLineSegment(sketch, "E3029", {"start": v(146.3, -17.46) * mm, "end": v(146.3, 58.37) * mm});
            skLineSegment(sketch, "E3030", {"start": v(146.3, 58.37) * mm, "end": v(130.37, 56.95) * mm});
            skLineSegment(sketch, "E3031", {"start": v(130.37, 56.95) * mm, "end": v(126.74, 56.63) * mm});
            skLineSegment(sketch, "E3032", {"start": v(126.74, 56.63) * mm, "end": v(126.23, 56.55) * mm});
            skLineSegment(sketch, "E3033", {"start": v(126.23, 56.55) * mm, "end": v(125.73, 56.4) * mm});
            skLineSegment(sketch, "E3034", {"start": v(125.73, 56.4) * mm, "end": v(125.26, 56.2) * mm});
            skLineSegment(sketch, "E3035", {"start": v(125.26, 56.2) * mm, "end": v(124.82, 55.92) * mm});
            skLineSegment(sketch, "E3036", {"start": v(124.82, 55.92) * mm, "end": v(124.42, 55.6) * mm});
            skLineSegment(sketch, "E3037", {"start": v(124.42, 55.6) * mm, "end": v(124.06, 55.22) * mm});
            skLineSegment(sketch, "E3038", {"start": v(124.06, 55.22) * mm, "end": v(123.76, 54.8) * mm});
            skLineSegment(sketch, "E3039", {"start": v(123.76, 54.8) * mm, "end": v(123.51, 54.34) * mm});
            skLineSegment(sketch, "E3040", {"start": v(123.51, 54.34) * mm, "end": v(123.32, 53.86) * mm});
            skLineSegment(sketch, "E3041", {"start": v(123.32, 53.86) * mm, "end": v(123.2, 53.35) * mm});
            skLineSegment(sketch, "E3042", {"start": v(123.2, 53.35) * mm, "end": v(123.15, 52.83) * mm});
            skLineSegment(sketch, "E3043", {"start": v(123.15, 52.83) * mm, "end": v(123.14, 47.8) * mm});
            skLineSegment(sketch, "E3044", {"start": v(123.14, 47.8) * mm, "end": v(123.14, 43.18) * mm});
            skLineSegment(sketch, "E3045", {"start": v(123.14, 43.18) * mm, "end": v(123.18, 42.66) * mm});
            skLineSegment(sketch, "E3046", {"start": v(123.18, 42.66) * mm, "end": v(123.27, 42.15) * mm});
            skLineSegment(sketch, "E3047", {"start": v(123.27, 42.15) * mm, "end": v(123.43, 41.65) * mm});
            skLineSegment(sketch, "E3048", {"start": v(123.43, 41.65) * mm, "end": v(123.66, 41.18) * mm});
            skLineSegment(sketch, "E3049", {"start": v(123.66, 41.18) * mm, "end": v(123.94, 40.74) * mm});
            skLineSegment(sketch, "E3050", {"start": v(123.94, 40.74) * mm, "end": v(124.27, 40.33) * mm});
            skLineSegment(sketch, "E3051", {"start": v(124.27, 40.33) * mm, "end": v(124.65, 39.98) * mm});
            skLineSegment(sketch, "E3052", {"start": v(124.65, 39.98) * mm, "end": v(125.07, 39.67) * mm});
            skLineSegment(sketch, "E3053", {"start": v(125.07, 39.67) * mm, "end": v(125.53, 39.42) * mm});
            skLineSegment(sketch, "E3054", {"start": v(125.53, 39.42) * mm, "end": v(126, 39.23) * mm});
            skLineSegment(sketch, "E3055", {"start": v(126, 39.23) * mm, "end": v(126.5, 39.1) * mm});
            skLineSegment(sketch, "E3056", {"start": v(126.5, 39.1) * mm, "end": v(127.02, 39.04) * mm});
            skLineSegment(sketch, "E3057", {"start": v(127.02, 39.04) * mm, "end": v(138.3, 38.44) * mm});
            skLineSegment(sketch, "E3058", {"start": v(138.3, 38.44) * mm, "end": v(138.3, 26.68) * mm});
            skLineSegment(sketch, "E3059", {"start": v(138.3, 26.68) * mm, "end": v(142.3, 26.53) * mm});
            skLineSegment(sketch, "E3060", {"start": v(142.3, 26.53) * mm, "end": v(142.3, 23.53) * mm});
            skLineSegment(sketch, "E3061", {"start": v(142.3, 23.53) * mm, "end": v(138.44, 23.53) * mm});
            skLineSegment(sketch, "E3062", {"start": v(138.44, 23.53) * mm, "end": v(138.3, 10.78) * mm});
            skLineSegment(sketch, "E3063", {"start": v(138.3, 10.78) * mm, "end": v(138.3, 0.8) * mm});
            skLineSegment(sketch, "E3064", {"start": v(138.3, 0.8) * mm, "end": v(138.3, 0.1) * mm});
            skLineSegment(sketch, "E3065", {"start": v(138.3, 0.1) * mm, "end": v(138.3, -0.59) * mm});
            skLineSegment(sketch, "E3066", {"start": v(138.3, -0.59) * mm, "end": v(138.3, -1.52) * mm});
            skLineSegment(sketch, "E3067", {"start": v(138.3, -1.52) * mm, "end": v(138.3, -2.7) * mm});
            skLineSegment(sketch, "E3068", {"start": v(138.3, -2.7) * mm, "end": v(138.3, -4.19) * mm});
            skLineSegment(sketch, "E3069", {"start": v(138.3, -4.19) * mm, "end": v(138.3, -5.98) * mm});
            skLineSegment(sketch, "E3070", {"start": v(138.3, -5.98) * mm, "end": v(138.3, -7.62) * mm});
            skLineSegment(sketch, "E3071", {"start": v(138.3, -7.62) * mm, "end": v(142.3, -7.77) * mm});
            skLineSegment(sketch, "E3072", {"start": v(142.3, -7.77) * mm, "end": v(142.3, -10.77) * mm});
            skLineSegment(sketch, "E3073", {"start": v(142.3, -10.77) * mm, "end": v(138.44, -10.77) * mm});
            skLineSegment(sketch, "E3074", {"start": v(138.44, -10.77) * mm, "end": v(138.3, -10.92) * mm});
            skSolve(sketch);
        }
        {
            var Q0;
            Q0=makeQuery(id+"F0.imprint","IMPRINT",FACE,{"disambiguationData":[TD([[makeQuery(id+"F0.imprint","IMPRINT",EDGE,{"derivedFrom":sQuery(id+"F0.wireOp",EDGE,"E0")}),1.0]])]});
            var Q1;
            Q1=makeQuery(id+"F0.imprint","IMPRINT",FACE,{"disambiguationData":[TD([[makeQuery(id+"F0.imprint","IMPRINT",EDGE,{"derivedFrom":sQuery(id+"F0.wireOp",EDGE,"E369")}),1.0]])]});
            var Q2;
            Q2=makeQuery(id+"F0.imprint","IMPRINT",FACE,{"disambiguationData":[TD([[makeQuery(id+"F0.imprint","IMPRINT",EDGE,{"derivedFrom":sQuery(id+"F0.wireOp",EDGE,"E738")}),1.0]])]});
            var Q3;
            Q3=makeQuery(id+"F0.imprint","IMPRINT",FACE,{"disambiguationData":[TD([[makeQuery(id+"F0.imprint","IMPRINT",EDGE,{"derivedFrom":sQuery(id+"F0.wireOp",EDGE,"E1029")}),1.0]])]});
            var Q4;
            Q4=makeQuery(id+"F0.imprint","IMPRINT",FACE,{"disambiguationData":[TD([[makeQuery(id+"F0.imprint","IMPRINT",EDGE,{"derivedFrom":sQuery(id+"F0.wireOp",EDGE,"E1324")}),1.0]])]});
            var Q5;
            Q5=makeQuery(id+"F0.imprint","IMPRINT",FACE,{"disambiguationData":[TD([[makeQuery(id+"F0.imprint","IMPRINT",EDGE,{"derivedFrom":sQuery(id+"F0.wireOp",EDGE,"E1707")}),1.0]])]});
            var Q6;
            Q6=makeQuery(id+"F0.imprint","IMPRINT",FACE,{"disambiguationData":[TD([[makeQuery(id+"F0.imprint","IMPRINT",EDGE,{"derivedFrom":sQuery(id+"F0.wireOp",EDGE,"E2090")}),1.0]])]});
            var Q7;
            Q7=makeQuery(id+"F0.imprint","IMPRINT",FACE,{"disambiguationData":[TD([[makeQuery(id+"F0.imprint","IMPRINT",EDGE,{"derivedFrom":sQuery(id+"F0.wireOp",EDGE,"E2559")}),1.0]])]});
            var Q8;
            Q8=makeQuery(id+"F0.imprint","IMPRINT",FACE,{"disambiguationData":[TD([[makeQuery(id+"F0.imprint","IMPRINT",EDGE,{"derivedFrom":sQuery(id+"F0.wireOp",EDGE,"E2839")}),1.0]])]});
            var Q9;
            Q9=makeQuery(id+"F0.imprint","IMPRINT",FACE,{"disambiguationData":[TD([[makeQuery(id+"F0.imprint","IMPRINT",EDGE,{"derivedFrom":sQuery(id+"F0.wireOp",EDGE,"E1598")}),1.0]])]});
            var Q10;
            Q10=makeQuery(id+"F0.imprint","IMPRINT",FACE,{"disambiguationData":[TD([[makeQuery(id+"F0.imprint","IMPRINT",EDGE,{"derivedFrom":sQuery(id+"F0.wireOp",EDGE,"E1988")}),1.0]])]});
            var Q11;
            Q11=makeQuery(id+"F0.imprint","IMPRINT",FACE,{"disambiguationData":[TD([[makeQuery(id+"F0.imprint","IMPRINT",EDGE,{"derivedFrom":sQuery(id+"F0.wireOp",EDGE,"E2425")}),1.0]])]});
            extrude(context, id + "F1", {"entities" : qUnion([Q0, Q1, Q2, Q3, Q4, Q5, Q6, Q7, Q8, Q9, Q10, Q11]), "depth" : 3 * mm, "offsetDistance" : 25 * mm});
        }
    });
